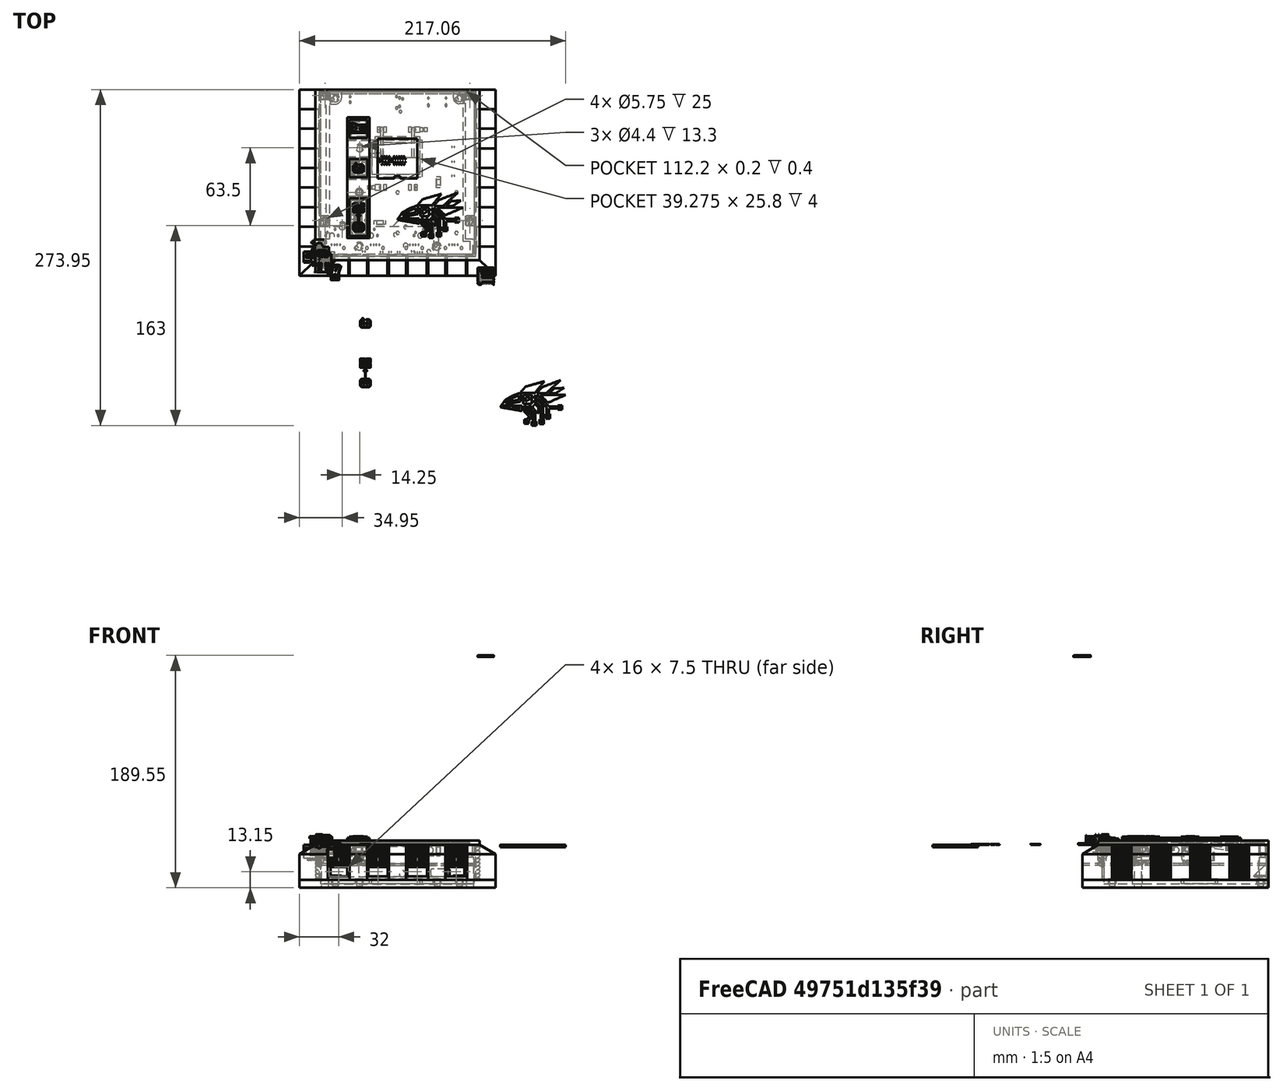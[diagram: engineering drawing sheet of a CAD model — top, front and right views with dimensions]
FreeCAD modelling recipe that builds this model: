
FCSTD DOCUMENT  (FreeCAD 1.0R39109 (Git))
Label: LegoCase_Konnexus_Mk1
License: All rights reserved
LicenseURL: http://en.wikipedia.org/wiki/All_rights_reserved
objects: Sketcher::SketchObject×154, PartDesign::Pad×122, Part::Feature×79, PartDesign::Body×69, App::Part×57, PartDesign::Pocket×45, PartDesign::SubShapeBinder×32, Part::Extrusion×20, Part::Cut×14, TechDraw::DrawViewDimension×11, PartDesign::FeatureBase×10, Mesh::Feature×9, Part::Scale×7, TechDraw::DrawSVGTemplate×6, PartDesign::Plane×6, TechDraw::DrawProjGroupItem×6, TechDraw::DrawPage×6, PartDesign::SubtractiveSphere×4, PartDesign::Groove×3, PartDesign::SubtractiveCylinder×3, +4 more types
note: 1118 computed .brp shape members not serialized (recipe doc carries the construction recipe); baked Part::Feature solids carry a one-line shape summary decoded from their .brp

FEATURE [Sketcher::SketchObject] Sketch
  ArcFitTolerance = 1e-06
  AttachmentSupport = -> [XY_Plane]
  FullyConstrained = true
  MakeInternals = false
  MapMode = 5
  sketch-geometry (4):
    g0: LineSegment StartX=0 StartY=0 StartZ=0 EndX=127.8 EndY=0 EndZ=0
    g1: LineSegment StartX=127.8 StartY=0 StartZ=0 EndX=127.8 EndY=135.8 EndZ=0
    g2: LineSegment StartX=127.8 StartY=135.8 StartZ=0 EndX=0 EndY=135.8 EndZ=0
    g3: LineSegment StartX=0 StartY=135.8 StartZ=0 EndX=0 EndY=0 EndZ=0
  constraints (11):
    c: Coincident(g0,g1)
    c: Coincident(g1,g2)
    c: Coincident(g2,g3)
    c: Coincident(g3,g0)
    c: Horizontal(g0)
    c: Horizontal(g2)
    c: Vertical(g1)
    c: Vertical(g3)
    c: Distance(g1,g3) = 127.8
    c: Distance(g0,g2) = 135.8
    c: Coincident(g0,g-1)
FEATURE [PartDesign::Pad] Pad
  Direction = (0,0,1)
  Length = 3.2
  Length2 = 10
  Profile = -> Sketch
  ReferenceAxis = -> Sketch [N_Axis]
  Refine = true
  Suppressed = false
  Type = 0
FEATURE [Sketcher::SketchObject] Sketch001
  ArcFitTolerance = 1e-06
  AttachmentSupport = -> [Pad]
  ExternalGeometry = -> [Pad]
  FullyConstrained = true
  MakeInternals = false
  MapMode = 5
  Placement = pos=(0,0,3.2) rot=(0,0,1;0rad)
  sketch-geometry (26):
    g0: LineSegment [constr] StartX=48 StartY=63.8 StartZ=0 EndX=79.8 EndY=63.8 EndZ=0
    g1: LineSegment [constr] StartX=79.8 StartY=63.8 StartZ=0 EndX=79.8 EndY=95.6 EndZ=0
    g2: LineSegment [constr] StartX=79.8 StartY=95.6 StartZ=0 EndX=48 EndY=95.6 EndZ=0
    g3: LineSegment [constr] StartX=48 StartY=95.6 StartZ=0 EndX=48 EndY=63.8 EndZ=0
    g4: LineSegment [constr] StartX=48 StartY=95.6 StartZ=0 EndX=79.8 EndY=63.8 EndZ=0
    g5: LineSegment [constr] StartX=48 StartY=63.8 StartZ=0 EndX=79.8 EndY=95.6 EndZ=0
    g6: GeomPoint [constr] X=63.9 Y=79.7 Z=0
    g7: LineSegment StartX=47.85 StartY=95.75 StartZ=0 EndX=47.85 EndY=63.65 EndZ=0
    g8: LineSegment StartX=47.85 StartY=63.65 StartZ=0 EndX=79.95 EndY=63.65 EndZ=0
    g9: LineSegment StartX=79.95 StartY=63.65 StartZ=0 EndX=79.95 EndY=95.75 EndZ=0
    g10: LineSegment StartX=79.95 StartY=95.75 StartZ=0 EndX=47.85 EndY=95.75 EndZ=0
    g11: LineSegment [constr] StartX=47.85 StartY=95.75 StartZ=0 EndX=79.95 EndY=63.65 EndZ=0
    g12: LineSegment [constr] StartX=47.85 StartY=63.65 StartZ=0 EndX=79.95 EndY=95.75 EndZ=0
    g13: LineSegment [constr] StartX=63.9 StartY=135.8 StartZ=0 EndX=63.9 EndY=0 EndZ=0
    g14: LineSegment StartX=24 StartY=111.8 StartZ=0 EndX=24 EndY=95.8 EndZ=0
    g15: LineSegment StartX=24 StartY=95.8 StartZ=0 EndX=40 EndY=95.8 EndZ=0
    g16: LineSegment StartX=40 StartY=95.8 StartZ=0 EndX=40 EndY=111.8 EndZ=0
    g17: LineSegment StartX=40 StartY=111.8 StartZ=0 EndX=24 EndY=111.8 EndZ=0
    g18: LineSegment StartX=24 StartY=79.8 StartZ=0 EndX=24 EndY=63.8 EndZ=0
    g19: LineSegment StartX=24 StartY=63.8 StartZ=0 EndX=40 EndY=63.8 EndZ=0
    g20: LineSegment StartX=40 StartY=63.8 StartZ=0 EndX=40 EndY=79.8 EndZ=0
    g21: LineSegment StartX=40 StartY=79.8 StartZ=0 EndX=24 EndY=79.8 EndZ=0
    g22: LineSegment StartX=24 StartY=47.8 StartZ=0 EndX=24 EndY=15.8 EndZ=0
    g23: LineSegment StartX=24 StartY=15.8 StartZ=0 EndX=40 EndY=15.8 EndZ=0
    g24: LineSegment StartX=40 StartY=15.8 StartZ=0 EndX=40 EndY=47.8 EndZ=0
    g25: LineSegment StartX=40 StartY=47.8 StartZ=0 EndX=24 EndY=47.8 EndZ=0
  constraints (72):
    c: Coincident(g0,g1)
    c: Coincident(g1,g2)
    c: Coincident(g2,g3)
    c: Coincident(g3,g0)
    c: Horizontal(g0)
    c: Horizontal(g2)
    c: Vertical(g1)
    c: Vertical(g3)
    c: Distance(g1,g3) = 31.8
    c: Distance(g0,g2) = 31.8
    c: Coincident(g4,g2)
    c: Coincident(g4,g0)
    c: Coincident(g5,g0)
    c: Coincident(g5,g1)
    c: PointOnObject(g6,g4)
    c: PointOnObject(g6,g5)
    c: Coincident(g7,g8)
    c: Coincident(g8,g9)
    c: Coincident(g9,g10)
    c: Coincident(g10,g7)
    c: Vertical(g7)
    c: Vertical(g9)
    c: Horizontal(g8)
    c: Horizontal(g10)
    c: Distance(g7,g9) = 32.1
    c: Distance(g8,g10) = 32.1
    c: Coincident(g11,g7)
    c: Coincident(g11,g8)
    c: Coincident(g12,g7)
    c: Coincident(g12,g9)
    c: PointOnObject(g6,g12)
    c: PointOnObject(g6,g11)
    c: Symmetric(g-3,g-3,g13)
    c: Symmetric(g-4,g-4,g13)
    c: PointOnObject(g6,g13)
    c: DistanceY(g-1,g0) = 63.8
    c: Coincident(g14,g15)
    c: Coincident(g15,g16)
    c: Coincident(g16,g17)
    c: Coincident(g17,g14)
    c: Vertical(g14)
    c: Vertical(g16)
    c: Horizontal(g15)
    c: Horizontal(g17)
    c: Distance(g14,g16) = 16
    c: Distance(g15,g17) = 16
    c: DistanceX(g-3,g14) = 24
    c: DistanceY(g14,g-3) = 24
    c: Coincident(g18,g19)
    c: Coincident(g19,g20)
    c: Coincident(g20,g21)
    c: Coincident(g21,g18)
    c: Vertical(g18)
    c: Vertical(g20)
    c: Horizontal(g19)
    c: Horizontal(g21)
    c: Distance(g18,g20) = 16
    c: Distance(g19,g21) = 16
    c: PointOnObject(g18,g14)
    c: DistanceY(g18,g14) = 16
    c: Coincident(g22,g23)
    c: Coincident(g23,g24)
    c: Coincident(g24,g25)
    c: Coincident(g25,g22)
    c: Vertical(g22)
    c: Vertical(g24)
    c: Horizontal(g23)
    c: Horizontal(g25)
    c: Distance(g22,g24) = 16
    c: Distance(g23,g25) = 32
    c: PointOnObject(g22,g18)
    c: DistanceY(g22,g18) = 16
FEATURE [PartDesign::Pocket] Pocket
  BaseFeature = -> Pad
  Direction = (0,0,-1)
  Length = 5
  Length2 = 5
  Profile = -> Sketch001
  ReferenceAxis = -> Sketch001 [N_Axis]
  Refine = true
  Suppressed = false
  Type = 0
FEATURE [PartDesign::SubShapeBinder] Binder
  BindCopyOnChange = 0
  BindMode = 0
  ClaimChildren = false
  Context = -> Part001 [Body001.Binder.]
  Fuse = false
  MakeFace = true
  OffsetFill = false
  OffsetIntersection = false
  OffsetJoinType = 0
  OffsetOpenResult = false
  PartialLoad = false
  Refine = true
  Relative = true
  Support = -> [Body]
  _Version = 2
FEATURE [Sketcher::SketchObject] Sketch002
  ArcFitTolerance = 1e-06
  AttachmentSupport = -> [Binder]
  ExternalGeometry = -> [Binder]
  FullyConstrained = true
  MakeInternals = false
  MapMode = 5
  Placement = pos=(0,0,-7.05e-14) rot=(1,0,0;3.14159rad)
  sketch-geometry (8):
    g0: LineSegment StartX=0 StartY=0 StartZ=0 EndX=0 EndY=-135.8 EndZ=0
    g1: LineSegment StartX=0 StartY=-135.8 StartZ=0 EndX=127.8 EndY=-135.8 EndZ=0
    g2: LineSegment StartX=127.8 StartY=-135.8 StartZ=0 EndX=127.8 EndY=0 EndZ=0
    g3: LineSegment StartX=127.8 StartY=0 StartZ=0 EndX=0 EndY=0 EndZ=0
    g4: LineSegment StartX=1.4 StartY=-1.4 StartZ=0 EndX=1.4 EndY=-134.4 EndZ=0
    g5: LineSegment StartX=1.4 StartY=-134.4 StartZ=0 EndX=126.4 EndY=-134.4 EndZ=0
    g6: LineSegment StartX=126.4 StartY=-134.4 StartZ=0 EndX=126.4 EndY=-1.4 EndZ=0
    g7: LineSegment StartX=126.4 StartY=-1.4 StartZ=0 EndX=1.4 EndY=-1.4 EndZ=0
  constraints (22):
    c: Coincident(g0,g1)
    c: Coincident(g1,g2)
    c: Coincident(g2,g3)
    c: Coincident(g3,g0)
    c: Vertical(g0)
    c: Vertical(g2)
    c: Horizontal(g1)
    c: Horizontal(g3)
    c: Coincident(g0,g-1)
    c: Coincident(g1,g-3)
    c: Coincident(g4,g5)
    c: Coincident(g5,g6)
    c: Coincident(g6,g7)
    c: Coincident(g7,g4)
    c: Vertical(g4)
    c: Vertical(g6)
    c: Horizontal(g5)
    c: Horizontal(g7)
    c: DistanceX(g0,g4) = 1.4
    c: DistanceY(g6,g2) = 1.4
    c: DistanceX(g5,g1) = 1.4
    c: DistanceY(g0,g4) = 1.4
FEATURE [PartDesign::Pad] Pad001
  Direction = (0,0,-1)
  Length = 32
  Length2 = 10
  Profile = -> Sketch002
  ReferenceAxis = -> Sketch002 [N_Axis]
  Refine = true
  Suppressed = false
  Type = 0
FEATURE [Sketcher::SketchObject] Sketch003
  ArcFitTolerance = 1e-06
  AttachmentSupport = -> [Pad001]
  ExternalGeometry = -> [Pad001]
  FullyConstrained = true
  MakeInternals = false
  MapMode = 5
  Placement = pos=(0,0,-32) rot=(1,0,0;3.14159rad)
  sketch-geometry (4):
    g0: LineSegment StartX=0 StartY=0 StartZ=0 EndX=0 EndY=-135.8 EndZ=0
    g1: LineSegment StartX=0 StartY=-135.8 StartZ=0 EndX=127.8 EndY=-135.8 EndZ=0
    g2: LineSegment StartX=127.8 StartY=-135.8 StartZ=0 EndX=127.8 EndY=0 EndZ=0
    g3: LineSegment StartX=127.8 StartY=0 StartZ=0 EndX=0 EndY=0 EndZ=0
  constraints (10):
    c: Coincident(g0,g1)
    c: Coincident(g1,g2)
    c: Coincident(g2,g3)
    c: Coincident(g3,g0)
    c: Vertical(g0)
    c: Vertical(g2)
    c: Horizontal(g1)
    c: Horizontal(g3)
    c: Coincident(g0,g-1)
    c: Coincident(g1,g-3)
FEATURE [PartDesign::Pad] Pad002
  BaseFeature = -> Pad001
  Direction = (0,0,-1)
  Length = 3.2
  Length2 = 10
  Profile = -> Sketch003
  ReferenceAxis = -> Sketch003 [N_Axis]
  Refine = true
  Suppressed = false
  Type = 0
FEATURE [Sketcher::SketchObject] Sketch004
  ArcFitTolerance = 1e-06
  AttachmentSupport = -> [Pad002]
  ExternalGeometry = -> [Pad002]
  FullyConstrained = true
  MakeInternals = false
  MapMode = 5
  Placement = pos=(0,0,-35.2) rot=(1,0,0;3.14159rad)
  sketch-geometry (14):
    g0: LineSegment [constr] StartX=0 StartY=0 StartZ=0 EndX=127.8 EndY=-135.8 EndZ=0
    g1: LineSegment [constr] StartX=127.8 StartY=0 StartZ=0 EndX=-4.4e-15 EndY=-135.8 EndZ=0
    g2: LineSegment StartX=0 StartY=0 StartZ=0 EndX=-4.4e-15 EndY=-135.8 EndZ=0
    g3: LineSegment StartX=127.8 StartY=-135.8 StartZ=0 EndX=127.8 EndY=0 EndZ=0
    g4: LineSegment StartX=-16 StartY=16 StartZ=0 EndX=-16 EndY=-135.8 EndZ=0
    g5: LineSegment StartX=143.8 StartY=-135.8 StartZ=0 EndX=143.8 EndY=16 EndZ=0
    g6: LineSegment [constr] StartX=-16 StartY=16 StartZ=0 EndX=143.8 EndY=-135.8 EndZ=0
    g7: LineSegment [constr] StartX=143.8 StartY=16 StartZ=0 EndX=-16 EndY=-135.8 EndZ=0
    g8: GeomPoint [constr] X=63.9 Y=-67.9 Z=0
    g9: GeomPoint X=63.9 Y=-59.9 Z=0
    g10: LineSegment StartX=-16 StartY=-135.8 StartZ=0 EndX=-3.6e-15 EndY=-135.8 EndZ=0
    g11: LineSegment StartX=127.8 StartY=-135.8 StartZ=0 EndX=143.8 EndY=-135.8 EndZ=0
    g12: LineSegment StartX=-16 StartY=16 StartZ=0 EndX=143.8 EndY=16 EndZ=0
    g13: LineSegment StartX=0 StartY=0 StartZ=0 EndX=127.8 EndY=0 EndZ=0
  constraints (32):
    c: Coincident(g0,g-1)
    c: Coincident(g0,g-3)
    c: Coincident(g1,g-3)
    c: Coincident(g1,g-4)
    c: Coincident(g2,g0)
    c: Vertical(g4)
    c: Vertical(g5)
    c: DistanceY(g4,g4) = 151.8
    c: Coincident(g7,g5)
    c: Coincident(g7,g4)
    c: PointOnObject(g8,g0)
    c: PointOnObject(g8,g1)
    c: PointOnObject(g9,g7)
    c: PointOnObject(g9,g6)
    c: Vertical(g9,g8)
    c: Coincident(g6,g4)
    c: DistanceX(g4,g5) = 159.8
    c: Coincident(g3,g1)
    c: Coincident(g6,g5)
    c: Coincident(g10,g4)
    c: Coincident(g10,g2)
    c: Coincident(g11,g3)
    c: Coincident(g11,g5)
    c: Horizontal(g10)
    c: Coincident(g1,g2)
    c: Horizontal(g11)
    c: Coincident(g12,g4)
    c: Coincident(g12,g5)
    c: Horizontal(g12)
    c: Coincident(g3,g0)
    c: Coincident(g13,g0)
    c: Coincident(g13,g1)
FEATURE [PartDesign::Pad] Pad003
  BaseFeature = -> Pad002
  Direction = (0,0,-1)
  Length = 6.4
  Length2 = 10
  Profile = -> Sketch004
  ReferenceAxis = -> Sketch004 [N_Axis]
  Refine = true
  Reversed = true
  Suppressed = false
  Type = 0
FEATURE [Sketcher::SketchObject] Sketch005
  ArcFitTolerance = 1e-06
  AttachmentSupport = -> [Pad003]
  ExternalGeometry = -> [Pad003]
  FullyConstrained = true
  MakeInternals = false
  MapMode = 5
  Placement = pos=(0,0,-28.8) rot=(0,0,1;0rad)
  sketch-geometry (32):
    g0: LineSegment StartX=127.8 StartY=24 StartZ=0 EndX=127.8 EndY=8 EndZ=0
    g1: LineSegment StartX=127.8 StartY=8 StartZ=0 EndX=143.8 EndY=8 EndZ=0
    g2: LineSegment StartX=143.8 StartY=8 StartZ=0 EndX=143.8 EndY=24 EndZ=0
    g3: LineSegment StartX=143.8 StartY=24 StartZ=0 EndX=127.8 EndY=24 EndZ=0
    g4: LineSegment StartX=127.8 StartY=56 StartZ=0 EndX=127.8 EndY=40 EndZ=0
    g5: LineSegment StartX=127.8 StartY=40 StartZ=0 EndX=143.8 EndY=40 EndZ=0
    g6: LineSegment StartX=143.8 StartY=40 StartZ=0 EndX=143.8 EndY=56 EndZ=0
    g7: LineSegment StartX=143.8 StartY=56 StartZ=0 EndX=127.8 EndY=56 EndZ=0
    g8: LineSegment StartX=127.8 StartY=88 StartZ=0 EndX=127.8 EndY=72 EndZ=0
    g9: LineSegment StartX=127.8 StartY=72 StartZ=0 EndX=143.8 EndY=72 EndZ=0
    g10: LineSegment StartX=143.8 StartY=72 StartZ=0 EndX=143.8 EndY=88 EndZ=0
    g11: LineSegment StartX=143.8 StartY=88 StartZ=0 EndX=127.8 EndY=88 EndZ=0
    g12: LineSegment StartX=127.8 StartY=120 StartZ=0 EndX=127.8 EndY=104 EndZ=0
    g13: LineSegment StartX=127.8 StartY=104 StartZ=0 EndX=143.8 EndY=104 EndZ=0
    g14: LineSegment StartX=143.8 StartY=104 StartZ=0 EndX=143.8 EndY=120 EndZ=0
    g15: LineSegment StartX=143.8 StartY=120 StartZ=0 EndX=127.8 EndY=120 EndZ=0
    g16: LineSegment StartX=-3.6e-15 StartY=120 StartZ=0 EndX=-16 EndY=120 EndZ=0
    g17: LineSegment StartX=-16 StartY=120 StartZ=0 EndX=-16 EndY=104 EndZ=0
    g18: LineSegment StartX=-16 StartY=104 StartZ=0 EndX=-3.6e-15 EndY=104 EndZ=0
    g19: LineSegment StartX=-3.6e-15 StartY=104 StartZ=0 EndX=-3.6e-15 EndY=120 EndZ=0
    g20: LineSegment StartX=-3.6e-15 StartY=88 StartZ=0 EndX=-16 EndY=88 EndZ=0
    g21: LineSegment StartX=-16 StartY=88 StartZ=0 EndX=-16 EndY=72 EndZ=0
    g22: LineSegment StartX=-16 StartY=72 StartZ=0 EndX=-3.6e-15 EndY=72 EndZ=0
    g23: LineSegment StartX=-3.6e-15 StartY=72 StartZ=0 EndX=-3.6e-15 EndY=88 EndZ=0
    g24: LineSegment StartX=-16 StartY=56 StartZ=0 EndX=-16 EndY=40 EndZ=0
    g25: LineSegment StartX=-16 StartY=40 StartZ=0 EndX=0 EndY=40 EndZ=0
    g26: LineSegment StartX=0 StartY=24 StartZ=0 EndX=-16 EndY=24 EndZ=0
    g27: LineSegment StartX=-16 StartY=24 StartZ=0 EndX=-16 EndY=8 EndZ=0
    g28: LineSegment StartX=-16 StartY=8 StartZ=0 EndX=0 EndY=8 EndZ=0
    g29: LineSegment StartX=0 StartY=8 StartZ=0 EndX=0 EndY=24 EndZ=0
    g30: LineSegment StartX=-16 StartY=56 StartZ=0 EndX=0 EndY=56 EndZ=0
    g31: LineSegment StartX=0 StartY=56 StartZ=0 EndX=0 EndY=40 EndZ=0
  constraints (96):
    c: Coincident(g0,g1)
    c: Coincident(g1,g2)
    c: Coincident(g2,g3)
    c: Coincident(g3,g0)
    c: Vertical(g0)
    c: Vertical(g2)
    c: Horizontal(g1)
    c: Horizontal(g3)
    c: PointOnObject(g0,g-5)
    c: PointOnObject(g1,g-4)
    c: DistanceY(g2,g2) = 16
    c: DistanceY(g-4,g1) = 24
    c: Coincident(g4,g5)
    c: Coincident(g5,g6)
    c: Coincident(g6,g7)
    c: Coincident(g7,g4)
    c: Vertical(g4)
    c: Vertical(g6)
    c: Horizontal(g5)
    c: Horizontal(g7)
    c: PointOnObject(g4,g-5)
    c: PointOnObject(g5,g-4)
    c: DistanceY(g6,g6) = 16
    c: DistanceY(g2,g5) = 16
    c: Coincident(g8,g9)
    c: Coincident(g9,g10)
    c: Coincident(g10,g11)
    c: Coincident(g11,g8)
    c: Vertical(g8)
    c: Vertical(g10)
    c: Horizontal(g9)
    c: Horizontal(g11)
    c: PointOnObject(g8,g-5)
    c: PointOnObject(g9,g-4)
    c: DistanceY(g10,g10) = 16
    c: DistanceY(g6,g9) = 16
    c: Coincident(g12,g13)
    c: Coincident(g13,g14)
    c: Coincident(g14,g15)
    c: Coincident(g15,g12)
    c: Vertical(g12)
    c: Vertical(g14)
    c: Horizontal(g13)
    c: Horizontal(g15)
    c: PointOnObject(g12,g-5)
    c: PointOnObject(g13,g-4)
    c: DistanceY(g14,g14) = 16
    c: DistanceY(g10,g13) = 16
    c: Coincident(g16,g17)
    c: Coincident(g17,g18)
    c: Coincident(g18,g19)
    c: Coincident(g19,g16)
    c: Horizontal(g16)
    c: Horizontal(g18)
    c: Vertical(g17)
    c: Vertical(g19)
    c: PointOnObject(g16,g-6)
    c: PointOnObject(g17,g-3)
    c: Coincident(g20,g21)
    c: Coincident(g21,g22)
    c: Coincident(g22,g23)
    c: Coincident(g23,g20)
    c: Horizontal(g20)
    c: Horizontal(g22)
    c: Vertical(g21)
    c: Vertical(g23)
    c: PointOnObject(g20,g-6)
    c: PointOnObject(g21,g-3)
    c: Coincident(g24,g25)
    c: Horizontal(g25)
    c: Vertical(g24)
    c: PointOnObject(g24,g-3)
    c: Coincident(g26,g27)
    c: Coincident(g27,g28)
    c: Coincident(g28,g29)
    c: Coincident(g29,g26)
    c: Horizontal(g26)
    c: Horizontal(g28)
    c: Vertical(g27)
    c: Vertical(g29)
    c: PointOnObject(g26,g-6)
    c: PointOnObject(g27,g-3)
    c: DistanceY(g27,g27) = 16
    c: DistanceY(g24,g24) = 16
    c: DistanceY(g21,g21) = 16
    c: DistanceY(g17,g17) = 16
    c: PointOnObject(g28,g1)
    c: PointOnObject(g25,g5)
    c: Coincident(g30,g24)
    c: PointOnObject(g30,g-6)
    c: Horizontal(g30)
    c: Coincident(g31,g30)
    c: Coincident(g31,g25)
    c: Vertical(g31)
    c: PointOnObject(g22,g9)
    c: PointOnObject(g18,g13)
FEATURE [PartDesign::Pad] Pad004
  BaseFeature = -> Pad003
  Direction = (0,0,1)
  Length = 19.2
  Length2 = 10
  Profile = -> Sketch005
  ReferenceAxis = -> Sketch005 [N_Axis]
  Refine = true
  Suppressed = false
  Type = 0
FEATURE [PartDesign::SubShapeBinder] Binder001
  BindCopyOnChange = 0
  BindMode = 0
  ClaimChildren = false
  Context = -> Part001 [Body002.Binder001.]
  Fuse = false
  MakeFace = true
  OffsetFill = false
  OffsetIntersection = false
  OffsetJoinType = 0
  OffsetOpenResult = false
  PartialLoad = false
  Refine = true
  Relative = true
  Support = -> [Body001]
  _Version = 2
FEATURE [Sketcher::SketchObject] Sketch006
  ArcFitTolerance = 1e-06
  AttachmentSupport = -> [Binder001]
  ExternalGeometry = -> [Binder001]
  FullyConstrained = true
  MakeInternals = false
  MapMode = 5
  Placement = pos=(0,0,-28.8) rot=(0,0,1;0rad)
  sketch-geometry (4):
    g0: LineSegment StartX=143.8 StartY=135.8 StartZ=0 EndX=127.8 EndY=135.8 EndZ=0
    g1: LineSegment StartX=127.8 StartY=135.8 StartZ=0 EndX=127.8 EndY=120 EndZ=0
    g2: LineSegment StartX=127.8 StartY=120 StartZ=0 EndX=143.8 EndY=120 EndZ=0
    g3: LineSegment StartX=143.8 StartY=120 StartZ=0 EndX=143.8 EndY=135.8 EndZ=0
  constraints (10):
    c: Coincident(g0,g1)
    c: Coincident(g1,g2)
    c: Coincident(g2,g3)
    c: Coincident(g3,g0)
    c: Horizontal(g0)
    c: Horizontal(g2)
    c: Vertical(g1)
    c: Vertical(g3)
    c: Coincident(g0,g-4)
    c: Coincident(g1,g-3)
FEATURE [PartDesign::Pad] Pad005
  Direction = (0,0,1)
  Length = 28.8
  Length2 = 10
  Profile = -> Sketch006
  ReferenceAxis = -> Sketch006 [N_Axis]
  Refine = true
  Suppressed = false
  Type = 0
FEATURE [Sketcher::SketchObject] Sketch007
  ArcFitTolerance = 1e-06
  AttachmentSupport = -> [Pad005]
  ExternalGeometry = -> [Pad005]
  FullyConstrained = true
  MakeInternals = false
  MapMode = 5
  Placement = pos=(0,120,0) rot=(1,0,0;1.5708rad)
  sketch-geometry (4):
    g0: LineSegment [constr] StartX=143.8 StartY=-9.6 StartZ=0 EndX=127.8 EndY=-9.6 EndZ=0
    g1: LineSegment StartX=127.8 StartY=-3.6e-15 StartZ=0 EndX=143.8 EndY=-9.6 EndZ=0
    g2: LineSegment StartX=127.8 StartY=-3.6e-15 StartZ=0 EndX=143.8 EndY=-3.6e-15 EndZ=0
    g3: LineSegment StartX=143.8 StartY=-3.6e-15 StartZ=0 EndX=143.8 EndY=-9.6 EndZ=0
  constraints (10):
    c: PointOnObject(g0,g-3)
    c: PointOnObject(g0,g-5)
    c: Horizontal(g0)
    c: Coincident(g1,g-5)
    c: Coincident(g1,g0)
    c: Coincident(g2,g1)
    c: Coincident(g2,g-4)
    c: Coincident(g3,g2)
    c: Coincident(g3,g0)
    c: DistanceY(g3,g3) = 9.6
FEATURE [PartDesign::Pocket] Pocket001
  BaseFeature = -> Pad005
  Direction = (0,1,-2e-16)
  Length = 16
  Length2 = 5
  Profile = -> Sketch007
  ReferenceAxis = -> Sketch007 [N_Axis]
  Refine = true
  Suppressed = false
  Type = 0
FEATURE [PartDesign::SubShapeBinder] Binder002
  BindCopyOnChange = 0
  BindMode = 0
  ClaimChildren = false
  Context = -> Part001 [Body003.Binder002.]
  Fuse = false
  MakeFace = true
  OffsetFill = false
  OffsetIntersection = false
  OffsetJoinType = 0
  OffsetOpenResult = false
  PartialLoad = false
  Refine = true
  Relative = true
  Support = -> [Body001]
  _Version = 2
FEATURE [Sketcher::SketchObject] Sketch008
  ArcFitTolerance = 1e-06
  AttachmentSupport = -> [Binder002]
  ExternalGeometry = -> [Binder002]
  FullyConstrained = true
  MakeInternals = false
  MapMode = 5
  Placement = pos=(0,0,-28.8) rot=(0,0,1;0rad)
  sketch-geometry (4):
    g0: LineSegment StartX=127.8 StartY=104 StartZ=0 EndX=127.8 EndY=88 EndZ=0
    g1: LineSegment StartX=127.8 StartY=88 StartZ=0 EndX=143.8 EndY=88 EndZ=0
    g2: LineSegment StartX=143.8 StartY=88 StartZ=0 EndX=143.8 EndY=104 EndZ=0
    g3: LineSegment StartX=143.8 StartY=104 StartZ=0 EndX=127.8 EndY=104 EndZ=0
  constraints (10):
    c: Coincident(g0,g1)
    c: Coincident(g1,g2)
    c: Coincident(g2,g3)
    c: Coincident(g3,g0)
    c: Vertical(g0)
    c: Vertical(g2)
    c: Horizontal(g1)
    c: Horizontal(g3)
    c: Coincident(g0,g-3)
    c: Coincident(g1,g-4)
FEATURE [PartDesign::Pad] Pad006
  Direction = (0,0,1)
  Length = 28.8
  Length2 = 10
  Profile = -> Sketch008
  ReferenceAxis = -> Sketch008 [N_Axis]
  Refine = true
  Suppressed = false
  Type = 0
FEATURE [Sketcher::SketchObject] Sketch009
  ArcFitTolerance = 1e-06
  AttachmentSupport = -> [Pad006]
  ExternalGeometry = -> [Pad006]
  FullyConstrained = true
  MakeInternals = false
  MapMode = 5
  Placement = pos=(0,88,0) rot=(1,0,0;1.5708rad)
  sketch-geometry (4):
    g0: LineSegment [constr] StartX=143.8 StartY=-9.6 StartZ=0 EndX=127.8 EndY=-9.6 EndZ=0
    g1: LineSegment StartX=143.8 StartY=-9.6 StartZ=0 EndX=127.8 EndY=-6.2e-15 EndZ=0
    g2: LineSegment StartX=127.8 StartY=-6.2e-15 StartZ=0 EndX=143.8 EndY=-3.6e-15 EndZ=0
    g3: LineSegment StartX=143.8 StartY=-3.6e-15 StartZ=0 EndX=143.8 EndY=-9.6 EndZ=0
  constraints (10):
    c: PointOnObject(g0,g-4)
    c: PointOnObject(g0,g-3)
    c: Horizontal(g0)
    c: Coincident(g0,g1)
    c: Coincident(g1,g-3)
    c: Coincident(g1,g2)
    c: Coincident(g2,g-4)
    c: Coincident(g2,g3)
    c: Coincident(g3,g1)
    c: DistanceY(g3,g3) = 9.6
FEATURE [PartDesign::Pocket] Pocket002
  BaseFeature = -> Pad006
  Direction = (0,1,-2e-16)
  Length = 16
  Length2 = 5
  Profile = -> Sketch009
  ReferenceAxis = -> Sketch009 [N_Axis]
  Refine = true
  Suppressed = false
  Type = 0
FEATURE [PartDesign::SubShapeBinder] Binder003
  BindCopyOnChange = 0
  BindMode = 0
  ClaimChildren = false
  Context = -> Part001 [Body004.Binder003.]
  Fuse = false
  MakeFace = true
  OffsetFill = false
  OffsetIntersection = false
  OffsetJoinType = 0
  OffsetOpenResult = false
  PartialLoad = false
  Refine = true
  Relative = true
  Support = -> [Body001]
  _Version = 2
FEATURE [Sketcher::SketchObject] Sketch010
  ArcFitTolerance = 1e-06
  AttachmentSupport = -> [Binder003]
  ExternalGeometry = -> [Binder003]
  FullyConstrained = true
  MakeInternals = false
  MapMode = 5
  Placement = pos=(0,0,-28.8) rot=(0,0,1;0rad)
  sketch-geometry (4):
    g0: LineSegment StartX=127.8 StartY=72 StartZ=0 EndX=127.8 EndY=56 EndZ=0
    g1: LineSegment StartX=127.8 StartY=56 StartZ=0 EndX=143.8 EndY=56 EndZ=0
    g2: LineSegment StartX=143.8 StartY=56 StartZ=0 EndX=143.8 EndY=72 EndZ=0
    g3: LineSegment StartX=143.8 StartY=72 StartZ=0 EndX=127.8 EndY=72 EndZ=0
  constraints (10):
    c: Coincident(g0,g1)
    c: Coincident(g1,g2)
    c: Coincident(g2,g3)
    c: Coincident(g3,g0)
    c: Vertical(g0)
    c: Vertical(g2)
    c: Horizontal(g1)
    c: Horizontal(g3)
    c: Coincident(g0,g-3)
    c: Coincident(g1,g-4)
FEATURE [PartDesign::Pad] Pad007
  Direction = (0,0,1)
  Length = 28.8
  Length2 = 10
  Profile = -> Sketch010
  ReferenceAxis = -> Sketch010 [N_Axis]
  Refine = true
  Suppressed = false
  Type = 0
FEATURE [Sketcher::SketchObject] Sketch011
  ArcFitTolerance = 1e-06
  AttachmentSupport = -> [Pad007]
  ExternalGeometry = -> [Pad007]
  FullyConstrained = true
  MakeInternals = false
  MapMode = 5
  Placement = pos=(0,56,0) rot=(1,0,0;1.5708rad)
  sketch-geometry (4):
    g0: LineSegment [constr] StartX=143.8 StartY=-9.6 StartZ=0 EndX=127.8 EndY=-9.6 EndZ=0
    g1: LineSegment StartX=143.8 StartY=-9.6 StartZ=0 EndX=127.8 EndY=-6e-16 EndZ=0
    g2: LineSegment StartX=143.8 StartY=-3.6e-15 StartZ=0 EndX=143.8 EndY=-9.6 EndZ=0
    g3: LineSegment StartX=127.8 StartY=-6e-16 StartZ=0 EndX=143.8 EndY=-3.6e-15 EndZ=0
  constraints (10):
    c: PointOnObject(g0,g-4)
    c: PointOnObject(g0,g-3)
    c: Horizontal(g0)
    c: Coincident(g1,g0)
    c: Coincident(g1,g-3)
    c: Coincident(g2,g-4)
    c: Coincident(g2,g0)
    c: Coincident(g3,g1)
    c: Coincident(g3,g2)
    c: DistanceY(g2,g2) = 9.6
FEATURE [PartDesign::Pocket] Pocket003
  BaseFeature = -> Pad007
  Direction = (0,1,-2e-16)
  Length = 16
  Length2 = 5
  Profile = -> Sketch011
  ReferenceAxis = -> Sketch011 [N_Axis]
  Refine = true
  Suppressed = false
  Type = 0
FEATURE [PartDesign::SubShapeBinder] Binder004
  BindCopyOnChange = 0
  BindMode = 0
  ClaimChildren = false
  Context = -> Part001 [Body005.Binder004.]
  Fuse = false
  MakeFace = true
  OffsetFill = false
  OffsetIntersection = false
  OffsetJoinType = 0
  OffsetOpenResult = false
  PartialLoad = false
  Refine = true
  Relative = true
  Support = -> [Body001]
  _Version = 2
FEATURE [Sketcher::SketchObject] Sketch012
  ArcFitTolerance = 1e-06
  AttachmentSupport = -> [Binder004]
  ExternalGeometry = -> [Binder004]
  FullyConstrained = true
  MakeInternals = false
  MapMode = 5
  Placement = pos=(0,0,-28.8) rot=(0,0,1;0rad)
  sketch-geometry (4):
    g0: LineSegment StartX=127.8 StartY=40 StartZ=0 EndX=127.8 EndY=24 EndZ=0
    g1: LineSegment StartX=127.8 StartY=24 StartZ=0 EndX=143.8 EndY=24 EndZ=0
    g2: LineSegment StartX=143.8 StartY=24 StartZ=0 EndX=143.8 EndY=40 EndZ=0
    g3: LineSegment StartX=143.8 StartY=40 StartZ=0 EndX=127.8 EndY=40 EndZ=0
  constraints (10):
    c: Coincident(g0,g1)
    c: Coincident(g1,g2)
    c: Coincident(g2,g3)
    c: Coincident(g3,g0)
    c: Vertical(g0)
    c: Vertical(g2)
    c: Horizontal(g1)
    c: Horizontal(g3)
    c: Coincident(g0,g-3)
    c: Coincident(g1,g-4)
FEATURE [PartDesign::Pad] Pad008
  Direction = (0,0,1)
  Length = 28.8
  Length2 = 10
  Profile = -> Sketch012
  ReferenceAxis = -> Sketch012 [N_Axis]
  Refine = true
  Suppressed = false
  Type = 0
FEATURE [Sketcher::SketchObject] Sketch013
  ArcFitTolerance = 1e-06
  AttachmentSupport = -> [Pad008]
  ExternalGeometry = -> [Pad008]
  FullyConstrained = true
  MakeInternals = false
  MapMode = 5
  Placement = pos=(0,24,0) rot=(1,0,0;1.5708rad)
  sketch-geometry (3):
    g0: LineSegment StartX=143.8 StartY=-9.6 StartZ=0 EndX=127.8 EndY=-4.5e-15 EndZ=0
    g1: LineSegment StartX=127.8 StartY=-4.5e-15 StartZ=0 EndX=143.8 EndY=-3.6e-15 EndZ=0
    g2: LineSegment StartX=143.8 StartY=-3.6e-15 StartZ=0 EndX=143.8 EndY=-9.6 EndZ=0
  constraints (7):
    c: PointOnObject(g0,g-4)
    c: Coincident(g0,g-3)
    c: Coincident(g1,g0)
    c: Coincident(g1,g-4)
    c: Coincident(g2,g1)
    c: DistanceY(g2,g2) = 9.6
    c: Coincident(g0,g2)
FEATURE [PartDesign::Pocket] Pocket004
  BaseFeature = -> Pad008
  Direction = (0,1,-2e-16)
  Length = 16
  Length2 = 5
  Profile = -> Sketch013
  ReferenceAxis = -> Sketch013 [N_Axis]
  Refine = true
  Suppressed = false
  Type = 0
FEATURE [PartDesign::SubShapeBinder] Binder005
  BindCopyOnChange = 0
  BindMode = 0
  ClaimChildren = false
  Context = -> Part001 [Body006.Binder005.]
  Fuse = false
  MakeFace = true
  OffsetFill = false
  OffsetIntersection = false
  OffsetJoinType = 0
  OffsetOpenResult = false
  PartialLoad = false
  Refine = true
  Relative = true
  Support = -> [Body001]
  _Version = 2
FEATURE [Sketcher::SketchObject] Sketch014
  ArcFitTolerance = 1e-06
  AttachmentSupport = -> [Binder005]
  ExternalGeometry = -> [Binder005]
  FullyConstrained = true
  MakeInternals = false
  MapMode = 5
  Placement = pos=(0,0,-28.8) rot=(0,0,1;0rad)
  sketch-geometry (6):
    g0: LineSegment StartX=127.8 StartY=0 StartZ=0 EndX=127.8 EndY=8 EndZ=0
    g1: LineSegment StartX=127.8 StartY=8 StartZ=0 EndX=143.8 EndY=8 EndZ=0
    g2: LineSegment StartX=143.8 StartY=8 StartZ=0 EndX=143.8 EndY=-16 EndZ=0
    g3: LineSegment StartX=143.8 StartY=-16 StartZ=0 EndX=119.8 EndY=-16 EndZ=0
    g4: LineSegment StartX=119.8 StartY=-16 StartZ=0 EndX=119.8 EndY=0 EndZ=0
    g5: LineSegment StartX=119.8 StartY=0 StartZ=0 EndX=127.8 EndY=0 EndZ=0
  constraints (14):
    c: Coincident(g-4,g0)
    c: Coincident(g0,g-4)
    c: Coincident(g0,g1)
    c: Coincident(g1,g-3)
    c: Coincident(g1,g2)
    c: Coincident(g2,g-3)
    c: Coincident(g2,g3)
    c: Horizontal(g3)
    c: Coincident(g3,g4)
    c: PointOnObject(g4,g-1)
    c: Vertical(g4)
    c: Coincident(g4,g5)
    c: Coincident(g5,g0)
    c: Equal(g5,g0)
FEATURE [PartDesign::Pad] Pad009
  Direction = (0,0,1)
  Length = 28.8
  Length2 = 10
  Profile = -> Sketch014
  ReferenceAxis = -> Sketch014 [N_Axis]
  Refine = true
  Suppressed = false
  Type = 0
FEATURE [Sketcher::SketchObject] Sketch015
  ArcFitTolerance = 1e-06
  AttachmentSupport = -> [Pad009]
  ExternalGeometry = -> [Pad009]
  FullyConstrained = true
  MakeInternals = false
  MapMode = 5
  Placement = pos=(119.8,0,0) rot=(0.57735,-0.57735,-0.57735;2.0944rad)
  sketch-geometry (4):
    g0: LineSegment [constr] StartX=16 StartY=-9.6 StartZ=0 EndX=0 EndY=-9.6 EndZ=0
    g1: LineSegment StartX=16 StartY=-9.6 StartZ=0 EndX=3e-16 EndY=-1.3e-15 EndZ=0
    g2: LineSegment StartX=3e-16 StartY=-1.3e-15 StartZ=0 EndX=16 EndY=-3.6e-15 EndZ=0
    g3: LineSegment StartX=16 StartY=-3.6e-15 StartZ=0 EndX=16 EndY=-9.6 EndZ=0
  constraints (10):
    c: PointOnObject(g0,g-3)
    c: PointOnObject(g0,g-4)
    c: Horizontal(g0)
    c: Coincident(g0,g1)
    c: Coincident(g1,g-1)
    c: Coincident(g1,g2)
    c: Coincident(g2,g-3)
    c: Coincident(g2,g3)
    c: Coincident(g3,g1)
    c: DistanceY(g3,g3) = 9.6
FEATURE [PartDesign::Pocket] Pocket005
  BaseFeature = -> Pad009
  Direction = (1,0,0)
  Length = 24
  Length2 = 5
  Profile = -> Sketch015
  ReferenceAxis = -> Sketch015 [N_Axis]
  Refine = true
  Suppressed = false
  Type = 0
FEATURE [Sketcher::SketchObject] Sketch016
  ArcFitTolerance = 1e-06
  AttachmentSupport = -> [Pocket005]
  ExternalGeometry = -> [Pocket005]
  FullyConstrained = true
  MakeInternals = false
  MapMode = 5
  Placement = pos=(0,8,0) rot=(0,0.707107,0.707107;3.14159rad)
  sketch-geometry (4):
    g0: LineSegment [constr] StartX=-143.8 StartY=-9.6 StartZ=0 EndX=-127.8 EndY=-9.6 EndZ=0
    g1: LineSegment StartX=-143.8 StartY=-9.6 StartZ=0 EndX=-127.8 EndY=-4.5e-15 EndZ=0
    g2: LineSegment StartX=-127.8 StartY=-4.5e-15 StartZ=0 EndX=-143.8 EndY=-3.6e-15 EndZ=0
    g3: LineSegment StartX=-143.8 StartY=-3.6e-15 StartZ=0 EndX=-143.8 EndY=-9.6 EndZ=0
  constraints (10):
    c: PointOnObject(g0,g-3)
    c: PointOnObject(g0,g-4)
    c: Horizontal(g0)
    c: Coincident(g1,g0)
    c: Coincident(g1,g-4)
    c: Coincident(g2,g1)
    c: Coincident(g2,g-3)
    c: Coincident(g3,g2)
    c: Coincident(g3,g0)
    c: DistanceY(g3,g3) = 9.6
FEATURE [PartDesign::Pocket] Pocket006
  BaseFeature = -> Pocket005
  Direction = (0,-1,2e-16)
  Length = 24
  Length2 = 5
  Profile = -> Sketch016
  ReferenceAxis = -> Sketch016 [N_Axis]
  Refine = true
  Suppressed = false
  Type = 0
FEATURE [PartDesign::SubShapeBinder] Binder006
  BindCopyOnChange = 0
  BindMode = 0
  ClaimChildren = false
  Context = -> Part001 [Body007.Binder006.]
  Fuse = false
  MakeFace = true
  OffsetFill = false
  OffsetIntersection = false
  OffsetJoinType = 0
  OffsetOpenResult = false
  PartialLoad = false
  Refine = true
  Relative = true
  Support = -> [Body001]
  _Version = 2
FEATURE [Sketcher::SketchObject] Sketch017
  ArcFitTolerance = 1e-06
  AttachmentSupport = -> [Binder006]
  ExternalGeometry = -> [Binder006]
  FullyConstrained = true
  MakeInternals = false
  MapMode = 5
  Placement = pos=(0,0,-28.8) rot=(0,0,1;0rad)
  sketch-geometry (4):
    g0: LineSegment StartX=0 StartY=135.8 StartZ=0 EndX=-16 EndY=135.8 EndZ=0
    g1: LineSegment StartX=-16 StartY=135.8 StartZ=0 EndX=-16 EndY=120 EndZ=0
    g2: LineSegment StartX=-16 StartY=120 StartZ=0 EndX=0 EndY=120 EndZ=0
    g3: LineSegment StartX=0 StartY=120 StartZ=0 EndX=0 EndY=135.8 EndZ=0
  constraints (10):
    c: Coincident(g0,g1)
    c: Coincident(g1,g2)
    c: Coincident(g2,g3)
    c: Coincident(g3,g0)
    c: Horizontal(g0)
    c: Horizontal(g2)
    c: Vertical(g1)
    c: Vertical(g3)
    c: Coincident(g0,g-3)
    c: Coincident(g1,g-4)
FEATURE [PartDesign::Pad] Pad010
  Direction = (0,0,1)
  Length = 28.8
  Length2 = 10
  Profile = -> Sketch017
  ReferenceAxis = -> Sketch017 [N_Axis]
  Refine = true
  Suppressed = false
  Type = 0
FEATURE [Sketcher::SketchObject] Sketch018
  ArcFitTolerance = 1e-06
  AttachmentSupport = -> [Pad010]
  ExternalGeometry = -> [Pad010]
  FullyConstrained = true
  MakeInternals = false
  MapMode = 5
  Placement = pos=(0,120,0) rot=(1,0,0;1.5708rad)
  sketch-geometry (3):
    g0: LineSegment StartX=0 StartY=0 StartZ=0 EndX=-16 EndY=-9.6 EndZ=0
    g1: LineSegment StartX=-16 StartY=-9.6 StartZ=0 EndX=-16 EndY=-3.6e-15 EndZ=0
    g2: LineSegment StartX=-16 StartY=-3.6e-15 StartZ=0 EndX=0 EndY=0 EndZ=0
  constraints (7):
    c: PointOnObject(g0,g-3)
    c: Coincident(g0,g-1)
    c: Coincident(g1,g-3)
    c: Coincident(g2,g1)
    c: Coincident(g2,g0)
    c: DistanceY(g1,g1) = 9.6
    c: Coincident(g0,g1)
FEATURE [PartDesign::Pocket] Pocket007
  BaseFeature = -> Pad010
  Direction = (0,1,-2e-16)
  Length = 16
  Length2 = 5
  Profile = -> Sketch018
  ReferenceAxis = -> Sketch018 [N_Axis]
  Refine = true
  Suppressed = false
  Type = 0
FEATURE [PartDesign::SubShapeBinder] Binder007
  BindCopyOnChange = 0
  BindMode = 0
  ClaimChildren = false
  Context = -> Part001 [Body008.Binder007.]
  Fuse = false
  MakeFace = true
  OffsetFill = false
  OffsetIntersection = false
  OffsetJoinType = 0
  OffsetOpenResult = false
  PartialLoad = false
  Refine = true
  Relative = true
  Support = -> [Body001]
  _Version = 2
FEATURE [Sketcher::SketchObject] Sketch019
  ArcFitTolerance = 1e-06
  AttachmentSupport = -> [Binder007]
  ExternalGeometry = -> [Binder007]
  FullyConstrained = true
  MakeInternals = false
  MapMode = 5
  Placement = pos=(0,0,-28.8) rot=(0,0,1;0rad)
  sketch-geometry (4):
    g0: LineSegment StartX=0 StartY=104 StartZ=0 EndX=-16 EndY=104 EndZ=0
    g1: LineSegment StartX=-16 StartY=104 StartZ=0 EndX=-16 EndY=88 EndZ=0
    g2: LineSegment StartX=-16 StartY=88 StartZ=0 EndX=0 EndY=88 EndZ=0
    g3: LineSegment StartX=0 StartY=88 StartZ=0 EndX=0 EndY=104 EndZ=0
  constraints (10):
    c: Coincident(g0,g1)
    c: Coincident(g1,g2)
    c: Coincident(g2,g3)
    c: Coincident(g3,g0)
    c: Horizontal(g0)
    c: Horizontal(g2)
    c: Vertical(g1)
    c: Vertical(g3)
    c: Coincident(g0,g-3)
    c: Coincident(g1,g-4)
FEATURE [PartDesign::Pad] Pad011
  Direction = (0,0,1)
  Length = 28.8
  Length2 = 10
  Profile = -> Sketch019
  ReferenceAxis = -> Sketch019 [N_Axis]
  Refine = true
  Suppressed = false
  Type = 0
FEATURE [Sketcher::SketchObject] Sketch020
  ArcFitTolerance = 1e-06
  AttachmentSupport = -> [Pad011]
  ExternalGeometry = -> [Pad011]
  FullyConstrained = true
  MakeInternals = false
  MapMode = 5
  Placement = pos=(0,88,0) rot=(1,0,0;1.5708rad)
  sketch-geometry (4):
    g0: LineSegment [constr] StartX=-16 StartY=-9.6 StartZ=0 EndX=0 EndY=-9.6 EndZ=0
    g1: LineSegment StartX=-16 StartY=-9.6 StartZ=0 EndX=-3e-16 EndY=7e-16 EndZ=0
    g2: LineSegment StartX=-3e-16 StartY=7e-16 StartZ=0 EndX=-16 EndY=-3.6e-15 EndZ=0
    g3: LineSegment StartX=-16 StartY=-3.6e-15 StartZ=0 EndX=-16 EndY=-9.6 EndZ=0
  constraints (10):
    c: PointOnObject(g0,g-3)
    c: PointOnObject(g0,g-4)
    c: Horizontal(g0)
    c: Coincident(g0,g1)
    c: Coincident(g1,g-1)
    c: Coincident(g1,g2)
    c: Coincident(g2,g-3)
    c: Coincident(g2,g3)
    c: Coincident(g3,g1)
    c: DistanceY(g3,g3) = 9.6
FEATURE [PartDesign::Pocket] Pocket008
  BaseFeature = -> Pad011
  Direction = (0,1,-2e-16)
  Length = 16
  Length2 = 5
  Profile = -> Sketch020
  ReferenceAxis = -> Sketch020 [N_Axis]
  Refine = true
  Suppressed = false
  Type = 0
FEATURE [PartDesign::SubShapeBinder] Binder008
  BindCopyOnChange = 0
  BindMode = 0
  ClaimChildren = false
  Context = -> Part001 [Body009.Binder008.]
  Fuse = false
  MakeFace = true
  OffsetFill = false
  OffsetIntersection = false
  OffsetJoinType = 0
  OffsetOpenResult = false
  PartialLoad = false
  Refine = true
  Relative = true
  Support = -> [Body001]
  _Version = 2
FEATURE [Sketcher::SketchObject] Sketch021
  ArcFitTolerance = 1e-06
  AttachmentSupport = -> [Binder008]
  ExternalGeometry = -> [Binder008]
  FullyConstrained = true
  MakeInternals = false
  MapMode = 5
  Placement = pos=(0,0,-28.8) rot=(0,0,1;0rad)
  sketch-geometry (4):
    g0: LineSegment StartX=0 StartY=72 StartZ=0 EndX=-16 EndY=72 EndZ=0
    g1: LineSegment StartX=-16 StartY=72 StartZ=0 EndX=-16 EndY=56 EndZ=0
    g2: LineSegment StartX=-16 StartY=56 StartZ=0 EndX=0 EndY=56 EndZ=0
    g3: LineSegment StartX=0 StartY=56 StartZ=0 EndX=0 EndY=72 EndZ=0
  constraints (10):
    c: Coincident(g0,g1)
    c: Coincident(g1,g2)
    c: Coincident(g2,g3)
    c: Coincident(g3,g0)
    c: Horizontal(g0)
    c: Horizontal(g2)
    c: Vertical(g1)
    c: Vertical(g3)
    c: Coincident(g0,g-3)
    c: Coincident(g1,g-4)
FEATURE [PartDesign::Pad] Pad012
  Direction = (0,0,1)
  Length = 28.8
  Length2 = 10
  Profile = -> Sketch021
  ReferenceAxis = -> Sketch021 [N_Axis]
  Refine = true
  Suppressed = false
  Type = 0
FEATURE [Sketcher::SketchObject] Sketch022
  ArcFitTolerance = 1e-06
  AttachmentSupport = -> [Pad012]
  ExternalGeometry = -> [Pad012]
  FullyConstrained = true
  MakeInternals = false
  MapMode = 5
  Placement = pos=(0,56,0) rot=(1,0,0;1.5708rad)
  sketch-geometry (4):
    g0: LineSegment [constr] StartX=-16 StartY=-9.6 StartZ=0 EndX=0 EndY=-9.6 EndZ=0
    g1: LineSegment StartX=-16 StartY=-9.6 StartZ=0 EndX=-3e-16 EndY=7e-16 EndZ=0
    g2: LineSegment StartX=-3e-16 StartY=7e-16 StartZ=0 EndX=-16 EndY=-3.6e-15 EndZ=0
    g3: LineSegment StartX=-16 StartY=-3.6e-15 StartZ=0 EndX=-16 EndY=-9.6 EndZ=0
  constraints (10):
    c: PointOnObject(g0,g-3)
    c: PointOnObject(g0,g-4)
    c: Horizontal(g0)
    c: Coincident(g0,g1)
    c: Coincident(g1,g-1)
    c: Coincident(g1,g2)
    c: Coincident(g2,g-3)
    c: Coincident(g2,g3)
    c: Coincident(g3,g1)
    c: DistanceY(g3,g3) = 9.6
FEATURE [PartDesign::Pocket] Pocket009
  BaseFeature = -> Pad012
  Direction = (0,1,-2e-16)
  Length = 16
  Length2 = 5
  Profile = -> Sketch022
  ReferenceAxis = -> Sketch022 [N_Axis]
  Refine = true
  Suppressed = false
  Type = 0
FEATURE [PartDesign::SubShapeBinder] Binder009
  BindCopyOnChange = 0
  BindMode = 0
  ClaimChildren = false
  Context = -> Part001 [Body010.Binder009.]
  Fuse = false
  MakeFace = true
  OffsetFill = false
  OffsetIntersection = false
  OffsetJoinType = 0
  OffsetOpenResult = false
  PartialLoad = false
  Refine = true
  Relative = true
  Support = -> [Body001]
  _Version = 2
FEATURE [Sketcher::SketchObject] Sketch023
  ArcFitTolerance = 1e-06
  AttachmentSupport = -> [Binder009]
  ExternalGeometry = -> [Binder009]
  FullyConstrained = true
  MakeInternals = false
  MapMode = 5
  Placement = pos=(0,0,-28.8) rot=(0,0,1;0rad)
  sketch-geometry (4):
    g0: LineSegment StartX=0 StartY=40 StartZ=0 EndX=-16 EndY=40 EndZ=0
    g1: LineSegment StartX=-16 StartY=40 StartZ=0 EndX=-16 EndY=24 EndZ=0
    g2: LineSegment StartX=-16 StartY=24 StartZ=0 EndX=0 EndY=24 EndZ=0
    g3: LineSegment StartX=0 StartY=24 StartZ=0 EndX=0 EndY=40 EndZ=0
  constraints (10):
    c: Coincident(g0,g1)
    c: Coincident(g1,g2)
    c: Coincident(g2,g3)
    c: Coincident(g3,g0)
    c: Horizontal(g0)
    c: Horizontal(g2)
    c: Vertical(g1)
    c: Vertical(g3)
    c: Coincident(g0,g-3)
    c: Coincident(g1,g-4)
FEATURE [PartDesign::Pad] Pad013
  Direction = (0,0,1)
  Length = 28.8
  Length2 = 10
  Profile = -> Sketch023
  ReferenceAxis = -> Sketch023 [N_Axis]
  Refine = true
  Suppressed = false
  Type = 0
FEATURE [Sketcher::SketchObject] Sketch024
  ArcFitTolerance = 1e-06
  AttachmentSupport = -> [Pad013]
  ExternalGeometry = -> [Pad013]
  FullyConstrained = true
  MakeInternals = false
  MapMode = 5
  Placement = pos=(0,24,0) rot=(1,0,0;1.5708rad)
  sketch-geometry (4):
    g0: LineSegment [constr] StartX=-16 StartY=-9.6 StartZ=0 EndX=0 EndY=-9.6 EndZ=0
    g1: LineSegment StartX=-16 StartY=-9.6 StartZ=0 EndX=-3e-16 EndY=7e-16 EndZ=0
    g2: LineSegment StartX=-3e-16 StartY=7e-16 StartZ=0 EndX=-16 EndY=-3.6e-15 EndZ=0
    g3: LineSegment StartX=-16 StartY=-3.6e-15 StartZ=0 EndX=-16 EndY=-9.6 EndZ=0
  constraints (10):
    c: PointOnObject(g0,g-3)
    c: PointOnObject(g0,g-4)
    c: Horizontal(g0)
    c: Coincident(g0,g1)
    c: Coincident(g1,g-1)
    c: Coincident(g1,g2)
    c: Coincident(g2,g-3)
    c: Coincident(g2,g3)
    c: Coincident(g3,g1)
    c: DistanceY(g3,g3) = 9.6
FEATURE [PartDesign::Pocket] Pocket010
  BaseFeature = -> Pad013
  Direction = (0,1,-2e-16)
  Length = 16
  Length2 = 5
  Profile = -> Sketch024
  ReferenceAxis = -> Sketch024 [N_Axis]
  Refine = true
  Suppressed = false
  Type = 0
FEATURE [PartDesign::SubShapeBinder] Binder010
  BindCopyOnChange = 0
  BindMode = 0
  ClaimChildren = false
  Context = -> Part001 [Body011.Binder010.]
  Fuse = false
  MakeFace = true
  OffsetFill = false
  OffsetIntersection = false
  OffsetJoinType = 0
  OffsetOpenResult = false
  PartialLoad = false
  Refine = true
  Relative = true
  Support = -> [Body001]
  _Version = 2
FEATURE [Sketcher::SketchObject] Sketch025
  ArcFitTolerance = 1e-06
  AttachmentSupport = -> [Binder010]
  ExternalGeometry = -> [Binder010]
  FullyConstrained = true
  MakeInternals = false
  MapMode = 5
  Placement = pos=(0,0,-28.8) rot=(0,0,1;0rad)
  sketch-geometry (6):
    g0: LineSegment StartX=0 StartY=0 StartZ=0 EndX=-2e-16 EndY=8 EndZ=0
    g1: LineSegment StartX=-2e-16 StartY=8 StartZ=0 EndX=-16 EndY=8 EndZ=0
    g2: LineSegment StartX=-16 StartY=8 StartZ=0 EndX=-16 EndY=-16 EndZ=0
    g3: LineSegment StartX=-16 StartY=-16 StartZ=0 EndX=8 EndY=-16 EndZ=0
    g4: LineSegment StartX=8 StartY=-16 StartZ=0 EndX=8 EndY=0 EndZ=0
    g5: LineSegment StartX=8 StartY=0 StartZ=0 EndX=0 EndY=0 EndZ=0
  constraints (14):
    c: Coincident(g-1,g0)
    c: Coincident(g0,g-4)
    c: Coincident(g0,g1)
    c: Coincident(g1,g-3)
    c: Coincident(g1,g2)
    c: Coincident(g2,g-3)
    c: Coincident(g2,g3)
    c: Horizontal(g3)
    c: Coincident(g3,g4)
    c: PointOnObject(g4,g-1)
    c: Vertical(g4)
    c: Coincident(g4,g5)
    c: Coincident(g5,g0)
    c: Equal(g5,g0)
FEATURE [PartDesign::Pad] Pad014
  Direction = (0,0,1)
  Length = 28.8
  Length2 = 10
  Profile = -> Sketch025
  ReferenceAxis = -> Sketch025 [N_Axis]
  Refine = true
  Suppressed = false
  Type = 0
FEATURE [Sketcher::SketchObject] Sketch026
  ArcFitTolerance = 1e-06
  AttachmentSupport = -> [Pad014]
  ExternalGeometry = -> [Pad014]
  FullyConstrained = true
  MakeInternals = false
  MapMode = 5
  Placement = pos=(8,0,0) rot=(0.57735,0.57735,0.57735;2.0944rad)
  sketch-geometry (3):
    g0: LineSegment StartX=-16 StartY=-9.6 StartZ=0 EndX=-3e-16 EndY=7e-16 EndZ=0
    g1: LineSegment StartX=-3e-16 StartY=7e-16 StartZ=0 EndX=-16 EndY=-3.6e-15 EndZ=0
    g2: LineSegment StartX=-16 StartY=-3.6e-15 StartZ=0 EndX=-16 EndY=-9.6 EndZ=0
  constraints (7):
    c: PointOnObject(g0,g-3)
    c: Coincident(g0,g-1)
    c: Coincident(g0,g1)
    c: Coincident(g1,g-3)
    c: Coincident(g1,g2)
    c: Coincident(g2,g0)
    c: DistanceY(g2,g2) = 9.6
FEATURE [PartDesign::Pocket] Pocket011
  BaseFeature = -> Pad014
  Direction = (-1,0,0)
  Length = 24
  Length2 = 5
  Profile = -> Sketch026
  ReferenceAxis = -> Sketch026 [N_Axis]
  Refine = true
  Suppressed = false
  Type = 0
FEATURE [Sketcher::SketchObject] Sketch027
  ArcFitTolerance = 1e-06
  AttachmentSupport = -> [Pocket011]
  ExternalGeometry = -> [Pocket011]
  FullyConstrained = true
  MakeInternals = false
  MapMode = 5
  Placement = pos=(1.4e-15,8,0) rot=(0,0.707107,0.707107;3.14159rad)
  sketch-geometry (4):
    g0: LineSegment [constr] StartX=16 StartY=-9.6 StartZ=0 EndX=1.8e-15 EndY=-9.6 EndZ=0
    g1: LineSegment StartX=16 StartY=-9.6 StartZ=0 EndX=3e-16 EndY=7e-16 EndZ=0
    g2: LineSegment StartX=3e-16 StartY=7e-16 StartZ=0 EndX=16 EndY=-3.6e-15 EndZ=0
    g3: LineSegment StartX=16 StartY=-3.6e-15 StartZ=0 EndX=16 EndY=-9.6 EndZ=0
  constraints (10):
    c: PointOnObject(g0,g-4)
    c: PointOnObject(g0,g-3)
    c: Horizontal(g0)
    c: Coincident(g0,g1)
    c: Coincident(g1,g-1)
    c: Coincident(g1,g2)
    c: Coincident(g2,g-4)
    c: Coincident(g2,g3)
    c: Coincident(g3,g1)
    c: DistanceY(g3,g3) = 9.6
FEATURE [PartDesign::Pocket] Pocket012
  BaseFeature = -> Pocket011
  Direction = (0,-1,2e-16)
  Length = 24
  Length2 = 5
  Profile = -> Sketch027
  ReferenceAxis = -> Sketch027 [N_Axis]
  Refine = true
  Suppressed = false
  Type = 0
FEATURE [PartDesign::SubShapeBinder] Binder011
  BindCopyOnChange = 0
  BindMode = 0
  ClaimChildren = false
  Context = -> Part001 [Body012.Binder011.]
  Fuse = false
  MakeFace = true
  OffsetFill = false
  OffsetIntersection = false
  OffsetJoinType = 0
  OffsetOpenResult = false
  PartialLoad = false
  Refine = true
  Relative = true
  Support = -> [Body001]
  _Version = 2
FEATURE [Sketcher::SketchObject] Sketch028
  ArcFitTolerance = 1e-06
  AttachmentSupport = -> [Binder011]
  ExternalGeometry = -> [Binder011]
  FullyConstrained = true
  MakeInternals = false
  MapMode = 5
  Placement = pos=(0,0,-28.8) rot=(0,0,1;0rad)
  expr: Constraints[11] = (24 + 16) * 1 mm
  sketch-geometry (4):
    g0: LineSegment StartX=24 StartY=0 StartZ=0 EndX=24 EndY=-16 EndZ=0
    g1: LineSegment StartX=24 StartY=-16 StartZ=0 EndX=40 EndY=-16 EndZ=0
    g2: LineSegment StartX=40 StartY=-16 StartZ=0 EndX=40 EndY=0 EndZ=0
    g3: LineSegment StartX=40 StartY=0 StartZ=0 EndX=24 EndY=0 EndZ=0
  constraints (12):
    c: Coincident(g0,g1)
    c: Coincident(g1,g2)
    c: Coincident(g2,g3)
    c: Coincident(g3,g0)
    c: Vertical(g0)
    c: Vertical(g2)
    c: Horizontal(g1)
    c: Horizontal(g3)
    c: PointOnObject(g0,g-4)
    c: PointOnObject(g1,g-3)
    c: DistanceX(g1,g1) = 16
    c: DistanceX(g-3,g0) = 40
FEATURE [PartDesign::Pad] Pad015
  Direction = (0,0,1)
  Length = 28.8
  Length2 = 10
  Profile = -> Sketch028
  ReferenceAxis = -> Sketch028 [N_Axis]
  Refine = true
  Suppressed = false
  Type = 0
FEATURE [Sketcher::SketchObject] Sketch029
  ArcFitTolerance = 1e-06
  AttachmentSupport = -> [Pad015]
  ExternalGeometry = -> [Pad015]
  FullyConstrained = true
  MakeInternals = false
  MapMode = 5
  Placement = pos=(40,0,0) rot=(0.57735,0.57735,0.57735;2.0944rad)
  sketch-geometry (3):
    g0: LineSegment StartX=-16 StartY=-3.6e-15 StartZ=0 EndX=-16 EndY=-9.6 EndZ=0
    g1: LineSegment StartX=-16 StartY=-9.6 StartZ=0 EndX=-3e-16 EndY=7e-16 EndZ=0
    g2: LineSegment StartX=-3e-16 StartY=7e-16 StartZ=0 EndX=-16 EndY=-3.6e-15 EndZ=0
  constraints (7):
    c: Coincident(g-3,g0)
    c: Vertical(g0)
    c: Coincident(g0,g1)
    c: Coincident(g1,g-1)
    c: Coincident(g1,g2)
    c: Coincident(g2,g0)
    c: DistanceY(g0,g0) = 9.6
FEATURE [PartDesign::Pocket] Pocket013
  BaseFeature = -> Pad015
  Direction = (-1,0,0)
  Length = 16
  Length2 = 5
  Profile = -> Sketch029
  ReferenceAxis = -> Sketch029 [N_Axis]
  Refine = true
  Suppressed = false
  Type = 0
FEATURE [PartDesign::SubShapeBinder] Binder012
  BindCopyOnChange = 0
  BindMode = 0
  ClaimChildren = false
  Context = -> Part001 [Body013.Binder012.]
  Fuse = false
  MakeFace = true
  OffsetFill = false
  OffsetIntersection = false
  OffsetJoinType = 0
  OffsetOpenResult = false
  PartialLoad = false
  Refine = true
  Relative = true
  Support = -> [Body001]
  _Version = 2
FEATURE [Sketcher::SketchObject] Sketch030
  ArcFitTolerance = 1e-06
  AttachmentSupport = -> [Binder012]
  ExternalGeometry = -> [Binder012]
  FullyConstrained = true
  MakeInternals = false
  MapMode = 5
  Placement = pos=(0,0,-28.8) rot=(0,0,1;0rad)
  expr: Constraints[11] = (24 + 16 + 16 + 16) * 1 mm
  sketch-geometry (4):
    g0: LineSegment StartX=56 StartY=-16 StartZ=0 EndX=72 EndY=-16 EndZ=0
    g1: LineSegment StartX=72 StartY=-16 StartZ=0 EndX=72 EndY=0 EndZ=0
    g2: LineSegment StartX=72 StartY=0 StartZ=0 EndX=56 EndY=0 EndZ=0
    g3: LineSegment StartX=56 StartY=0 StartZ=0 EndX=56 EndY=-16 EndZ=0
  constraints (12):
    c: Coincident(g0,g1)
    c: Coincident(g1,g2)
    c: Coincident(g2,g3)
    c: Coincident(g3,g0)
    c: Horizontal(g0)
    c: Horizontal(g2)
    c: Vertical(g1)
    c: Vertical(g3)
    c: PointOnObject(g0,g-4)
    c: PointOnObject(g1,g-3)
    c: DistanceX(g0,g0) = 16
    c: DistanceX(g-4,g0) = 72
FEATURE [PartDesign::Pad] Pad016
  Direction = (0,0,1)
  Length = 28.8
  Length2 = 10
  Profile = -> Sketch030
  ReferenceAxis = -> Sketch030 [N_Axis]
  Refine = true
  Suppressed = false
  Type = 0
FEATURE [Sketcher::SketchObject] Sketch031
  ArcFitTolerance = 1e-06
  AttachmentSupport = -> [Pad016]
  ExternalGeometry = -> [Pad016]
  FullyConstrained = true
  MakeInternals = false
  MapMode = 5
  Placement = pos=(72,0,0) rot=(0.57735,0.57735,0.57735;2.0944rad)
  sketch-geometry (3):
    g0: LineSegment StartX=-16 StartY=-3.6e-15 StartZ=0 EndX=-16 EndY=-9.6 EndZ=0
    g1: LineSegment StartX=-16 StartY=-9.6 StartZ=0 EndX=2e-16 EndY=0 EndZ=0
    g2: LineSegment StartX=2e-16 StartY=0 StartZ=0 EndX=-16 EndY=-3.6e-15 EndZ=0
  constraints (7):
    c: Coincident(g-3,g0)
    c: PointOnObject(g0,g-3)
    c: Coincident(g0,g1)
    c: Coincident(g1,g-1)
    c: Coincident(g1,g2)
    c: Coincident(g2,g0)
    c: DistanceY(g0,g0) = 9.6
FEATURE [PartDesign::Pocket] Pocket014
  BaseFeature = -> Pad016
  Direction = (-1,0,0)
  Length = 16
  Length2 = 5
  Profile = -> Sketch031
  ReferenceAxis = -> Sketch031 [N_Axis]
  Refine = true
  Suppressed = false
  Type = 0
FEATURE [PartDesign::SubShapeBinder] Binder013
  BindCopyOnChange = 0
  BindMode = 0
  ClaimChildren = false
  Context = -> Part001 [Body014.Binder013.]
  Fuse = false
  MakeFace = true
  OffsetFill = false
  OffsetIntersection = false
  OffsetJoinType = 0
  OffsetOpenResult = false
  PartialLoad = false
  Refine = true
  Relative = true
  Support = -> [Body001]
  _Version = 2
FEATURE [Sketcher::SketchObject] Sketch032
  ArcFitTolerance = 1e-06
  AttachmentSupport = -> [Binder013]
  ExternalGeometry = -> [Binder013]
  FullyConstrained = true
  MakeInternals = false
  MapMode = 5
  Placement = pos=(0,0,-28.8) rot=(0,0,1;0rad)
  expr: Constraints[11] = (24 + 16 + 16 + 16 + 16 + 16) * 1 mm
  sketch-geometry (4):
    g0: LineSegment StartX=88 StartY=-16 StartZ=0 EndX=104 EndY=-16 EndZ=0
    g1: LineSegment StartX=104 StartY=-16 StartZ=0 EndX=104 EndY=0 EndZ=0
    g2: LineSegment StartX=104 StartY=0 StartZ=0 EndX=88 EndY=0 EndZ=0
    g3: LineSegment StartX=88 StartY=0 StartZ=0 EndX=88 EndY=-16 EndZ=0
  constraints (12):
    c: Coincident(g0,g1)
    c: Coincident(g1,g2)
    c: Coincident(g2,g3)
    c: Coincident(g3,g0)
    c: Horizontal(g0)
    c: Horizontal(g2)
    c: Vertical(g1)
    c: Vertical(g3)
    c: PointOnObject(g0,g-3)
    c: PointOnObject(g1,g-4)
    c: DistanceX(g0,g0) = 16
    c: DistanceX(g-3,g0) = 104
FEATURE [PartDesign::Pad] Pad017
  Direction = (0,0,1)
  Length = 28.8
  Length2 = 10
  Profile = -> Sketch032
  ReferenceAxis = -> Sketch032 [N_Axis]
  Refine = true
  Suppressed = false
  Type = 0
FEATURE [Sketcher::SketchObject] Sketch033
  ArcFitTolerance = 1e-06
  AttachmentSupport = -> [Pad017]
  ExternalGeometry = -> [Pad017]
  FullyConstrained = true
  MakeInternals = false
  MapMode = 5
  Placement = pos=(104,0,0) rot=(0.57735,0.57735,0.57735;2.0944rad)
  sketch-geometry (3):
    g0: LineSegment StartX=-16 StartY=-3.6e-15 StartZ=0 EndX=-16 EndY=-9.6 EndZ=0
    g1: LineSegment StartX=-16 StartY=-9.6 StartZ=0 EndX=2e-16 EndY=0 EndZ=0
    g2: LineSegment StartX=2e-16 StartY=0 StartZ=0 EndX=-16 EndY=-3.6e-15 EndZ=0
  constraints (7):
    c: Coincident(g-3,g0)
    c: PointOnObject(g0,g-3)
    c: Coincident(g0,g1)
    c: Coincident(g1,g-1)
    c: Coincident(g1,g2)
    c: Coincident(g2,g0)
    c: DistanceY(g0,g0) = 9.6
FEATURE [PartDesign::Pocket] Pocket015
  BaseFeature = -> Pad017
  Direction = (-1,0,0)
  Length = 16
  Length2 = 5
  Profile = -> Sketch033
  ReferenceAxis = -> Sketch033 [N_Axis]
  Refine = true
  Suppressed = false
  Type = 0
FEATURE [Sketcher::SketchObject] Sketch034
  ArcFitTolerance = 1e-06
  AttachmentSupport = -> [Pad004]
  ExternalGeometry = -> [Pad004]
  FullyConstrained = true
  MakeInternals = false
  MapMode = 5
  Placement = pos=(0,0,-32) rot=(0,0,1;0rad)
  sketch-geometry (16):
    g0: LineSegment StartX=1.4 StartY=25 StartZ=0 EndX=8 EndY=25 EndZ=0
    g1: LineSegment StartX=8 StartY=25 StartZ=0 EndX=8 EndY=33 EndZ=0
    g2: LineSegment StartX=8 StartY=33 StartZ=0 EndX=1.4 EndY=33 EndZ=0
    g3: LineSegment StartX=1.4 StartY=33 StartZ=0 EndX=1.4 EndY=25 EndZ=0
    g4: LineSegment StartX=126.4 StartY=25 StartZ=0 EndX=126.4 EndY=33 EndZ=0
    g5: LineSegment StartX=126.4 StartY=33 StartZ=0 EndX=119.8 EndY=33 EndZ=0
    g6: LineSegment StartX=119.8 StartY=33 StartZ=0 EndX=119.8 EndY=25 EndZ=0
    g7: LineSegment StartX=119.8 StartY=25 StartZ=0 EndX=126.4 EndY=25 EndZ=0
    g8: LineSegment StartX=126.4 StartY=134.4 StartZ=0 EndX=119.8 EndY=134.4 EndZ=0
    g9: LineSegment StartX=119.8 StartY=134.4 StartZ=0 EndX=119.8 EndY=127.8 EndZ=0
    g10: LineSegment StartX=119.8 StartY=127.8 StartZ=0 EndX=126.4 EndY=127.8 EndZ=0
    g11: LineSegment StartX=126.4 StartY=127.8 StartZ=0 EndX=126.4 EndY=134.4 EndZ=0
    g12: LineSegment StartX=1.4 StartY=134.4 StartZ=0 EndX=1.4 EndY=127.8 EndZ=0
    g13: LineSegment StartX=1.4 StartY=127.8 StartZ=0 EndX=8 EndY=127.8 EndZ=0
    g14: LineSegment StartX=8 StartY=127.8 StartZ=0 EndX=8 EndY=134.4 EndZ=0
    g15: LineSegment StartX=8 StartY=134.4 StartZ=0 EndX=1.4 EndY=134.4 EndZ=0
  constraints (46):
    c: Coincident(g0,g1)
    c: Coincident(g1,g2)
    c: Coincident(g2,g3)
    c: Horizontal(g0)
    c: Horizontal(g2)
    c: Vertical(g1)
    c: Vertical(g3)
    c: Coincident(g4,g5)
    c: Coincident(g5,g6)
    c: Coincident(g6,g7)
    c: Vertical(g4)
    c: Vertical(g6)
    c: Horizontal(g5)
    c: Horizontal(g7)
    c: Coincident(g8,g9)
    c: Coincident(g9,g10)
    c: Coincident(g10,g11)
    c: Coincident(g11,g8)
    c: Horizontal(g8)
    c: Horizontal(g10)
    c: Vertical(g9)
    c: Vertical(g11)
    c: Coincident(g8,g-10)
    c: Coincident(g12,g13)
    c: Coincident(g13,g14)
    c: Coincident(g14,g15)
    c: Coincident(g15,g12)
    c: Vertical(g12)
    c: Vertical(g14)
    c: Horizontal(g13)
    c: Horizontal(g15)
    c: Coincident(g12,g-8)
    c: DistanceX(g-6,g13) = 8
    c: DistanceY(g13,g-6) = 8
    c: DistanceX(g9,g-6) = 8
    c: DistanceY(g9,g-6) = 8
    c: Coincident(g0,g3)
    c: DistanceX(g-1,g0) = 8
    c: PointOnObject(g0,g-8)
    c: DistanceY(g1,g1) = 8
    c: DistanceY(g-1,g0) = 25
    c: Coincident(g7,g4)
    c: PointOnObject(g4,g-10)
    c: DistanceX(g6,g-5) = 8
    c: DistanceY(g6,g6) = 8
    c: PointOnObject(g6,g0)
FEATURE [PartDesign::Pad] Pad018
  BaseFeature = -> Pad004
  Direction = (0,0,1)
  Length = 25
  Length2 = 10
  Profile = -> Sketch034
  ReferenceAxis = -> Sketch034 [N_Axis]
  Refine = true
  Suppressed = false
  Type = 0
FEATURE [Sketcher::SketchObject] Sketch035
  ArcFitTolerance = 1e-06
  AttachmentSupport = -> [Pad018]
  ExternalGeometry = -> [Pad018]
  FullyConstrained = true
  MakeInternals = false
  MapMode = 5
  Placement = pos=(0,0,0) rot=(1,0,0;1.5708rad)
  expr: Constraints[40] = 24 * 1 mm
  sketch-geometry (16):
    g0: LineSegment StartX=8 StartY=-25.8 StartZ=0 EndX=24 EndY=-25.8 EndZ=0
    g1: LineSegment StartX=24 StartY=-25.8 StartZ=0 EndX=24 EndY=-18.3 EndZ=0
    g2: LineSegment StartX=24 StartY=-18.3 StartZ=0 EndX=8 EndY=-18.3 EndZ=0
    g3: LineSegment StartX=8 StartY=-18.3 StartZ=0 EndX=8 EndY=-25.8 EndZ=0
    g4: LineSegment StartX=40 StartY=-18.3 StartZ=0 EndX=40 EndY=-25.8 EndZ=0
    g5: LineSegment StartX=40 StartY=-25.8 StartZ=0 EndX=56 EndY=-25.8 EndZ=0
    g6: LineSegment StartX=56 StartY=-25.8 StartZ=0 EndX=56 EndY=-18.3 EndZ=0
    g7: LineSegment StartX=56 StartY=-18.3 StartZ=0 EndX=40 EndY=-18.3 EndZ=0
    g8: LineSegment StartX=72 StartY=-18.3 StartZ=0 EndX=72 EndY=-25.8 EndZ=0
    g9: LineSegment StartX=72 StartY=-25.8 StartZ=0 EndX=88 EndY=-25.8 EndZ=0
    g10: LineSegment StartX=88 StartY=-25.8 StartZ=0 EndX=88 EndY=-18.3 EndZ=0
    g11: LineSegment StartX=88 StartY=-18.3 StartZ=0 EndX=72 EndY=-18.3 EndZ=0
    g12: LineSegment StartX=104 StartY=-18.3 StartZ=0 EndX=104 EndY=-25.8 EndZ=0
    g13: LineSegment StartX=104 StartY=-25.8 StartZ=0 EndX=120 EndY=-25.8 EndZ=0
    g14: LineSegment StartX=120 StartY=-25.8 StartZ=0 EndX=120 EndY=-18.3 EndZ=0
    g15: LineSegment StartX=120 StartY=-18.3 StartZ=0 EndX=104 EndY=-18.3 EndZ=0
  constraints (48):
    c: Coincident(g0,g1)
    c: Coincident(g1,g2)
    c: Coincident(g2,g3)
    c: Coincident(g3,g0)
    c: Horizontal(g0)
    c: Horizontal(g2)
    c: Vertical(g1)
    c: Vertical(g3)
    c: Distance(g1,g3) = 16
    c: Distance(g0,g2) = 7.5
    c: Coincident(g4,g5)
    c: Coincident(g5,g6)
    c: Coincident(g6,g7)
    c: Coincident(g7,g4)
    c: Vertical(g4)
    c: Vertical(g6)
    c: Horizontal(g5)
    c: Horizontal(g7)
    c: Distance(g4,g6) = 16
    c: Distance(g5,g7) = 7.5
    c: Coincident(g8,g9)
    c: Coincident(g9,g10)
    c: Coincident(g10,g11)
    c: Coincident(g11,g8)
    c: Vertical(g8)
    c: Vertical(g10)
    c: Horizontal(g9)
    c: Horizontal(g11)
    c: Distance(g8,g10) = 16
    c: Distance(g9,g11) = 7.5
    c: Coincident(g12,g13)
    c: Coincident(g13,g14)
    c: Coincident(g14,g15)
    c: Coincident(g15,g12)
    c: Vertical(g12)
    c: Vertical(g14)
    c: Horizontal(g13)
    c: Horizontal(g15)
    c: Distance(g12,g14) = 16
    c: Distance(g13,g15) = 7.5
    c: DistanceX(g-3,g0) = 24
    c: DistanceY(g-3,g0) = 3
    c: DistanceX(g0,g4) = 16
    c: PointOnObject(g4,g0)
    c: DistanceX(g5,g8) = 16
    c: PointOnObject(g8,g5)
    c: DistanceX(g9,g12) = 16
    c: PointOnObject(g12,g9)
FEATURE [PartDesign::Pocket] Pocket016
  BaseFeature = -> Pad018
  Direction = (0,1,-2e-16)
  Length = 1.4
  Length2 = 5
  Profile = -> Sketch035
  ReferenceAxis = -> Sketch035 [N_Axis]
  Refine = true
  Suppressed = false
  Type = 0
FEATURE [TechDraw::DrawSVGTemplate] Template
  Height = 210
  Orientation = 1
  Template = /Applications/FreeCAD.app/Contents/Resources/share/Mod/TechDraw/Templates/Default_Template_A4_Landscape.svg
  Width = 297
FEATURE [TechDraw::DrawSVGTemplate] Template001
  Height = 210
  Orientation = 1
  Template = /Applications/FreeCAD.app/Contents/Resources/share/Mod/TechDraw/Templates/Default_Template_A4_Landscape.svg
  Width = 297
FEATURE [PartDesign::SubShapeBinder] Binder014
  BindCopyOnChange = 0
  BindMode = 0
  ClaimChildren = false
  Context = -> Body015 [Binder014.]
  Fuse = false
  MakeFace = true
  OffsetFill = false
  OffsetIntersection = false
  OffsetJoinType = 0
  OffsetOpenResult = false
  PartialLoad = false
  Refine = true
  Relative = true
  Support = -> [Body001]
  _Version = 2
FEATURE [PartDesign::SubShapeBinder] Binder015
  BindCopyOnChange = 0
  BindMode = 0
  ClaimChildren = false
  Context = -> Body015 [Binder015.]
  Fuse = false
  MakeFace = true
  OffsetFill = false
  OffsetIntersection = false
  OffsetJoinType = 0
  OffsetOpenResult = false
  PartialLoad = false
  Refine = true
  Relative = true
  Support = -> [Body]
  _Version = 2
FEATURE [PartDesign::Plane] DatumPlane
  AttachmentOffset = pos=(0,0,15) rot=(0,0,1;0rad)
  AttachmentSupport = -> [Binder014]
  Length = 181.347
  MapMode = 5
  Placement = pos=(0,0,-17) rot=(0,0,1;0rad)
  ResizeMode = 0
  Width = 190.147
FEATURE [Sketcher::SketchObject] Sketch036
  ArcFitTolerance = 1e-06
  AttachmentSupport = -> [DatumPlane]
  ExternalGeometry = -> [Binder014,Binder015]
  FullyConstrained = true
  MakeInternals = false
  MapMode = 5
  Placement = pos=(0,0,-17) rot=(0,0,1;0rad)
  sketch-geometry (34):
    g0: LineSegment StartX=8.2 StartY=134.2 StartZ=0 EndX=8.2 EndY=14 EndZ=0
    g1: LineSegment StartX=8.2 StartY=14 StartZ=0 EndX=2.4 EndY=14 EndZ=0
    g2: LineSegment StartX=2.4 StartY=14 StartZ=0 EndX=2.4 EndY=1.6 EndZ=0
    g3: LineSegment StartX=2.4 StartY=1.6 StartZ=0 EndX=8.2 EndY=1.6 EndZ=0
    g4: LineSegment StartX=8.2 StartY=1.6 StartZ=0 EndX=8.2 EndY=-16 EndZ=0
    g5: LineSegment StartX=8.2 StartY=-16 StartZ=0 EndX=23.8 EndY=-16 EndZ=0
    g6: LineSegment StartX=23.8 StartY=-16 StartZ=0 EndX=23.8 EndY=1.6 EndZ=0
    g7: LineSegment StartX=23.8 StartY=1.6 StartZ=0 EndX=40.2 EndY=1.6 EndZ=0
    g8: LineSegment StartX=40.2 StartY=1.6 StartZ=0 EndX=40.2 EndY=-16 EndZ=0
    g9: LineSegment StartX=40.2 StartY=-16 StartZ=0 EndX=55.8 EndY=-16 EndZ=0
    g10: LineSegment StartX=55.8 StartY=-16 StartZ=0 EndX=55.8 EndY=1.6 EndZ=0
    g11: LineSegment StartX=55.8 StartY=1.6 StartZ=0 EndX=72.2 EndY=1.6 EndZ=0
    g12: LineSegment StartX=72.2 StartY=1.6 StartZ=0 EndX=72.2 EndY=-16 EndZ=0
    g13: LineSegment StartX=72.2 StartY=-16 StartZ=0 EndX=87.8 EndY=-16 EndZ=0
    g14: LineSegment StartX=87.8 StartY=-16 StartZ=0 EndX=87.8 EndY=1.6 EndZ=0
    g15: LineSegment StartX=87.8 StartY=1.6 StartZ=0 EndX=104.2 EndY=1.6 EndZ=0
    g16: LineSegment StartX=104.2 StartY=1.6 StartZ=0 EndX=104.2 EndY=-16 EndZ=0
    g17: LineSegment StartX=104.2 StartY=-16 StartZ=0 EndX=119.8 EndY=-16 EndZ=0
    g18: LineSegment StartX=119.8 StartY=-16 StartZ=0 EndX=119.8 EndY=1.6 EndZ=0
    g19: LineSegment StartX=119.8 StartY=1.6 StartZ=0 EndX=125.4 EndY=1.6 EndZ=0
    g20: LineSegment StartX=125.4 StartY=1.6 StartZ=0 EndX=125.4 EndY=14 EndZ=0
    g21: LineSegment StartX=125.4 StartY=14 StartZ=0 EndX=119.6 EndY=14 EndZ=0
    g22: LineSegment StartX=119.6 StartY=14 StartZ=0 EndX=119.6 EndY=134.2 EndZ=0
    g23: LineSegment StartX=119.6 StartY=134.2 StartZ=0 EndX=8.2 EndY=134.2 EndZ=0
    g24: LineSegment [constr] StartX=2.4 StartY=1.6 StartZ=0 EndX=1.4 EndY=1.6 EndZ=0
    g25: LineSegment [constr] StartX=47.85 StartY=95.75 StartZ=0 EndX=79.95 EndY=63.65 EndZ=0
    g26: LineSegment [constr] StartX=47.85 StartY=63.65 StartZ=0 EndX=79.95 EndY=95.75 EndZ=0
    g27: LineSegment StartX=48 StartY=95.6 StartZ=0 EndX=48 EndY=63.8 EndZ=0
    g28: LineSegment StartX=48 StartY=63.8 StartZ=0 EndX=79.8 EndY=63.8 EndZ=0
    g29: LineSegment StartX=79.8 StartY=63.8 StartZ=0 EndX=79.8 EndY=95.6 EndZ=0
    g30: LineSegment StartX=79.8 StartY=95.6 StartZ=0 EndX=48 EndY=95.6 EndZ=0
    g31: LineSegment [constr] StartX=48 StartY=95.6 StartZ=0 EndX=79.8 EndY=63.8 EndZ=0
    g32: LineSegment [constr] StartX=48 StartY=63.8 StartZ=0 EndX=79.8 EndY=95.6 EndZ=0
    g33: GeomPoint X=63.9 Y=79.7 Z=0
  constraints (97):
    c: Vertical(g0)
    c: Coincident(g0,g1)
    c: Horizontal(g1)
    c: Coincident(g1,g2)
    c: Vertical(g2)
    c: Coincident(g2,g3)
    c: Horizontal(g3)
    c: Coincident(g3,g4)
    c: Vertical(g4)
    c: Coincident(g4,g5)
    c: Horizontal(g5)
    c: Coincident(g5,g6)
    c: Vertical(g6)
    c: Coincident(g6,g7)
    c: Horizontal(g7)
    c: Coincident(g7,g8)
    c: Vertical(g8)
    c: Coincident(g8,g9)
    c: Horizontal(g9)
    c: Coincident(g9,g10)
    c: Vertical(g10)
    c: Coincident(g10,g11)
    c: Horizontal(g11)
    c: Coincident(g11,g12)
    c: Vertical(g12)
    c: Coincident(g12,g13)
    c: Horizontal(g13)
    c: Coincident(g13,g14)
    c: Vertical(g14)
    c: Coincident(g14,g15)
    c: Horizontal(g15)
    c: Coincident(g15,g16)
    c: Vertical(g16)
    c: Coincident(g16,g17)
    c: Horizontal(g17)
    c: Coincident(g17,g18)
    c: Vertical(g18)
    c: Coincident(g18,g19)
    c: Horizontal(g19)
    c: Coincident(g19,g20)
    c: Coincident(g20,g21)
    c: Horizontal(g21)
    c: Coincident(g21,g22)
    c: Vertical(g22)
    c: Coincident(g22,g23)
    c: Coincident(g23,g0)
    c: Horizontal(g23)
    c: Vertical(g20)
    c: Coincident(g24,g2)
    c: Horizontal(g24)
    c: DistanceX(g24,g24) = 1
    c: PointOnObject(g6,g3)
    c: PointOnObject(g10,g7)
    c: PointOnObject(g14,g11)
    c: PointOnObject(g18,g15)
    c: Coincident(g27,g28)
    c: Coincident(g28,g29)
    c: Coincident(g29,g30)
    c: Coincident(g30,g27)
    c: Vertical(g27)
    c: Vertical(g29)
    c: Horizontal(g28)
    c: Horizontal(g30)
    c: Distance(g27,g29) = 31.8
    c: Distance(g28,g30) = 31.8
    c: Coincident(g31,g27)
    c: Coincident(g31,g28)
    c: Coincident(g32,g27)
    c: Coincident(g32,g29)
    c: DistanceX(g-3,g0) = 0.2
    c: DistanceX(g22,g-16) = 0.2
    c: DistanceX(g-5,g3) = 0.2
    c: DistanceY(g-5,g3) = 0.2
    c: DistanceY(g2,g2) = 12.4
    c: DistanceY(g0,g-3) = 0.2
    c: PointOnObject(g24,g-17)
    c: PointOnObject(g4,g-13)
    c: DistanceX(g6,g-12) = 0.2
    c: DistanceX(g-6,g7) = 0.2
    c: PointOnObject(g8,g-13)
    c: DistanceX(g10,g-11) = 0.2
    c: DistanceX(g-7,g11) = 0.2
    c: PointOnObject(g12,g-13)
    c: DistanceX(g14,g-10) = 0.2
    c: DistanceX(g-8,g15) = 0.2
    c: PointOnObject(g16,g-13)
    c: DistanceX(g18,g-9) = 0.2
    c: Equal(g2,g20)
    c: DistanceX(g19,g-4) = 1
    c: Coincident(g26,g-14)
    c: Coincident(g26,g-15)
    c: Coincident(g25,g-15)
    c: Coincident(g25,g-14)
    c: PointOnObject(g33,g25)
    c: PointOnObject(g33,g26)
    c: PointOnObject(g33,g32)
    c: PointOnObject(g33,g31)
FEATURE [PartDesign::Pad] Pad019
  Direction = (0,0,1)
  Length = 1.6
  Length2 = 10
  Placement = pos=(0,0,-17) rot=(0,0,1;0rad)
  Profile = -> Sketch036
  ReferenceAxis = -> Sketch036 [N_Axis]
  Refine = true
  Suppressed = false
  Type = 0
FEATURE [PartDesign::Body] Body015  label="Dummy PCB"
  AllowCompound = false
  Group = -> [Binder014,Binder015,DatumPlane,Sketch036,Pad019]
  Origin = -> Origin015
  Tip = -> Pad019
FEATURE [TechDraw::DrawSVGTemplate] Template002
  Height = 210
  Orientation = 1
  Template = /Applications/FreeCAD.app/Contents/Resources/share/Mod/TechDraw/Templates/Default_Template_A4_Landscape.svg
  Width = 297
FEATURE [TechDraw::DrawProjGroupItem] View002
  CoarseView = false
  Direction = (0,0,1)
  Focus = 100
  HardHidden = false
  IsoCount = 0
  IsoHidden = false
  IsoVisible = false
  LockPosition = false
  Perspective = false
  Rotation = 0
  RotationVector = (1,0,0)
  ScaleType = 0
  ScrubCount = 1
  SeamHidden = false
  SeamVisible = true
  SmoothHidden = false
  SmoothVisible = true
  Source = -> [Body015]
  Type = 0
  X = 148.5
  XDirection = (1,0,0)
  Y = 105
FEATURE [TechDraw::DrawViewDimension] Dimension012
  AngleOverride = false
  Arbitrary = false
  ArbitraryTolerances = false
  BoxCorners = (2) [(-61.5,-75.1,0),(61.5,75.1,0)]
  EqualTolerance = true
  ExtensionAngle = 0
  FormatSpec = %.2f
  FormatSpecOverTolerance = %+.2f
  FormatSpecUnderTolerance = %+.2f
  Inverted = false
  LineAngle = 0
  LockPosition = false
  MeasureType = 1
  OverTolerance = 0
  References2D = -> [View002]
  Rotation = 0
  ScaleType = 0
  TheoreticalExact = false
  Type = 2
  UnderTolerance = 0
  X = -108.887
  Y = -30.5785
FEATURE [TechDraw::DrawViewDimension] Dimension013
  AngleOverride = false
  Arbitrary = false
  ArbitraryTolerances = false
  BoxCorners = (2) [(-61.5,-75.1,0),(61.5,75.1,0)]
  EqualTolerance = true
  ExtensionAngle = 0
  FormatSpec = %.2f
  FormatSpecOverTolerance = %+.2f
  FormatSpecUnderTolerance = %+.2f
  Inverted = false
  LineAngle = 0
  LockPosition = false
  MeasureType = 1
  OverTolerance = 0
  References2D = -> [View002]
  Rotation = 0
  ScaleType = 0
  TheoreticalExact = false
  Type = 0
  UnderTolerance = 0
  X = -97.7541
  Y = -25.2396
FEATURE [TechDraw::DrawViewDimension] Dimension014
  AngleOverride = false
  Arbitrary = false
  ArbitraryTolerances = false
  BoxCorners = (2) [(-61.5,-75.1,0),(61.5,75.1,0)]
  EqualTolerance = true
  ExtensionAngle = 0
  FormatSpec = %.2f
  FormatSpecOverTolerance = %+.2f
  FormatSpecUnderTolerance = %+.2f
  Inverted = false
  LineAngle = 0
  LockPosition = false
  MeasureType = 1
  OverTolerance = 0
  References2D = -> [View002]
  Rotation = 0
  ScaleType = 0
  TheoreticalExact = false
  Type = 1
  UnderTolerance = 0
  X = 14.8695
  Y = 90.4384
FEATURE [TechDraw::DrawViewDimension] Dimension015
  AngleOverride = false
  Arbitrary = false
  ArbitraryTolerances = false
  BoxCorners = (2) [(-61.5,-75.1,0),(61.5,75.1,0)]
  EqualTolerance = true
  ExtensionAngle = 0
  FormatSpec = %.2f
  FormatSpecOverTolerance = %+.2f
  FormatSpecUnderTolerance = %+.2f
  Inverted = false
  LineAngle = 0
  LockPosition = false
  MeasureType = 1
  OverTolerance = 0
  References2D = -> [View002]
  Rotation = 0
  ScaleType = 0
  TheoreticalExact = false
  Type = 0
  UnderTolerance = 0
  X = -52.0708
  Y = 90.4384
FEATURE [TechDraw::DrawViewDimension] Dimension016
  AngleOverride = false
  Arbitrary = false
  ArbitraryTolerances = false
  BoxCorners = (2) [(-61.5,-75.1,0),(61.5,75.1,0)]
  EqualTolerance = true
  ExtensionAngle = 0
  FormatSpec = %.2f
  FormatSpecOverTolerance = %+.2f
  FormatSpecUnderTolerance = %+.2f
  Inverted = false
  LineAngle = 0
  LockPosition = false
  MeasureType = 1
  OverTolerance = 0
  References2D = -> [View002]
  Rotation = 0
  ScaleType = 0
  TheoreticalExact = false
  Type = 0
  UnderTolerance = 0
  X = 66.0542
  Y = 90.4384
FEATURE [TechDraw::DrawPage] Page002  label="DummyPCB Main"
  KeepUpdated = true
  NextBalloonIndex = 1
  ProjectionType = 0
  Template = -> Template002
  Views = -> [View002,Dimension012,Dimension013,Dimension014,Dimension015,Dimension016]
FEATURE [Mesh::Feature] CartridgeMk1_BackSide  label="CartridgeMk1-BackSide"
FEATURE [Mesh::Feature] CartridgeMk1_CartridgeMk1_simple_1  label="CartridgeMk1-CartridgeMk1_simple 1"
FEATURE [Mesh::Feature] CartridgeMk1_FrontSide  label="CartridgeMk1-FrontSide"
FEATURE [Mesh::Feature] CartridgeMk1_Housing  label="CartridgeMk1-Housing"
FEATURE [Mesh::Feature] CartridgeMk1_TopPanel  label="CartridgeMk1-TopPanel"
FEATURE [App::Part] Part  label="Cartridge"
  Group = -> [CartridgeMk1_TopPanel,CartridgeMk1_Housing,CartridgeMk1_FrontSide,CartridgeMk1_CartridgeMk1_simple_1,CartridgeMk1_BackSide]
  Origin = -> Origin053
  Placement = pos=(50.1,80.5,-24) rot=(1,0,0;1.5708rad)
FEATURE [Part::Feature] Part__Feature  label="C_0201_0603Metric"
  shape: bbox 0.6 x 0.3 x 0.3 mm, 28 faces (baked)
FEATURE [App::Part] C_0201_0603Metric  label="C_0201_0603Metric062"
  Group = -> [Part__Feature]
  Origin = -> Origin239
  Placement = pos=(82.03,101.9,1.65) rot=(0,0,-1;1.5708rad)
FEATURE [Part::Feature] Part__Feature220  label="USB_A_Molex_67643_Horizontal"
  shape: bbox 16.16 x 15.26 x 11.54 mm, 559 faces, 10 solids (baked)
FEATURE [App::Part] USB_A_Molex_67643_Horizontal  label="USB_A_Molex_67643_Horizontal035"
  Group = -> [Part__Feature220]
  Origin = -> Origin240
  Placement = pos=(106.05,9.36,1.65) rot=(0,0,1;0rad)
FEATURE [Part::Feature] Part__Feature221  label="5033981892"
  shape: bbox 13.66 x 14.33 x 1.281 mm, 1438 faces (baked)
FEATURE [App::Part] _033981892  label="5033981892010"
  Group = -> [Part__Feature221]
  Origin = -> Origin241
  Placement = pos=(-94.1,17.1,156.05) rot=(1,0,0;3.14159rad)
FEATURE [Part::Feature] Part__Feature222  label="JST_B2B_PH_K"
  shape: bbox 5.9 x 4.55 x 9.4 mm, 93 faces (baked)
FEATURE [App::Part] JST_PH_B2B_PH_K_1x02_P2_00mm_Vertical  label="JST_PH_B2B-PH-K_1x02_P2.00mm_Vertical"
  Group = -> [Part__Feature222]
  Origin = -> Origin242
  Placement = pos=(108.3,77.05,1.65) rot=(0,0,1;0rad)
FEATURE [Part::Feature] Part__Feature223  label="C_0201_0603Metric063"
  shape: bbox 0.6 x 0.3 x 0.3 mm, 28 faces (baked)
FEATURE [App::Part] C_0201_0603Metric040
  Group = -> [Part__Feature223]
  Origin = -> Origin243
  Placement = pos=(81.65,117.345,1.65) rot=(0,0,-1;1.5708rad)
FEATURE [Part::Feature] Part__Feature224  label="SJ3-35083B-TR"
  shape: large baked B-rep (47 MB .brp); summary skipped
FEATURE [App::Part] SJ3_35083B_TR  label="SJ3-35083B-TR010"
  Group = -> [Part__Feature224]
  Origin = -> Origin244
  Placement = pos=(65.5745,126.666,1.75) rot=(0,0.707107,0.707107;3.14159rad)
FEATURE [Part::Feature] Part__Feature225  label="PJ-114AH-SMT-TR"
  shape: bbox 12.43 x 13.46 x 12.3 mm, 85 faces (baked)
FEATURE [App::Part] PJ_114AH_SMT_TR  label="PJ-114AH-SMT-TR010"
  Group = -> [Part__Feature225]
  Origin = -> Origin245
  Placement = pos=(25.3,135.15,7.15) rot=(0,0,1;3.14159rad)
FEATURE [Part::Feature] Part__Feature226  label="R_0201_0603Metric"
  shape: bbox 0.6 x 0.3 x 0.23 mm, 26 faces (baked)
FEATURE [App::Part] R_0201_0603Metric  label="R_0201_0603Metric080"
  Group = -> [Part__Feature226]
  Origin = -> Origin246
  Placement = pos=(81.33,106.945,1.65) rot=(0,0,1;3.14159rad)
FEATURE [Part::Feature] Part__Feature227  label="ASSEMBLY"
  shape: bbox 2.5 x 2 x 0.7 mm, 30 faces, 5 solids (baked)
FEATURE [App::Part] _30108208209  label="830108208209"
  Group = -> [Part__Feature227]
  Origin = -> Origin247
  Placement = pos=(25.125,27.863,1.65) rot=(0,0,1;3.14159rad)
FEATURE [Part::Feature] Part__Feature228  label="R_0201_0603Metric081"
  shape: bbox 0.6 x 0.3 x 0.23 mm, 26 faces (baked)
FEATURE [App::Part] R_0201_0603Metric052
  Group = -> [Part__Feature228]
  Origin = -> Origin248
  Placement = pos=(53.455,31,1.65) rot=(0,0,1;0rad)
FEATURE [Part::Feature] Part__Feature229  label="USB_A_Molex_67643_Horizontal036"
  shape: bbox 16.16 x 15.26 x 11.54 mm, 559 faces, 10 solids (baked)
FEATURE [App::Part] USB_A_Molex_67643_Horizontal022
  Group = -> [Part__Feature229]
  Origin = -> Origin249
  Placement = pos=(42.05,9.36,1.65) rot=(0,0,1;0rad)
FEATURE [Part::Feature] Part__Feature230  label="JST_B2B_PH_K016"
  shape: bbox 5.9 x 4.55 x 9.4 mm, 93 faces (baked)
FEATURE [App::Part] JST_PH_B2B_PH_K_1x02_P2_00mm_Vertical016  label="JST_PH_B2B-PH-K_1x02_P2.00mm_Vertical016"
  Group = -> [Part__Feature230]
  Origin = -> Origin250
  Placement = pos=(108.3,89.05,1.65) rot=(0,0,1;0rad)
FEATURE [Part::Feature] Part__Feature231  label="R_0201_0603Metric082"
  shape: bbox 0.6 x 0.3 x 0.23 mm, 26 faces (baked)
FEATURE [App::Part] R_0201_0603Metric053
  Group = -> [Part__Feature231]
  Origin = -> Origin251
  Placement = pos=(76.595,113.6,1.65) rot=(0,0,1;0rad)
FEATURE [Part::Feature] Part__Feature232  label="ASSEMBLY022"
  shape: bbox 2.1 x 2 x 1.1 mm, 102 faces, 7 solids (baked)
FEATURE [App::Part] NC7WZ16P6X
  Group = -> [Part__Feature232]
  Origin = -> Origin252
  Placement = pos=(78.1,101.55,1.65) rot=(0,0,1;1.5708rad)
FEATURE [Part::Feature] Part__Feature233  label="R_0201_0603Metric083"
  shape: bbox 0.6 x 0.3 x 0.23 mm, 26 faces (baked)
FEATURE [App::Part] R_0201_0603Metric054
  Group = -> [Part__Feature233]
  Origin = -> Origin253
  Placement = pos=(76.53,120.4,1.65) rot=(0,0,1;0rad)
FEATURE [Part::Feature] Part__Feature234  label="DF40C-100DS.prt"
  shape: bbox 3.38 x 1.45 x 22.6 mm, 2193 faces (baked)
FEATURE [App::Part] DF40C_100DS  label="DF40C-100DS"
  Group = -> [Part__Feature234]
  Origin = -> Origin254
  Placement = pos=(96.67,18.54,1.65) rot=(0.57735,0.57735,0.57735;2.0944rad)
FEATURE [Part::Feature] Part__Feature235  label="DF40C-100DS.prt010"
  shape: bbox 3.38 x 1.45 x 22.6 mm, 2193 faces (baked)
FEATURE [App::Part] DF40C_100DS010  label="DF40C-100DS010"
  Group = -> [Part__Feature235]
  Origin = -> Origin255
  Placement = pos=(96.67,52.46,1.65) rot=(0.57735,0.57735,0.57735;2.0944rad)
FEATURE [Part::Feature] Part__Feature236  label="LED_0201_0603Metric"
  shape: bbox 0.65 x 0.35 x 0.2 mm, 24 faces (baked)
FEATURE [App::Part] LED_0201_0603Metric  label="LED_0201_0603Metric008"
  Group = -> [Part__Feature236]
  Origin = -> Origin256
  Placement = pos=(53.455,35.5,1.65) rot=(0,0,1;0rad)
FEATURE [Part::Feature] Part__Feature237  label="C_0201_0603Metric064"
  shape: bbox 0.6 x 0.3 x 0.3 mm, 28 faces (baked)
FEATURE [App::Part] C_0201_0603Metric041
  Group = -> [Part__Feature237]
  Origin = -> Origin257
  Placement = pos=(81.295,110.1,1.65) rot=(0,0,1;3.14159rad)
FEATURE [Part::Feature] Part__Feature238  label="R_0201_0603Metric084"
  shape: bbox 0.6 x 0.3 x 0.23 mm, 26 faces (baked)
FEATURE [App::Part] R_0201_0603Metric055
  Group = -> [Part__Feature238]
  Origin = -> Origin258
  Placement = pos=(81.295,113.6,1.65) rot=(0,0,1;3.14159rad)
FEATURE [Part::Feature] Part__Feature239  label="R_0201_0603Metric085"
  shape: bbox 0.6 x 0.3 x 0.23 mm, 26 faces (baked)
FEATURE [App::Part] R_0201_0603Metric056
  Group = -> [Part__Feature239]
  Origin = -> Origin259
  Placement = pos=(81.35,120.4,1.65) rot=(0,0,1;3.14159rad)
FEATURE [Part::Feature] Part__Feature240  label="JST_B2B_PH_K017"
  shape: bbox 5.9 x 4.55 x 9.4 mm, 93 faces (baked)
FEATURE [App::Part] JST_PH_B2B_PH_K_1x02_P2_00mm_Vertical017  label="JST_PH_B2B-PH-K_1x02_P2.00mm_Vertical017"
  Group = -> [Part__Feature240]
  Origin = -> Origin260
  Placement = pos=(108.3,65.5,1.65) rot=(0,0,1;0rad)
FEATURE [Part::Feature] Part__Feature241  label="C_0201_0603Metric065"
  shape: bbox 0.6 x 0.3 x 0.3 mm, 28 faces (baked)
FEATURE [App::Part] C_0201_0603Metric042
  Group = -> [Part__Feature241]
  Origin = -> Origin261
  Placement = pos=(30.3,28.095,1.65) rot=(0,0,1;1.5708rad)
FEATURE [Part::Feature] Part__Feature242  label="USB_A_Molex_67643_Horizontal037"
  shape: bbox 16.16 x 15.26 x 11.54 mm, 559 faces, 10 solids (baked)
FEATURE [App::Part] USB_A_Molex_67643_Horizontal023
  Group = -> [Part__Feature242]
  Origin = -> Origin262
  Placement = pos=(74.05,9.36,1.65) rot=(0,0,1;0rad)
FEATURE [Part::Feature] Part__Feature243  label="PinHeader_1x03_P254mm_Vertical"
  shape: bbox 2.54 x 7.62 x 11.54 mm, 76 faces (baked)
FEATURE [App::Part] PinHeader_1x03_P2_54mm_Vertical  label="PinHeader_1x03_P2.54mm_Vertical"
  Group = -> [Part__Feature243]
  Origin = -> Origin263
  Placement = pos=(34.15,101.3,1.65) rot=(0,0,1;3.14159rad)
FEATURE [Part::Feature] Part__Feature244  label="C_0201_0603Metric066"
  shape: bbox 0.6 x 0.3 x 0.3 mm, 28 faces (baked)
FEATURE [App::Part] C_0201_0603Metric043
  Group = -> [Part__Feature244]
  Origin = -> Origin264
  Placement = pos=(76.405,110.1,1.65) rot=(0,0,1;0rad)
FEATURE [Part::Feature] Part__Feature245  label="C-1871058-1"
  shape: bbox 25 x 8.85 x 15.4 mm, 386 faces (baked)
FEATURE [App::Part] _871058_1  label="1871058-1"
  Group = -> [Part__Feature245]
  Origin = -> Origin265
  Placement = pos=(60.74,78,11.6) rot=(0,0,1;3.14159rad)
FEATURE [Part::Feature] Part__Feature246  label="HDMI_A_Molex_208658-1001_Horizontal"
  shape: bbox 12.15 x 15 x 8.39 mm, 435 faces (baked)
FEATURE [App::Part] HDMI_A_Molex_208658_1001_Horizontal  label="HDMI_A_Molex_208658-1001_Horizontal010"
  Group = -> [Part__Feature246]
  Origin = -> Origin266
  Placement = pos=(96.3,125.565,1.65) rot=(0,0,1;1.5708rad)
FEATURE [Part::Feature] Part__Feature247  label="IRF540NSTRLPBF"
  shape: bbox 9.65 x 4.187 x 15.88 mm, 74 faces (baked)
FEATURE [App::Part] IRLZ34NSTRLPBF
  Group = -> [Part__Feature247]
  Origin = -> Origin267
  Placement = pos=(15.59,94.65,1.78) rot=(1,0,0;1.5708rad)
FEATURE [Part::Feature] Part__Feature248  label="R_0201_0603Metric086"
  shape: bbox 0.6 x 0.3 x 0.23 mm, 26 faces (baked)
FEATURE [App::Part] R_0201_0603Metric057
  Group = -> [Part__Feature248]
  Origin = -> Origin268
  Placement = pos=(76.47,106.945,1.65) rot=(0,0,1;0rad)
FEATURE [Part::Feature] Part__Feature249  label="USB_A_Molex_67643_Horizontal038"
  shape: bbox 16.16 x 15.26 x 11.54 mm, 559 faces, 10 solids (baked)
FEATURE [App::Part] USB_A_Molex_67643_Horizontal024
  Group = -> [Part__Feature249]
  Origin = -> Origin269
  Placement = pos=(10.05,9.36,1.65) rot=(0,0,1;0rad)
FEATURE [Part::Feature] Part__Feature250  label="R_0201_0603Metric087"
  shape: bbox 0.6 x 0.3 x 0.23 mm, 26 faces (baked)
FEATURE [App::Part] R_0201_0603Metric058
  Group = -> [Part__Feature250]
  Origin = -> Origin270
  Placement = pos=(32.3,23.345,1.65) rot=(0,0,1;1.5708rad)
FEATURE [Part::Feature] Part__Feature251  label="C_0201_0603Metric067"
  shape: bbox 0.6 x 0.3 x 0.3 mm, 28 faces (baked)
FEATURE [App::Part] C_0201_0603Metric044
  Group = -> [Part__Feature251]
  Origin = -> Origin271
  Placement = pos=(76.25,117.345,1.65) rot=(0,0,-1;1.5708rad)
FEATURE [Part::Feature] Part__Feature252  label="C_0201_0603Metric068"
  shape: bbox 0.6 x 0.3 x 0.3 mm, 28 faces (baked)
FEATURE [App::Part] C_0201_0603Metric045
  Group = -> [Part__Feature252]
  Origin = -> Origin272
  Placement = pos=(20.8,28.07,1.65) rot=(0,0,1;1.5708rad)
FEATURE [Part::Feature] Part__Feature253  label="R_0201_0603Metric088"
  shape: bbox 0.6 x 0.3 x 0.23 mm, 26 faces (baked)
FEATURE [App::Part] R_0201_0603Metric059
  Group = -> [Part__Feature253]
  Origin = -> Origin273
  Placement = pos=(19.8,24,1.65) rot=(0,0,1;1.5708rad)
FEATURE [Part::Feature] Part__Feature254  label="ASSEMBLY023"
  shape: bbox 6.1 x 6.1 x 1 mm, 230 faces, 38 solids (baked)
FEATURE [App::Part] USB2514B_M2
  Group = -> [Part__Feature254]
  Origin = -> Origin274
  Placement = pos=(25.75,19.75,1.65) rot=(0,0,1;0rad)
FEATURE [Part::Feature] Part__Feature255  label="RetroConsoleMk2_PCB"
  shape: bbox 123 x 132.6 x 1.6 mm, 115 faces (baked)
FEATURE [App::Part] RetroConsoleMk2_1  label="RetroConsoleMk2"
  Group = -> [C_0201_0603Metric,USB_A_Molex_67643_Horizontal,_033981892,JST_PH_B2B_PH_K_1x02_P2_00mm_Vertical,C_0201_0603Metric040,SJ3_35083B_TR,PJ_114AH_SMT_TR,R_0201_0603Metric,_30108208209,R_0201_0603Metric052,USB_A_Molex_67643_Horizontal022,JST_PH_B2B_PH_K_1x02_P2_00mm_Vertical016,R_0201_0603Metric053,NC7WZ16P6X,R_0201_0603Metric054,DF40C_100DS,DF40C_100DS010,LED_0201_0603Metric,C_0201_0603Metric041,+18 more]
  Origin = -> Origin275
  Placement = pos=(2.4,1.6,-28) rot=(0,0,1;0rad)
FEATURE [Part::Feature] Part__Feature256  label="Component1"
  Placement = pos=(-3.98676e-05,0.793211,-1.03617) rot=(0,0,1;0rad)
  shape: bbox 15.64 x 14.07 x 16.33 mm, 110 faces, 7 solids (baked)
FEATURE [Part::Feature] Part__Feature257  label="Component2"
  Placement = pos=(-3.98676e-05,0.628211,-1.03617) rot=(0,0,1;0rad)
  shape: bbox 7.2 x 3.95 x 5.56 mm, 19 faces (baked)
FEATURE [App::Part] cherry_mx_v28  label="cherry mx v28"
  Group = -> [Part__Feature256,Part__Feature257]
  Origin = -> Origin276
  Placement = pos=(30.97,103.8,-6.72) rot=(-0.57735,0.57735,0.57735;4.18879rad)
  expr: .Placement.Base.z = -6.72 mm
FEATURE [Part::FeaturePython] Clone  label="cherry mx v029"  # Draft clone (typed FeaturePython)
  AttacherType = Attacher::AttachEngine3D
  Fuse = false
  Objects = -> [cherry_mx_v28]
  Placement = pos=(30.97,71.8,-8.12) rot=(-0.57735,0.57735,0.57735;4.18879rad)
  Scale = (1,1,1)
  expr: .Placement.Base.y = 103.8 mm - 32 mm
  expr: .Placement.Base.z = -6.72 mm - 1.4 mm
FEATURE [Part::FeaturePython] Clone001  label="cherry mx v030"  # Draft clone (typed FeaturePython)
  AttacherType = Attacher::AttachEngine3D
  Fuse = false
  Objects = -> [cherry_mx_v28]
  Placement = pos=(30.97,31.8,-8.12) rot=(-0.57735,0.57735,0.57735;4.18879rad)
  Scale = (1,1,1)
  expr: .Placement.Base.y = 103.8 mm - 16 mm - 16 mm - 16 mm - 16 mm - 8 mm
  expr: .Placement.Base.z = -6.72 mm - 1.4 mm
FEATURE [PartDesign::SubShapeBinder] Binder016
  BindCopyOnChange = 0
  BindMode = 0
  ClaimChildren = false
  Context = -> Body016 [Binder016.]
  Fuse = false
  MakeFace = true
  OffsetFill = false
  OffsetIntersection = false
  OffsetJoinType = 0
  OffsetOpenResult = false
  PartialLoad = false
  Refine = true
  Relative = true
  Support = -> [cherry_mx_v28]
  _Version = 2
FEATURE [PartDesign::SubShapeBinder] Binder017
  BindCopyOnChange = 0
  BindMode = 0
  ClaimChildren = false
  Context = -> Body016 [Binder017.]
  Fuse = false
  MakeFace = true
  OffsetFill = false
  OffsetIntersection = false
  OffsetJoinType = 0
  OffsetOpenResult = false
  PartialLoad = false
  Refine = true
  Relative = true
  Support = -> [Body]
  _Version = 2
FEATURE [Sketcher::SketchObject] Sketch037
  ArcFitTolerance = 1e-06
  AttachmentSupport = -> [Binder016]
  ExternalGeometry = -> [Binder016]
  FullyConstrained = true
  MakeInternals = false
  MapMode = 5
  Placement = pos=(0,0,-0.411789) rot=(0,0,1;0rad)
  sketch-geometry (20):
    g0: LineSegment StartX=29.7562 StartY=104.475 StartZ=0 EndX=31.4312 EndY=104.475 EndZ=0
    g1: LineSegment StartX=31.4312 StartY=104.475 StartZ=0 EndX=31.4312 EndY=106.05 EndZ=0
    g2: LineSegment StartX=31.4312 StartY=106.05 StartZ=0 EndX=32.5812 EndY=106.05 EndZ=0
    g3: LineSegment StartX=32.5812 StartY=106.05 StartZ=0 EndX=32.5812 EndY=104.475 EndZ=0
    g4: LineSegment StartX=32.5812 StartY=104.475 StartZ=0 EndX=34.2562 EndY=104.475 EndZ=0
    g5: LineSegment StartX=34.2562 StartY=104.475 StartZ=0 EndX=34.2562 EndY=103.125 EndZ=0
    g6: LineSegment StartX=34.2562 StartY=103.125 StartZ=0 EndX=32.5812 EndY=103.125 EndZ=0
    g7: LineSegment StartX=32.5812 StartY=103.125 StartZ=0 EndX=32.5812 EndY=101.55 EndZ=0
    g8: LineSegment StartX=32.5812 StartY=101.55 StartZ=0 EndX=31.4312 EndY=101.55 EndZ=0
    g9: LineSegment StartX=31.4312 StartY=101.55 StartZ=0 EndX=31.4312 EndY=103.125 EndZ=0
    g10: LineSegment StartX=31.4312 StartY=103.125 StartZ=0 EndX=29.7562 EndY=103.125 EndZ=0
    g11: LineSegment StartX=29.7562 StartY=103.125 StartZ=0 EndX=29.7562 EndY=104.475 EndZ=0
    g12: LineSegment StartX=29.1762 StartY=102.825 StartZ=0 EndX=29.1762 EndY=104.775 EndZ=0
    g13: LineSegment StartX=29.1762 StartY=104.775 StartZ=0 EndX=31.1312 EndY=106.73 EndZ=0
    g14: LineSegment StartX=31.1312 StartY=106.73 StartZ=0 EndX=32.8812 EndY=106.73 EndZ=0
    g15: LineSegment StartX=32.8812 StartY=106.73 StartZ=0 EndX=34.8362 EndY=104.775 EndZ=0
    g16: LineSegment StartX=34.8362 StartY=104.775 StartZ=0 EndX=34.8362 EndY=102.825 EndZ=0
    g17: LineSegment StartX=34.8362 StartY=102.825 StartZ=0 EndX=32.8812 EndY=100.87 EndZ=0
    g18: LineSegment StartX=32.8812 StartY=100.87 StartZ=0 EndX=31.1312 EndY=100.87 EndZ=0
    g19: LineSegment StartX=31.1312 StartY=100.87 StartZ=0 EndX=29.1762 EndY=102.825 EndZ=0
  constraints (60):
    c: Horizontal(g0)
    c: Coincident(g0,g1)
    c: Vertical(g1)
    c: Coincident(g1,g2)
    c: Horizontal(g2)
    c: Coincident(g2,g3)
    c: Vertical(g3)
    c: Coincident(g3,g4)
    c: Horizontal(g4)
    c: Coincident(g4,g5)
    c: Vertical(g5)
    c: Coincident(g5,g6)
    c: Horizontal(g6)
    c: Coincident(g6,g7)
    c: Vertical(g7)
    c: Coincident(g7,g8)
    c: Horizontal(g8)
    c: Coincident(g8,g9)
    c: Vertical(g9)
    c: Coincident(g9,g10)
    c: Horizontal(g10)
    c: Coincident(g10,g11)
    c: Coincident(g11,g0)
    c: Vertical(g11)
    c: DistanceX(g0,g-3) = 0
    c: DistanceY(g-3,g0) = 0
    c: DistanceX(g1,g-4) = 0
    c: DistanceY(g-4,g1) = 0
    c: DistanceX(g-4,g2) = 0
    c: Equal(g3,g1)
    c: Equal(g0,g4)
    c: Equal(g4,g6)
    c: DistanceY(g10,g-3) = 0
    c: Equal(g5,g11)
    c: Equal(g7,g3)
    c: Equal(g8,g2)
    c: Vertical(g12)
    c: Coincident(g12,g13)
    c: Coincident(g13,g14)
    c: Horizontal(g14)
    c: Coincident(g14,g15)
    c: Coincident(g15,g16)
    c: Vertical(g16)
    c: Coincident(g16,g17)
    c: Coincident(g17,g18)
    c: Horizontal(g18)
    c: Coincident(g18,g19)
    c: Coincident(g19,g12)
    c: Angle(g-7,g13) = 2.35619
    c: Angle(g14,g15) = 2.35619
    c: Angle(g16,g17) = 2.35619
    c: Angle(g18,g19) = 2.35619
    c: DistanceX(g12,g-7) = 0.05
    c: DistanceX(g-8,g15) = 0.05
    c: DistanceY(g4,g15) = 0.3
    c: DistanceY(g16,g5) = 0.3
    c: DistanceX(g2,g14) = 0.3
    c: DistanceX(g13,g1) = 0.3
    c: DistanceX(g7,g17) = 0.3
    c: DistanceX(g18,g8) = 0.3
FEATURE [PartDesign::Pad] Pad020
  Direction = (0,0,1)
  Length = 5.81
  Length2 = 10
  Profile = -> Sketch037
  ReferenceAxis = -> Sketch037 [N_Axis]
  Refine = true
  Suppressed = false
  Type = 0
  expr: Length = 7 mm - 0.19 mm - 1 mm
FEATURE [Sketcher::SketchObject] Sketch038
  ArcFitTolerance = 1e-06
  AttachmentSupport = -> [Pad020]
  ExternalGeometry = -> [Binder017]
  FullyConstrained = true
  MakeInternals = false
  MapMode = 5
  Placement = pos=(0,0,5.39821) rot=(0,0,1;0rad)
  sketch-geometry (4):
    g0: LineSegment StartX=24.5 StartY=111.3 StartZ=0 EndX=24.5 EndY=96.3 EndZ=0
    g1: LineSegment StartX=24.5 StartY=96.3 StartZ=0 EndX=39.5 EndY=96.3 EndZ=0
    g2: LineSegment StartX=39.5 StartY=96.3 StartZ=0 EndX=39.5 EndY=111.3 EndZ=0
    g3: LineSegment StartX=39.5 StartY=111.3 StartZ=0 EndX=24.5 EndY=111.3 EndZ=0
  constraints (12):
    c: Coincident(g0,g1)
    c: Coincident(g1,g2)
    c: Coincident(g2,g3)
    c: Coincident(g3,g0)
    c: Vertical(g0)
    c: Vertical(g2)
    c: Horizontal(g1)
    c: Horizontal(g3)
    c: DistanceY(g0,g-3) = 0.5
    c: DistanceX(g-3,g0) = 0.5
    c: DistanceY(g-3,g0) = 0.5
    c: DistanceX(g1,g-4) = 0.5
FEATURE [PartDesign::Pad] Pad021
  BaseFeature = -> Pad020
  Direction = (0,0,1)
  Length = 1
  Length2 = 10
  Profile = -> Sketch038
  ReferenceAxis = -> Sketch038 [N_Axis]
  Refine = true
  Suppressed = false
  Type = 0
FEATURE [Sketcher::SketchObject] Sketch039
  ArcFitTolerance = 1e-06
  AttachmentSupport = -> [Pad021]
  ExternalGeometry = -> [Pad021]
  FullyConstrained = true
  MakeInternals = false
  MapMode = 5
  Placement = pos=(0,0,5.39821) rot=(1,0,0;3.14159rad)
  sketch-geometry (8):
    g0: LineSegment StartX=24.5 StartY=-96.3 StartZ=0 EndX=24.5 EndY=-111.3 EndZ=0
    g1: LineSegment StartX=24.5 StartY=-111.3 StartZ=0 EndX=39.5 EndY=-111.3 EndZ=0
    g2: LineSegment StartX=39.5 StartY=-111.3 StartZ=0 EndX=39.5 EndY=-96.3 EndZ=0
    g3: LineSegment StartX=39.5 StartY=-96.3 StartZ=0 EndX=24.5 EndY=-96.3 EndZ=0
    g4: LineSegment StartX=25.9 StartY=-97.7 StartZ=0 EndX=25.9 EndY=-109.9 EndZ=0
    g5: LineSegment StartX=25.9 StartY=-109.9 StartZ=0 EndX=38.1 EndY=-109.9 EndZ=0
    g6: LineSegment StartX=38.1 StartY=-109.9 StartZ=0 EndX=38.1 EndY=-97.7 EndZ=0
    g7: LineSegment StartX=38.1 StartY=-97.7 StartZ=0 EndX=25.9 EndY=-97.7 EndZ=0
  constraints (22):
    c: Coincident(g0,g1)
    c: Coincident(g1,g2)
    c: Coincident(g2,g3)
    c: Coincident(g3,g0)
    c: Vertical(g0)
    c: Vertical(g2)
    c: Horizontal(g1)
    c: Horizontal(g3)
    c: Coincident(g0,g-3)
    c: Coincident(g1,g-4)
    c: Coincident(g4,g5)
    c: Coincident(g5,g6)
    c: Coincident(g6,g7)
    c: Coincident(g7,g4)
    c: Vertical(g4)
    c: Vertical(g6)
    c: Horizontal(g5)
    c: Horizontal(g7)
    c: DistanceY(g4,g0) = 1.4
    c: DistanceX(g0,g4) = 1.4
    c: DistanceX(g6,g2) = 1.4
    c: DistanceY(g1,g5) = 1.4
FEATURE [PartDesign::Pad] Pad022
  BaseFeature = -> Pad021
  Direction = (0,0,-1)
  Length = 4
  Length2 = 10
  Profile = -> Sketch039
  ReferenceAxis = -> Sketch039 [N_Axis]
  Refine = true
  Suppressed = false
  Type = 0
FEATURE [PartDesign::Body] Body016  label="Shutdown Button plain"
  AllowCompound = false
  Group = -> [Binder016,Binder017,Sketch037,Pad020,Sketch038,Pad021,Sketch039,Pad022]
  Origin = -> Origin277
  Tip = -> Pad022
FEATURE [PartDesign::FeatureBase] Clone002
  BaseFeature = -> Body016
  Suppressed = false
FEATURE [PartDesign::Body] Body017  label="Reset Button plain"
  AllowCompound = false
  Group = -> [Clone002]
  Origin = -> Origin278
  Placement = pos=(0,-32,0) rot=(0,0,1;0rad)
  Tip = -> Clone002
FEATURE [PartDesign::SubShapeBinder] Binder018
  BindCopyOnChange = 0
  BindMode = 0
  ClaimChildren = false
  Context = -> Body018 [Binder018.]
  Fuse = false
  MakeFace = true
  OffsetFill = false
  OffsetIntersection = false
  OffsetJoinType = 0
  OffsetOpenResult = false
  PartialLoad = false
  Refine = true
  Relative = true
  Support = -> [Clone001]
  _Version = 2
FEATURE [PartDesign::SubShapeBinder] Binder019
  BindCopyOnChange = 0
  BindMode = 0
  ClaimChildren = false
  Context = -> Body018 [Binder019.]
  Fuse = false
  MakeFace = true
  OffsetFill = false
  OffsetIntersection = false
  OffsetJoinType = 0
  OffsetOpenResult = false
  PartialLoad = false
  Refine = true
  Relative = true
  Support = -> [Body]
  _Version = 2
FEATURE [Sketcher::SketchObject] Sketch040
  ArcFitTolerance = 1e-06
  AttachmentSupport = -> [Binder018]
  ExternalGeometry = -> [Binder018]
  FullyConstrained = true
  MakeInternals = false
  MapMode = 5
  Placement = pos=(0,0,-1.81179) rot=(0,0,1;0rad)
  sketch-geometry (20):
    g0: LineSegment StartX=29.7562 StartY=31.125 StartZ=0 EndX=29.7562 EndY=32.475 EndZ=0
    g1: LineSegment StartX=29.7562 StartY=32.475 StartZ=0 EndX=31.4312 EndY=32.475 EndZ=0
    g2: LineSegment StartX=31.4312 StartY=32.475 StartZ=0 EndX=31.4312 EndY=34.05 EndZ=0
    g3: LineSegment StartX=31.4312 StartY=34.05 StartZ=0 EndX=32.5812 EndY=34.05 EndZ=0
    g4: LineSegment StartX=32.5812 StartY=34.05 StartZ=0 EndX=32.5812 EndY=32.475 EndZ=0
    g5: LineSegment StartX=32.5812 StartY=32.475 StartZ=0 EndX=34.2562 EndY=32.475 EndZ=0
    g6: LineSegment StartX=34.2562 StartY=32.475 StartZ=0 EndX=34.2562 EndY=31.125 EndZ=0
    g7: LineSegment StartX=34.2562 StartY=31.125 StartZ=0 EndX=32.5812 EndY=31.125 EndZ=0
    g8: LineSegment StartX=32.5812 StartY=31.125 StartZ=0 EndX=32.5812 EndY=29.55 EndZ=0
    g9: LineSegment StartX=32.5812 StartY=29.55 StartZ=0 EndX=31.4312 EndY=29.55 EndZ=0
    g10: LineSegment StartX=31.4312 StartY=29.55 StartZ=0 EndX=31.4312 EndY=31.125 EndZ=0
    g11: LineSegment StartX=31.4312 StartY=31.125 StartZ=0 EndX=29.7562 EndY=31.125 EndZ=0
    g12: LineSegment StartX=29.1762 StartY=30.825 StartZ=0 EndX=29.1762 EndY=32.775 EndZ=0
    g13: LineSegment StartX=29.1762 StartY=32.775 StartZ=0 EndX=31.1312 EndY=34.73 EndZ=0
    g14: LineSegment StartX=31.1312 StartY=34.73 StartZ=0 EndX=32.8812 EndY=34.73 EndZ=0
    g15: LineSegment StartX=32.8812 StartY=34.73 StartZ=0 EndX=34.8362 EndY=32.775 EndZ=0
    g16: LineSegment StartX=34.8362 StartY=32.775 StartZ=0 EndX=34.8362 EndY=30.825 EndZ=0
    g17: LineSegment StartX=34.8362 StartY=30.825 StartZ=0 EndX=32.8812 EndY=28.87 EndZ=0
    g18: LineSegment StartX=32.8812 StartY=28.87 StartZ=0 EndX=31.1312 EndY=28.87 EndZ=0
    g19: LineSegment StartX=31.1312 StartY=28.87 StartZ=0 EndX=29.1762 EndY=30.825 EndZ=0
  constraints (60):
    c: Vertical(g0)
    c: Coincident(g0,g1)
    c: Horizontal(g1)
    c: Coincident(g1,g2)
    c: Vertical(g2)
    c: Coincident(g2,g3)
    c: Horizontal(g3)
    c: Coincident(g3,g4)
    c: Vertical(g4)
    c: Coincident(g4,g5)
    c: Horizontal(g5)
    c: Coincident(g5,g6)
    c: Vertical(g6)
    c: Coincident(g6,g7)
    c: Horizontal(g7)
    c: Coincident(g7,g8)
    c: Vertical(g8)
    c: Coincident(g8,g9)
    c: Horizontal(g9)
    c: Coincident(g9,g10)
    c: Vertical(g10)
    c: Coincident(g10,g11)
    c: Coincident(g11,g0)
    c: Horizontal(g11)
    c: DistanceX(g0,g-3) = 0
    c: DistanceY(g-3,g0) = 0
    c: DistanceX(g2,g-4) = 0
    c: DistanceY(g-4,g2) = 0
    c: DistanceX(g-4,g3) = 0
    c: DistanceY(g0,g-3) = 0
    c: Equal(g4,g2)
    c: Equal(g5,g1)
    c: Equal(g6,g0)
    c: Equal(g7,g5)
    c: Equal(g8,g4)
    c: Equal(g9,g3)
    c: Vertical(g12)
    c: Coincident(g12,g13)
    c: Coincident(g13,g14)
    c: Horizontal(g14)
    c: Coincident(g14,g15)
    c: Coincident(g15,g16)
    c: Vertical(g16)
    c: Coincident(g16,g17)
    c: Coincident(g17,g18)
    c: Horizontal(g18)
    c: Coincident(g18,g19)
    c: Coincident(g19,g12)
    c: Angle(g12,g13) = 2.35619
    c: Angle(g14,g15) = 2.35619
    c: Angle(g16,g17) = 2.35619
    c: Angle(g18,g19) = 2.35619
    c: DistanceX(g-8,g15) = 0.05
    c: DistanceX(g12,g-7) = 0.05
    c: DistanceY(g5,g15) = 0.3
    c: DistanceY(g16,g6) = 0.3
    c: DistanceX(g3,g14) = 0.3
    c: DistanceX(g13,g2) = 0.3
    c: DistanceX(g8,g17) = 0.3
    c: DistanceX(g18,g9) = 0.3
FEATURE [PartDesign::Pad] Pad023
  Direction = (0,0,1)
  Length = 5.81
  Length2 = 10
  Profile = -> Sketch040
  ReferenceAxis = -> Sketch040 [N_Axis]
  Refine = true
  Suppressed = false
  Type = 0
FEATURE [Sketcher::SketchObject] Sketch041
  ArcFitTolerance = 1e-06
  AttachmentSupport = -> [Pad023]
  ExternalGeometry = -> [Binder019]
  FullyConstrained = true
  MakeInternals = false
  MapMode = 5
  Placement = pos=(0,0,3.99821) rot=(0,0,1;0rad)
  sketch-geometry (4):
    g0: LineSegment StartX=24.5 StartY=47.3 StartZ=0 EndX=24.5 EndY=16.3 EndZ=0
    g1: LineSegment StartX=24.5 StartY=16.3 StartZ=0 EndX=39.5 EndY=16.3 EndZ=0
    g2: LineSegment StartX=39.5 StartY=16.3 StartZ=0 EndX=39.5 EndY=47.3 EndZ=0
    g3: LineSegment StartX=39.5 StartY=47.3 StartZ=0 EndX=24.5 EndY=47.3 EndZ=0
  constraints (12):
    c: Coincident(g0,g1)
    c: Coincident(g1,g2)
    c: Coincident(g2,g3)
    c: Coincident(g3,g0)
    c: Vertical(g0)
    c: Vertical(g2)
    c: Horizontal(g1)
    c: Horizontal(g3)
    c: DistanceX(g-3,g0) = 0.5
    c: DistanceY(g0,g-3) = 0.5
    c: DistanceX(g2,g-4) = 0.5
    c: DistanceY(g-4,g1) = 0.5
FEATURE [PartDesign::Pad] Pad024
  BaseFeature = -> Pad023
  Direction = (0,0,1)
  Length = 1
  Length2 = 10
  Profile = -> Sketch041
  ReferenceAxis = -> Sketch041 [N_Axis]
  Refine = true
  Suppressed = false
  Type = 0
FEATURE [Sketcher::SketchObject] Sketch042
  ArcFitTolerance = 1e-06
  AttachmentSupport = -> [Pad024]
  ExternalGeometry = -> [Pad024]
  FullyConstrained = true
  MakeInternals = false
  MapMode = 5
  Placement = pos=(0,0,3.99821) rot=(1,0,0;3.14159rad)
  sketch-geometry (8):
    g0: LineSegment StartX=24.5 StartY=-16.3 StartZ=0 EndX=24.5 EndY=-47.3 EndZ=0
    g1: LineSegment StartX=24.5 StartY=-47.3 StartZ=0 EndX=39.5 EndY=-47.3 EndZ=0
    g2: LineSegment StartX=39.5 StartY=-47.3 StartZ=0 EndX=39.5 EndY=-16.3 EndZ=0
    g3: LineSegment StartX=39.5 StartY=-16.3 StartZ=0 EndX=24.5 EndY=-16.3 EndZ=0
    g4: LineSegment StartX=25.9 StartY=-17.7 StartZ=0 EndX=25.9 EndY=-45.9 EndZ=0
    g5: LineSegment StartX=25.9 StartY=-45.9 StartZ=0 EndX=38.1 EndY=-45.9 EndZ=0
    g6: LineSegment StartX=38.1 StartY=-45.9 StartZ=0 EndX=38.1 EndY=-17.7 EndZ=0
    g7: LineSegment StartX=38.1 StartY=-17.7 StartZ=0 EndX=25.9 EndY=-17.7 EndZ=0
  constraints (22):
    c: Coincident(g0,g1)
    c: Coincident(g1,g2)
    c: Coincident(g2,g3)
    c: Coincident(g3,g0)
    c: Vertical(g0)
    c: Vertical(g2)
    c: Horizontal(g1)
    c: Horizontal(g3)
    c: Coincident(g0,g-3)
    c: Coincident(g1,g-4)
    c: Coincident(g4,g5)
    c: Coincident(g5,g6)
    c: Coincident(g6,g7)
    c: Coincident(g7,g4)
    c: Vertical(g4)
    c: Vertical(g6)
    c: Horizontal(g5)
    c: Horizontal(g7)
    c: DistanceY(g4,g0) = 1.4
    c: DistanceX(g0,g4) = 1.4
    c: DistanceX(g6,g2) = 1.4
    c: DistanceY(g1,g5) = 1.4
FEATURE [PartDesign::Pad] Pad025
  BaseFeature = -> Pad024
  Direction = (0,0,-1)
  Length = 4
  Length2 = 10
  Profile = -> Sketch042
  ReferenceAxis = -> Sketch042 [N_Axis]
  Refine = true
  Suppressed = false
  Type = 0
FEATURE [PartDesign::Body] Body018  label="Quit Button plain"
  AllowCompound = false
  Group = -> [Binder018,Binder019,Sketch040,Pad023,Sketch041,Pad024,Sketch042,Pad025]
  Origin = -> Origin279
  Tip = -> Pad025
FEATURE [TechDraw::DrawSVGTemplate] Template003
  Height = 210
  Orientation = 1
  Template = /Applications/FreeCAD.app/Contents/Resources/share/Mod/TechDraw/Templates/Default_Template_A4_Landscape.svg
  Width = 297
FEATURE [TechDraw::DrawProjGroupItem] View003
  CoarseView = false
  Direction = (-1,-1e-16,0)
  Focus = 100
  HardHidden = false
  IsoCount = 0
  IsoHidden = false
  IsoVisible = false
  LockPosition = false
  Perspective = false
  Rotation = 0
  RotationVector = (1,0,0)
  ScaleType = 0
  ScrubCount = 1
  SeamHidden = false
  SeamVisible = true
  SmoothHidden = false
  SmoothVisible = true
  Source = -> [cherry_mx_v28,Clone,Clone001]
  Type = 0
  X = 73.8682
  XDirection = (1e-16,-1,0)
  Y = 188.821
FEATURE [TechDraw::DrawViewSection] SectionView001  label="Section001  - "
  BaseView = -> View003
  CoarseView = false
  CutSurfaceDisplay = 2
  Direction = (0,-1e-16,1)
  FileGeomPattern = /Applications/FreeCAD.app/Contents/Resources/share/Mod/TechDraw/PAT/FCPAT.pat
  FileHatchPattern = /Applications/FreeCAD.app/Contents/Resources/share/Mod/TechDraw/Patterns/simple.svg
  Focus = 100
  FuseBeforeCut = false
  HardHidden = false
  HatchOffset = (0,0,0)
  HatchRotation = 0
  HatchScale = 1
  IsoCount = 0
  IsoHidden = false
  IsoVisible = false
  LockPosition = false
  NameGeomPattern = Diamond
  Perspective = false
  Rotation = 0
  ScaleType = 0
  ScrubCount = 1
  SeamHidden = false
  SeamVisible = true
  SectionDirection = 4
  SectionLineStretch = 1
  SectionNormal = (0,-1e-16,1)
  SectionOrigin = (32.01,67.8,-12.63)
  SmoothHidden = false
  SmoothVisible = true
  Source = -> [cherry_mx_v28,Clone,Clone001]
  TrimAfterCut = false
  UsePreviousCut = false
  X = 67.1446
  XDirection = (1e-16,-1,-1e-16)
  Y = 144.445
FEATURE [TechDraw::DrawPage] Page003  label="DummyPCB KeyswitchCarrier"
  KeepUpdated = true
  NextBalloonIndex = 1
  ProjectionType = 0
  Template = -> Template003
  Views = -> [View003,SectionView001]
FEATURE [Part::Feature] Part__Feature262  label="JST_B2B_PH_K021"
  shape: bbox 5.9 x 4.55 x 9.4 mm, 93 faces (baked)
FEATURE [App::Part] JST_PH_B2B_PH_K_1x02_P2_00mm_Vertical021  label="JST_PH_B2B-PH-K_1x02_P2.00mm_Vertical021"
  Group = -> [Part__Feature262]
  Origin = -> Origin284
  Placement = pos=(75.4,3.9,-0.05) rot=(1,0,0;3.14159rad)
FEATURE [Part::Feature] Part__Feature263  label="JST_B2B_PH_K022"
  shape: bbox 5.9 x 4.55 x 9.4 mm, 93 faces (baked)
FEATURE [App::Part] JST_PH_B2B_PH_K_1x02_P2_00mm_Vertical022  label="JST_PH_B2B-PH-K_1x02_P2.00mm_Vertical022"
  Group = -> [Part__Feature263]
  Origin = -> Origin285
  Placement = pos=(3.4,3.9,-0.05) rot=(1,0,0;3.14159rad)
FEATURE [Part::Feature] Part__Feature264  label="JST_B2B_PH_K023"
  shape: bbox 5.9 x 4.55 x 9.4 mm, 93 faces (baked)
FEATURE [App::Part] JST_PH_B2B_PH_K_1x02_P2_00mm_Vertical023  label="JST_PH_B2B-PH-K_1x02_P2.00mm_Vertical023"
  Group = -> [Part__Feature264]
  Origin = -> Origin286
  Placement = pos=(35.4,3.9,-0.05) rot=(1,0,0;3.14159rad)
FEATURE [Part::Feature] Part__Feature265  label="KeyswitchCarrierMk1_PCB001"
  shape: bbox 93.3 x 24.4 x 1.6 mm, 30 faces (baked)
FEATURE [App::Part] KeyswitchCarrierMk1_002  label="KeyswitchCarrierMk1"
  Group = -> [JST_PH_B2B_PH_K_1x02_P2_00mm_Vertical021,JST_PH_B2B_PH_K_1x02_P2_00mm_Vertical022,JST_PH_B2B_PH_K_1x02_P2_00mm_Vertical023,Part__Feature265]
  Origin = -> Origin287
  Placement = pos=(15.2,114.3,-14.9) rot=(0,0,1;-1.5708rad)
  expr: .Placement.Base.z = -13.5 mm - 1.4 mm
FEATURE [Sketcher::SketchObject] Sketch043
  ArcFitTolerance = 1e-06
  AttachmentSupport = -> [Pocket]
  ExternalGeometry = -> [Pocket]
  FullyConstrained = true
  MakeInternals = false
  MapMode = 5
  Placement = pos=(0,0,0) rot=(1,0,0;3.14159rad)
  sketch-geometry (16):
    g0: LineSegment StartX=1.5 StartY=-25 StartZ=0 EndX=1.5 EndY=-33 EndZ=0
    g1: LineSegment StartX=1.5 StartY=-33 StartZ=0 EndX=8 EndY=-33 EndZ=0
    g2: LineSegment StartX=8 StartY=-33 StartZ=0 EndX=8 EndY=-25 EndZ=0
    g3: LineSegment StartX=8 StartY=-25 StartZ=0 EndX=1.5 EndY=-25 EndZ=0
    g4: LineSegment StartX=119.8 StartY=-25 StartZ=0 EndX=119.8 EndY=-33 EndZ=0
    g5: LineSegment StartX=119.8 StartY=-33 StartZ=0 EndX=126.3 EndY=-33 EndZ=0
    g6: LineSegment StartX=126.3 StartY=-33 StartZ=0 EndX=126.3 EndY=-25 EndZ=0
    g7: LineSegment StartX=126.3 StartY=-25 StartZ=0 EndX=119.8 EndY=-25 EndZ=0
    g8: LineSegment StartX=1.5 StartY=-134.3 StartZ=0 EndX=8 EndY=-134.3 EndZ=0
    g9: LineSegment StartX=8 StartY=-134.3 StartZ=0 EndX=8 EndY=-127.8 EndZ=0
    g10: LineSegment StartX=8 StartY=-127.8 StartZ=0 EndX=1.5 EndY=-127.8 EndZ=0
    g11: LineSegment StartX=1.5 StartY=-127.8 StartZ=0 EndX=1.5 EndY=-134.3 EndZ=0
    g12: LineSegment StartX=119.8 StartY=-127.8 StartZ=0 EndX=119.8 EndY=-134.3 EndZ=0
    g13: LineSegment StartX=119.8 StartY=-134.3 StartZ=0 EndX=126.3 EndY=-134.3 EndZ=0
    g14: LineSegment StartX=126.3 StartY=-134.3 StartZ=0 EndX=126.3 EndY=-127.8 EndZ=0
    g15: LineSegment StartX=126.3 StartY=-127.8 StartZ=0 EndX=119.8 EndY=-127.8 EndZ=0
  constraints (48):
    c: Coincident(g0,g1)
    c: Coincident(g1,g2)
    c: Coincident(g2,g3)
    c: Coincident(g3,g0)
    c: Vertical(g0)
    c: Vertical(g2)
    c: Horizontal(g1)
    c: Horizontal(g3)
    c: Distance(g0,g2) = 6.5
    c: Distance(g1,g3) = 8
    c: DistanceX(g-1,g0) = 1.5
    c: DistanceY(g0,g-1) = 25
    c: Coincident(g4,g5)
    c: Coincident(g5,g6)
    c: Coincident(g6,g7)
    c: Coincident(g7,g4)
    c: Vertical(g4)
    c: Vertical(g6)
    c: Horizontal(g5)
    c: Horizontal(g7)
    c: Distance(g4,g6) = 6.5
    c: Distance(g5,g7) = 8
    c: DistanceX(g6,g-3) = 1.5
    c: PointOnObject(g4,g3)
    c: Coincident(g8,g9)
    c: Coincident(g9,g10)
    c: Coincident(g10,g11)
    c: Coincident(g11,g8)
    c: Horizontal(g8)
    c: Horizontal(g10)
    c: Vertical(g9)
    c: Vertical(g11)
    c: Distance(g9,g11) = 6.5
    c: Distance(g8,g10) = 6.5
    c: PointOnObject(g10,g0)
    c: DistanceY(g-3,g8) = 1.5
    c: Coincident(g12,g13)
    c: Coincident(g13,g14)
    c: Coincident(g14,g15)
    c: Coincident(g15,g12)
    c: Vertical(g12)
    c: Vertical(g14)
    c: Horizontal(g13)
    c: Horizontal(g15)
    c: Distance(g12,g14) = 6.5
    c: Distance(g13,g15) = 6.5
    c: PointOnObject(g12,g10)
    c: PointOnObject(g14,g6)
FEATURE [PartDesign::Pad] Pad026
  BaseFeature = -> Pocket
  Direction = (0,0,-1)
  Length = 6.8
  Length2 = 10
  Profile = -> Sketch043
  ReferenceAxis = -> Sketch043 [N_Axis]
  Refine = true
  Suppressed = false
  Type = 0
FEATURE [PartDesign::SubShapeBinder] Binder020
  BindCopyOnChange = 0
  BindMode = 0
  ClaimChildren = false
  Context = -> Part001 [Body001.Binder020.]
  Fuse = false
  MakeFace = true
  OffsetFill = false
  OffsetIntersection = false
  OffsetJoinType = 0
  OffsetOpenResult = false
  PartialLoad = false
  Refine = true
  Relative = true
  Support = -> [RetroConsoleMk2_1[Part__Feature255.]]
  _Version = 2
FEATURE [Sketcher::SketchObject] Sketch044
  ArcFitTolerance = 1e-06
  AttachmentSupport = -> [Pocket016]
  ExternalGeometry = -> [Pocket016,Binder020]
  FullyConstrained = true
  MakeInternals = false
  MapMode = 5
  Placement = pos=(0,135.8,-3.4e-14) rot=(0,0.707107,0.707107;3.14159rad)
  sketch-geometry (4):
    g0: LineSegment StartX=-120.6 StartY=0 StartZ=0 EndX=-120.6 EndY=-26.4 EndZ=0
    g1: LineSegment StartX=-120.6 StartY=-26.4 StartZ=0 EndX=-7.2 EndY=-26.4 EndZ=0
    g2: LineSegment StartX=-7.2 StartY=-26.4 StartZ=0 EndX=-7.2 EndY=0 EndZ=0
    g3: LineSegment StartX=-7.2 StartY=0 StartZ=0 EndX=-120.6 EndY=0 EndZ=0
  constraints (12):
    c: Coincident(g0,g1)
    c: Coincident(g1,g2)
    c: Coincident(g2,g3)
    c: Coincident(g3,g0)
    c: Vertical(g0)
    c: Vertical(g2)
    c: Horizontal(g1)
    c: Horizontal(g3)
    c: PointOnObject(g0,g-3)
    c: PointOnObject(g1,g-6)
    c: DistanceX(g0,g-6) = 1
    c: DistanceX(g-6,g1) = 1
FEATURE [PartDesign::Pocket] Pocket017
  BaseFeature = -> Pocket016
  Direction = (0,-1,2e-16)
  Length = 1.4
  Length2 = 5
  Profile = -> Sketch044
  ReferenceAxis = -> Sketch044 [N_Axis]
  Refine = true
  Suppressed = false
  Type = 0
FEATURE [Sketcher::SketchObject] Sketch045
  ArcFitTolerance = 1e-06
  AttachmentSupport = -> [Pocket017]
  ExternalGeometry = -> [Binder020]
  FullyConstrained = true
  MakeInternals = false
  MapMode = 5
  Placement = pos=(0,0,-32) rot=(0,0,1;0rad)
  sketch-geometry (20):
    g0: Circle CenterX=13.2 CenterY=129.1 CenterZ=0 NormalX=0 NormalY=0 NormalZ=1 AngleXU=0 Radius=2.2
    g1: Circle CenterX=114.45 CenterY=129.35 CenterZ=0 NormalX=0 NormalY=0 NormalZ=1 AngleXU=0 Radius=2.2
    g2: Circle CenterX=32.7 CenterY=8.18114 CenterZ=0 NormalX=0 NormalY=0 NormalZ=1 AngleXU=0 Radius=2.2
    g3: Circle CenterX=96.2 CenterY=8.18114 CenterZ=0 NormalX=0 NormalY=0 NormalZ=1 AngleXU=0 Radius=2.2
    g4: Circle CenterX=13.2 CenterY=129.1 CenterZ=0 NormalX=0 NormalY=0 NormalZ=1 AngleXU=0 Radius=3.25
    g5: Circle CenterX=114.45 CenterY=129.35 CenterZ=0 NormalX=0 NormalY=0 NormalZ=1 AngleXU=0 Radius=3.25
    g6: Circle CenterX=32.7 CenterY=8.18114 CenterZ=0 NormalX=0 NormalY=0 NormalZ=1 AngleXU=0 Radius=3.25
    g7: Circle CenterX=96.2 CenterY=8.18114 CenterZ=0 NormalX=0 NormalY=0 NormalZ=1 AngleXU=0 Radius=3.25
    g8: LineSegment StartX=43.025 StartY=92.55 StartZ=0 EndX=43.025 EndY=66.75 EndZ=0
    g9: LineSegment StartX=43.025 StartY=66.75 StartZ=0 EndX=82.3 EndY=66.75 EndZ=0
    g10: LineSegment StartX=82.3 StartY=66.75 StartZ=0 EndX=82.3 EndY=92.55 EndZ=0
    g11: LineSegment StartX=82.3 StartY=92.55 StartZ=0 EndX=43.025 EndY=92.55 EndZ=0
    g12: LineSegment StartX=41.025 StartY=94.55 StartZ=0 EndX=41.025 EndY=64.75 EndZ=0
    g13: LineSegment StartX=41.025 StartY=64.75 StartZ=0 EndX=84.3 EndY=64.75 EndZ=0
    g14: LineSegment StartX=84.3 StartY=64.75 StartZ=0 EndX=84.3 EndY=94.55 EndZ=0
    g15: LineSegment StartX=84.3 StartY=94.55 StartZ=0 EndX=41.025 EndY=94.55 EndZ=0
    g16: LineSegment [constr] StartX=53.025 StartY=79.65 StartZ=0 EndX=43.025 EndY=79.65 EndZ=0
    g17: LineSegment [constr] StartX=53.65 StartY=66.75 StartZ=0 EndX=53.65 EndY=76.75 EndZ=0
    g18: LineSegment [constr] StartX=72.3 StartY=80.9 StartZ=0 EndX=82.3 EndY=80.9 EndZ=0
    g19: LineSegment [constr] StartX=71.65 StartY=92.55 StartZ=0 EndX=71.65 EndY=82.55 EndZ=0
  constraints (56):
    c: Diameter(g0) = 4.4
    c: Diameter(g1) = 4.4
    c: Diameter(g2) = 4.4
    c: Diameter(g3) = 4.4
    c: Coincident(g0,g-3)
    c: Coincident(g1,g-4)
    c: Coincident(g2,g-5)
    c: Coincident(g3,g-6)
    c: Diameter(g4) = 6.5
    c: Diameter(g5) = 6.5
    c: Diameter(g6) = 6.5
    c: Diameter(g7) = 6.5
    c: Coincident(g4,g0)
    c: Coincident(g5,g1)
    c: Coincident(g6,g2)
    c: Coincident(g7,g3)
    c: Coincident(g8,g9)
    c: Coincident(g9,g10)
    c: Coincident(g10,g11)
    c: Coincident(g11,g8)
    c: Vertical(g8)
    c: Vertical(g10)
    c: Horizontal(g9)
    c: Horizontal(g11)
    c: Coincident(g12,g13)
    c: Coincident(g13,g14)
    c: Coincident(g14,g15)
    c: Coincident(g15,g12)
    c: Vertical(g12)
    c: Vertical(g14)
    c: Horizontal(g13)
    c: Horizontal(g15)
    c: DistanceY(g12,g8) = 2
    c: DistanceX(g12,g8) = 2
    c: DistanceY(g10,g14) = 2
    c: DistanceX(g9,g13) = 2
    c: PointOnObject(g16,g-7)
    c: PointOnObject(g16,g8)
    c: Horizontal(g16)
    c: PointOnObject(g-7,g16)
    c: PointOnObject(g17,g9)
    c: PointOnObject(g17,g-8)
    c: Vertical(g17)
    c: PointOnObject(g-8,g17)
    c: PointOnObject(g18,g-10)
    c: Horizontal(g18)
    c: PointOnObject(g18,g10)
    c: PointOnObject(g-10,g18)
    c: PointOnObject(g19,g11)
    c: PointOnObject(g19,g-9)
    c: Vertical(g19)
    c: PointOnObject(g-9,g19)
    c: DistanceX(g16,g16) = 10
    c: DistanceY(g17,g17) = 10
    c: DistanceX(g18,g18) = 10
    c: DistanceY(g19,g19) = 10
FEATURE [PartDesign::Pocket] Pocket018
  BaseFeature = -> Pocket017
  Direction = (0,0,-1)
  Length = 2
  Length2 = 5
  Profile = -> Sketch045 [Edge2,Edge1,Edge3,Edge4]
  ReferenceAxis = -> Sketch045 [N_Axis]
  Refine = true
  Suppressed = false
  Type = 0
FEATURE [PartDesign::Pad] Pad027
  BaseFeature = -> Pocket018
  Direction = (0,0,1)
  Length = 4
  Length2 = 10
  Profile = -> Sketch045
  ReferenceAxis = -> Sketch045 [N_Axis]
  Refine = true
  Suppressed = false
  Type = 0
FEATURE [Sketcher::SketchObject] Sketch046
  ArcFitTolerance = 1e-06
  AttachmentSupport = -> [Pad027]
  ExternalGeometry = -> [Pad027]
  FullyConstrained = true
  MakeInternals = false
  MapMode = 5
  Placement = pos=(0,0,-35.2) rot=(1,0,0;3.14159rad)
  sketch-geometry (16):
    g0: LineSegment [constr] StartX=1.4 StartY=-25 StartZ=0 EndX=8 EndY=-33 EndZ=0
    g1: LineSegment [constr] StartX=1.4 StartY=-33 StartZ=0 EndX=8 EndY=-25 EndZ=0
    g2: Circle CenterX=4.7 CenterY=-29 CenterZ=0 NormalX=0 NormalY=0 NormalZ=1 AngleXU=0 Radius=1.75
    g3: Circle CenterX=4.7 CenterY=-29 CenterZ=0 NormalX=0 NormalY=0 NormalZ=1 AngleXU=0 Radius=2.875
    g4: LineSegment [constr] StartX=119.8 StartY=-25 StartZ=0 EndX=126.4 EndY=-33 EndZ=0
    g5: LineSegment [constr] StartX=119.8 StartY=-33 StartZ=0 EndX=126.4 EndY=-25 EndZ=0
    g6: Circle CenterX=123.1 CenterY=-29 CenterZ=0 NormalX=0 NormalY=0 NormalZ=1 AngleXU=0 Radius=1.75
    g7: Circle CenterX=123.1 CenterY=-29 CenterZ=0 NormalX=0 NormalY=0 NormalZ=1 AngleXU=0 Radius=2.875
    g8: LineSegment [constr] StartX=1.4 StartY=-127.8 StartZ=0 EndX=8 EndY=-134.4 EndZ=0
    g9: LineSegment [constr] StartX=8 StartY=-127.8 StartZ=0 EndX=4.7 EndY=-131.1 EndZ=0
    g10: Circle CenterX=4.7 CenterY=-131.1 CenterZ=0 NormalX=0 NormalY=0 NormalZ=1 AngleXU=0 Radius=1.75
    g11: Circle CenterX=4.7 CenterY=-131.1 CenterZ=0 NormalX=0 NormalY=0 NormalZ=1 AngleXU=0 Radius=2.875
    g12: LineSegment [constr] StartX=126.4 StartY=-127.8 StartZ=0 EndX=119.8 EndY=-134.4 EndZ=0
    g13: LineSegment [constr] StartX=119.8 StartY=-127.8 StartZ=0 EndX=123.1 EndY=-131.1 EndZ=0
    g14: Circle CenterX=123.1 CenterY=-131.1 CenterZ=0 NormalX=0 NormalY=0 NormalZ=1 AngleXU=0 Radius=1.75
    g15: Circle CenterX=123.1 CenterY=-131.1 CenterZ=0 NormalX=0 NormalY=0 NormalZ=1 AngleXU=0 Radius=2.875
  constraints (36):
    c: Coincident(g0,g-4)
    c: Coincident(g0,g-3)
    c: Coincident(g1,g-4)
    c: Coincident(g1,g-3)
    c: Diameter(g2) = 3.5
    c: PointOnObject(g2,g0)
    c: PointOnObject(g2,g1)
    c: Diameter(g3) = 5.75
    c: PointOnObject(g3,g0)
    c: PointOnObject(g3,g1)
    c: Coincident(g4,g-5)
    c: Coincident(g4,g-6)
    c: Coincident(g5,g-5)
    c: Coincident(g5,g-6)
    c: Diameter(g6) = 3.5
    c: Diameter(g7) = 5.75
    c: PointOnObject(g6,g5)
    c: PointOnObject(g6,g4)
    c: PointOnObject(g7,g4)
    c: PointOnObject(g7,g5)
    c: Coincident(g8,g-9)
    c: Coincident(g8,g-10)
    c: Coincident(g9,g-10)
    c: Symmetric(g8,g8,g9)
    c: Diameter(g10) = 3.5
    c: Diameter(g11) = 5.75
    c: Coincident(g10,g9)
    c: Coincident(g11,g9)
    c: Coincident(g12,g-7)
    c: Coincident(g12,g-8)
    c: Coincident(g13,g-8)
    c: Symmetric(g12,g12,g13)
    c: Diameter(g14) = 3.5
    c: Diameter(g15) = 5.75
    c: Coincident(g14,g13)
    c: Coincident(g15,g13)
FEATURE [PartDesign::Pocket] Pocket019
  BaseFeature = -> Pad027
  Direction = (0,0,1)
  Length = 35
  Length2 = 5
  Profile = -> Sketch046 [Edge7,Edge5,Edge1,Edge3]
  ReferenceAxis = -> Sketch046 [N_Axis]
  Refine = true
  Suppressed = false
  Type = 0
FEATURE [PartDesign::Pocket] Pocket020
  BaseFeature = -> Pocket019
  Direction = (0,0,1)
  Length = 25
  Length2 = 5
  Profile = -> Sketch046
  ReferenceAxis = -> Sketch046 [N_Axis]
  Refine = true
  Suppressed = false
  Type = 0
FEATURE [TechDraw::DrawSVGTemplate] Template004
  Height = 210
  Orientation = 1
  Template = /Applications/FreeCAD.app/Contents/Resources/share/Mod/TechDraw/Templates/Default_Template_A4_Landscape.svg
  Width = 297
FEATURE [PartDesign::SubShapeBinder] Binder021
  BindCopyOnChange = 0
  BindMode = 0
  ClaimChildren = false
  Context = -> Body019 [Binder021.]
  Fuse = false
  MakeFace = true
  OffsetFill = false
  OffsetIntersection = false
  OffsetJoinType = 0
  OffsetOpenResult = false
  PartialLoad = false
  Refine = true
  Relative = true
  Support = -> [RetroConsoleMk2_1[SJ3_35083B_TR.,PJ_114AH_SMT_TR.,HDMI_A_Molex_208658_1001_Horizontal.],Part001[Body001.]]
  _Version = 2
FEATURE [Sketcher::SketchObject] Sketch047
  ArcFitTolerance = 1e-06
  AttachmentSupport = -> [Binder021]
  ExternalGeometry = -> [Binder021]
  FullyConstrained = true
  MakeInternals = false
  MapMode = 5
  Placement = pos=(0,135.8,-3.4e-14) rot=(0,0.707107,0.707107;3.14159rad)
  sketch-geometry (28):
    g0: LineSegment StartX=-120.5 StartY=-0.1 StartZ=0 EndX=-120.5 EndY=-26.3 EndZ=0
    g1: LineSegment StartX=-7.3 StartY=-26.3 StartZ=0 EndX=-7.3 EndY=-0.1 EndZ=0
    g2: LineSegment StartX=-7.3 StartY=-0.1 StartZ=0 EndX=-120.5 EndY=-0.1 EndZ=0
    g3: LineSegment StartX=-120.5 StartY=-26.3 StartZ=0 EndX=-68.4819 EndY=-26.3 EndZ=0
    g4: ArcOfCircle CenterX=-67.9745 CenterY=-23.75 CenterZ=0 NormalX=0 NormalY=0 NormalZ=1 AngleXU=0 Radius=2.6 StartAngle=4.90882 EndAngle=10.7991
    g5: LineSegment StartX=-67.4671 StartY=-26.3 StartZ=0 EndX=-32.3 EndY=-26.3 EndZ=0
    g6: LineSegment StartX=-32.3 StartY=-15.9343 StartZ=0 EndX=-32.3 EndY=-26.3 EndZ=0
    g7: ArcOfCircle CenterX=-31.6157 CenterY=-15.9343 CenterZ=0 NormalX=0 NormalY=0 NormalZ=1 AngleXU=0 Radius=0.684266 StartAngle=1.5708 EndAngle=3.14159
    g8: LineSegment StartX=-31.6157 StartY=-15.25 StartZ=0 EndX=-23.7843 EndY=-15.25 EndZ=0
    g9: ArcOfCircle CenterX=-23.7843 CenterY=-15.9343 CenterZ=0 NormalX=0 NormalY=0 NormalZ=1 AngleXU=0 Radius=0.684266 StartAngle=8.18479e-08 EndAngle=1.5708
    g10: LineSegment StartX=-23.1 StartY=-15.9343 StartZ=0 EndX=-23.1 EndY=-26.3 EndZ=0
    g11: LineSegment StartX=-7.3 StartY=-26.3 StartZ=0 EndX=-23.1 EndY=-26.3 EndZ=0
    g12: LineSegment StartX=-105.2 StartY=-19.86 StartZ=0 EndX=-92.2 EndY=-19.86 EndZ=0
    g13: LineSegment StartX=-90.9 StartY=-21.16 StartZ=0 EndX=-90.9 EndY=-24.7766 EndZ=0
    g14: LineSegment StartX=-106.5 StartY=-21.16 StartZ=0 EndX=-106.5 EndY=-24.7766 EndZ=0
    g15: ArcOfCircle CenterX=-105.2 CenterY=-21.16 CenterZ=0 NormalX=0 NormalY=0 NormalZ=1 AngleXU=0 Radius=1.3 StartAngle=1.5708 EndAngle=3.14159
    g16: ArcOfCircle CenterX=-92.2 CenterY=-21.16 CenterZ=0 NormalX=0 NormalY=0 NormalZ=1 AngleXU=0 Radius=1.3 StartAngle=-9e-16 EndAngle=1.5708
    g17: LineSegment StartX=-90.9 StartY=-24.7766 StartZ=0 EndX=-91.9387 EndY=-25.1209 EndZ=0
    g18: LineSegment [constr] StartX=-91.9387 StartY=-25.1209 StartZ=0 EndX=-92.0331 EndY=-24.8361 EndZ=0
    g19: LineSegment StartX=-91.9387 StartY=-25.1209 StartZ=0 EndX=-92.869 EndY=-25.774 EndZ=0
    g20: LineSegment [constr] StartX=-92.869 StartY=-25.774 StartZ=0 EndX=-93.0414 EndY=-25.5285 EndZ=0
    g21: ArcOfCircle CenterX=-93.616 CenterY=-24.71 CenterZ=0 NormalX=0 NormalY=0 NormalZ=1 AngleXU=0 Radius=1.3 StartAngle=4.71239 EndAngle=5.32448
    g22: LineSegment StartX=-93.616 StartY=-26.01 StartZ=0 EndX=-103.784 EndY=-26.01 EndZ=0
    g23: LineSegment StartX=-106.5 StartY=-24.7766 StartZ=0 EndX=-105.461 EndY=-25.1209 EndZ=0
    g24: LineSegment [constr] StartX=-105.461 StartY=-25.1209 StartZ=0 EndX=-105.367 EndY=-24.8361 EndZ=0
    g25: LineSegment StartX=-105.461 StartY=-25.1209 StartZ=0 EndX=-104.531 EndY=-25.774 EndZ=0
    g26: LineSegment [constr] StartX=-104.531 StartY=-25.774 StartZ=0 EndX=-104.359 EndY=-25.5284 EndZ=0
    g27: ArcOfCircle CenterX=-103.784 CenterY=-24.71 CenterZ=0 NormalX=0 NormalY=0 NormalZ=1 AngleXU=0 Radius=1.3 StartAngle=4.1003 EndAngle=4.71239
  constraints (86):
    c: Coincident(g1,g2)
    c: Coincident(g2,g0)
    c: Vertical(g0)
    c: Vertical(g1)
    c: Horizontal(g2)
    c: DistanceX(g-3,g0) = 0.1
    c: DistanceX(g1,g-4) = 0.1
    c: DistanceY(g0,g-3) = 0.1
    c: DistanceY(g-3,g0) = 0.1
    c: DistanceY(g-4,g1) = 0.1
    c: Horizontal(g3)
    c: Coincident(g3,g0)
    c: Radius(g-20) = 2.5
    c: Radius(g4) = 2.6
    c: Coincident(g4,g-23)
    c: Coincident(g3,g4)
    c: PointOnObject(g4,g3)
    c: Coincident(g5,g4)
    c: Horizontal(g5)
    c: Vertical(g6)
    c: DistanceX(g6,g-29) = 0.1
    c: Coincident(g5,g6)
    c: Radius(g-27) = 0.584266
    c: Coincident(g7,g-27)
    c: Coincident(g7,g6)
    c: Horizontal(g8)
    c: DistanceY(g-27,g8) = 0.1
    c: Coincident(g8,g7)
    c: Vertical(g7,g-27)
    c: Coincident(g9,g-28)
    c: Coincident(g8,g9)
    c: Vertical(g8,g-28)
    c: Vertical(g10)
    c: DistanceX(g-28,g10) = 0.1
    c: Coincident(g10,g9)
    c: Coincident(g11,g1)
    c: Horizontal(g11)
    c: Coincident(g10,g11)
    c: Horizontal(g12)
    c: Vertical(g13)
    c: Vertical(g14)
    c: Horizontal(g14,g-17)
    c: DistanceX(g14,g-17) = 0.3
    c: DistanceY(g-17,g12) = 0.3
    c: Coincident(g15,g-17)
    c: Coincident(g15,g14)
    c: Coincident(g15,g12)
    c: DistanceX(g-16,g13) = 0.3
    c: Horizontal(g13,g-16)
    c: Coincident(g16,g-16)
    c: Coincident(g16,g13)
    c: Coincident(g12,g16)
    c: Parallel(g17,g-15)
    c: Coincident(g18,g17)
    c: PointOnObject(g18,g-15)
    c: Perpendicular(g17,g18)
    c: Distance(g18,g18) = 0.3
    c: Coincident(g17,g13)
    c: Parallel(g19,g-14)
    c: Coincident(g20,g19)
    c: PointOnObject(g20,g-14)
    c: Perpendicular(g19,g20)
    c: Distance(g20,g20) = 0.3
    c: Coincident(g19,g17)
    c: Coincident(g21,g-13)
    c: Coincident(g21,g19)
    c: Horizontal(g22)
    c: DistanceY(g22,g-13) = 0.3
    c: Coincident(g22,g21)
    c: Vertical(g21,g-13)
    c: Parallel(g23,g-10)
    c: Coincident(g24,g23)
    c: PointOnObject(g24,g-10)
    c: Perpendicular(g23,g24)
    c: Distance(g24,g24) = 0.3
    c: Coincident(g23,g14)
    c: Parallel(g25,g-11)
    c: Coincident(g26,g25)
    c: PointOnObject(g26,g-11)
    c: Perpendicular(g25,g26)
    c: Distance(g26,g26) = 0.3
    c: Coincident(g25,g23)
    c: Coincident(g27,g-12)
    c: Coincident(g27,g25)
    c: Coincident(g27,g22)
    c: Vertical(g22,g-12)
FEATURE [PartDesign::Pad] Pad028
  Direction = (0,1,-2e-16)
  Length = 1.4
  Length2 = 10
  Profile = -> Sketch047
  ReferenceAxis = -> Sketch047 [N_Axis]
  Refine = true
  Reversed = true
  Suppressed = false
  Type = 0
FEATURE [PartDesign::SubShapeBinder] Binder022
  BindCopyOnChange = 0
  BindMode = 0
  ClaimChildren = false
  Context = -> Body019 [Binder022.]
  Fuse = false
  MakeFace = true
  OffsetFill = false
  OffsetIntersection = false
  OffsetJoinType = 0
  OffsetOpenResult = false
  PartialLoad = false
  Refine = true
  Relative = true
  Support = -> [RetroConsoleMk2_1[Part__Feature255.]]
  _Version = 2
FEATURE [Sketcher::SketchObject] Sketch048
  ArcFitTolerance = 1e-06
  AttachmentOffset = pos=(0,0,0.1) rot=(0,0,1;0rad)
  AttachmentSupport = -> [Binder022]
  ExternalGeometry = -> [Binder022,Pad028]
  FullyConstrained = true
  MakeInternals = false
  MapMode = 5
  Placement = pos=(0,0,-26.3) rot=(0,0,1;0rad)
  sketch-geometry (12):
    g0: Circle CenterX=13.2 CenterY=129.1 CenterZ=0 NormalX=0 NormalY=0 NormalZ=1 AngleXU=0 Radius=1.75
    g1: Circle CenterX=114.45 CenterY=129.35 CenterZ=0 NormalX=0 NormalY=0 NormalZ=1 AngleXU=0 Radius=1.75
    g2: LineSegment StartX=18.2 StartY=134.4 StartZ=0 EndX=8.19999 EndY=134.4 EndZ=0
    g3: LineSegment StartX=8.19999 StartY=134.4 StartZ=0 EndX=8.19999 EndY=124.1 EndZ=0
    g4: LineSegment StartX=8.19999 StartY=124.1 StartZ=0 EndX=13.2 EndY=124.1 EndZ=0
    g5: ArcOfCircle CenterX=13.2 CenterY=129.1 CenterZ=0 NormalX=0 NormalY=0 NormalZ=1 AngleXU=0 Radius=5 StartAngle=4.71239 EndAngle=6.28319
    g6: LineSegment StartX=18.2 StartY=134.4 StartZ=0 EndX=18.2 EndY=129.1 EndZ=0
    g7: LineSegment StartX=109.45 StartY=134.4 StartZ=0 EndX=119.6 EndY=134.4 EndZ=0
    g8: LineSegment StartX=119.6 StartY=134.4 StartZ=0 EndX=119.6 EndY=124.35 EndZ=0
    g9: LineSegment StartX=119.6 StartY=124.35 StartZ=0 EndX=114.45 EndY=124.35 EndZ=0
    g10: ArcOfCircle CenterX=114.45 CenterY=129.35 CenterZ=0 NormalX=0 NormalY=0 NormalZ=1 AngleXU=0 Radius=5 StartAngle=3.14159 EndAngle=4.71239
    g11: LineSegment StartX=109.45 StartY=134.4 StartZ=0 EndX=109.45 EndY=129.35 EndZ=0
  constraints (34):
    c: Diameter(g0) = 3.5
    c: Coincident(g0,g-4)
    c: Diameter(g1) = 3.5
    c: Coincident(g1,g-3)
    c: PointOnObject(g2,g-5)
    c: PointOnObject(g2,g-5)
    c: Coincident(g3,g2)
    c: Vertical(g3)
    c: PointOnObject(g3,g-6)
    c: Coincident(g4,g3)
    c: Horizontal(g4)
    c: Vertical(g4,g0)
    c: DistanceY(g4,g0) = 5
    c: Coincident(g5,g0)
    c: Coincident(g5,g4)
    c: Coincident(g6,g2)
    c: Vertical(g6)
    c: Horizontal(g6,g0)
    c: Coincident(g5,g6)
    c: PointOnObject(g7,g-5)
    c: PointOnObject(g7,g-5)
    c: Coincident(g8,g7)
    c: Vertical(g8)
    c: PointOnObject(g8,g-7)
    c: Coincident(g9,g8)
    c: Horizontal(g9)
    c: Vertical(g9,g1)
    c: Coincident(g10,g1)
    c: Coincident(g10,g9)
    c: Coincident(g11,g7)
    c: Vertical(g11)
    c: Horizontal(g11,g1)
    c: Coincident(g11,g10)
    c: DistanceY(g9,g1) = 5
FEATURE [PartDesign::Pad] Pad029
  BaseFeature = -> Pad028
  Direction = (0,0,1)
  Length = 1
  Length2 = 10
  Profile = -> Sketch048
  ReferenceAxis = -> Sketch048 [N_Axis]
  Refine = true
  Suppressed = false
  Type = 0
FEATURE [Sketcher::SketchObject] Sketch049
  ArcFitTolerance = 1e-06
  AttachmentSupport = -> [Pad029]
  ExternalGeometry = -> [Pad029]
  FullyConstrained = true
  MakeInternals = false
  MapMode = 5
  Placement = pos=(8.19999,0,0) rot=(0.57735,-0.57735,-0.57735;2.0944rad)
  sketch-geometry (3):
    g0: LineSegment StartX=-134.4 StartY=-25.3 StartZ=0 EndX=-124.1 EndY=-25.3 EndZ=0
    g1: LineSegment StartX=-124.1 StartY=-25.3 StartZ=0 EndX=-134.4 EndY=-15 EndZ=0
    g2: LineSegment StartX=-134.4 StartY=-15 StartZ=0 EndX=-134.4 EndY=-25.3 EndZ=0
  constraints (7):
    c: Coincident(g-3,g0)
    c: Coincident(g0,g-3)
    c: Coincident(g0,g1)
    c: PointOnObject(g1,g-4)
    c: Coincident(g1,g2)
    c: Coincident(g2,g0)
    c: Angle(g1,g0) = 0.785398
FEATURE [PartDesign::Pad] Pad030
  BaseFeature = -> Pad029
  Direction = (-1,0,0)
  Length = 1
  Length2 = 10
  Profile = -> Sketch049
  ReferenceAxis = -> Sketch049 [N_Axis]
  Refine = true
  Reversed = true
  Suppressed = false
  Type = 0
FEATURE [Sketcher::SketchObject] Sketch050
  ArcFitTolerance = 1e-06
  AttachmentSupport = -> [Pad030]
  ExternalGeometry = -> [Pad030]
  FullyConstrained = true
  MakeInternals = false
  MapMode = 5
  Placement = pos=(119.6,0,0) rot=(0.57735,0.57735,0.57735;2.0944rad)
  sketch-geometry (3):
    g0: LineSegment StartX=124.35 StartY=-25.3 StartZ=0 EndX=134.4 EndY=-25.3 EndZ=0
    g1: LineSegment StartX=134.4 StartY=-25.3 StartZ=0 EndX=134.4 EndY=-15.25 EndZ=0
    g2: LineSegment StartX=134.4 StartY=-15.25 StartZ=0 EndX=124.35 EndY=-25.3 EndZ=0
  constraints (7):
    c: Coincident(g-3,g0)
    c: Coincident(g0,g-3)
    c: Coincident(g0,g1)
    c: PointOnObject(g1,g-4)
    c: Coincident(g1,g2)
    c: Coincident(g2,g0)
    c: Angle(g0,g2) = 0.785398
FEATURE [PartDesign::Pad] Pad031
  BaseFeature = -> Pad030
  Direction = (1,0,0)
  Length = 1
  Length2 = 10
  Profile = -> Sketch050
  ReferenceAxis = -> Sketch050 [N_Axis]
  Refine = true
  Reversed = true
  Suppressed = false
  Type = 0
FEATURE [PartDesign::Body] Body019  label="Backpanel"
  AllowCompound = false
  Group = -> [Binder021,Sketch047,Pad028,Binder022,Sketch048,Pad029,Sketch049,Pad030,Sketch050,Pad031]
  Origin = -> Origin289
  Tip = -> Pad031
FEATURE [Sketcher::SketchObject] Sketch051
  ArcFitTolerance = 1e-06
  AttachmentSupport = -> [Pad026]
  ExternalGeometry = -> [Pad026]
  FullyConstrained = true
  MakeInternals = false
  MapMode = 5
  Placement = pos=(0,0,-6.8) rot=(1,0,0;3.14159rad)
  sketch-geometry (12):
    g0: LineSegment [constr] StartX=1.5 StartY=-25 StartZ=0 EndX=8 EndY=-33 EndZ=0
    g1: LineSegment [constr] StartX=1.5 StartY=-33 StartZ=0 EndX=8 EndY=-25 EndZ=0
    g2: Circle CenterX=4.75 CenterY=-29 CenterZ=0 NormalX=0 NormalY=0 NormalZ=1 AngleXU=0 Radius=2.2
    g3: LineSegment [constr] StartX=1.5 StartY=-127.8 StartZ=0 EndX=8 EndY=-134.3 EndZ=0
    g4: LineSegment [constr] StartX=8 StartY=-127.8 StartZ=0 EndX=4.75 EndY=-131.05 EndZ=0
    g5: Circle CenterX=4.75 CenterY=-131.05 CenterZ=0 NormalX=0 NormalY=0 NormalZ=1 AngleXU=0 Radius=2.2
    g6: LineSegment [constr] StartX=119.8 StartY=-134.3 StartZ=0 EndX=126.3 EndY=-127.8 EndZ=0
    g7: LineSegment [constr] StartX=119.8 StartY=-127.8 StartZ=0 EndX=123.05 EndY=-131.05 EndZ=0
    g8: Circle CenterX=123.05 CenterY=-131.05 CenterZ=0 NormalX=0 NormalY=0 NormalZ=1 AngleXU=0 Radius=2.2
    g9: LineSegment [constr] StartX=119.8 StartY=-25 StartZ=0 EndX=126.3 EndY=-33 EndZ=0
    g10: LineSegment [constr] StartX=119.8 StartY=-33 StartZ=0 EndX=126.3 EndY=-25 EndZ=0
    g11: Circle CenterX=123.05 CenterY=-29 CenterZ=0 NormalX=0 NormalY=0 NormalZ=1 AngleXU=0 Radius=2.2
  constraints (26):
    c: Coincident(g0,g-3)
    c: Coincident(g0,g-4)
    c: Coincident(g1,g-3)
    c: Coincident(g1,g-4)
    c: Diameter(g2) = 4.4
    c: PointOnObject(g2,g1)
    c: PointOnObject(g2,g0)
    c: Coincident(g3,g-5)
    c: Coincident(g3,g-6)
    c: Coincident(g4,g-6)
    c: Symmetric(g3,g3,g4)
    c: Diameter(g5) = 4.4
    c: Coincident(g5,g4)
    c: Coincident(g6,g-8)
    c: Coincident(g6,g-7)
    c: Coincident(g7,g-8)
    c: Symmetric(g6,g6,g7)
    c: Diameter(g8) = 4.4
    c: Coincident(g8,g7)
    c: Coincident(g9,g-9)
    c: Coincident(g9,g-10)
    c: Coincident(g10,g-9)
    c: Coincident(g10,g-10)
    c: Diameter(g11) = 4.4
    c: PointOnObject(g11,g10)
    c: PointOnObject(g11,g9)
FEATURE [PartDesign::Pocket] Pocket021
  BaseFeature = -> Pad026
  Direction = (0,0,1)
  Length = 7
  Length2 = 5
  Profile = -> Sketch051
  ReferenceAxis = -> Sketch051 [N_Axis]
  Refine = true
  Suppressed = false
  Type = 0
FEATURE [Sketcher::SketchObject] Sketch052
  ArcFitTolerance = 1e-06
  AttachmentSupport = -> [Pocket021]
  ExternalGeometry = -> [Pocket021]
  FullyConstrained = true
  MakeInternals = false
  MapMode = 5
  Placement = pos=(0,0,0) rot=(1,0,0;3.14159rad)
  sketch-geometry (32):
    g0: LineSegment StartX=47.85 StartY=-53.65 StartZ=0 EndX=47.85 EndY=-58.65 EndZ=0
    g1: LineSegment StartX=47.85 StartY=-58.65 StartZ=0 EndX=49.85 EndY=-58.65 EndZ=0
    g2: LineSegment StartX=49.85 StartY=-58.65 StartZ=0 EndX=49.85 EndY=-53.65 EndZ=0
    g3: LineSegment StartX=49.85 StartY=-53.65 StartZ=0 EndX=47.85 EndY=-53.65 EndZ=0
    g4: LineSegment StartX=52.69 StartY=-53.65 StartZ=0 EndX=52.69 EndY=-58.65 EndZ=0
    g5: LineSegment StartX=52.69 StartY=-58.65 StartZ=0 EndX=54.69 EndY=-58.65 EndZ=0
    g6: LineSegment StartX=54.69 StartY=-58.65 StartZ=0 EndX=54.69 EndY=-53.65 EndZ=0
    g7: LineSegment StartX=54.69 StartY=-53.65 StartZ=0 EndX=52.69 EndY=-53.65 EndZ=0
    g8: LineSegment StartX=73.11 StartY=-53.65 StartZ=0 EndX=73.11 EndY=-58.65 EndZ=0
    g9: LineSegment StartX=73.11 StartY=-58.65 StartZ=0 EndX=75.11 EndY=-58.65 EndZ=0
    g10: LineSegment StartX=75.11 StartY=-58.65 StartZ=0 EndX=75.11 EndY=-53.65 EndZ=0
    g11: LineSegment StartX=75.11 StartY=-53.65 StartZ=0 EndX=73.11 EndY=-53.65 EndZ=0
    g12: LineSegment StartX=77.95 StartY=-53.65 StartZ=0 EndX=77.95 EndY=-58.65 EndZ=0
    g13: LineSegment StartX=77.95 StartY=-58.65 StartZ=0 EndX=79.95 EndY=-58.65 EndZ=0
    g14: LineSegment StartX=79.95 StartY=-58.65 StartZ=0 EndX=79.95 EndY=-53.65 EndZ=0
    g15: LineSegment StartX=79.95 StartY=-53.65 StartZ=0 EndX=77.95 EndY=-53.65 EndZ=0
    g16: LineSegment StartX=47.85 StartY=-100.75 StartZ=0 EndX=47.85 EndY=-105.75 EndZ=0
    g17: LineSegment StartX=47.85 StartY=-105.75 StartZ=0 EndX=49.85 EndY=-105.75 EndZ=0
    g18: LineSegment StartX=49.85 StartY=-105.75 StartZ=0 EndX=49.85 EndY=-100.75 EndZ=0
    g19: LineSegment StartX=49.85 StartY=-100.75 StartZ=0 EndX=47.85 EndY=-100.75 EndZ=0
    g20: LineSegment StartX=52.69 StartY=-100.75 StartZ=0 EndX=52.69 EndY=-105.75 EndZ=0
    g21: LineSegment StartX=52.69 StartY=-105.75 StartZ=0 EndX=54.69 EndY=-105.75 EndZ=0
    g22: LineSegment StartX=54.69 StartY=-105.75 StartZ=0 EndX=54.69 EndY=-100.75 EndZ=0
    g23: LineSegment StartX=54.69 StartY=-100.75 StartZ=0 EndX=52.69 EndY=-100.75 EndZ=0
    g24: LineSegment StartX=73.11 StartY=-100.75 StartZ=0 EndX=73.11 EndY=-105.75 EndZ=0
    g25: LineSegment StartX=73.11 StartY=-105.75 StartZ=0 EndX=75.11 EndY=-105.75 EndZ=0
    g26: LineSegment StartX=75.11 StartY=-105.75 StartZ=0 EndX=75.11 EndY=-100.75 EndZ=0
    g27: LineSegment StartX=75.11 StartY=-100.75 StartZ=0 EndX=73.11 EndY=-100.75 EndZ=0
    g28: LineSegment StartX=77.95 StartY=-100.75 StartZ=0 EndX=77.95 EndY=-105.75 EndZ=0
    g29: LineSegment StartX=77.95 StartY=-105.75 StartZ=0 EndX=79.95 EndY=-105.75 EndZ=0
    g30: LineSegment StartX=79.95 StartY=-105.75 StartZ=0 EndX=79.95 EndY=-100.75 EndZ=0
    g31: LineSegment StartX=79.95 StartY=-100.75 StartZ=0 EndX=77.95 EndY=-100.75 EndZ=0
  constraints (96):
    c: Coincident(g0,g1)
    c: Coincident(g1,g2)
    c: Coincident(g2,g3)
    c: Coincident(g3,g0)
    c: Vertical(g0)
    c: Vertical(g2)
    c: Horizontal(g1)
    c: Horizontal(g3)
    c: Distance(g0,g2) = 2
    c: Distance(g1,g3) = 5
    c: Coincident(g4,g5)
    c: Coincident(g5,g6)
    c: Coincident(g6,g7)
    c: Coincident(g7,g4)
    c: Vertical(g4)
    c: Vertical(g6)
    c: Horizontal(g5)
    c: Horizontal(g7)
    c: Distance(g4,g6) = 2
    c: Distance(g5,g7) = 5
    c: Coincident(g8,g9)
    c: Coincident(g9,g10)
    c: Coincident(g10,g11)
    c: Coincident(g11,g8)
    c: Vertical(g8)
    c: Vertical(g10)
    c: Horizontal(g9)
    c: Horizontal(g11)
    c: Distance(g8,g10) = 2
    c: Distance(g9,g11) = 5
    c: Coincident(g12,g13)
    c: Coincident(g13,g14)
    c: Coincident(g14,g15)
    c: Coincident(g15,g12)
    c: Vertical(g12)
    c: Vertical(g14)
    c: Horizontal(g13)
    c: Horizontal(g15)
    c: Distance(g12,g14) = 2
    c: Distance(g13,g15) = 5
    c: Coincident(g16,g17)
    c: Coincident(g17,g18)
    c: Coincident(g18,g19)
    c: Coincident(g19,g16)
    c: Vertical(g16)
    c: Vertical(g18)
    c: Horizontal(g17)
    c: Horizontal(g19)
    c: Distance(g16,g18) = 2
    c: Distance(g17,g19) = 5
    c: Coincident(g20,g21)
    c: Coincident(g21,g22)
    c: Coincident(g22,g23)
    c: Coincident(g23,g20)
    c: Vertical(g20)
    c: Vertical(g22)
    c: Horizontal(g21)
    c: Horizontal(g23)
    c: Distance(g20,g22) = 2
    c: Distance(g21,g23) = 5
    c: Coincident(g24,g25)
    c: Coincident(g25,g26)
    c: Coincident(g26,g27)
    c: Coincident(g27,g24)
    c: Vertical(g24)
    c: Vertical(g26)
    c: Horizontal(g25)
    c: Horizontal(g27)
    c: Distance(g24,g26) = 2
    c: Distance(g25,g27) = 5
    c: Coincident(g28,g29)
    c: Coincident(g29,g30)
    c: Coincident(g30,g31)
    c: Coincident(g31,g28)
    c: Vertical(g28)
    c: Vertical(g30)
    c: Horizontal(g29)
    c: Horizontal(g31)
    c: Distance(g28,g30) = 2
    c: Distance(g29,g31) = 5
    c: PointOnObject(g-3,g14)
    c: DistanceY(g-3,g14) = 10
    c: PointOnObject(g10,g15)
    c: DistanceX(g10,g12) = 2.84
    c: PointOnObject(g-3,g0)
    c: DistanceY(g-3,g0) = 10
    c: PointOnObject(g2,g7)
    c: DistanceX(g2,g4) = 2.84
    c: PointOnObject(g-4,g16)
    c: DistanceY(g16,g-4) = 10
    c: PointOnObject(g20,g17)
    c: DistanceX(g17,g20) = 2.84
    c: PointOnObject(g-4,g30)
    c: DistanceY(g29,g-4) = 10
    c: PointOnObject(g25,g29)
    c: DistanceX(g25,g28) = 2.84
FEATURE [PartDesign::Pad] Pad032
  BaseFeature = -> Pocket021
  Direction = (0,0,-1)
  Length = 5
  Length2 = 10
  Profile = -> Sketch052
  ReferenceAxis = -> Sketch052 [N_Axis]
  Refine = true
  Suppressed = false
  Type = 0
FEATURE [PartDesign::Pad] Pad033
  BaseFeature = -> Pad032
  Direction = (-1,0,0)
  Length = 2
  Length2 = 10
  Profile = -> Pad032 [Face22]
  Refine = true
  Suppressed = false
  Type = 0
FEATURE [PartDesign::Pad] Pad034
  BaseFeature = -> Pad033
  Direction = (1,0,0)
  Length = 2
  Length2 = 10
  Profile = -> Pad033 [Face62]
  Refine = true
  Suppressed = false
  Type = 0
FEATURE [Sketcher::SketchObject] Sketch053
  ArcFitTolerance = 1e-06
  AttachmentSupport = -> [Pad034]
  ExternalGeometry = -> [Pad034]
  FullyConstrained = true
  MakeInternals = false
  MapMode = 5
  Placement = pos=(45.85,0,0) rot=(0.57735,-0.57735,-0.57735;2.0944rad)
  sketch-geometry (3):
    g0: LineSegment [constr] StartX=-58.65 StartY=-5 StartZ=0 EndX=-53.65 EndY=-3e-16 EndZ=0
    g1: LineSegment [constr] StartX=-53.65 StartY=-5 StartZ=0 EndX=-56.15 EndY=-2.5 EndZ=0
    g2: Circle CenterX=-56.15 CenterY=-2.5 CenterZ=0 NormalX=0 NormalY=0 NormalZ=1 AngleXU=0 Radius=1.65
  constraints (6):
    c: Coincident(g0,g-3)
    c: Coincident(g0,g-4)
    c: Coincident(g1,g-3)
    c: Symmetric(g0,g0,g1)
    c: Diameter(g2) = 3.3
    c: Coincident(g2,g1)
FEATURE [PartDesign::Pad] Pad035
  BaseFeature = -> Pad034
  Direction = (-1,0,0)
  Length = 6
  Length2 = 10
  Profile = -> Sketch053
  ReferenceAxis = -> Sketch053 [N_Axis]
  Refine = true
  Suppressed = false
  Type = 0
FEATURE [Sketcher::SketchObject] Sketch054
  ArcFitTolerance = 1e-06
  AttachmentSupport = -> [Pad035]
  ExternalGeometry = -> [Pad035]
  FullyConstrained = true
  MakeInternals = false
  MapMode = 5
  Placement = pos=(81.95,0,0) rot=(0.57735,0.57735,0.57735;2.0944rad)
  sketch-geometry (3):
    g0: LineSegment [constr] StartX=100.75 StartY=-5 StartZ=0 EndX=105.75 EndY=-1e-16 EndZ=0
    g1: LineSegment [constr] StartX=105.75 StartY=-5 StartZ=0 EndX=103.25 EndY=-2.5 EndZ=0
    g2: Circle CenterX=103.25 CenterY=-2.5 CenterZ=0 NormalX=0 NormalY=0 NormalZ=1 AngleXU=0 Radius=1.65
  constraints (6):
    c: Coincident(g0,g-3)
    c: Coincident(g0,g-4)
    c: Coincident(g1,g-3)
    c: Symmetric(g0,g0,g1)
    c: Diameter(g2) = 3.3
    c: Coincident(g2,g1)
FEATURE [PartDesign::Pad] Pad036
  BaseFeature = -> Pad035
  Direction = (1,0,0)
  Length = 6
  Length2 = 10
  Profile = -> Sketch054
  ReferenceAxis = -> Sketch054 [N_Axis]
  Refine = true
  Suppressed = false
  Type = 0
FEATURE [PartDesign::Plane] DatumPlane001
  AttachmentOffset = pos=(0,0,0) rot=(1,0,0;1.5708rad)
  AttachmentSupport = -> [Pad036]
  Length = 192.15
  MapMode = 45
  Placement = pos=(84.95,103.25,-2.5) rot=(0.707107,0.707107,0;3.14159rad)
  ResizeMode = 0
  Width = 184.15
FEATURE [Sketcher::SketchObject] Sketch055
  ArcFitTolerance = 1e-06
  AttachmentSupport = -> [DatumPlane001]
  FullyConstrained = false
  MakeInternals = false
  MapMode = 5
  Placement = pos=(84.95,103.25,-2.5) rot=(0.707107,0.707107,0;3.14159rad)
  sketch-geometry (1):
    g0: Circle CenterX=1.67982 CenterY=0 CenterZ=0 NormalX=0 NormalY=0 NormalZ=1 AngleXU=0 Radius=0.5
  constraints (2):
    c: Diameter(g0) = 1
    c: PointOnObject(g0,g-1)
FEATURE [PartDesign::Groove] Groove
  Angle = 360
  Angle2 = 60
  Axis = (1,-2e-16,0)
  Base = (84.95,103.25,-2.5)
  BaseFeature = -> Pad036
  Profile = -> Sketch055
  ReferenceAxis = -> Sketch055 [V_Axis]
  Refine = true
  Suppressed = false
  Type = 0
FEATURE [PartDesign::Plane] DatumPlane002
  AttachmentOffset = pos=(0,0,0) rot=(1,0,0;1.5708rad)
  AttachmentSupport = -> [Groove]
  Length = 192.15
  MapMode = 45
  Placement = pos=(42.85,56.15,-2.5) rot=(0.707107,0.707107,0;3.14159rad)
  ResizeMode = 0
  Width = 184.15
FEATURE [Sketcher::SketchObject] Sketch056
  ArcFitTolerance = 1e-06
  AttachmentSupport = -> [DatumPlane002]
  FullyConstrained = false
  MakeInternals = false
  MapMode = 5
  Placement = pos=(42.85,56.15,-2.5) rot=(0.707107,0.707107,0;3.14159rad)
  sketch-geometry (1):
    g0: Circle CenterX=1.63266 CenterY=0 CenterZ=0 NormalX=0 NormalY=0 NormalZ=1 AngleXU=0 Radius=0.5
  constraints (2):
    c: Diameter(g0) = 1
    c: PointOnObject(g0,g-1)
FEATURE [PartDesign::Groove] Groove001
  Angle = 360
  Angle2 = 60
  Axis = (1,-2e-16,0)
  Base = (42.85,56.15,-2.5)
  BaseFeature = -> Groove
  Profile = -> Sketch056
  ReferenceAxis = -> Sketch056 [V_Axis]
  Refine = true
  Suppressed = false
  Type = 0
FEATURE [PartDesign::SubtractiveSphere] Sphere
  Angle1 = -90
  Angle2 = 90
  Angle3 = 360
  AttacherType = Attacher::AttachEngine3D
  AttachmentSupport = -> [Groove001]
  BaseFeature = -> Groove001
  MapMode = 45
  Placement = pos=(49.85,103.25,-2.5) rot=(0.57735,0.57735,0.57735;2.0944rad)
  Radius = 1
  Refine = true
  Suppressed = false
FEATURE [PartDesign::SubtractiveSphere] Sphere001
  Angle1 = -90
  Angle2 = 90
  Angle3 = 360
  AttacherType = Attacher::AttachEngine3D
  AttachmentSupport = -> [Sphere]
  BaseFeature = -> Sphere
  MapMode = 45
  Placement = pos=(77.95,103.25,-2.5) rot=(0.57735,0.57735,0.57735;2.0944rad)
  Radius = 1
  Refine = true
  Suppressed = false
FEATURE [PartDesign::SubtractiveSphere] Sphere002
  Angle1 = -90
  Angle2 = 90
  Angle3 = 360
  AttacherType = Attacher::AttachEngine3D
  AttachmentSupport = -> [Sphere001]
  BaseFeature = -> Sphere001
  MapMode = 45
  Placement = pos=(77.95,56.15,-2.5) rot=(0.57735,0.57735,0.57735;2.0944rad)
  Radius = 1
  Refine = true
  Suppressed = false
FEATURE [PartDesign::SubtractiveSphere] Sphere003
  Angle1 = -90
  Angle2 = 90
  Angle3 = 360
  AttacherType = Attacher::AttachEngine3D
  AttachmentSupport = -> [Sphere002]
  BaseFeature = -> Sphere002
  MapMode = 45
  Placement = pos=(49.85,56.15,-2.5) rot=(0.57735,0.57735,0.57735;2.0944rad)
  Radius = 1
  Refine = true
  Suppressed = false
FEATURE [PartDesign::SubShapeBinder] Binder023
  BindCopyOnChange = 0
  BindMode = 0
  ClaimChildren = false
  Context = -> Body [Binder023.]
  Fuse = false
  MakeFace = true
  OffsetFill = false
  OffsetIntersection = false
  OffsetJoinType = 0
  OffsetOpenResult = false
  PartialLoad = false
  Refine = true
  Relative = true
  Support = -> [KeyswitchCarrierMk1_002]
  _Version = 2
FEATURE [Sketcher::SketchObject] Sketch057
  ArcFitTolerance = 1e-06
  AttachmentSupport = -> [Sphere003]
  ExternalGeometry = -> [Binder023]
  FullyConstrained = true
  MakeInternals = false
  MapMode = 5
  Placement = pos=(49.85,56.15,-2.84e-14) rot=(0.707107,0.707107,0;3.14159rad)
  sketch-geometry (6):
    g0: Circle CenterX=-31.3 CenterY=-30.9 CenterZ=0 NormalX=0 NormalY=0 NormalZ=1 AngleXU=0 Radius=2.2
    g1: Circle CenterX=-31.3 CenterY=-30.9 CenterZ=0 NormalX=0 NormalY=0 NormalZ=1 AngleXU=0 Radius=3.2
    g2: Circle CenterX=-4.05 CenterY=-17.15 CenterZ=0 NormalX=0 NormalY=0 NormalZ=1 AngleXU=0 Radius=2.2
    g3: Circle CenterX=-4.05 CenterY=-17.15 CenterZ=0 NormalX=0 NormalY=0 NormalZ=1 AngleXU=0 Radius=3.2
    g4: Circle CenterX=32.2 CenterY=-16.65 CenterZ=0 NormalX=0 NormalY=0 NormalZ=1 AngleXU=0 Radius=2.2
    g5: Circle CenterX=32.2 CenterY=-16.65 CenterZ=0 NormalX=0 NormalY=0 NormalZ=1 AngleXU=0 Radius=3.2
  constraints (12):
    c: Diameter(g0) = 4.4
    c: Coincident(g0,g-3)
    c: Diameter(g1) = 6.4
    c: Coincident(g1,g0)
    c: Diameter(g2) = 4.4
    c: Diameter(g3) = 6.4
    c: Diameter(g4) = 4.4
    c: Diameter(g5) = 6.4
    c: Coincident(g2,g3)
    c: Coincident(g2,g-4)
    c: Coincident(g4,g5)
    c: Coincident(g4,g-5)
FEATURE [PartDesign::Pad] Pad037
  BaseFeature = -> Sphere003
  Direction = (0,0,-1)
  Length = 11.9
  Length2 = 10
  Placement = pos=(49.85,56.15,-2.5) rot=(0.57735,0.57735,0.57735;2.0944rad)
  Profile = -> Sketch057
  ReferenceAxis = -> Sketch057 [N_Axis]
  Refine = true
  Suppressed = false
  Type = 0
FEATURE [PartDesign::SubShapeBinder] Binder024
  BindCopyOnChange = 0
  BindMode = 0
  ClaimChildren = false
  Context = -> Body020 [Binder024.]
  Fuse = false
  MakeFace = true
  OffsetFill = false
  OffsetIntersection = false
  OffsetJoinType = 0
  OffsetOpenResult = false
  PartialLoad = false
  Refine = true
  Relative = true
  Support = -> [Body]
  _Version = 2
FEATURE [PartDesign::Plane] DatumPlane003
  AttachmentOffset = pos=(0,0,0.6) rot=(0,0,1;0rad)
  AttachmentSupport = -> [Binder024]
  Length = 133.541
  MapMode = 5
  Placement = pos=(0,0,-0.6) rot=(1,0,0;3.14159rad)
  ResizeMode = 0
  Width = 125.691
FEATURE [Sketcher::SketchObject] Sketch058
  ArcFitTolerance = 1e-06
  AttachmentSupport = -> [DatumPlane003]
  ExternalGeometry = -> [Binder024]
  FullyConstrained = true
  MakeInternals = false
  MapMode = 5
  Placement = pos=(0,0,-0.6) rot=(1,0,0;3.14159rad)
  sketch-geometry (20):
    g0: LineSegment [constr] StartX=47.85 StartY=-63.65 StartZ=0 EndX=79.95 EndY=-95.75 EndZ=0
    g1: LineSegment [constr] StartX=47.85 StartY=-95.75 StartZ=0 EndX=63.9 EndY=-79.7 EndZ=0
    g2: LineSegment StartX=45.85 StartY=-61.65 StartZ=0 EndX=45.85 EndY=-79.1 EndZ=0
    g3: LineSegment StartX=45.85 StartY=-79.1 StartZ=0 EndX=81.95 EndY=-79.1 EndZ=0
    g4: LineSegment StartX=81.95 StartY=-79.1 StartZ=0 EndX=81.95 EndY=-61.65 EndZ=0
    g5: LineSegment StartX=81.95 StartY=-61.65 StartZ=0 EndX=77.55 EndY=-61.65 EndZ=0
    g6: LineSegment StartX=77.55 StartY=-61.65 StartZ=0 EndX=77.55 EndY=-58.65 EndZ=0
    g7: LineSegment StartX=77.55 StartY=-58.65 StartZ=0 EndX=77.75 EndY=-58.65 EndZ=0
    g8: LineSegment StartX=77.75 StartY=-58.65 StartZ=0 EndX=77.75 EndY=-56.15 EndZ=0
    g9: LineSegment StartX=77.75 StartY=-56.15 StartZ=0 EndX=75.55 EndY=-56.15 EndZ=0
    g10: LineSegment StartX=75.55 StartY=-56.15 StartZ=0 EndX=75.55 EndY=-61.65 EndZ=0
    g11: LineSegment StartX=75.55 StartY=-61.65 StartZ=0 EndX=52.25 EndY=-61.65 EndZ=0
    g12: LineSegment StartX=52.25 StartY=-61.65 StartZ=0 EndX=52.25 EndY=-56.15 EndZ=0
    g13: LineSegment StartX=52.25 StartY=-56.15 StartZ=0 EndX=50.05 EndY=-56.15 EndZ=0
    g14: LineSegment StartX=50.05 StartY=-56.15 StartZ=0 EndX=50.05 EndY=-58.65 EndZ=0
    g15: LineSegment StartX=50.05 StartY=-58.65 StartZ=0 EndX=50.25 EndY=-58.65 EndZ=0
    g16: LineSegment StartX=50.25 StartY=-58.65 StartZ=0 EndX=50.25 EndY=-61.65 EndZ=0
    g17: LineSegment StartX=50.25 StartY=-61.65 StartZ=0 EndX=45.85 EndY=-61.65 EndZ=0
    g18: GeomPoint X=77.95 Y=-56.15 Z=0
    g19: GeomPoint X=49.85 Y=-56.15 Z=0
  constraints (54):
    c: Coincident(g0,g-3)
    c: Coincident(g0,g-4)
    c: Coincident(g1,g-4)
    c: Symmetric(g0,g0,g1)
    c: Vertical(g2)
    c: Coincident(g2,g3)
    c: Horizontal(g3)
    c: Coincident(g3,g4)
    c: Vertical(g4)
    c: Coincident(g4,g5)
    c: Horizontal(g5)
    c: Coincident(g5,g6)
    c: Vertical(g6)
    c: Coincident(g6,g7)
    c: Horizontal(g7)
    c: Coincident(g7,g8)
    c: Vertical(g8)
    c: Coincident(g8,g9)
    c: Horizontal(g9)
    c: Coincident(g9,g10)
    c: Vertical(g10)
    c: Coincident(g10,g11)
    c: Horizontal(g11)
    c: Coincident(g11,g12)
    c: Vertical(g12)
    c: Coincident(g12,g13)
    c: Horizontal(g13)
    c: Coincident(g13,g14)
    c: Vertical(g14)
    c: Coincident(g14,g15)
    c: Horizontal(g15)
    c: Coincident(g15,g16)
    c: Vertical(g16)
    c: Coincident(g16,g17)
    c: Horizontal(g17)
    c: Coincident(g17,g2)
    c: DistanceX(g2,g0) = 2
    c: DistanceY(g0,g2) = 2
    c: DistanceX(g-3,g4) = 2
    c: DistanceY(g-3,g4) = 2
    c: DistanceY(g1,g3) = 0.6
    c: PointOnObject(g11,g17)
    c: Symmetric(g-8,g-8,g18)
    c: PointOnObject(g18,g9)
    c: PointOnObject(g-8,g7)
    c: Distance(g-8,g7) = 0.2
    c: DistanceX(g7,g7) = 0.2
    c: DistanceX(g10,g5) = 2
    c: Symmetric(g-5,g-5,g19)
    c: PointOnObject(g19,g13)
    c: PointOnObject(g-5,g15)
    c: Distance(g14,g-5) = 0.2
    c: DistanceX(g15,g15) = 0.2
    c: DistanceX(g16,g11) = 2
FEATURE [PartDesign::Pad] Pad038
  Direction = (0,0,-1)
  Length = 1
  Length2 = 10
  Placement = pos=(0,0,-0.6) rot=(1,0,0;3.14159rad)
  Profile = -> Sketch058
  ReferenceAxis = -> Sketch058 [N_Axis]
  Refine = true
  Suppressed = false
  Type = 0
FEATURE [Sketcher::SketchObject] Sketch059
  ArcFitTolerance = 1e-06
  AttachmentSupport = -> [Pad038]
  ExternalGeometry = -> [Binder024,Pad038]
  FullyConstrained = true
  MakeInternals = false
  MapMode = 5
  Placement = pos=(50.05,0,-0.6) rot=(0.57735,0.57735,-0.57735;4.18879rad)
  sketch-geometry (3):
    g0: ArcOfCircle CenterX=56.15 CenterY=1.9 CenterZ=0 NormalX=0 NormalY=0 NormalZ=1 AngleXU=0 Radius=1.9 StartAngle=5.78972 EndAngle=10.9956
    g1: LineSegment StartX=57.8233 StartY=1 StartZ=0 EndX=56.15 EndY=1 EndZ=0
    g2: LineSegment StartX=56.15 StartY=1 StartZ=0 EndX=56.15 EndY=-2.55e-14 EndZ=0
  constraints (7):
    c: Coincident(g0,g-3)
    c: Coincident(g0,g-4)
    c: PointOnObject(g0,g-5)
    c: Coincident(g1,g0)
    c: Coincident(g1,g-5)
    c: Coincident(g2,g1)
    c: Coincident(g2,g0)
FEATURE [PartDesign::Pad] Pad039
  BaseFeature = -> Pad038
  Direction = (-1,0,0)
  Length = 2.2
  Length2 = 10
  Placement = pos=(0,0,-0.6) rot=(1,0,0;3.14159rad)
  Profile = -> Sketch059
  ReferenceAxis = -> Sketch059 [N_Axis]
  Refine = true
  Reversed = true
  Suppressed = false
  Type = 0
FEATURE [Sketcher::SketchObject] Sketch060
  ArcFitTolerance = 1e-06
  AttachmentSupport = -> [Pad039]
  ExternalGeometry = -> [Pad039]
  FullyConstrained = true
  MakeInternals = false
  MapMode = 5
  Placement = pos=(50.05,0,-0.6) rot=(0.57735,0.57735,-0.57735;4.18879rad)
  sketch-geometry (4):
    g0: ArcOfCircle CenterX=56.15 CenterY=1.9 CenterZ=0 NormalX=0 NormalY=0 NormalZ=1 AngleXU=0 Radius=1.9 StartAngle=4.71239 EndAngle=5.78972
    g1: LineSegment StartX=57.8233 StartY=1 StartZ=0 EndX=58.65 EndY=1 EndZ=0
    g2: LineSegment StartX=58.65 StartY=1 StartZ=0 EndX=58.65 EndY=-1.481e-13 EndZ=0
    g3: LineSegment StartX=58.65 StartY=-1.481e-13 StartZ=0 EndX=56.15 EndY=-1.481e-13 EndZ=0
  constraints (9):
    c: Coincident(g0,g-3)
    c: Coincident(g0,g-3)
    c: Coincident(g1,g0)
    c: Coincident(g1,g-4)
    c: Coincident(g2,g1)
    c: Coincident(g2,g-4)
    c: Coincident(g3,g2)
    c: Coincident(g3,g0)
    c: Horizontal(g3)
FEATURE [PartDesign::Pocket] Pocket022
  BaseFeature = -> Pad039
  Direction = (1,0,0)
  Length = 0.2
  Length2 = 5
  Placement = pos=(0,0,-0.6) rot=(1,0,0;3.14159rad)
  Profile = -> Sketch060
  ReferenceAxis = -> Sketch060 [N_Axis]
  Refine = true
  Suppressed = false
  Type = 0
FEATURE [Sketcher::SketchObject] Sketch061
  ArcFitTolerance = 1e-06
  AttachmentSupport = -> [Pocket022]
  ExternalGeometry = -> [Binder024,Pocket022]
  FullyConstrained = true
  MakeInternals = false
  MapMode = 5
  Placement = pos=(77.75,0,-0.6) rot=(0.57735,-0.57735,0.57735;4.18879rad)
  sketch-geometry (3):
    g0: ArcOfCircle CenterX=-56.15 CenterY=1.9 CenterZ=0 NormalX=0 NormalY=0 NormalZ=1 AngleXU=0 Radius=1.9 StartAngle=4.71239 EndAngle=9.91825
    g1: LineSegment StartX=-57.8233 StartY=1 StartZ=0 EndX=-56.15 EndY=1 EndZ=0
    g2: LineSegment StartX=-56.15 StartY=1 StartZ=0 EndX=-56.15 EndY=-6.44e-14 EndZ=0
  constraints (7):
    c: Coincident(g0,g-3)
    c: Coincident(g0,g-5)
    c: PointOnObject(g0,g-4)
    c: Coincident(g1,g0)
    c: Coincident(g1,g-5)
    c: Coincident(g2,g1)
    c: Coincident(g2,g0)
FEATURE [PartDesign::Pad] Pad040
  BaseFeature = -> Pocket022
  Direction = (1,0,0)
  Length = 2.2
  Length2 = 10
  Placement = pos=(0,0,-0.6) rot=(1,0,0;3.14159rad)
  Profile = -> Sketch061
  ReferenceAxis = -> Sketch061 [N_Axis]
  Refine = true
  Reversed = true
  Suppressed = false
  Type = 0
FEATURE [Sketcher::SketchObject] Sketch062
  ArcFitTolerance = 1e-06
  AttachmentSupport = -> [Pad040]
  ExternalGeometry = -> [Pad040]
  FullyConstrained = true
  MakeInternals = false
  MapMode = 5
  Placement = pos=(77.75,0,-0.6) rot=(0.57735,-0.57735,0.57735;4.18879rad)
  sketch-geometry (4):
    g0: ArcOfCircle CenterX=-56.15 CenterY=1.9 CenterZ=0 NormalX=0 NormalY=0 NormalZ=1 AngleXU=0 Radius=1.9 StartAngle=3.63506 EndAngle=4.71239
    g1: LineSegment StartX=-57.8233 StartY=1 StartZ=0 EndX=-58.65 EndY=1 EndZ=0
    g2: LineSegment StartX=-58.65 StartY=1 StartZ=0 EndX=-58.65 EndY=8.56e-14 EndZ=0
    g3: LineSegment StartX=-58.65 StartY=8.56e-14 StartZ=0 EndX=-56.15 EndY=7.77e-14 EndZ=0
  constraints (8):
    c: Coincident(g0,g-3)
    c: Coincident(g0,g-3)
    c: Coincident(g1,g0)
    c: Coincident(g1,g-4)
    c: Coincident(g2,g1)
    c: Coincident(g2,g-4)
    c: Coincident(g3,g2)
    c: Tangent(g3,g0) = -1.5708
FEATURE [PartDesign::Pocket] Pocket023
  BaseFeature = -> Pad040
  Direction = (-1,0,0)
  Length = 0.2
  Length2 = 5
  Placement = pos=(0,0,-0.6) rot=(1,0,0;3.14159rad)
  Profile = -> Sketch062
  ReferenceAxis = -> Sketch062 [N_Axis]
  Refine = true
  Suppressed = false
  Type = 0
FEATURE [PartDesign::AdditiveSphere] Sphere004
  Angle1 = -90
  Angle2 = 90
  Angle3 = 360
  AttacherType = Attacher::AttachEngine3D
  AttachmentSupport = -> [Pocket023]
  BaseFeature = -> Pocket023
  MapMode = 45
  Placement = pos=(50.05,56.15,-2.5) rot=(0.57735,0.57735,0.57735;2.0944rad)
  Radius = 1
  Refine = true
  Suppressed = false
FEATURE [PartDesign::AdditiveSphere] Sphere005
  Angle1 = -90
  Angle2 = 90
  Angle3 = 360
  AttacherType = Attacher::AttachEngine3D
  AttachmentSupport = -> [Sphere004]
  BaseFeature = -> Sphere004
  MapMode = 5
  Placement = pos=(77.75,56.15,-2.5) rot=(0.57735,0.57735,0.57735;2.0944rad)
  Radius = 1
  Refine = true
  Suppressed = false
FEATURE [Sketcher::SketchObject] Sketch063
  ArcFitTolerance = 1e-06
  AttachmentSupport = -> [Sphere005]
  ExternalGeometry = -> [Sphere005]
  FullyConstrained = true
  MakeInternals = false
  MapMode = 5
  Placement = pos=(77.75,56.15,-1.6) rot=(0.707107,0.707107,0;3.14159rad)
  sketch-geometry (4):
    g0: LineSegment StartX=22.95 StartY=4.2 StartZ=0 EndX=18.95 EndY=4.2 EndZ=0
    g1: LineSegment StartX=18.95 StartY=4.2 StartZ=0 EndX=18.95 EndY=0.2 EndZ=0
    g2: LineSegment StartX=18.95 StartY=0.2 StartZ=0 EndX=22.95 EndY=0.2 EndZ=0
    g3: LineSegment StartX=22.95 StartY=0.2 StartZ=0 EndX=22.95 EndY=4.2 EndZ=0
  constraints (11):
    c: Coincident(g0,g1)
    c: Coincident(g1,g2)
    c: Coincident(g2,g3)
    c: Coincident(g3,g0)
    c: Horizontal(g0)
    c: Horizontal(g2)
    c: Vertical(g1)
    c: Vertical(g3)
    c: Distance(g1,g3) = 4
    c: Coincident(g0,g-3)
    c: DistanceY(g1,g1) = 4
FEATURE [PartDesign::Pad] Pad041
  BaseFeature = -> Sphere005
  Direction = (0,1.1e-15,-1)
  Length = 5
  Length2 = 10
  Placement = pos=(77.75,56.15,-2.5) rot=(0.57735,0.57735,0.57735;2.0944rad)
  Profile = -> Sketch063
  ReferenceAxis = -> Sketch063 [N_Axis]
  Refine = true
  Suppressed = false
  Type = 0
FEATURE [Sketcher::SketchObject] Sketch064
  ArcFitTolerance = 1e-06
  AttachmentSupport = -> [Pad041]
  ExternalGeometry = -> [Pad041]
  FullyConstrained = true
  MakeInternals = false
  MapMode = 5
  Placement = pos=(81.95,56.15,-2.5) rot=(0.57735,0.57735,0.57735;2.0944rad)
  sketch-geometry (3):
    g0: LineSegment [constr] StartX=18.95 StartY=0.900004 StartZ=0 EndX=22.95 EndY=-4.1 EndZ=0
    g1: LineSegment [constr] StartX=18.95 StartY=-4.1 StartZ=0 EndX=20.95 EndY=-1.6 EndZ=0
    g2: Circle CenterX=20.95 CenterY=-1.6 CenterZ=0 NormalX=0 NormalY=0 NormalZ=1 AngleXU=0 Radius=1.65
  constraints (6):
    c: Coincident(g0,g-3)
    c: Coincident(g0,g-4)
    c: Coincident(g1,g-4)
    c: Symmetric(g0,g0,g1)
    c: Diameter(g2) = 3.3
    c: Coincident(g2,g1)
FEATURE [PartDesign::Pad] Pad042
  BaseFeature = -> Pad041
  Direction = (1,1.4e-15,-2e-16)
  Length = 5
  Length2 = 10
  Placement = pos=(77.75,56.15,-2.5) rot=(0.57735,0.57735,0.57735;2.0944rad)
  Profile = -> Sketch064
  ReferenceAxis = -> Sketch064 [N_Axis]
  Refine = true
  Suppressed = false
  Type = 0
FEATURE [PartDesign::Plane] DatumPlane004
  AttachmentOffset = pos=(0,0,0) rot=(1,0,0;1.5708rad)
  AttachmentSupport = -> [Pad042]
  Length = 125.691
  MapMode = 45
  Placement = pos=(84.45,77.1,-4.1) rot=(0.707107,0.707107,0;3.14159rad)
  ResizeMode = 0
  Width = 133.541
FEATURE [Sketcher::SketchObject] Sketch065
  ArcFitTolerance = 1e-06
  AttachmentSupport = -> [DatumPlane004]
  FullyConstrained = false
  MakeInternals = false
  MapMode = 5
  Placement = pos=(84.45,77.1,-4.1) rot=(0.707107,0.707107,0;3.14159rad)
  sketch-geometry (1):
    g0: Circle CenterX=1.68054 CenterY=0.5 CenterZ=0 NormalX=0 NormalY=0 NormalZ=1 AngleXU=0 Radius=0.5
  constraints (2):
    c: Diameter(g0) = 1
    c: Tangent(g-1,g0)
FEATURE [PartDesign::Groove] Groove002
  Angle = 360
  Angle2 = 60
  Axis = (1,-2e-16,0)
  Base = (84.45,77.1,-4.1)
  BaseFeature = -> Pad042
  Placement = pos=(77.75,56.15,-2.5) rot=(0.57735,0.57735,0.57735;2.0944rad)
  Profile = -> Sketch065
  ReferenceAxis = -> Sketch065 [V_Axis]
  Refine = true
  Suppressed = false
  Type = 0
FEATURE [Sketcher::SketchObject] Sketch066
  ArcFitTolerance = 1e-06
  AttachmentSupport = -> [Pad037]
  FullyConstrained = false
  MakeInternals = false
  MapMode = 5
  Placement = pos=(49.85,56.15,-2.8e-14) rot=(0.707107,0.707107,0;3.14159rad)
  sketch-geometry (12):
    g0: LineSegment StartX=-30.1845 StartY=4.16634 StartZ=0 EndX=-30.1845 EndY=-4.83366 EndZ=0
    g1: LineSegment StartX=-30.1845 StartY=-4.83366 StartZ=0 EndX=-27.1845 EndY=-4.83366 EndZ=0
    g2: LineSegment StartX=-27.1845 StartY=-4.83366 StartZ=0 EndX=-27.1845 EndY=4.16634 EndZ=0
    g3: LineSegment StartX=-27.1845 StartY=4.16634 StartZ=0 EndX=-30.1845 EndY=4.16634 EndZ=0
    g4: LineSegment StartX=-30.1845 StartY=45.3612 StartZ=0 EndX=-30.1845 EndY=36.3612 EndZ=0
    g5: LineSegment StartX=-30.1845 StartY=36.3612 StartZ=0 EndX=-27.1845 EndY=36.3612 EndZ=0
    g6: LineSegment StartX=-27.1845 StartY=36.3612 StartZ=0 EndX=-27.1845 EndY=45.3612 EndZ=0
    g7: LineSegment StartX=-27.1845 StartY=45.3612 StartZ=0 EndX=-30.1845 EndY=45.3612 EndZ=0
    g8: LineSegment StartX=-0.240095 StartY=48.8712 StartZ=0 EndX=-0.240095 EndY=45.8712 EndZ=0
    g9: LineSegment StartX=-0.240095 StartY=45.8712 StartZ=0 EndX=8.75991 EndY=45.8712 EndZ=0
    g10: LineSegment StartX=8.75991 StartY=45.8712 StartZ=0 EndX=8.75991 EndY=48.8712 EndZ=0
    g11: LineSegment StartX=8.75991 StartY=48.8712 StartZ=0 EndX=-0.240095 EndY=48.8712 EndZ=0
  constraints (31):
    c: Coincident(g0,g1)
    c: Coincident(g1,g2)
    c: Coincident(g2,g3)
    c: Coincident(g3,g0)
    c: Vertical(g0)
    c: Vertical(g2)
    c: Horizontal(g1)
    c: Horizontal(g3)
    c: Distance(g0,g2) = 3
    c: Distance(g1,g3) = 9
    c: Coincident(g4,g5)
    c: Coincident(g5,g6)
    c: Coincident(g6,g7)
    c: Coincident(g7,g4)
    c: Vertical(g4)
    c: Vertical(g6)
    c: Horizontal(g5)
    c: Horizontal(g7)
    c: Distance(g4,g6) = 3
    c: Distance(g5,g7) = 9
    c: PointOnObject(g4,g0)
    c: Coincident(g8,g9)
    c: Coincident(g9,g10)
    c: Coincident(g10,g11)
    c: Coincident(g11,g8)
    c: Vertical(g8)
    c: Vertical(g10)
    c: Horizontal(g9)
    c: Horizontal(g11)
    c: Distance(g8,g10) = 9
    c: Distance(g9,g11) = 3
FEATURE [PartDesign::Pad] Pad043
  BaseFeature = -> Pad037
  Direction = (0,0,-1)
  Length = 9
  Length2 = 10
  Placement = pos=(49.85,56.15,-2.5) rot=(0.57735,0.57735,0.57735;2.0944rad)
  Profile = -> Sketch066
  ReferenceAxis = -> Sketch066 [N_Axis]
  Refine = true
  Suppressed = false
  Type = 0
FEATURE [PartDesign::SubtractiveCylinder] Cylinder
  Angle = 360
  AttacherType = Attacher::AttachEngine3D
  AttachmentOffset = pos=(0,0,-5) rot=(0,0,1;0rad)
  AttachmentSupport = -> [Pad043]
  BaseFeature = -> Pad043
  FirstAngle = 0
  Height = 10
  MapMode = 45
  Placement = pos=(92.2212,60.4099,-4.5) rot=(0.57735,0.57735,0.57735;2.0944rad)
  Radius = 2.5
  Refine = true
  SecondAngle = 0
  Suppressed = false
FEATURE [PartDesign::SubtractiveCylinder] Cylinder001
  Angle = 360
  AttacherType = Attacher::AttachEngine3D
  AttachmentOffset = pos=(0,0,-5) rot=(0,0,1;0rad)
  AttachmentSupport = -> [Cylinder]
  BaseFeature = -> Cylinder
  FirstAngle = 0
  Height = 10
  MapMode = 45
  Placement = pos=(90.7112,22.4655,-4.5) rot=(0,0.707107,0.707107;3.14159rad)
  Radius = 2.5
  Refine = true
  SecondAngle = 0
  Suppressed = false
FEATURE [PartDesign::SubtractiveCylinder] Cylinder002
  Angle = 360
  AttacherType = Attacher::AttachEngine3D
  AttachmentOffset = pos=(0,0,-4) rot=(0,0,1;0rad)
  AttachmentSupport = -> [Cylinder001]
  BaseFeature = -> Cylinder001
  FirstAngle = 0
  Height = 10
  MapMode = 45
  Placement = pos=(49.5163,23.4655,-4.5) rot=(0,0.707107,0.707107;3.14159rad)
  Radius = 2.5
  Refine = true
  SecondAngle = 0
  Suppressed = false
FEATURE [PartDesign::SubShapeBinder] Binder025
  BindCopyOnChange = 0
  BindMode = 0
  ClaimChildren = false
  Context = -> Body022 [Binder025.]
  Fuse = false
  MakeFace = true
  OffsetFill = false
  OffsetIntersection = false
  OffsetJoinType = 0
  OffsetOpenResult = false
  PartialLoad = false
  Refine = true
  Relative = true
  Support = -> [cherry_mx_v28,Clone,Clone001]
  _Version = 2
FEATURE [PartDesign::Plane] DatumPlane005
  AttachmentOffset = pos=(0,0,4) rot=(0,0,1;0rad)
  AttachmentSupport = -> [Binder025]
  Length = 85.2052
  MapMode = 5
  Placement = pos=(0,0,3.58821) rot=(0,0,1;0rad)
  ResizeMode = 0
  Width = 157.407
FEATURE [Sketcher::SketchObject] Sketch067
  ArcFitTolerance = 1e-06
  AttachmentSupport = -> [DatumPlane005]
  ExternalGeometry = -> [Binder025]
  FullyConstrained = false
  MakeInternals = false
  MapMode = 5
  Placement = pos=(0,0,3.58821) rot=(0,0,1;0rad)
  sketch-geometry (57):
    g0: LineSegment StartX=29.6562 StartY=103.025 StartZ=0 EndX=29.6562 EndY=104.575 EndZ=0
    g1: LineSegment StartX=29.6562 StartY=104.575 StartZ=0 EndX=31.3312 EndY=104.575 EndZ=0
    g2: LineSegment StartX=31.3312 StartY=104.575 StartZ=0 EndX=31.3312 EndY=106.15 EndZ=0
    g3: LineSegment StartX=31.3312 StartY=106.15 StartZ=0 EndX=32.6812 EndY=106.15 EndZ=0
    g4: LineSegment StartX=32.6812 StartY=106.15 StartZ=0 EndX=32.6812 EndY=104.575 EndZ=0
    g5: LineSegment StartX=32.6812 StartY=104.575 StartZ=0 EndX=34.3562 EndY=104.575 EndZ=0
    g6: LineSegment StartX=34.3562 StartY=104.575 StartZ=0 EndX=34.3562 EndY=103.025 EndZ=0
    g7: LineSegment StartX=34.3562 StartY=103.025 StartZ=0 EndX=32.6812 EndY=103.025 EndZ=0
    g8: LineSegment StartX=32.6812 StartY=103.025 StartZ=0 EndX=32.6812 EndY=101.45 EndZ=0
    g9: LineSegment StartX=32.6812 StartY=101.45 StartZ=0 EndX=31.3312 EndY=101.45 EndZ=0
    g10: LineSegment StartX=31.3312 StartY=101.45 StartZ=0 EndX=31.3312 EndY=103.025 EndZ=0
    g11: LineSegment StartX=31.3312 StartY=103.025 StartZ=0 EndX=29.6562 EndY=103.025 EndZ=0
    g12: LineSegment StartX=29.6562 StartY=71.025 StartZ=0 EndX=29.6562 EndY=72.575 EndZ=0
    g13: LineSegment StartX=29.6562 StartY=72.575 StartZ=0 EndX=31.3312 EndY=72.575 EndZ=0
    g14: LineSegment StartX=31.3312 StartY=72.575 StartZ=0 EndX=31.3312 EndY=74.15 EndZ=0
    g15: LineSegment StartX=31.3312 StartY=74.15 StartZ=0 EndX=32.6812 EndY=74.15 EndZ=0
    g16: LineSegment StartX=32.6812 StartY=74.15 StartZ=0 EndX=32.6812 EndY=72.575 EndZ=0
    g17: LineSegment StartX=32.6812 StartY=72.575 StartZ=0 EndX=34.3562 EndY=72.575 EndZ=0
    g18: LineSegment StartX=34.3562 StartY=72.575 StartZ=0 EndX=34.3562 EndY=71.025 EndZ=0
    g19: LineSegment StartX=34.3562 StartY=71.025 StartZ=0 EndX=32.6812 EndY=71.025 EndZ=0
    g20: LineSegment StartX=32.6812 StartY=71.025 StartZ=0 EndX=32.6812 EndY=69.45 EndZ=0
    g21: LineSegment StartX=32.6812 StartY=69.45 StartZ=0 EndX=31.3312 EndY=69.45 EndZ=0
    g22: LineSegment StartX=31.3312 StartY=69.45 StartZ=0 EndX=31.3312 EndY=71.025 EndZ=0
    g23: LineSegment StartX=31.3312 StartY=71.025 StartZ=0 EndX=29.6562 EndY=71.025 EndZ=0
    g24: LineSegment StartX=29.6562 StartY=31.025 StartZ=0 EndX=29.6562 EndY=32.575 EndZ=0
    g25: LineSegment StartX=29.6562 StartY=32.575 StartZ=0 EndX=31.3312 EndY=32.575 EndZ=0
    g26: LineSegment StartX=31.3312 StartY=32.575 StartZ=0 EndX=31.3312 EndY=34.15 EndZ=0
    g27: LineSegment StartX=31.3312 StartY=34.15 StartZ=0 EndX=32.6812 EndY=34.15 EndZ=0
    g28: LineSegment StartX=32.6812 StartY=34.15 StartZ=0 EndX=32.6812 EndY=32.575 EndZ=0
    g29: LineSegment StartX=32.6812 StartY=32.575 StartZ=0 EndX=34.3562 EndY=32.575 EndZ=0
    g30: LineSegment StartX=34.3562 StartY=32.575 StartZ=0 EndX=34.3562 EndY=31.025 EndZ=0
    g31: LineSegment StartX=34.3562 StartY=31.025 StartZ=0 EndX=32.6812 EndY=31.025 EndZ=0
    g32: LineSegment StartX=32.6812 StartY=31.025 StartZ=0 EndX=32.6812 EndY=29.45 EndZ=0
    g33: LineSegment StartX=32.6812 StartY=29.45 StartZ=0 EndX=31.3312 EndY=29.45 EndZ=0
    g34: LineSegment StartX=31.3312 StartY=29.45 StartZ=0 EndX=31.3312 EndY=31.025 EndZ=0
    g35: LineSegment StartX=31.3312 StartY=31.025 StartZ=0 EndX=29.6562 EndY=31.025 EndZ=0
    g36: LineSegment [constr] StartX=24.0062 StartY=95.8471 StartZ=0 EndX=40.0572 EndY=95.8471 EndZ=0
    g37: LineSegment [constr] StartX=23.9551 StartY=111.753 StartZ=0 EndX=40.0572 EndY=95.8471 EndZ=0
    g38: LineSegment [constr] StartX=40.0062 StartY=111.8 StartZ=0 EndX=32.0062 EndY=103.8 EndZ=0
    g39: LineSegment [constr] StartX=31.3312 StartY=104.575 StartZ=0 EndX=32.6812 EndY=103.025 EndZ=0
    g40: LineSegment [constr] StartX=32.6812 StartY=104.575 StartZ=0 EndX=32.0062 EndY=103.8 EndZ=0
    g41: LineSegment StartX=29.0762 StartY=106.73 StartZ=0 EndX=29.0762 EndY=100.87 EndZ=0
    g42: LineSegment StartX=29.0762 StartY=100.87 StartZ=0 EndX=34.9362 EndY=100.87 EndZ=0
    g43: LineSegment StartX=34.9362 StartY=100.87 StartZ=0 EndX=34.9362 EndY=106.73 EndZ=0
    g44: LineSegment StartX=34.9362 StartY=106.73 StartZ=0 EndX=29.0762 EndY=106.73 EndZ=0
    g45: LineSegment StartX=29.0762 StartY=74.73 StartZ=0 EndX=29.0762 EndY=68.87 EndZ=0
    g46: LineSegment StartX=29.0762 StartY=68.87 StartZ=0 EndX=34.9362 EndY=68.87 EndZ=0
    g47: LineSegment StartX=34.9362 StartY=68.87 StartZ=0 EndX=34.9362 EndY=74.73 EndZ=0
    g48: LineSegment StartX=34.9362 StartY=74.73 StartZ=0 EndX=29.0762 EndY=74.73 EndZ=0
    g49: LineSegment StartX=29.0762 StartY=34.73 StartZ=0 EndX=29.0762 EndY=28.87 EndZ=0
    g50: LineSegment StartX=29.0762 StartY=28.87 StartZ=0 EndX=34.9362 EndY=28.87 EndZ=0
    g51: LineSegment StartX=34.9362 StartY=28.87 StartZ=0 EndX=34.9362 EndY=34.73 EndZ=0
    g52: LineSegment StartX=34.9362 StartY=34.73 StartZ=0 EndX=29.0762 EndY=34.73 EndZ=0
    g53: LineSegment StartX=23.0257 StartY=113.288 StartZ=0 EndX=23.0257 EndY=23.6454 EndZ=0
    g54: LineSegment StartX=23.0257 StartY=23.6454 StartZ=0 EndX=41.0858 EndY=23.6454 EndZ=0
    g55: LineSegment StartX=41.0858 StartY=23.6454 StartZ=0 EndX=41.0858 EndY=113.288 EndZ=0
    g56: LineSegment StartX=41.0858 StartY=113.288 StartZ=0 EndX=23.0257 EndY=113.288 EndZ=0
  constraints (160):
    c: Vertical(g0)
    c: Coincident(g0,g1)
    c: Horizontal(g1)
    c: Coincident(g1,g2)
    c: Vertical(g2)
    c: Coincident(g2,g3)
    c: Horizontal(g3)
    c: Coincident(g3,g4)
    c: Vertical(g4)
    c: Coincident(g4,g5)
    c: Horizontal(g5)
    c: Coincident(g5,g6)
    c: Vertical(g6)
    c: Coincident(g6,g7)
    c: Horizontal(g7)
    c: Coincident(g7,g8)
    c: Vertical(g8)
    c: Coincident(g8,g9)
    c: Horizontal(g9)
    c: Coincident(g9,g10)
    c: Vertical(g10)
    c: Coincident(g10,g11)
    c: Coincident(g11,g0)
    c: Horizontal(g11)
    c: DistanceX(g0,g-3) = 0.1
    c: DistanceY(g0,g-3) = 0.1
    c: DistanceY(g-3,g0) = 0.1
    c: DistanceX(g2,g-4) = 0.1
    c: DistanceY(g-4,g2) = 0.1
    c: DistanceX(g-4,g3) = 0.1
    c: DistanceY(g-5,g5) = 0.1
    c: DistanceX(g-5,g5) = 0.1
    c: DistanceY(g6,g-5) = 0.1
    c: DistanceX(g-6,g8) = 0.1
    c: DistanceY(g8,g-6) = 0.1
    c: DistanceX(g9,g-6) = 0.1
    c: Vertical(g12)
    c: Coincident(g12,g13)
    c: Horizontal(g13)
    c: Coincident(g13,g14)
    c: Vertical(g14)
    c: Coincident(g14,g15)
    c: Horizontal(g15)
    c: Coincident(g15,g16)
    c: Vertical(g16)
    c: Coincident(g16,g17)
    c: Horizontal(g17)
    c: Coincident(g17,g18)
    c: Vertical(g18)
    c: Coincident(g18,g19)
    c: Horizontal(g19)
    c: Coincident(g19,g20)
    c: Vertical(g20)
    c: Coincident(g20,g21)
    c: Horizontal(g21)
    c: Coincident(g21,g22)
    c: Vertical(g22)
    c: Coincident(g22,g23)
    c: Coincident(g23,g12)
    c: Horizontal(g23)
    c: DistanceY(g-8,g12) = 0.1
    c: DistanceX(g12,g-8) = 0.1
    c: DistanceX(g14,g-7) = 0.1
    c: DistanceY(g-7,g14) = 0.1
    c: DistanceX(g-7,g15) = 0.1
    c: DistanceY(g-10,g17) = 0.1
    c: DistanceX(g-10,g17) = 0.1
    c: DistanceY(g18,g-10) = 0.1
    c: DistanceX(g-9,g20) = 0.1
    c: DistanceY(g20,g-9) = 0.1
    c: DistanceX(g21,g-9) = 0.1
    c: DistanceY(g12,g-8) = 0.1
    c: Vertical(g24)
    c: Coincident(g24,g25)
    c: Horizontal(g25)
    c: Coincident(g25,g26)
    c: Vertical(g26)
    c: Coincident(g26,g27)
    c: Horizontal(g27)
    c: Coincident(g27,g28)
    c: Vertical(g28)
    c: Coincident(g28,g29)
    c: Horizontal(g29)
    c: Coincident(g29,g30)
    c: Vertical(g30)
    c: Coincident(g30,g31)
    c: Horizontal(g31)
    c: Coincident(g31,g32)
    c: Vertical(g32)
    c: Coincident(g32,g33)
    c: Horizontal(g33)
    c: Coincident(g33,g34)
    c: Vertical(g34)
    c: Coincident(g34,g35)
    c: Coincident(g35,g24)
    c: Horizontal(g35)
    c: DistanceY(g-12,g24) = 0.1
    c: DistanceX(g24,g-12) = 0.1
    c: DistanceX(g26,g-11) = 0.1
    c: DistanceY(g-11,g26) = 0.1
    c: DistanceX(g-11,g27) = 0.1
    c: DistanceY(g-13,g29) = 0.1
    c: DistanceX(g-13,g29) = 0.1
    c: DistanceY(g30,g-13) = 0.1
    c: DistanceY(g32,g-14) = 0.1
    c: DistanceX(g-14,g32) = 0.1
    c: DistanceX(g33,g-14) = 0.1
    c: DistanceY(g24,g-12) = 0.1
    c: Horizontal(g36)
    c: Coincident(g37,g36)
    c: Symmetric(g37,g37,g38)
    c: Coincident(g39,g1)
    c: Coincident(g39,g7)
    c: Coincident(g40,g4)
    c: Symmetric(g39,g39,g40)
    c: Coincident(g38,g40)
    c: Coincident(g41,g42)
    c: Coincident(g42,g43)
    c: Coincident(g43,g44)
    c: Coincident(g44,g41)
    c: Vertical(g41)
    c: Vertical(g43)
    c: Horizontal(g42)
    c: Horizontal(g44)
    c: DistanceX(g41,g0) = 0.58
    c: DistanceY(g41,g9) = 0.58
    c: DistanceX(g6,g42) = 0.58
    c: DistanceY(g3,g43) = 0.58
    c: Coincident(g45,g46)
    c: Coincident(g46,g47)
    c: Coincident(g47,g48)
    c: Coincident(g48,g45)
    c: Vertical(g45)
    c: Vertical(g47)
    c: Horizontal(g46)
    c: Horizontal(g48)
    c: DistanceY(g45,g21) = 0.58
    c: DistanceX(g18,g46) = 0.58
    c: DistanceY(g15,g47) = 0.58
    c: DistanceX(g45,g12) = 0.58
    c: Coincident(g49,g50)
    c: Coincident(g50,g51)
    c: Coincident(g51,g52)
    c: Coincident(g52,g49)
    c: Vertical(g49)
    c: Vertical(g51)
    c: Horizontal(g50)
    c: Horizontal(g52)
    c: DistanceX(g29,g51) = 0.58
    c: DistanceY(g50,g32) = 0.58
    c: DistanceX(g49,g24) = 0.58
    c: DistanceY(g26,g49) = 0.58
    c: Coincident(g53,g54)
    c: Coincident(g54,g55)
    c: Coincident(g55,g56)
    c: Coincident(g56,g53)
    c: Vertical(g53)
    c: Vertical(g55)
    c: Horizontal(g54)
    c: Horizontal(g56)
FEATURE [PartDesign::Pad] Pad044
  Direction = (0,0,1)
  Length = 2
  Length2 = 10
  Placement = pos=(1e-16,0,3.58821) rot=(0,0,1;0rad)
  Profile = -> Sketch067 [Edge49,Edge52,Edge51,Edge50]
  ReferenceAxis = -> Sketch067 [N_Axis]
  Refine = true
  Suppressed = false
  Type = 0
FEATURE [PartDesign::Pad] Pad045
  BaseFeature = -> Pad044
  Direction = (0,0,1)
  Length = 4
  Length2 = 10
  Placement = pos=(1e-16,0,3.58821) rot=(0,0,1;0rad)
  Profile = -> Sketch067 [Edge46,Edge45,Edge48,Edge47,Edge31,Edge32,Edge33,Edge34,Edge35,Edge36,Edge25,Edge26,Edge27,Edge28,Edge29,Edge30,Edge42,Edge43,Edge44,Edge41,Edge13,Edge24,Edge23,Edge22,Edge21,Edge20,Edge18,Edge19,Edge17,Edge16,Edge15,Edge14,Edge38,Edge39,Edge40,Edge37,Edge1,Edge12,Edge11,Edge10,+8 more]
  ReferenceAxis = -> Sketch067 [N_Axis]
  Refine = true
  Reversed = true
  Suppressed = false
  Type = 0
FEATURE [PartDesign::Body] Body022  label="KeySwitchSolderingHolder"
  AllowCompound = false
  Group = -> [Binder025,Sketch067,DatumPlane005,Pad044,Pad045]
  Origin = -> Origin292
  Tip = -> Pad045
FEATURE [Sketcher::SketchObject] Sketch068
  ArcFitTolerance = 1e-06
  AttachmentSupport = -> [Cylinder002]
  ExternalGeometry = -> [Cylinder002]
  FullyConstrained = true
  MakeInternals = false
  MapMode = 5
  Placement = pos=(49.5163,23.4655,3.855e-13) rot=(0,1,0;3.14159rad)
  sketch-geometry (4):
    g0: LineSegment StartX=-70.2837 StartY=110.834 StartZ=0 EndX=-70.2837 EndY=108.834 EndZ=0
    g1: LineSegment StartX=-70.2837 StartY=108.834 StartZ=0 EndX=41.5163 EndY=108.834 EndZ=0
    g2: LineSegment StartX=41.5163 StartY=108.834 StartZ=0 EndX=41.5163 EndY=110.834 EndZ=0
    g3: LineSegment StartX=41.5163 StartY=110.834 StartZ=0 EndX=-70.2837 EndY=110.834 EndZ=0
  constraints (10):
    c: Coincident(g0,g1)
    c: Coincident(g1,g2)
    c: Coincident(g2,g3)
    c: Coincident(g3,g0)
    c: Vertical(g0)
    c: Vertical(g2)
    c: Horizontal(g1)
    c: Distance(g1,g3) = 2
    c: Coincident(g0,g-3)
    c: Coincident(g2,g-4)
FEATURE [PartDesign::Pad] Pad046
  BaseFeature = -> Cylinder002
  Direction = (0,0,-1)
  Length = 1
  Length2 = 10
  Placement = pos=(49.5163,23.4655,-4.5) rot=(0,0.707107,0.707107;3.14159rad)
  Profile = -> Sketch068
  ReferenceAxis = -> Sketch068 [N_Axis]
  Refine = true
  Suppressed = false
  Type = 0
FEATURE [PartDesign::Body] Body  label="cover"
  AllowCompound = false
  Group = -> [Sketch,Pad,Sketch001,Pocket,Sketch043,Pad026,Sketch051,Pocket021,Sketch052,Pad032,Pad033,Pad034,Sketch053,Pad035,Sketch054,Pad036,DatumPlane001,Sketch055,Groove,DatumPlane002,Sketch056,Groove001,Sphere,Sphere001,Sphere002,Sphere003,Binder023,Sketch057,Pad037,Sketch066,Pad043,Cylinder,Cylinder001,Cylinder002,Sketch068,Pad046]
  Origin = -> Origin
  Tip = -> Pad046
FEATURE [Sketcher::SketchObject] Sketch069
  ArcFitTolerance = 1e-06
  AttachmentSupport = -> [XY_Plane293]
  FullyConstrained = false
  MakeInternals = false
  MapMode = 5
  sketch-geometry (24):
    g0: BSplineCurve PolesCount=3 KnotsCount=2 Degree=2 IsPeriodic=0
    g1: BSplineCurve PolesCount=2 KnotsCount=2 Degree=1 IsPeriodic=0
    g2: BSplineCurve PolesCount=2 KnotsCount=2 Degree=1 IsPeriodic=0
    g3: BSplineCurve PolesCount=3 KnotsCount=2 Degree=2 IsPeriodic=0
    g4: BSplineCurve PolesCount=2 KnotsCount=2 Degree=1 IsPeriodic=0
    g5: BSplineCurve PolesCount=3 KnotsCount=2 Degree=2 IsPeriodic=0
    g6: BSplineCurve PolesCount=2 KnotsCount=2 Degree=1 IsPeriodic=0
    g7: BSplineCurve PolesCount=3 KnotsCount=2 Degree=2 IsPeriodic=0
    g8: BSplineCurve PolesCount=2 KnotsCount=2 Degree=1 IsPeriodic=0
    g9: BSplineCurve PolesCount=2 KnotsCount=2 Degree=1 IsPeriodic=0
    g10: BSplineCurve PolesCount=3 KnotsCount=2 Degree=2 IsPeriodic=0
    g11: BSplineCurve PolesCount=2 KnotsCount=2 Degree=1 IsPeriodic=0
    g12: BSplineCurve PolesCount=3 KnotsCount=2 Degree=2 IsPeriodic=0
    g13: BSplineCurve PolesCount=2 KnotsCount=2 Degree=1 IsPeriodic=0
    g14: BSplineCurve PolesCount=2 KnotsCount=2 Degree=1 IsPeriodic=0
    g15: BSplineCurve PolesCount=2 KnotsCount=2 Degree=1 IsPeriodic=0
    g16: BSplineCurve PolesCount=2 KnotsCount=2 Degree=1 IsPeriodic=0
    g17: BSplineCurve PolesCount=3 KnotsCount=2 Degree=2 IsPeriodic=0
    g18: BSplineCurve PolesCount=2 KnotsCount=2 Degree=1 IsPeriodic=0
    g19: BSplineCurve PolesCount=2 KnotsCount=2 Degree=1 IsPeriodic=0
    g20: BSplineCurve PolesCount=2 KnotsCount=2 Degree=1 IsPeriodic=0
    g21: BSplineCurve PolesCount=2 KnotsCount=2 Degree=1 IsPeriodic=0
    g22: BSplineCurve PolesCount=3 KnotsCount=2 Degree=2 IsPeriodic=0
    g23: BSplineCurve PolesCount=2 KnotsCount=2 Degree=1 IsPeriodic=0
  constraints (24):
    c: Coincident(g0,g1)
    c: Coincident(g1,g2)
    c: Coincident(g2,g3)
    c: Coincident(g3,g4)
    c: Coincident(g4,g5)
    c: Coincident(g5,g6)
    c: Coincident(g6,g7)
    c: Coincident(g7,g8)
    c: Coincident(g8,g9)
    c: Coincident(g9,g10)
    c: Coincident(g10,g11)
    c: Coincident(g11,g12)
    c: Coincident(g12,g13)
    c: Coincident(g13,g0)
    c: Coincident(g14,g15)
    c: Coincident(g15,g16)
    c: Coincident(g16,g17)
    c: Coincident(g17,g18)
    c: Coincident(g18,g19)
    c: Coincident(g19,g20)
    c: Coincident(g20,g21)
    c: Coincident(g21,g22)
    c: Coincident(g22,g23)
    c: Coincident(g23,g14)
FEATURE [PartDesign::Pad] Pad047
  Direction = (0,0,1)
  Length = 1
  Length2 = 10
  Profile = -> Sketch069
  ReferenceAxis = -> Sketch069 [N_Axis]
  Refine = true
  Suppressed = false
  Type = 0
FEATURE [PartDesign::Body] Body023  label="Body"
  AllowCompound = false
  Group = -> [Sketch069,Pad047]
  Origin = -> Origin293
  Tip = -> Pad047
FEATURE [Sketcher::SketchObject] Sketch070
  ArcFitTolerance = 1e-06
  AttachmentSupport = -> [XY_Plane294]
  FullyConstrained = false
  MakeInternals = false
  MapMode = 5
  sketch-geometry (6):
    g0: BSplineCurve PolesCount=3 KnotsCount=2 Degree=2 IsPeriodic=0
    g1: BSplineCurve PolesCount=2 KnotsCount=2 Degree=1 IsPeriodic=0
    g2: BSplineCurve PolesCount=3 KnotsCount=2 Degree=2 IsPeriodic=0
    g3: BSplineCurve PolesCount=3 KnotsCount=2 Degree=2 IsPeriodic=0
    g4: BSplineCurve PolesCount=2 KnotsCount=2 Degree=1 IsPeriodic=0
    g5: BSplineCurve PolesCount=3 KnotsCount=2 Degree=2 IsPeriodic=0
  constraints (6):
    c: Coincident(g0,g1)
    c: Coincident(g1,g2)
    c: Coincident(g2,g3)
    c: Coincident(g3,g4)
    c: Coincident(g4,g5)
    c: Coincident(g5,g0)
FEATURE [Sketcher::SketchObject] Sketch071
  ArcFitTolerance = 1e-06
  AttachmentSupport = -> [XY_Plane295]
  FullyConstrained = false
  MakeInternals = false
  MapMode = 5
  sketch-geometry (6):
    g0: BSplineCurve PolesCount=3 KnotsCount=2 Degree=2 IsPeriodic=0
    g1: BSplineCurve PolesCount=3 KnotsCount=2 Degree=2 IsPeriodic=0
    g2: BSplineCurve PolesCount=2 KnotsCount=2 Degree=1 IsPeriodic=0
    g3: BSplineCurve PolesCount=3 KnotsCount=2 Degree=2 IsPeriodic=0
    g4: BSplineCurve PolesCount=3 KnotsCount=2 Degree=2 IsPeriodic=0
    g5: BSplineCurve PolesCount=2 KnotsCount=2 Degree=1 IsPeriodic=0
  constraints (6):
    c: Coincident(g0,g1)
    c: Coincident(g1,g2)
    c: Coincident(g2,g3)
    c: Coincident(g3,g4)
    c: Coincident(g4,g5)
    c: Coincident(g5,g0)
FEATURE [Sketcher::SketchObject] Sketch072
  ArcFitTolerance = 1e-06
  AttachmentSupport = -> [XY_Plane296]
  FullyConstrained = false
  MakeInternals = false
  MapMode = 5
  sketch-geometry (7):
    g0: BSplineCurve PolesCount=3 KnotsCount=2 Degree=2 IsPeriodic=0
    g1: BSplineCurve PolesCount=2 KnotsCount=2 Degree=1 IsPeriodic=0
    g2: BSplineCurve PolesCount=3 KnotsCount=2 Degree=2 IsPeriodic=0
    g3: BSplineCurve PolesCount=3 KnotsCount=2 Degree=2 IsPeriodic=0
    g4: BSplineCurve PolesCount=2 KnotsCount=2 Degree=1 IsPeriodic=0
    g5: BSplineCurve PolesCount=3 KnotsCount=2 Degree=2 IsPeriodic=0
    g6: BSplineCurve PolesCount=3 KnotsCount=2 Degree=2 IsPeriodic=0
  constraints (7):
    c: Coincident(g0,g1)
    c: Coincident(g1,g2)
    c: Coincident(g2,g3)
    c: Coincident(g3,g4)
    c: Coincident(g4,g5)
    c: Coincident(g5,g6)
    c: Coincident(g6,g0)
FEATURE [PartDesign::Pad] Pad048
  Direction = (0,0,1)
  Length = 1
  Length2 = 10
  Profile = -> Sketch070
  ReferenceAxis = -> Sketch070 [N_Axis]
  Refine = true
  Suppressed = false
  Type = 0
FEATURE [PartDesign::Body] Body024
  AllowCompound = false
  Group = -> [Sketch070,Pad048]
  Origin = -> Origin294
  Tip = -> Pad048
FEATURE [PartDesign::Pad] Pad049
  Direction = (0,0,1)
  Length = 1
  Length2 = 10
  Profile = -> Sketch071
  ReferenceAxis = -> Sketch071 [N_Axis]
  Refine = true
  Suppressed = false
  Type = 0
FEATURE [PartDesign::Body] Body025
  AllowCompound = false
  Group = -> [Sketch071,Pad049]
  Origin = -> Origin295
  Tip = -> Pad049
FEATURE [Part::MultiFuse] Fusion
  Shapes = -> [Body025,Body023]
FEATURE [PartDesign::Pad] Pad050
  Direction = (0,0,1)
  Length = 1
  Length2 = 10
  Profile = -> Sketch072
  ReferenceAxis = -> Sketch072 [N_Axis]
  Refine = true
  Suppressed = false
  Type = 0
FEATURE [PartDesign::Body] Body026
  AllowCompound = false
  Group = -> [Sketch072,Pad050]
  Origin = -> Origin296
  Tip = -> Pad050
FEATURE [Part::MultiFuse] Fusion001
  Shapes = -> [Fusion,Body024]
FEATURE [Part::Scale] Scale
  Base = -> Fusion001
  Uniform = false
  UniformScale = 1
  XScale = 0.01
  YScale = 0.01
  ZScale = 1
FEATURE [Part::Scale] Scale001
  Base = -> Scale
  Uniform = false
  UniformScale = 1
  XScale = 0.9
  YScale = 0.9
  ZScale = 1
FEATURE [Part::Scale] Scale002
  Base = -> Body026
  Uniform = false
  UniformScale = 1
  XScale = 0.01
  YScale = 0.01
  ZScale = 1
FEATURE [Part::Scale] Scale003
  Base = -> Scale002
  Uniform = false
  UniformScale = 1
  XScale = 0.9
  YScale = 0.9
  ZScale = 1
FEATURE [Sketcher::SketchObject] Sketch075
  ArcFitTolerance = 1e-06
  AttachmentSupport = -> [XY_Plane300]
  FullyConstrained = false
  MakeInternals = false
  MapMode = 5
  sketch-geometry (8):
    g0: BSplineCurve PolesCount=4 KnotsCount=2 Degree=3 IsPeriodic=0
    g1: BSplineCurve PolesCount=4 KnotsCount=2 Degree=3 IsPeriodic=0
    g2: BSplineCurve PolesCount=4 KnotsCount=2 Degree=3 IsPeriodic=0
    g3: BSplineCurve PolesCount=4 KnotsCount=2 Degree=3 IsPeriodic=0
    g4: BSplineCurve PolesCount=4 KnotsCount=2 Degree=3 IsPeriodic=0
    g5: BSplineCurve PolesCount=4 KnotsCount=2 Degree=3 IsPeriodic=0
    g6: BSplineCurve PolesCount=4 KnotsCount=2 Degree=3 IsPeriodic=0
    g7: BSplineCurve PolesCount=4 KnotsCount=2 Degree=3 IsPeriodic=0
  constraints (8):
    c: Coincident(g0,g1)
    c: Coincident(g1,g2)
    c: Coincident(g2,g3)
    c: Coincident(g3,g0)
    c: Coincident(g4,g5)
    c: Coincident(g5,g6)
    c: Coincident(g6,g7)
    c: Coincident(g7,g4)
FEATURE [PartDesign::Pad] Pad053
  Direction = (0,0,1)
  Length = 1
  Length2 = 10
  Profile = -> Sketch075
  ReferenceAxis = -> Sketch075 [N_Axis]
  Refine = true
  Suppressed = false
  Type = 0
FEATURE [PartDesign::Body] Body029
  AllowCompound = false
  Group = -> [Sketch075,Pad053]
  Origin = -> Origin300
  Tip = -> Pad053
FEATURE [PartDesign::FeatureBase] BaseFeature
  BaseFeature = -> Scale001
  Suppressed = false
FEATURE [Sketcher::SketchObject] Sketch074
  ArcFitTolerance = 1e-06
  AttachmentSupport = -> [BaseFeature]
  ExternalGeometry = -> [BaseFeature]
  FullyConstrained = true
  MakeInternals = false
  MapMode = 5
  Placement = pos=(0,0,1) rot=(0,0,1;0rad)
  sketch-geometry (4):
    g0: LineSegment StartX=9.68768 StartY=-13.3082 StartZ=0 EndX=9.68768 EndY=-7.31951 EndZ=0
    g1: LineSegment StartX=9.68768 StartY=-7.31951 StartZ=0 EndX=10.2746 EndY=-7.83779 EndZ=0
    g2: LineSegment StartX=10.2746 StartY=-7.83779 StartZ=0 EndX=10.2746 EndY=-11.4999 EndZ=0
    g3: LineSegment StartX=10.2746 StartY=-11.4999 StartZ=0 EndX=9.68768 EndY=-13.3082 EndZ=0
  constraints (8):
    c: Coincident(g0,g-3)
    c: Coincident(g0,g-3)
    c: Coincident(g0,g1)
    c: Coincident(g1,g-4)
    c: Coincident(g1,g2)
    c: Coincident(g2,g-5)
    c: Coincident(g2,g3)
    c: Coincident(g3,g0)
FEATURE [PartDesign::Pad] Pad052
  BaseFeature = -> BaseFeature
  Direction = (0,0,1)
  Length = 1
  Length2 = 10
  Profile = -> Sketch074
  ReferenceAxis = -> Sketch074 [N_Axis]
  Refine = true
  Reversed = true
  Suppressed = false
  Type = 0
FEATURE [PartDesign::Body] Body028
  AllowCompound = false
  BaseFeature = -> Scale001
  Group = -> [BaseFeature,Sketch074,Pad052]
  Origin = -> Origin298
  Tip = -> Pad052
FEATURE [Part::Scale] Scale006
  Base = -> Body029
  Uniform = false
  UniformScale = 1
  XScale = 0.01
  YScale = 0.01
  ZScale = 1
FEATURE [Part::Scale] Scale007
  Base = -> Scale006
  Uniform = false
  UniformScale = 1
  XScale = 0.9
  YScale = 0.9
  ZScale = 1
FEATURE [App::Part] Part002
  Group = -> [Body026,Scale002,Scale003,Body028,Scale006,Body029,Scale007]
  Origin = -> Origin299
  Placement = pos=(18.46,116.87,5.39821) rot=(0,0,1;0rad)
FEATURE [Part::Scale] Scale010
  Base = -> Part002
  Placement = pos=(18.49,91,8.59732) rot=(0,0,1;1.5708rad)
  Uniform = false
  UniformScale = 1
  XScale = 1
  YScale = 1
  ZScale = 0.5
FEATURE [Part::Cut] Cut  label="Shutdown Button"
  Base = -> Body016
  Tool = -> Scale010
FEATURE [Part::Feature] Scale011  label="Shutdown Button print"
  Placement = pos=(18.49,91,8.59732) rot=(0,0,1;1.5708rad)
  shape: bbox 12.56 x 9.063 x 0.5 mm, 60 faces, 3 solids (baked)
FEATURE [Sketcher::SketchObject] Sketch076
  ArcFitTolerance = 1e-06
  FullyConstrained = false
  MakeInternals = false
  sketch-geometry (22):
    g0: BSplineCurve PolesCount=2 KnotsCount=2 Degree=1 IsPeriodic=0
    g1: BSplineCurve PolesCount=4 KnotsCount=2 Degree=3 IsPeriodic=0
    g2: BSplineCurve PolesCount=4 KnotsCount=2 Degree=3 IsPeriodic=0
    g3: BSplineCurve PolesCount=4 KnotsCount=2 Degree=3 IsPeriodic=0
    g4: BSplineCurve PolesCount=2 KnotsCount=2 Degree=1 IsPeriodic=0
    g5: BSplineCurve PolesCount=4 KnotsCount=2 Degree=3 IsPeriodic=0
    g6: BSplineCurve PolesCount=2 KnotsCount=2 Degree=1 IsPeriodic=0
    g7: BSplineCurve PolesCount=4 KnotsCount=2 Degree=3 IsPeriodic=0
    g8: BSplineCurve PolesCount=2 KnotsCount=2 Degree=1 IsPeriodic=0
    g9: BSplineCurve PolesCount=4 KnotsCount=2 Degree=3 IsPeriodic=0
    g10: BSplineCurve PolesCount=4 KnotsCount=2 Degree=3 IsPeriodic=0
    g11: BSplineCurve PolesCount=2 KnotsCount=2 Degree=1 IsPeriodic=0
    g12: BSplineCurve PolesCount=4 KnotsCount=2 Degree=3 IsPeriodic=0
    g13: BSplineCurve PolesCount=4 KnotsCount=2 Degree=3 IsPeriodic=0
    g14: BSplineCurve PolesCount=4 KnotsCount=2 Degree=3 IsPeriodic=0
    g15: BSplineCurve PolesCount=4 KnotsCount=2 Degree=3 IsPeriodic=0
    g16: BSplineCurve PolesCount=4 KnotsCount=2 Degree=3 IsPeriodic=0
    g17: BSplineCurve PolesCount=2 KnotsCount=2 Degree=1 IsPeriodic=0
    g18: BSplineCurve PolesCount=4 KnotsCount=2 Degree=3 IsPeriodic=0
    g19: BSplineCurve PolesCount=4 KnotsCount=2 Degree=3 IsPeriodic=0
    g20: BSplineCurve PolesCount=4 KnotsCount=2 Degree=3 IsPeriodic=0
    g21: BSplineCurve PolesCount=4 KnotsCount=2 Degree=3 IsPeriodic=0
  constraints (22):
    c: Coincident(g0,g1)
    c: Coincident(g1,g2)
    c: Coincident(g2,g3)
    c: Coincident(g3,g4)
    c: Coincident(g4,g5)
    c: Coincident(g5,g6)
    c: Coincident(g6,g7)
    c: Coincident(g7,g8)
    c: Coincident(g8,g9)
    c: Coincident(g9,g10)
    c: Coincident(g10,g11)
    c: Coincident(g11,g12)
    c: Coincident(g12,g13)
    c: Coincident(g13,g14)
    c: Coincident(g14,g15)
    c: Coincident(g15,g16)
    c: Coincident(g16,g17)
    c: Coincident(g17,g18)
    c: Coincident(g18,g19)
    c: Coincident(g19,g20)
    c: Coincident(g20,g21)
    c: Coincident(g21,g0)
FEATURE [Sketcher::SketchObject] Sketch077
  ArcFitTolerance = 1e-06
  FullyConstrained = false
  MakeInternals = false
  sketch-geometry (16):
    g0: BSplineCurve PolesCount=2 KnotsCount=2 Degree=1 IsPeriodic=0
    g1: BSplineCurve PolesCount=4 KnotsCount=2 Degree=3 IsPeriodic=0
    g2: BSplineCurve PolesCount=4 KnotsCount=2 Degree=3 IsPeriodic=0
    g3: BSplineCurve PolesCount=2 KnotsCount=2 Degree=1 IsPeriodic=0
    g4: BSplineCurve PolesCount=2 KnotsCount=2 Degree=1 IsPeriodic=0
    g5: BSplineCurve PolesCount=4 KnotsCount=2 Degree=3 IsPeriodic=0
    g6: BSplineCurve PolesCount=4 KnotsCount=2 Degree=3 IsPeriodic=0
    g7: BSplineCurve PolesCount=2 KnotsCount=2 Degree=1 IsPeriodic=0
    g8: BSplineCurve PolesCount=2 KnotsCount=2 Degree=1 IsPeriodic=0
    g9: BSplineCurve PolesCount=4 KnotsCount=2 Degree=3 IsPeriodic=0
    g10: BSplineCurve PolesCount=4 KnotsCount=2 Degree=3 IsPeriodic=0
    g11: BSplineCurve PolesCount=2 KnotsCount=2 Degree=1 IsPeriodic=0
    g12: BSplineCurve PolesCount=2 KnotsCount=2 Degree=1 IsPeriodic=0
    g13: BSplineCurve PolesCount=4 KnotsCount=2 Degree=3 IsPeriodic=0
    g14: BSplineCurve PolesCount=4 KnotsCount=2 Degree=3 IsPeriodic=0
    g15: BSplineCurve PolesCount=2 KnotsCount=2 Degree=1 IsPeriodic=0
  constraints (16):
    c: Coincident(g0,g1)
    c: Coincident(g1,g2)
    c: Coincident(g2,g3)
    c: Coincident(g3,g4)
    c: Coincident(g4,g5)
    c: Coincident(g5,g6)
    c: Coincident(g6,g7)
    c: Coincident(g7,g8)
    c: Coincident(g8,g9)
    c: Coincident(g9,g10)
    c: Coincident(g10,g11)
    c: Coincident(g11,g12)
    c: Coincident(g12,g13)
    c: Coincident(g13,g14)
    c: Coincident(g14,g15)
    c: Coincident(g15,g0)
FEATURE [Sketcher::SketchObject] Sketch078
  ArcFitTolerance = 1e-06
  FullyConstrained = false
  MakeInternals = false
  Placement = pos=(0,0,0) rot=(0,0,1;3.14159rad)
  sketch-geometry (4):
    g0: BSplineCurve PolesCount=4 KnotsCount=2 Degree=3 IsPeriodic=0
    g1: BSplineCurve PolesCount=4 KnotsCount=2 Degree=3 IsPeriodic=0
    g2: BSplineCurve PolesCount=4 KnotsCount=2 Degree=3 IsPeriodic=0
    g3: BSplineCurve PolesCount=4 KnotsCount=2 Degree=3 IsPeriodic=0
  constraints (4):
    c: Coincident(g0,g1)
    c: Coincident(g1,g2)
    c: Coincident(g2,g3)
    c: Coincident(g3,g0)
FEATURE [Sketcher::SketchObject] Sketch079
  ArcFitTolerance = 1e-06
  FullyConstrained = false
  MakeInternals = false
  Placement = pos=(0,0,0) rot=(0,0,1;3.14159rad)
  sketch-geometry (4):
    g0: BSplineCurve PolesCount=4 KnotsCount=2 Degree=3 IsPeriodic=0
    g1: BSplineCurve PolesCount=4 KnotsCount=2 Degree=3 IsPeriodic=0
    g2: BSplineCurve PolesCount=4 KnotsCount=2 Degree=3 IsPeriodic=0
    g3: BSplineCurve PolesCount=4 KnotsCount=2 Degree=3 IsPeriodic=0
  constraints (4):
    c: Coincident(g0,g1)
    c: Coincident(g1,g2)
    c: Coincident(g2,g3)
    c: Coincident(g3,g0)
FEATURE [Sketcher::SketchObject] Sketch080
  ArcFitTolerance = 1e-06
  FullyConstrained = false
  MakeInternals = false
  Placement = pos=(0,0,0) rot=(0,0,1;3.14159rad)
  sketch-geometry (4):
    g0: BSplineCurve PolesCount=4 KnotsCount=2 Degree=3 IsPeriodic=0
    g1: BSplineCurve PolesCount=4 KnotsCount=2 Degree=3 IsPeriodic=0
    g2: BSplineCurve PolesCount=4 KnotsCount=2 Degree=3 IsPeriodic=0
    g3: BSplineCurve PolesCount=4 KnotsCount=2 Degree=3 IsPeriodic=0
  constraints (4):
    c: Coincident(g0,g1)
    c: Coincident(g1,g2)
    c: Coincident(g2,g3)
    c: Coincident(g3,g0)
FEATURE [Sketcher::SketchObject] Sketch081
  ArcFitTolerance = 1e-06
  FullyConstrained = false
  MakeInternals = false
  Placement = pos=(0,0,0) rot=(0,0,1;3.14159rad)
  sketch-geometry (4):
    g0: BSplineCurve PolesCount=4 KnotsCount=2 Degree=3 IsPeriodic=0
    g1: BSplineCurve PolesCount=4 KnotsCount=2 Degree=3 IsPeriodic=0
    g2: BSplineCurve PolesCount=4 KnotsCount=2 Degree=3 IsPeriodic=0
    g3: BSplineCurve PolesCount=4 KnotsCount=2 Degree=3 IsPeriodic=0
  constraints (4):
    c: Coincident(g0,g1)
    c: Coincident(g1,g2)
    c: Coincident(g2,g3)
    c: Coincident(g3,g0)
FEATURE [Sketcher::SketchObject] Sketch082
  ArcFitTolerance = 1e-06
  FullyConstrained = false
  MakeInternals = false
  sketch-geometry (13):
    g0: BSplineCurve PolesCount=2 KnotsCount=2 Degree=1 IsPeriodic=0
    g1: BSplineCurve PolesCount=4 KnotsCount=2 Degree=3 IsPeriodic=0
    g2: BSplineCurve PolesCount=4 KnotsCount=2 Degree=3 IsPeriodic=0
    g3: BSplineCurve PolesCount=2 KnotsCount=2 Degree=1 IsPeriodic=0
    g4: BSplineCurve PolesCount=2 KnotsCount=2 Degree=1 IsPeriodic=0
    g5: BSplineCurve PolesCount=4 KnotsCount=2 Degree=3 IsPeriodic=0
    g6: BSplineCurve PolesCount=4 KnotsCount=2 Degree=3 IsPeriodic=0
    g7: BSplineCurve PolesCount=2 KnotsCount=2 Degree=1 IsPeriodic=0
    g8: BSplineCurve PolesCount=4 KnotsCount=2 Degree=3 IsPeriodic=0
    g9: BSplineCurve PolesCount=2 KnotsCount=2 Degree=1 IsPeriodic=0
    g10: BSplineCurve PolesCount=4 KnotsCount=2 Degree=3 IsPeriodic=0
    g11: BSplineCurve PolesCount=4 KnotsCount=2 Degree=3 IsPeriodic=0
    g12: BSplineCurve PolesCount=2 KnotsCount=2 Degree=1 IsPeriodic=0
  constraints (13):
    c: Coincident(g0,g1)
    c: Coincident(g1,g2)
    c: Coincident(g2,g3)
    c: Coincident(g3,g4)
    c: Coincident(g4,g5)
    c: Coincident(g5,g6)
    c: Coincident(g6,g7)
    c: Coincident(g7,g8)
    c: Coincident(g8,g9)
    c: Coincident(g9,g10)
    c: Coincident(g10,g11)
    c: Coincident(g11,g12)
    c: Coincident(g12,g0)
FEATURE [Sketcher::SketchObject] Sketch083
  ArcFitTolerance = 1e-06
  FullyConstrained = false
  MakeInternals = false
  sketch-geometry (12):
    g0: BSplineCurve PolesCount=4 KnotsCount=2 Degree=3 IsPeriodic=0
    g1: BSplineCurve PolesCount=2 KnotsCount=2 Degree=1 IsPeriodic=0
    g2: BSplineCurve PolesCount=4 KnotsCount=2 Degree=3 IsPeriodic=0
    g3: BSplineCurve PolesCount=2 KnotsCount=2 Degree=1 IsPeriodic=0
    g4: BSplineCurve PolesCount=4 KnotsCount=2 Degree=3 IsPeriodic=0
    g5: BSplineCurve PolesCount=2 KnotsCount=2 Degree=1 IsPeriodic=0
    g6: BSplineCurve PolesCount=4 KnotsCount=2 Degree=3 IsPeriodic=0
    g7: BSplineCurve PolesCount=2 KnotsCount=2 Degree=1 IsPeriodic=0
    g8: BSplineCurve PolesCount=2 KnotsCount=2 Degree=1 IsPeriodic=0
    g9: BSplineCurve PolesCount=4 KnotsCount=2 Degree=3 IsPeriodic=0
    g10: BSplineCurve PolesCount=4 KnotsCount=2 Degree=3 IsPeriodic=0
    g11: BSplineCurve PolesCount=2 KnotsCount=2 Degree=1 IsPeriodic=0
  constraints (12):
    c: Coincident(g0,g1)
    c: Coincident(g1,g2)
    c: Coincident(g2,g3)
    c: Coincident(g3,g4)
    c: Coincident(g4,g5)
    c: Coincident(g5,g6)
    c: Coincident(g6,g7)
    c: Coincident(g7,g0)
    c: Coincident(g8,g9)
    c: Coincident(g9,g10)
    c: Coincident(g10,g11)
    c: Coincident(g11,g8)
FEATURE [Sketcher::SketchObject] Sketch084
  ArcFitTolerance = 1e-06
  FullyConstrained = false
  MakeInternals = false
  sketch-geometry (12):
    g0: BSplineCurve PolesCount=4 KnotsCount=2 Degree=3 IsPeriodic=0
    g1: BSplineCurve PolesCount=2 KnotsCount=2 Degree=1 IsPeriodic=0
    g2: BSplineCurve PolesCount=4 KnotsCount=2 Degree=3 IsPeriodic=0
    g3: BSplineCurve PolesCount=2 KnotsCount=2 Degree=1 IsPeriodic=0
    g4: BSplineCurve PolesCount=4 KnotsCount=2 Degree=3 IsPeriodic=0
    g5: BSplineCurve PolesCount=2 KnotsCount=2 Degree=1 IsPeriodic=0
    g6: BSplineCurve PolesCount=4 KnotsCount=2 Degree=3 IsPeriodic=0
    g7: BSplineCurve PolesCount=2 KnotsCount=2 Degree=1 IsPeriodic=0
    g8: BSplineCurve PolesCount=2 KnotsCount=2 Degree=1 IsPeriodic=0
    g9: BSplineCurve PolesCount=4 KnotsCount=2 Degree=3 IsPeriodic=0
    g10: BSplineCurve PolesCount=4 KnotsCount=2 Degree=3 IsPeriodic=0
    g11: BSplineCurve PolesCount=2 KnotsCount=2 Degree=1 IsPeriodic=0
  constraints (12):
    c: Coincident(g0,g1)
    c: Coincident(g1,g2)
    c: Coincident(g2,g3)
    c: Coincident(g3,g4)
    c: Coincident(g4,g5)
    c: Coincident(g5,g6)
    c: Coincident(g6,g7)
    c: Coincident(g7,g0)
    c: Coincident(g8,g9)
    c: Coincident(g9,g10)
    c: Coincident(g10,g11)
    c: Coincident(g11,g8)
FEATURE [Sketcher::SketchObject] Sketch085
  ArcFitTolerance = 1e-06
  FullyConstrained = false
  MakeInternals = false
  sketch-geometry (12):
    g0: BSplineCurve PolesCount=4 KnotsCount=2 Degree=3 IsPeriodic=0
    g1: BSplineCurve PolesCount=2 KnotsCount=2 Degree=1 IsPeriodic=0
    g2: BSplineCurve PolesCount=4 KnotsCount=2 Degree=3 IsPeriodic=0
    g3: BSplineCurve PolesCount=2 KnotsCount=2 Degree=1 IsPeriodic=0
    g4: BSplineCurve PolesCount=4 KnotsCount=2 Degree=3 IsPeriodic=0
    g5: BSplineCurve PolesCount=2 KnotsCount=2 Degree=1 IsPeriodic=0
    g6: BSplineCurve PolesCount=4 KnotsCount=2 Degree=3 IsPeriodic=0
    g7: BSplineCurve PolesCount=2 KnotsCount=2 Degree=1 IsPeriodic=0
    g8: BSplineCurve PolesCount=2 KnotsCount=2 Degree=1 IsPeriodic=0
    g9: BSplineCurve PolesCount=4 KnotsCount=2 Degree=3 IsPeriodic=0
    g10: BSplineCurve PolesCount=4 KnotsCount=2 Degree=3 IsPeriodic=0
    g11: BSplineCurve PolesCount=2 KnotsCount=2 Degree=1 IsPeriodic=0
  constraints (12):
    c: Coincident(g0,g1)
    c: Coincident(g1,g2)
    c: Coincident(g2,g3)
    c: Coincident(g3,g4)
    c: Coincident(g4,g5)
    c: Coincident(g5,g6)
    c: Coincident(g6,g7)
    c: Coincident(g7,g0)
    c: Coincident(g8,g9)
    c: Coincident(g9,g10)
    c: Coincident(g10,g11)
    c: Coincident(g11,g8)
FEATURE [Sketcher::SketchObject] Sketch086
  ArcFitTolerance = 1e-06
  FullyConstrained = false
  MakeInternals = false
  sketch-geometry (12):
    g0: BSplineCurve PolesCount=4 KnotsCount=2 Degree=3 IsPeriodic=0
    g1: BSplineCurve PolesCount=2 KnotsCount=2 Degree=1 IsPeriodic=0
    g2: BSplineCurve PolesCount=4 KnotsCount=2 Degree=3 IsPeriodic=0
    g3: BSplineCurve PolesCount=2 KnotsCount=2 Degree=1 IsPeriodic=0
    g4: BSplineCurve PolesCount=4 KnotsCount=2 Degree=3 IsPeriodic=0
    g5: BSplineCurve PolesCount=2 KnotsCount=2 Degree=1 IsPeriodic=0
    g6: BSplineCurve PolesCount=4 KnotsCount=2 Degree=3 IsPeriodic=0
    g7: BSplineCurve PolesCount=2 KnotsCount=2 Degree=1 IsPeriodic=0
    g8: BSplineCurve PolesCount=2 KnotsCount=2 Degree=1 IsPeriodic=0
    g9: BSplineCurve PolesCount=4 KnotsCount=2 Degree=3 IsPeriodic=0
    g10: BSplineCurve PolesCount=4 KnotsCount=2 Degree=3 IsPeriodic=0
    g11: BSplineCurve PolesCount=2 KnotsCount=2 Degree=1 IsPeriodic=0
  constraints (12):
    c: Coincident(g0,g1)
    c: Coincident(g1,g2)
    c: Coincident(g2,g3)
    c: Coincident(g3,g4)
    c: Coincident(g4,g5)
    c: Coincident(g5,g6)
    c: Coincident(g6,g7)
    c: Coincident(g7,g0)
    c: Coincident(g8,g9)
    c: Coincident(g9,g10)
    c: Coincident(g10,g11)
    c: Coincident(g11,g8)
FEATURE [Sketcher::SketchObject] Sketch087
  ArcFitTolerance = 1e-06
  AttachmentSupport = -> [XY_Plane303]
  FullyConstrained = false
  MakeInternals = false
  MapMode = 5
  sketch-geometry (29):
    g0: BSplineCurve PolesCount=2 KnotsCount=2 Degree=1 IsPeriodic=0
    g1: BSplineCurve PolesCount=4 KnotsCount=2 Degree=3 IsPeriodic=0
    g2: BSplineCurve PolesCount=4 KnotsCount=2 Degree=3 IsPeriodic=0
    g3: BSplineCurve PolesCount=4 KnotsCount=2 Degree=3 IsPeriodic=0
    g4: BSplineCurve PolesCount=4 KnotsCount=2 Degree=3 IsPeriodic=0
    g5: BSplineCurve PolesCount=4 KnotsCount=2 Degree=3 IsPeriodic=0
    g6: BSplineCurve PolesCount=2 KnotsCount=2 Degree=1 IsPeriodic=0
    g7: BSplineCurve PolesCount=4 KnotsCount=2 Degree=3 IsPeriodic=0
    g8: BSplineCurve PolesCount=2 KnotsCount=2 Degree=1 IsPeriodic=0
    g9: BSplineCurve PolesCount=4 KnotsCount=2 Degree=3 IsPeriodic=0
    g10: BSplineCurve PolesCount=4 KnotsCount=2 Degree=3 IsPeriodic=0
    g11: BSplineCurve PolesCount=2 KnotsCount=2 Degree=1 IsPeriodic=0
    g12: BSplineCurve PolesCount=4 KnotsCount=2 Degree=3 IsPeriodic=0
    g13: BSplineCurve PolesCount=4 KnotsCount=2 Degree=3 IsPeriodic=0
    g14: BSplineCurve PolesCount=4 KnotsCount=2 Degree=3 IsPeriodic=0
    g15: BSplineCurve PolesCount=2 KnotsCount=2 Degree=1 IsPeriodic=0
    g16: BSplineCurve PolesCount=4 KnotsCount=2 Degree=3 IsPeriodic=0
    g17: BSplineCurve PolesCount=2 KnotsCount=2 Degree=1 IsPeriodic=0
    g18: BSplineCurve PolesCount=4 KnotsCount=2 Degree=3 IsPeriodic=0
    g19: BSplineCurve PolesCount=2 KnotsCount=2 Degree=1 IsPeriodic=0
    g20: BSplineCurve PolesCount=2 KnotsCount=2 Degree=1 IsPeriodic=0
    g21: BSplineCurve PolesCount=4 KnotsCount=2 Degree=3 IsPeriodic=0
    g22: BSplineCurve PolesCount=4 KnotsCount=2 Degree=3 IsPeriodic=0
    g23: BSplineCurve PolesCount=2 KnotsCount=2 Degree=1 IsPeriodic=0
    g24: BSplineCurve PolesCount=4 KnotsCount=2 Degree=3 IsPeriodic=0
    g25: BSplineCurve PolesCount=2 KnotsCount=2 Degree=1 IsPeriodic=0
    g26: BSplineCurve PolesCount=4 KnotsCount=2 Degree=3 IsPeriodic=0
    g27: BSplineCurve PolesCount=4 KnotsCount=2 Degree=3 IsPeriodic=0
    g28: BSplineCurve PolesCount=2 KnotsCount=2 Degree=1 IsPeriodic=0
  constraints (29):
    c: Coincident(g0,g1)
    c: Coincident(g1,g2)
    c: Coincident(g2,g3)
    c: Coincident(g3,g4)
    c: Coincident(g4,g5)
    c: Coincident(g5,g6)
    c: Coincident(g6,g7)
    c: Coincident(g7,g8)
    c: Coincident(g8,g9)
    c: Coincident(g9,g10)
    c: Coincident(g10,g11)
    c: Coincident(g11,g12)
    c: Coincident(g12,g13)
    c: Coincident(g13,g14)
    c: Coincident(g14,g15)
    c: Coincident(g15,g16)
    c: Coincident(g16,g17)
    c: Coincident(g17,g18)
    c: Coincident(g18,g19)
    c: Coincident(g19,g20)
    c: Coincident(g20,g21)
    c: Coincident(g21,g22)
    c: Coincident(g22,g23)
    c: Coincident(g23,g24)
    c: Coincident(g24,g25)
    c: Coincident(g25,g26)
    c: Coincident(g26,g27)
    c: Coincident(g27,g28)
    c: Coincident(g28,g0)
FEATURE [Sketcher::SketchObject] Sketch088
  ArcFitTolerance = 1e-06
  AttachmentSupport = -> [XY_Plane304]
  FullyConstrained = false
  MakeInternals = false
  MapMode = 5
  sketch-geometry (16):
    g0: BSplineCurve PolesCount=2 KnotsCount=2 Degree=1 IsPeriodic=0
    g1: BSplineCurve PolesCount=4 KnotsCount=2 Degree=3 IsPeriodic=0
    g2: BSplineCurve PolesCount=4 KnotsCount=2 Degree=3 IsPeriodic=0
    g3: BSplineCurve PolesCount=2 KnotsCount=2 Degree=1 IsPeriodic=0
    g4: BSplineCurve PolesCount=2 KnotsCount=2 Degree=1 IsPeriodic=0
    g5: BSplineCurve PolesCount=4 KnotsCount=2 Degree=3 IsPeriodic=0
    g6: BSplineCurve PolesCount=4 KnotsCount=2 Degree=3 IsPeriodic=0
    g7: BSplineCurve PolesCount=2 KnotsCount=2 Degree=1 IsPeriodic=0
    g8: BSplineCurve PolesCount=2 KnotsCount=2 Degree=1 IsPeriodic=0
    g9: BSplineCurve PolesCount=4 KnotsCount=2 Degree=3 IsPeriodic=0
    g10: BSplineCurve PolesCount=4 KnotsCount=2 Degree=3 IsPeriodic=0
    g11: BSplineCurve PolesCount=2 KnotsCount=2 Degree=1 IsPeriodic=0
    g12: BSplineCurve PolesCount=2 KnotsCount=2 Degree=1 IsPeriodic=0
    g13: BSplineCurve PolesCount=4 KnotsCount=2 Degree=3 IsPeriodic=0
    g14: BSplineCurve PolesCount=4 KnotsCount=2 Degree=3 IsPeriodic=0
    g15: BSplineCurve PolesCount=2 KnotsCount=2 Degree=1 IsPeriodic=0
  constraints (16):
    c: Coincident(g0,g1)
    c: Coincident(g1,g2)
    c: Coincident(g2,g3)
    c: Coincident(g3,g4)
    c: Coincident(g4,g5)
    c: Coincident(g5,g6)
    c: Coincident(g6,g7)
    c: Coincident(g7,g8)
    c: Coincident(g8,g9)
    c: Coincident(g9,g10)
    c: Coincident(g10,g11)
    c: Coincident(g11,g12)
    c: Coincident(g12,g13)
    c: Coincident(g13,g14)
    c: Coincident(g14,g15)
    c: Coincident(g15,g0)
FEATURE [Sketcher::SketchObject] Sketch089
  ArcFitTolerance = 1e-06
  FullyConstrained = false
  MakeInternals = false
  Placement = pos=(0,0,0) rot=(0,0,1;3.14159rad)
  sketch-geometry (4):
    g0: BSplineCurve PolesCount=4 KnotsCount=2 Degree=3 IsPeriodic=0
    g1: BSplineCurve PolesCount=4 KnotsCount=2 Degree=3 IsPeriodic=0
    g2: BSplineCurve PolesCount=4 KnotsCount=2 Degree=3 IsPeriodic=0
    g3: BSplineCurve PolesCount=4 KnotsCount=2 Degree=3 IsPeriodic=0
  constraints (4):
    c: Coincident(g0,g1)
    c: Coincident(g1,g2)
    c: Coincident(g2,g3)
    c: Coincident(g3,g0)
FEATURE [Sketcher::SketchObject] Sketch090
  ArcFitTolerance = 1e-06
  FullyConstrained = false
  MakeInternals = false
  Placement = pos=(0,0,0) rot=(0,0,1;3.14159rad)
  sketch-geometry (4):
    g0: BSplineCurve PolesCount=4 KnotsCount=2 Degree=3 IsPeriodic=0
    g1: BSplineCurve PolesCount=4 KnotsCount=2 Degree=3 IsPeriodic=0
    g2: BSplineCurve PolesCount=4 KnotsCount=2 Degree=3 IsPeriodic=0
    g3: BSplineCurve PolesCount=4 KnotsCount=2 Degree=3 IsPeriodic=0
  constraints (4):
    c: Coincident(g0,g1)
    c: Coincident(g1,g2)
    c: Coincident(g2,g3)
    c: Coincident(g3,g0)
FEATURE [Sketcher::SketchObject] Sketch091
  ArcFitTolerance = 1e-06
  FullyConstrained = false
  MakeInternals = false
  Placement = pos=(0,0,0) rot=(0,0,1;3.14159rad)
  sketch-geometry (4):
    g0: BSplineCurve PolesCount=4 KnotsCount=2 Degree=3 IsPeriodic=0
    g1: BSplineCurve PolesCount=4 KnotsCount=2 Degree=3 IsPeriodic=0
    g2: BSplineCurve PolesCount=4 KnotsCount=2 Degree=3 IsPeriodic=0
    g3: BSplineCurve PolesCount=4 KnotsCount=2 Degree=3 IsPeriodic=0
  constraints (4):
    c: Coincident(g0,g1)
    c: Coincident(g1,g2)
    c: Coincident(g2,g3)
    c: Coincident(g3,g0)
FEATURE [Sketcher::SketchObject] Sketch092
  ArcFitTolerance = 1e-06
  FullyConstrained = false
  MakeInternals = false
  Placement = pos=(0,0,0) rot=(0,0,1;3.14159rad)
  sketch-geometry (4):
    g0: BSplineCurve PolesCount=4 KnotsCount=2 Degree=3 IsPeriodic=0
    g1: BSplineCurve PolesCount=4 KnotsCount=2 Degree=3 IsPeriodic=0
    g2: BSplineCurve PolesCount=4 KnotsCount=2 Degree=3 IsPeriodic=0
    g3: BSplineCurve PolesCount=4 KnotsCount=2 Degree=3 IsPeriodic=0
  constraints (4):
    c: Coincident(g0,g1)
    c: Coincident(g1,g2)
    c: Coincident(g2,g3)
    c: Coincident(g3,g0)
FEATURE [PartDesign::Pad] Pad054
  Direction = (0,0,1)
  Length = 0.5
  Length2 = 10
  Profile = -> Sketch087
  ReferenceAxis = -> Sketch087 [N_Axis]
  Refine = true
  Suppressed = false
  Type = 0
FEATURE [PartDesign::Body] Body030
  AllowCompound = false
  Group = -> [Sketch087,Pad054]
  Origin = -> Origin303
  Tip = -> Pad054
FEATURE [PartDesign::Pad] Pad055
  Direction = (0,0,1)
  Length = 0.5
  Length2 = 10
  Profile = -> Sketch088
  ReferenceAxis = -> Sketch088 [N_Axis]
  Refine = true
  Suppressed = false
  Type = 0
FEATURE [PartDesign::Body] Body031
  AllowCompound = false
  Group = -> [Sketch088,Pad055]
  Origin = -> Origin304
  Tip = -> Pad055
FEATURE [PartDesign::Pad] Pad056
  Direction = (0,0,1)
  Length = 0.5
  Length2 = 10
  Placement = pos=(0,0,0) rot=(0,0,1;3.14159rad)
  Profile = -> Sketch089
  ReferenceAxis = -> Sketch089 [N_Axis]
  Refine = true
  Suppressed = false
  Type = 0
FEATURE [PartDesign::Body] Body032
  AllowCompound = false
  Group = -> [Sketch089,Pad056]
  Origin = -> Origin305
  Tip = -> Pad056
FEATURE [PartDesign::Pad] Pad057
  Direction = (0,0,1)
  Length = 0.5
  Length2 = 10
  Placement = pos=(0,0,0) rot=(0,0,1;3.14159rad)
  Profile = -> Sketch090
  ReferenceAxis = -> Sketch090 [N_Axis]
  Refine = true
  Suppressed = false
  Type = 0
FEATURE [PartDesign::Body] Body033
  AllowCompound = false
  Group = -> [Sketch090,Pad057]
  Origin = -> Origin306
  Tip = -> Pad057
FEATURE [PartDesign::Pad] Pad058
  Direction = (0,0,1)
  Length = 0.5
  Length2 = 10
  Placement = pos=(0,0,0) rot=(0,0,1;3.14159rad)
  Profile = -> Sketch091
  ReferenceAxis = -> Sketch091 [N_Axis]
  Refine = true
  Suppressed = false
  Type = 0
FEATURE [PartDesign::Body] Body034
  AllowCompound = false
  Group = -> [Sketch091,Pad058]
  Origin = -> Origin307
  Tip = -> Pad058
FEATURE [PartDesign::Pad] Pad059
  Direction = (0,0,1)
  Length = 0.5
  Length2 = 10
  Placement = pos=(0,0,0) rot=(0,0,1;3.14159rad)
  Profile = -> Sketch092
  ReferenceAxis = -> Sketch092 [N_Axis]
  Refine = true
  Suppressed = false
  Type = 0
FEATURE [PartDesign::Body] Body035
  AllowCompound = false
  Group = -> [Sketch092,Pad059]
  Origin = -> Origin308
  Tip = -> Pad059
FEATURE [App::Part] Part004
  Group = -> [Body030,Body031,Body032,Body033,Body034,Body035]
  Origin = -> Origin302
  Placement = pos=(-5.69031,126.5,5.9) rot=(0,0,1;0rad)
FEATURE [Part::Cut] Cut001  label="Reset Button"
  Base = -> Body017
  Tool = -> Part004
FEATURE [Part::Feature] Part005  label="Reset Button print"
  Placement = pos=(-5.69031,126.5,5.9) rot=(0,0,1;0rad)
  shape: bbox 8.662 x 7.861 x 0.5 mm, 73 faces, 6 solids (baked)
FEATURE [PartDesign::Pad] Pad060
  Direction = (0,0,1)
  Length = 0.5
  Length2 = 10
  Profile = -> Sketch076
  ReferenceAxis = -> Sketch076 [N_Axis]
  Refine = true
  Suppressed = false
  Type = 0
FEATURE [PartDesign::Body] Body036
  AllowCompound = false
  Group = -> [Sketch076,Pad060]
  Origin = -> Origin309
  Tip = -> Pad060
FEATURE [PartDesign::Pad] Pad061
  Direction = (0,0,1)
  Length = 0.5
  Length2 = 10
  Profile = -> Sketch077
  ReferenceAxis = -> Sketch077 [N_Axis]
  Refine = true
  Suppressed = false
  Type = 0
FEATURE [PartDesign::Body] Body037
  AllowCompound = false
  Group = -> [Sketch077,Pad061]
  Origin = -> Origin310
  Tip = -> Pad061
FEATURE [PartDesign::Pad] Pad062
  Direction = (0,0,1)
  Length = 0.5
  Length2 = 10
  Placement = pos=(0,0,0) rot=(0,0,1;3.14159rad)
  Profile = -> Sketch078
  ReferenceAxis = -> Sketch078 [N_Axis]
  Refine = true
  Suppressed = false
  Type = 0
FEATURE [PartDesign::Body] Body038
  AllowCompound = false
  Group = -> [Sketch078,Pad062]
  Origin = -> Origin311
  Tip = -> Pad062
FEATURE [PartDesign::Pad] Pad063
  Direction = (0,0,1)
  Length = 0.5
  Length2 = 10
  Placement = pos=(0,0,0) rot=(0,0,1;3.14159rad)
  Profile = -> Sketch079
  ReferenceAxis = -> Sketch079 [N_Axis]
  Refine = true
  Suppressed = false
  Type = 0
FEATURE [PartDesign::Body] Body039
  AllowCompound = false
  Group = -> [Sketch079,Pad063]
  Origin = -> Origin312
  Tip = -> Pad063
FEATURE [PartDesign::Pad] Pad064
  Direction = (0,0,1)
  Length = 0.5
  Length2 = 10
  Placement = pos=(0,0,0) rot=(0,0,1;3.14159rad)
  Profile = -> Sketch080
  ReferenceAxis = -> Sketch080 [N_Axis]
  Refine = true
  Suppressed = false
  Type = 0
FEATURE [PartDesign::Body] Body040
  AllowCompound = false
  Group = -> [Sketch080,Pad064]
  Origin = -> Origin313
  Tip = -> Pad064
FEATURE [PartDesign::Pad] Pad065
  Direction = (0,0,1)
  Length = 0.5
  Length2 = 10
  Placement = pos=(0,0,0) rot=(0,0,1;3.14159rad)
  Profile = -> Sketch081
  ReferenceAxis = -> Sketch081 [N_Axis]
  Refine = true
  Suppressed = false
  Type = 0
FEATURE [PartDesign::Body] Body041
  AllowCompound = false
  Group = -> [Sketch081,Pad065]
  Origin = -> Origin314
  Tip = -> Pad065
FEATURE [PartDesign::Pad] Pad066
  Direction = (0,0,1)
  Length = 0.5
  Length2 = 10
  Profile = -> Sketch082
  ReferenceAxis = -> Sketch082 [N_Axis]
  Refine = true
  Suppressed = false
  Type = 0
FEATURE [PartDesign::Body] Body042
  AllowCompound = false
  Group = -> [Sketch082,Pad066]
  Origin = -> Origin315
  Tip = -> Pad066
FEATURE [PartDesign::Pad] Pad067
  Direction = (0,0,1)
  Length = 0.5
  Length2 = 10
  Profile = -> Sketch083
  ReferenceAxis = -> Sketch083 [N_Axis]
  Refine = true
  Suppressed = false
  Type = 0
FEATURE [PartDesign::Body] Body043
  AllowCompound = false
  Group = -> [Sketch083,Pad067]
  Origin = -> Origin316
  Tip = -> Pad067
FEATURE [PartDesign::Pad] Pad068
  Direction = (0,0,1)
  Length = 0.5
  Length2 = 10
  Profile = -> Sketch084
  ReferenceAxis = -> Sketch084 [N_Axis]
  Refine = true
  Suppressed = false
  Type = 0
FEATURE [PartDesign::Body] Body044
  AllowCompound = false
  Group = -> [Sketch084,Pad068]
  Origin = -> Origin317
  Tip = -> Pad068
FEATURE [PartDesign::Pad] Pad069
  Direction = (0,0,1)
  Length = 0.5
  Length2 = 10
  Profile = -> Sketch085
  ReferenceAxis = -> Sketch085 [N_Axis]
  Refine = true
  Suppressed = false
  Type = 0
FEATURE [PartDesign::Body] Body045
  AllowCompound = false
  Group = -> [Sketch085,Pad069]
  Origin = -> Origin318
  Tip = -> Pad069
FEATURE [PartDesign::Pad] Pad070
  Direction = (0,0,1)
  Length = 0.5
  Length2 = 10
  Profile = -> Sketch086
  ReferenceAxis = -> Sketch086 [N_Axis]
  Refine = true
  Suppressed = false
  Type = 0
FEATURE [PartDesign::Body] Body046
  AllowCompound = false
  Group = -> [Sketch086,Pad070]
  Origin = -> Origin319
  Tip = -> Pad070
FEATURE [App::Part] Part003
  Group = -> [Body036,Body037,Body038,Body039,Body040,Body041,Body042,Body043,Body044,Body045,Body046]
  Origin = -> Origin301
  Placement = pos=(-5.54,126.777,5.89821) rot=(0,0,1;0rad)
FEATURE [Part::Cut] Cut002  label="Quit Button"
  Base = -> Body018
  Tool = -> Part003
FEATURE [Part::Feature] Part006  label="Quit Button print"
  Placement = pos=(-5.54,126.78,5.89821) rot=(0,0,1;0rad)
  shape: bbox 8.682 x 23.13 x 0.5 mm, 137 faces, 11 solids (baked)
FEATURE [Part::Feature] Body047  label="Reset Button plain fat"
  Placement = pos=(0,-32,0) rot=(0,0,1;0rad)
  shape: bbox 15 x 15 x 6.81 mm, 33 faces (baked)
FEATURE [Part::Feature] Body048  label="Quit Button plain fat"
  shape: bbox 15 x 31 x 6.81 mm, 33 faces (baked)
FEATURE [Sketcher::SketchObject] Sketch093
  ArcFitTolerance = 1e-06
  FullyConstrained = false
  MakeInternals = false
  Placement = pos=(0,0,6.39821) rot=(0,0,1;0rad)
  sketch-geometry (29):
    g0: BSplineCurve PolesCount=2 KnotsCount=2 Degree=1 IsPeriodic=0
    g1: BSplineCurve PolesCount=4 KnotsCount=2 Degree=3 IsPeriodic=0
    g2: BSplineCurve PolesCount=4 KnotsCount=2 Degree=3 IsPeriodic=0
    g3: BSplineCurve PolesCount=4 KnotsCount=2 Degree=3 IsPeriodic=0
    g4: BSplineCurve PolesCount=4 KnotsCount=2 Degree=3 IsPeriodic=0
    g5: BSplineCurve PolesCount=4 KnotsCount=2 Degree=3 IsPeriodic=0
    g6: BSplineCurve PolesCount=2 KnotsCount=2 Degree=1 IsPeriodic=0
    g7: BSplineCurve PolesCount=4 KnotsCount=2 Degree=3 IsPeriodic=0
    g8: BSplineCurve PolesCount=2 KnotsCount=2 Degree=1 IsPeriodic=0
    g9: BSplineCurve PolesCount=4 KnotsCount=2 Degree=3 IsPeriodic=0
    g10: BSplineCurve PolesCount=4 KnotsCount=2 Degree=3 IsPeriodic=0
    g11: BSplineCurve PolesCount=2 KnotsCount=2 Degree=1 IsPeriodic=0
    g12: BSplineCurve PolesCount=4 KnotsCount=2 Degree=3 IsPeriodic=0
    g13: BSplineCurve PolesCount=4 KnotsCount=2 Degree=3 IsPeriodic=0
    g14: BSplineCurve PolesCount=4 KnotsCount=2 Degree=3 IsPeriodic=0
    g15: BSplineCurve PolesCount=2 KnotsCount=2 Degree=1 IsPeriodic=0
    g16: BSplineCurve PolesCount=4 KnotsCount=2 Degree=3 IsPeriodic=0
    g17: BSplineCurve PolesCount=2 KnotsCount=2 Degree=1 IsPeriodic=0
    g18: BSplineCurve PolesCount=4 KnotsCount=2 Degree=3 IsPeriodic=0
    g19: BSplineCurve PolesCount=2 KnotsCount=2 Degree=1 IsPeriodic=0
    g20: BSplineCurve PolesCount=2 KnotsCount=2 Degree=1 IsPeriodic=0
    g21: BSplineCurve PolesCount=4 KnotsCount=2 Degree=3 IsPeriodic=0
    g22: BSplineCurve PolesCount=4 KnotsCount=2 Degree=3 IsPeriodic=0
    g23: BSplineCurve PolesCount=2 KnotsCount=2 Degree=1 IsPeriodic=0
    g24: BSplineCurve PolesCount=4 KnotsCount=2 Degree=3 IsPeriodic=0
    g25: BSplineCurve PolesCount=2 KnotsCount=2 Degree=1 IsPeriodic=0
    g26: BSplineCurve PolesCount=4 KnotsCount=2 Degree=3 IsPeriodic=0
    g27: BSplineCurve PolesCount=4 KnotsCount=2 Degree=3 IsPeriodic=0
    g28: BSplineCurve PolesCount=2 KnotsCount=2 Degree=1 IsPeriodic=0
  constraints (29):
    c: Coincident(g0,g1)
    c: Coincident(g1,g2)
    c: Coincident(g2,g3)
    c: Coincident(g3,g4)
    c: Coincident(g4,g5)
    c: Coincident(g5,g6)
    c: Coincident(g6,g7)
    c: Coincident(g7,g8)
    c: Coincident(g8,g9)
    c: Coincident(g9,g10)
    c: Coincident(g10,g11)
    c: Coincident(g11,g12)
    c: Coincident(g12,g13)
    c: Coincident(g13,g14)
    c: Coincident(g14,g15)
    c: Coincident(g15,g16)
    c: Coincident(g16,g17)
    c: Coincident(g17,g18)
    c: Coincident(g18,g19)
    c: Coincident(g19,g20)
    c: Coincident(g20,g21)
    c: Coincident(g21,g22)
    c: Coincident(g22,g23)
    c: Coincident(g23,g24)
    c: Coincident(g24,g25)
    c: Coincident(g25,g26)
    c: Coincident(g26,g27)
    c: Coincident(g27,g28)
    c: Coincident(g28,g0)
FEATURE [Sketcher::SketchObject] Sketch094
  ArcFitTolerance = 1e-06
  FullyConstrained = false
  MakeInternals = false
  Placement = pos=(0,0,6.39821) rot=(0,0,1;0rad)
  sketch-geometry (16):
    g0: BSplineCurve PolesCount=2 KnotsCount=2 Degree=1 IsPeriodic=0
    g1: BSplineCurve PolesCount=4 KnotsCount=2 Degree=3 IsPeriodic=0
    g2: BSplineCurve PolesCount=4 KnotsCount=2 Degree=3 IsPeriodic=0
    g3: BSplineCurve PolesCount=2 KnotsCount=2 Degree=1 IsPeriodic=0
    g4: BSplineCurve PolesCount=2 KnotsCount=2 Degree=1 IsPeriodic=0
    g5: BSplineCurve PolesCount=4 KnotsCount=2 Degree=3 IsPeriodic=0
    g6: BSplineCurve PolesCount=4 KnotsCount=2 Degree=3 IsPeriodic=0
    g7: BSplineCurve PolesCount=2 KnotsCount=2 Degree=1 IsPeriodic=0
    g8: BSplineCurve PolesCount=2 KnotsCount=2 Degree=1 IsPeriodic=0
    g9: BSplineCurve PolesCount=4 KnotsCount=2 Degree=3 IsPeriodic=0
    g10: BSplineCurve PolesCount=4 KnotsCount=2 Degree=3 IsPeriodic=0
    g11: BSplineCurve PolesCount=2 KnotsCount=2 Degree=1 IsPeriodic=0
    g12: BSplineCurve PolesCount=2 KnotsCount=2 Degree=1 IsPeriodic=0
    g13: BSplineCurve PolesCount=4 KnotsCount=2 Degree=3 IsPeriodic=0
    g14: BSplineCurve PolesCount=4 KnotsCount=2 Degree=3 IsPeriodic=0
    g15: BSplineCurve PolesCount=2 KnotsCount=2 Degree=1 IsPeriodic=0
  constraints (16):
    c: Coincident(g0,g1)
    c: Coincident(g1,g2)
    c: Coincident(g2,g3)
    c: Coincident(g3,g4)
    c: Coincident(g4,g5)
    c: Coincident(g5,g6)
    c: Coincident(g6,g7)
    c: Coincident(g7,g8)
    c: Coincident(g8,g9)
    c: Coincident(g9,g10)
    c: Coincident(g10,g11)
    c: Coincident(g11,g12)
    c: Coincident(g12,g13)
    c: Coincident(g13,g14)
    c: Coincident(g14,g15)
    c: Coincident(g15,g0)
FEATURE [Sketcher::SketchObject] Sketch095
  ArcFitTolerance = 1e-06
  FullyConstrained = false
  MakeInternals = false
  Placement = pos=(0,0,6.39821) rot=(0,0,1;0rad)
  sketch-geometry (4):
    g0: BSplineCurve PolesCount=4 KnotsCount=2 Degree=3 IsPeriodic=0
    g1: BSplineCurve PolesCount=4 KnotsCount=2 Degree=3 IsPeriodic=0
    g2: BSplineCurve PolesCount=4 KnotsCount=2 Degree=3 IsPeriodic=0
    g3: BSplineCurve PolesCount=4 KnotsCount=2 Degree=3 IsPeriodic=0
  constraints (4):
    c: Coincident(g0,g1)
    c: Coincident(g1,g2)
    c: Coincident(g2,g3)
    c: Coincident(g3,g0)
FEATURE [Sketcher::SketchObject] Sketch096
  ArcFitTolerance = 1e-06
  FullyConstrained = false
  MakeInternals = false
  Placement = pos=(0,0,6.39821) rot=(0,0,1;0rad)
  sketch-geometry (4):
    g0: BSplineCurve PolesCount=4 KnotsCount=2 Degree=3 IsPeriodic=0
    g1: BSplineCurve PolesCount=4 KnotsCount=2 Degree=3 IsPeriodic=0
    g2: BSplineCurve PolesCount=4 KnotsCount=2 Degree=3 IsPeriodic=0
    g3: BSplineCurve PolesCount=4 KnotsCount=2 Degree=3 IsPeriodic=0
  constraints (4):
    c: Coincident(g0,g1)
    c: Coincident(g1,g2)
    c: Coincident(g2,g3)
    c: Coincident(g3,g0)
FEATURE [PartDesign::Pad] Pad071
  Direction = (0,0,1)
  Length = 0.5
  Length2 = 10
  Placement = pos=(0,0,6.39821) rot=(0,0,1;0rad)
  Profile = -> Sketch093
  ReferenceAxis = -> Sketch093 [N_Axis]
  Refine = true
  Suppressed = false
  Type = 0
FEATURE [PartDesign::Body] Body049
  AllowCompound = false
  Group = -> [Sketch093,Pad071]
  Origin = -> Origin321
  Tip = -> Pad071
FEATURE [PartDesign::Pad] Pad072
  Direction = (0,0,1)
  Length = 0.5
  Length2 = 10
  Placement = pos=(0,0,6.39821) rot=(0,0,1;0rad)
  Profile = -> Sketch094
  ReferenceAxis = -> Sketch094 [N_Axis]
  Refine = true
  Suppressed = false
  Type = 0
FEATURE [PartDesign::Body] Body050
  AllowCompound = false
  Group = -> [Sketch094,Pad072]
  Origin = -> Origin322
  Tip = -> Pad072
FEATURE [PartDesign::Pad] Pad073
  Direction = (0,0,1)
  Length = 0.5
  Length2 = 10
  Placement = pos=(0,0,6.39821) rot=(0,0,1;0rad)
  Profile = -> Sketch095
  ReferenceAxis = -> Sketch095 [N_Axis]
  Refine = true
  Suppressed = false
  Type = 0
FEATURE [PartDesign::Body] Body051
  AllowCompound = false
  Group = -> [Sketch095,Pad073]
  Origin = -> Origin323
  Tip = -> Pad073
FEATURE [PartDesign::Pad] Pad074
  Direction = (0,0,1)
  Length = 0.5
  Length2 = 10
  Placement = pos=(0,0,6.39821) rot=(0,0,1;0rad)
  Profile = -> Sketch096
  ReferenceAxis = -> Sketch096 [N_Axis]
  Refine = true
  Suppressed = false
  Type = 0
FEATURE [PartDesign::Body] Body052
  AllowCompound = false
  Group = -> [Sketch096,Pad074]
  Origin = -> Origin324
  Tip = -> Pad074
FEATURE [App::Part] Part007
  Group = -> [Body049,Body050,Body051,Body052]
  Origin = -> Origin320
  Placement = pos=(0,0,-0.5) rot=(0,0,1;0rad)
FEATURE [Sketcher::SketchObject] Sketch097
  ArcFitTolerance = 1e-06
  FullyConstrained = false
  MakeInternals = false
  Placement = pos=(0,0,6.39821) rot=(0,0,1;0rad)
  sketch-geometry (4):
    g0: BSplineCurve PolesCount=4 KnotsCount=2 Degree=3 IsPeriodic=0
    g1: BSplineCurve PolesCount=4 KnotsCount=2 Degree=3 IsPeriodic=0
    g2: BSplineCurve PolesCount=4 KnotsCount=2 Degree=3 IsPeriodic=0
    g3: BSplineCurve PolesCount=4 KnotsCount=2 Degree=3 IsPeriodic=0
  constraints (4):
    c: Coincident(g0,g1)
    c: Coincident(g1,g2)
    c: Coincident(g2,g3)
    c: Coincident(g3,g0)
FEATURE [Sketcher::SketchObject] Sketch098
  ArcFitTolerance = 1e-06
  FullyConstrained = false
  MakeInternals = false
  Placement = pos=(0,0,6.39821) rot=(0,0,1;0rad)
  sketch-geometry (4):
    g0: BSplineCurve PolesCount=4 KnotsCount=2 Degree=3 IsPeriodic=0
    g1: BSplineCurve PolesCount=4 KnotsCount=2 Degree=3 IsPeriodic=0
    g2: BSplineCurve PolesCount=4 KnotsCount=2 Degree=3 IsPeriodic=0
    g3: BSplineCurve PolesCount=4 KnotsCount=2 Degree=3 IsPeriodic=0
  constraints (4):
    c: Coincident(g0,g1)
    c: Coincident(g1,g2)
    c: Coincident(g2,g3)
    c: Coincident(g3,g0)
FEATURE [Sketcher::SketchObject] Sketch099
  ArcFitTolerance = 1e-06
  FullyConstrained = false
  MakeInternals = false
  Placement = pos=(0,0,6.39821) rot=(0,0,1;0rad)
  sketch-geometry (16):
    g0: BSplineCurve PolesCount=2 KnotsCount=2 Degree=1 IsPeriodic=0
    g1: BSplineCurve PolesCount=4 KnotsCount=2 Degree=3 IsPeriodic=0
    g2: BSplineCurve PolesCount=4 KnotsCount=2 Degree=3 IsPeriodic=0
    g3: BSplineCurve PolesCount=2 KnotsCount=2 Degree=1 IsPeriodic=0
    g4: BSplineCurve PolesCount=2 KnotsCount=2 Degree=1 IsPeriodic=0
    g5: BSplineCurve PolesCount=4 KnotsCount=2 Degree=3 IsPeriodic=0
    g6: BSplineCurve PolesCount=4 KnotsCount=2 Degree=3 IsPeriodic=0
    g7: BSplineCurve PolesCount=2 KnotsCount=2 Degree=1 IsPeriodic=0
    g8: BSplineCurve PolesCount=2 KnotsCount=2 Degree=1 IsPeriodic=0
    g9: BSplineCurve PolesCount=4 KnotsCount=2 Degree=3 IsPeriodic=0
    g10: BSplineCurve PolesCount=4 KnotsCount=2 Degree=3 IsPeriodic=0
    g11: BSplineCurve PolesCount=2 KnotsCount=2 Degree=1 IsPeriodic=0
    g12: BSplineCurve PolesCount=2 KnotsCount=2 Degree=1 IsPeriodic=0
    g13: BSplineCurve PolesCount=4 KnotsCount=2 Degree=3 IsPeriodic=0
    g14: BSplineCurve PolesCount=4 KnotsCount=2 Degree=3 IsPeriodic=0
    g15: BSplineCurve PolesCount=2 KnotsCount=2 Degree=1 IsPeriodic=0
  constraints (16):
    c: Coincident(g0,g1)
    c: Coincident(g1,g2)
    c: Coincident(g2,g3)
    c: Coincident(g3,g4)
    c: Coincident(g4,g5)
    c: Coincident(g5,g6)
    c: Coincident(g6,g7)
    c: Coincident(g7,g8)
    c: Coincident(g8,g9)
    c: Coincident(g9,g10)
    c: Coincident(g10,g11)
    c: Coincident(g11,g12)
    c: Coincident(g12,g13)
    c: Coincident(g13,g14)
    c: Coincident(g14,g15)
    c: Coincident(g15,g0)
FEATURE [Sketcher::SketchObject] Sketch100
  ArcFitTolerance = 1e-06
  FullyConstrained = false
  MakeInternals = false
  Placement = pos=(0,0,6.39821) rot=(0,0,1;0rad)
  sketch-geometry (22):
    g0: BSplineCurve PolesCount=2 KnotsCount=2 Degree=1 IsPeriodic=0
    g1: BSplineCurve PolesCount=4 KnotsCount=2 Degree=3 IsPeriodic=0
    g2: BSplineCurve PolesCount=4 KnotsCount=2 Degree=3 IsPeriodic=0
    g3: BSplineCurve PolesCount=4 KnotsCount=2 Degree=3 IsPeriodic=0
    g4: BSplineCurve PolesCount=2 KnotsCount=2 Degree=1 IsPeriodic=0
    g5: BSplineCurve PolesCount=4 KnotsCount=2 Degree=3 IsPeriodic=0
    g6: BSplineCurve PolesCount=2 KnotsCount=2 Degree=1 IsPeriodic=0
    g7: BSplineCurve PolesCount=4 KnotsCount=2 Degree=3 IsPeriodic=0
    g8: BSplineCurve PolesCount=2 KnotsCount=2 Degree=1 IsPeriodic=0
    g9: BSplineCurve PolesCount=4 KnotsCount=2 Degree=3 IsPeriodic=0
    g10: BSplineCurve PolesCount=4 KnotsCount=2 Degree=3 IsPeriodic=0
    g11: BSplineCurve PolesCount=2 KnotsCount=2 Degree=1 IsPeriodic=0
    g12: BSplineCurve PolesCount=4 KnotsCount=2 Degree=3 IsPeriodic=0
    g13: BSplineCurve PolesCount=4 KnotsCount=2 Degree=3 IsPeriodic=0
    g14: BSplineCurve PolesCount=4 KnotsCount=2 Degree=3 IsPeriodic=0
    g15: BSplineCurve PolesCount=4 KnotsCount=2 Degree=3 IsPeriodic=0
    g16: BSplineCurve PolesCount=4 KnotsCount=2 Degree=3 IsPeriodic=0
    g17: BSplineCurve PolesCount=2 KnotsCount=2 Degree=1 IsPeriodic=0
    g18: BSplineCurve PolesCount=4 KnotsCount=2 Degree=3 IsPeriodic=0
    g19: BSplineCurve PolesCount=4 KnotsCount=2 Degree=3 IsPeriodic=0
    g20: BSplineCurve PolesCount=4 KnotsCount=2 Degree=3 IsPeriodic=0
    g21: BSplineCurve PolesCount=4 KnotsCount=2 Degree=3 IsPeriodic=0
  constraints (22):
    c: Coincident(g0,g1)
    c: Coincident(g1,g2)
    c: Coincident(g2,g3)
    c: Coincident(g3,g4)
    c: Coincident(g4,g5)
    c: Coincident(g5,g6)
    c: Coincident(g6,g7)
    c: Coincident(g7,g8)
    c: Coincident(g8,g9)
    c: Coincident(g9,g10)
    c: Coincident(g10,g11)
    c: Coincident(g11,g12)
    c: Coincident(g12,g13)
    c: Coincident(g13,g14)
    c: Coincident(g14,g15)
    c: Coincident(g15,g16)
    c: Coincident(g16,g17)
    c: Coincident(g17,g18)
    c: Coincident(g18,g19)
    c: Coincident(g19,g20)
    c: Coincident(g20,g21)
    c: Coincident(g21,g0)
FEATURE [Sketcher::SketchObject] Sketch101
  ArcFitTolerance = 1e-06
  FullyConstrained = false
  MakeInternals = false
  Placement = pos=(0,0,6.39821) rot=(0,0,1;0rad)
  sketch-geometry (13):
    g0: BSplineCurve PolesCount=2 KnotsCount=2 Degree=1 IsPeriodic=0
    g1: BSplineCurve PolesCount=4 KnotsCount=2 Degree=3 IsPeriodic=0
    g2: BSplineCurve PolesCount=4 KnotsCount=2 Degree=3 IsPeriodic=0
    g3: BSplineCurve PolesCount=2 KnotsCount=2 Degree=1 IsPeriodic=0
    g4: BSplineCurve PolesCount=2 KnotsCount=2 Degree=1 IsPeriodic=0
    g5: BSplineCurve PolesCount=4 KnotsCount=2 Degree=3 IsPeriodic=0
    g6: BSplineCurve PolesCount=4 KnotsCount=2 Degree=3 IsPeriodic=0
    g7: BSplineCurve PolesCount=2 KnotsCount=2 Degree=1 IsPeriodic=0
    g8: BSplineCurve PolesCount=4 KnotsCount=2 Degree=3 IsPeriodic=0
    g9: BSplineCurve PolesCount=2 KnotsCount=2 Degree=1 IsPeriodic=0
    g10: BSplineCurve PolesCount=4 KnotsCount=2 Degree=3 IsPeriodic=0
    g11: BSplineCurve PolesCount=4 KnotsCount=2 Degree=3 IsPeriodic=0
    g12: BSplineCurve PolesCount=2 KnotsCount=2 Degree=1 IsPeriodic=0
  constraints (13):
    c: Coincident(g0,g1)
    c: Coincident(g1,g2)
    c: Coincident(g2,g3)
    c: Coincident(g3,g4)
    c: Coincident(g4,g5)
    c: Coincident(g5,g6)
    c: Coincident(g6,g7)
    c: Coincident(g7,g8)
    c: Coincident(g8,g9)
    c: Coincident(g9,g10)
    c: Coincident(g10,g11)
    c: Coincident(g11,g12)
    c: Coincident(g12,g0)
FEATURE [Sketcher::SketchObject] Sketch102
  ArcFitTolerance = 1e-06
  FullyConstrained = false
  MakeInternals = false
  Placement = pos=(0,0,6.39821) rot=(0,0,1;0rad)
  sketch-geometry (12):
    g0: BSplineCurve PolesCount=2 KnotsCount=2 Degree=1 IsPeriodic=0
    g1: BSplineCurve PolesCount=4 KnotsCount=2 Degree=3 IsPeriodic=0
    g2: BSplineCurve PolesCount=4 KnotsCount=2 Degree=3 IsPeriodic=0
    g3: BSplineCurve PolesCount=2 KnotsCount=2 Degree=1 IsPeriodic=0
    g4: BSplineCurve PolesCount=4 KnotsCount=2 Degree=3 IsPeriodic=0
    g5: BSplineCurve PolesCount=2 KnotsCount=2 Degree=1 IsPeriodic=0
    g6: BSplineCurve PolesCount=4 KnotsCount=2 Degree=3 IsPeriodic=0
    g7: BSplineCurve PolesCount=2 KnotsCount=2 Degree=1 IsPeriodic=0
    g8: BSplineCurve PolesCount=4 KnotsCount=2 Degree=3 IsPeriodic=0
    g9: BSplineCurve PolesCount=2 KnotsCount=2 Degree=1 IsPeriodic=0
    g10: BSplineCurve PolesCount=4 KnotsCount=2 Degree=3 IsPeriodic=0
    g11: BSplineCurve PolesCount=2 KnotsCount=2 Degree=1 IsPeriodic=0
  constraints (12):
    c: Coincident(g0,g1)
    c: Coincident(g1,g2)
    c: Coincident(g2,g3)
    c: Coincident(g3,g0)
    c: Coincident(g4,g5)
    c: Coincident(g5,g6)
    c: Coincident(g6,g7)
    c: Coincident(g7,g8)
    c: Coincident(g8,g9)
    c: Coincident(g9,g10)
    c: Coincident(g10,g11)
    c: Coincident(g11,g4)
FEATURE [Sketcher::SketchObject] Sketch103
  ArcFitTolerance = 1e-06
  FullyConstrained = false
  MakeInternals = false
  Placement = pos=(0,0,6.39821) rot=(0,0,1;0rad)
  sketch-geometry (12):
    g0: BSplineCurve PolesCount=2 KnotsCount=2 Degree=1 IsPeriodic=0
    g1: BSplineCurve PolesCount=4 KnotsCount=2 Degree=3 IsPeriodic=0
    g2: BSplineCurve PolesCount=4 KnotsCount=2 Degree=3 IsPeriodic=0
    g3: BSplineCurve PolesCount=2 KnotsCount=2 Degree=1 IsPeriodic=0
    g4: BSplineCurve PolesCount=4 KnotsCount=2 Degree=3 IsPeriodic=0
    g5: BSplineCurve PolesCount=2 KnotsCount=2 Degree=1 IsPeriodic=0
    g6: BSplineCurve PolesCount=4 KnotsCount=2 Degree=3 IsPeriodic=0
    g7: BSplineCurve PolesCount=2 KnotsCount=2 Degree=1 IsPeriodic=0
    g8: BSplineCurve PolesCount=4 KnotsCount=2 Degree=3 IsPeriodic=0
    g9: BSplineCurve PolesCount=2 KnotsCount=2 Degree=1 IsPeriodic=0
    g10: BSplineCurve PolesCount=4 KnotsCount=2 Degree=3 IsPeriodic=0
    g11: BSplineCurve PolesCount=2 KnotsCount=2 Degree=1 IsPeriodic=0
  constraints (12):
    c: Coincident(g0,g1)
    c: Coincident(g1,g2)
    c: Coincident(g2,g3)
    c: Coincident(g3,g0)
    c: Coincident(g4,g5)
    c: Coincident(g5,g6)
    c: Coincident(g6,g7)
    c: Coincident(g7,g8)
    c: Coincident(g8,g9)
    c: Coincident(g9,g10)
    c: Coincident(g10,g11)
    c: Coincident(g11,g4)
FEATURE [Sketcher::SketchObject] Sketch104
  ArcFitTolerance = 1e-06
  FullyConstrained = false
  MakeInternals = false
  Placement = pos=(0,0,6.39821) rot=(0,0,1;0rad)
  sketch-geometry (12):
    g0: BSplineCurve PolesCount=4 KnotsCount=2 Degree=3 IsPeriodic=0
    g1: BSplineCurve PolesCount=2 KnotsCount=2 Degree=1 IsPeriodic=0
    g2: BSplineCurve PolesCount=4 KnotsCount=2 Degree=3 IsPeriodic=0
    g3: BSplineCurve PolesCount=2 KnotsCount=2 Degree=1 IsPeriodic=0
    g4: BSplineCurve PolesCount=4 KnotsCount=2 Degree=3 IsPeriodic=0
    g5: BSplineCurve PolesCount=2 KnotsCount=2 Degree=1 IsPeriodic=0
    g6: BSplineCurve PolesCount=4 KnotsCount=2 Degree=3 IsPeriodic=0
    g7: BSplineCurve PolesCount=2 KnotsCount=2 Degree=1 IsPeriodic=0
    g8: BSplineCurve PolesCount=2 KnotsCount=2 Degree=1 IsPeriodic=0
    g9: BSplineCurve PolesCount=4 KnotsCount=2 Degree=3 IsPeriodic=0
    g10: BSplineCurve PolesCount=4 KnotsCount=2 Degree=3 IsPeriodic=0
    g11: BSplineCurve PolesCount=2 KnotsCount=2 Degree=1 IsPeriodic=0
  constraints (12):
    c: Coincident(g0,g1)
    c: Coincident(g1,g2)
    c: Coincident(g2,g3)
    c: Coincident(g3,g4)
    c: Coincident(g4,g5)
    c: Coincident(g5,g6)
    c: Coincident(g6,g7)
    c: Coincident(g7,g0)
    c: Coincident(g8,g9)
    c: Coincident(g9,g10)
    c: Coincident(g10,g11)
    c: Coincident(g11,g8)
FEATURE [Sketcher::SketchObject] Sketch105
  ArcFitTolerance = 1e-06
  FullyConstrained = false
  MakeInternals = false
  Placement = pos=(0,0,6.39821) rot=(0,0,1;0rad)
  sketch-geometry (12):
    g0: BSplineCurve PolesCount=4 KnotsCount=2 Degree=3 IsPeriodic=0
    g1: BSplineCurve PolesCount=2 KnotsCount=2 Degree=1 IsPeriodic=0
    g2: BSplineCurve PolesCount=4 KnotsCount=2 Degree=3 IsPeriodic=0
    g3: BSplineCurve PolesCount=2 KnotsCount=2 Degree=1 IsPeriodic=0
    g4: BSplineCurve PolesCount=4 KnotsCount=2 Degree=3 IsPeriodic=0
    g5: BSplineCurve PolesCount=2 KnotsCount=2 Degree=1 IsPeriodic=0
    g6: BSplineCurve PolesCount=4 KnotsCount=2 Degree=3 IsPeriodic=0
    g7: BSplineCurve PolesCount=2 KnotsCount=2 Degree=1 IsPeriodic=0
    g8: BSplineCurve PolesCount=2 KnotsCount=2 Degree=1 IsPeriodic=0
    g9: BSplineCurve PolesCount=4 KnotsCount=2 Degree=3 IsPeriodic=0
    g10: BSplineCurve PolesCount=4 KnotsCount=2 Degree=3 IsPeriodic=0
    g11: BSplineCurve PolesCount=2 KnotsCount=2 Degree=1 IsPeriodic=0
  constraints (12):
    c: Coincident(g0,g1)
    c: Coincident(g1,g2)
    c: Coincident(g2,g3)
    c: Coincident(g3,g4)
    c: Coincident(g4,g5)
    c: Coincident(g5,g6)
    c: Coincident(g6,g7)
    c: Coincident(g7,g0)
    c: Coincident(g8,g9)
    c: Coincident(g9,g10)
    c: Coincident(g10,g11)
    c: Coincident(g11,g8)
FEATURE [PartDesign::Pad] Pad075
  Direction = (0,0,1)
  Length = 0.5
  Length2 = 10
  Placement = pos=(0,0,6.39821) rot=(0,0,1;0rad)
  Profile = -> Sketch097
  ReferenceAxis = -> Sketch097 [N_Axis]
  Refine = true
  Suppressed = false
  Type = 0
FEATURE [PartDesign::Body] Body053
  AllowCompound = false
  Group = -> [Sketch097,Pad075]
  Origin = -> Origin326
  Tip = -> Pad075
FEATURE [PartDesign::Pad] Pad076
  Direction = (0,0,1)
  Length = 0.5
  Length2 = 10
  Placement = pos=(0,0,6.39821) rot=(0,0,1;0rad)
  Profile = -> Sketch098
  ReferenceAxis = -> Sketch098 [N_Axis]
  Refine = true
  Suppressed = false
  Type = 0
FEATURE [PartDesign::Body] Body054
  AllowCompound = false
  Group = -> [Sketch098,Pad076]
  Origin = -> Origin327
  Tip = -> Pad076
FEATURE [PartDesign::Pad] Pad077
  Direction = (0,0,1)
  Length = 0.5
  Length2 = 10
  Placement = pos=(0,0,6.39821) rot=(0,0,1;0rad)
  Profile = -> Sketch099
  ReferenceAxis = -> Sketch099 [N_Axis]
  Refine = true
  Suppressed = false
  Type = 0
FEATURE [PartDesign::Body] Body055
  AllowCompound = false
  Group = -> [Sketch099,Pad077]
  Origin = -> Origin328
  Tip = -> Pad077
FEATURE [PartDesign::Pad] Pad078
  Direction = (0,0,1)
  Length = 0.5
  Length2 = 10
  Placement = pos=(0,0,6.39821) rot=(0,0,1;0rad)
  Profile = -> Sketch100
  ReferenceAxis = -> Sketch100 [N_Axis]
  Refine = true
  Suppressed = false
  Type = 0
FEATURE [PartDesign::Body] Body056
  AllowCompound = false
  Group = -> [Sketch100,Pad078]
  Origin = -> Origin329
  Tip = -> Pad078
FEATURE [PartDesign::Pad] Pad079
  Direction = (0,0,1)
  Length = 0.5
  Length2 = 10
  Placement = pos=(0,0,6.39821) rot=(0,0,1;0rad)
  Profile = -> Sketch101
  ReferenceAxis = -> Sketch101 [N_Axis]
  Refine = true
  Suppressed = false
  Type = 0
FEATURE [PartDesign::Body] Body057
  AllowCompound = false
  Group = -> [Sketch101,Pad079]
  Origin = -> Origin330
  Tip = -> Pad079
FEATURE [PartDesign::Pad] Pad080
  Direction = (0,0,1)
  Length = 0.5
  Length2 = 10
  Placement = pos=(0,0,6.39821) rot=(0,0,1;0rad)
  Profile = -> Sketch102
  ReferenceAxis = -> Sketch102 [N_Axis]
  Refine = true
  Suppressed = false
  Type = 0
FEATURE [PartDesign::Body] Body058
  AllowCompound = false
  Group = -> [Sketch102,Pad080]
  Origin = -> Origin331
  Tip = -> Pad080
FEATURE [PartDesign::Pad] Pad081
  Direction = (0,0,1)
  Length = 0.5
  Length2 = 10
  Placement = pos=(0,0,6.39821) rot=(0,0,1;0rad)
  Profile = -> Sketch103
  ReferenceAxis = -> Sketch103 [N_Axis]
  Refine = true
  Suppressed = false
  Type = 0
FEATURE [PartDesign::Body] Body059
  AllowCompound = false
  Group = -> [Sketch103,Pad081]
  Origin = -> Origin332
  Tip = -> Pad081
FEATURE [PartDesign::Pad] Pad082
  Direction = (0,0,1)
  Length = 0.5
  Length2 = 10
  Placement = pos=(0,0,6.39821) rot=(0,0,1;0rad)
  Profile = -> Sketch104
  ReferenceAxis = -> Sketch104 [N_Axis]
  Refine = true
  Suppressed = false
  Type = 0
FEATURE [PartDesign::Body] Body060
  AllowCompound = false
  Group = -> [Sketch104,Pad082]
  Origin = -> Origin333
  Tip = -> Pad082
FEATURE [PartDesign::Pad] Pad083
  Direction = (0,0,1)
  Length = 0.5
  Length2 = 10
  Placement = pos=(0,0,6.39821) rot=(0,0,1;0rad)
  Profile = -> Sketch105
  ReferenceAxis = -> Sketch105 [N_Axis]
  Refine = true
  Suppressed = false
  Type = 0
FEATURE [PartDesign::Body] Body061
  AllowCompound = false
  Group = -> [Sketch105,Pad083]
  Origin = -> Origin334
  Tip = -> Pad083
FEATURE [App::Part] Part008
  Group = -> [Body053,Body054,Body055,Body056,Body057,Body058,Body059,Body060,Body061]
  Origin = -> Origin325
  Placement = pos=(0,0,-0.5) rot=(0,0,1;0rad)
FEATURE [Part::Cut] Cut003  label="Reset Button fat"
  Base = -> Body047
  Tool = -> Part007
FEATURE [Part::Feature] Part009  label="Reset Button fat print"
  Placement = pos=(0,0,-0.5) rot=(0,0,1;0rad)
  shape: bbox 8.093 x 7.013 x 0.5 mm, 61 faces, 4 solids (baked)
FEATURE [Part::Cut] Cut004  label="Quit Button fat"
  Base = -> Body048
  Tool = -> Part008
FEATURE [Part::Feature] Part010  label="Quit Button fat print"
  Placement = pos=(0,0,-0.5) rot=(0,0,1;0rad)
  shape: bbox 8.112 x 21.61 x 0.5 mm, 125 faces, 9 solids (baked)
FEATURE [Part::Feature] path1
  shape: bbox 7.133 x 7.132 x 2e-07 mm, 0 faces, 0 solids (baked)
FEATURE [Part::Feature] path320
  shape: bbox 3.566 x 3.566 x 2e-07 mm, 0 faces, 0 solids (baked)
FEATURE [Part::Feature] path321
  shape: bbox 17.37 x 4.252 x 2e-07 mm, 0 faces, 0 solids (baked)
FEATURE [Part::Feature] path322
  shape: bbox 6.416 x 0.9813 x 2e-07 mm, 0 faces, 0 solids (baked)
FEATURE [Part::Feature] path323
  shape: bbox 5.362 x 14.66 x 2e-07 mm, 0 faces, 0 solids (baked)
FEATURE [Part::Feature] path324
  shape: bbox 1.783 x 1.783 x 2e-07 mm, 0 faces, 0 solids (baked)
FEATURE [Part::Feature] path325
  shape: bbox 8.024 x 19.17 x 2e-07 mm, 0 faces, 0 solids (baked)
FEATURE [Part::Feature] path326
  shape: bbox 1.783 x 1.783 x 2e-07 mm, 0 faces, 0 solids (baked)
FEATURE [Part::Feature] path327
  shape: bbox 6.241 x 16.05 x 2e-07 mm, 0 faces, 0 solids (baked)
FEATURE [Part::Feature] path328
  shape: bbox 1.783 x 1.783 x 2e-07 mm, 0 faces, 0 solids (baked)
FEATURE [Part::Feature] path329
  shape: bbox 22.78 x 18.28 x 2e-07 mm, 0 faces, 0 solids (baked)
FEATURE [Part::Feature] path330
  shape: bbox 1.783 x 1.783 x 2e-07 mm, 0 faces, 0 solids (baked)
FEATURE [Part::Feature] path331
  shape: bbox 1.783 x 1.783 x 2e-07 mm, 0 faces, 0 solids (baked)
FEATURE [Part::Feature] path332
  shape: bbox 19.14 x 10.32 x 2e-07 mm, 0 faces, 0 solids (baked)
FEATURE [Part::Feature] path333
  shape: bbox 19.33 x 10.73 x 2e-07 mm, 0 faces, 0 solids (baked)
FEATURE [Part::Feature] path334
  shape: bbox 20.74 x 6.339 x 2e-07 mm, 0 faces, 0 solids (baked)
FEATURE [Part::Feature] path335
  shape: bbox 4.461 x 7.132 x 2e-07 mm, 0 faces, 0 solids (baked)
FEATURE [Part::Feature] path336
  shape: bbox 12.31 x 4.368 x 2e-07 mm, 0 faces, 0 solids (baked)
FEATURE [Part::Feature] path337
  shape: bbox 16.87 x 11.38 x 2e-07 mm, 0 faces, 0 solids (baked)
FEATURE [Part::Feature] path338
  shape: bbox 10.85 x 6.072 x 2e-07 mm, 0 faces, 0 solids (baked)
FEATURE [Part::Extrusion] Extrude
  Base = -> path1
  Dir = (0,0,1)
  DirMode = 2
  FaceMakerClass = Part::FaceMakerBullseye
  FaceMakerMode = 3
  LengthFwd = 2
  LengthRev = 0
  Reversed = true
  Solid = true
  Symmetric = false
FEATURE [Part::Extrusion] Extrude001
  Base = -> path320
  Dir = (0,0,-1)
  DirMode = 2
  FaceMakerClass = Part::FaceMakerBullseye
  FaceMakerMode = 3
  LengthFwd = 2
  LengthRev = 0
  Solid = true
  Symmetric = false
FEATURE [Part::Cut] Cut005
  Base = -> Extrude
  Tool = -> Extrude001
FEATURE [Part::Extrusion] Extrude002
  Base = -> path321
  Dir = (0,0,1)
  DirMode = 2
  FaceMakerClass = Part::FaceMakerBullseye
  FaceMakerMode = 3
  LengthFwd = 2
  LengthRev = 0
  Reversed = true
  Solid = true
  Symmetric = false
FEATURE [Part::Extrusion] Extrude003
  Base = -> path322
  Dir = (0,0,-1)
  DirMode = 2
  FaceMakerClass = Part::FaceMakerBullseye
  FaceMakerMode = 3
  LengthFwd = 2
  LengthRev = 0
  Solid = true
  Symmetric = false
FEATURE [Part::Cut] Cut006
  Base = -> Extrude002
  Tool = -> Extrude003
FEATURE [Part::Extrusion] Extrude004
  Base = -> path323
  Dir = (0,0,1)
  DirMode = 2
  FaceMakerClass = Part::FaceMakerBullseye
  FaceMakerMode = 3
  LengthFwd = 2
  LengthRev = 0
  Reversed = true
  Solid = true
  Symmetric = false
FEATURE [Part::Extrusion] Extrude005
  Base = -> path324
  Dir = (0,0,-1)
  DirMode = 2
  FaceMakerClass = Part::FaceMakerBullseye
  FaceMakerMode = 3
  LengthFwd = 2
  LengthRev = 0
  Solid = true
  Symmetric = false
FEATURE [Part::Cut] Cut007
  Base = -> Extrude004
  Tool = -> Extrude005
FEATURE [Part::Extrusion] Extrude006
  Base = -> path325
  Dir = (0,0,1)
  DirMode = 2
  FaceMakerClass = Part::FaceMakerBullseye
  FaceMakerMode = 3
  LengthFwd = 2
  LengthRev = 0
  Reversed = true
  Solid = true
  Symmetric = false
FEATURE [Part::Extrusion] Extrude007
  Base = -> path326
  Dir = (0,0,-1)
  DirMode = 2
  FaceMakerClass = Part::FaceMakerBullseye
  FaceMakerMode = 3
  LengthFwd = 2
  LengthRev = 0
  Solid = true
  Symmetric = false
FEATURE [Part::Cut] Cut008
  Base = -> Extrude006
  Tool = -> Extrude007
FEATURE [Part::Extrusion] Extrude008
  Base = -> path327
  Dir = (0,0,1)
  DirMode = 2
  FaceMakerClass = Part::FaceMakerBullseye
  FaceMakerMode = 3
  LengthFwd = 2
  LengthRev = 0
  Reversed = true
  Solid = true
  Symmetric = false
FEATURE [Part::Extrusion] Extrude009
  Base = -> path328
  Dir = (0,0,-1)
  DirMode = 2
  FaceMakerClass = Part::FaceMakerBullseye
  FaceMakerMode = 3
  LengthFwd = 2
  LengthRev = 0
  Solid = true
  Symmetric = false
FEATURE [Part::Cut] Cut009
  Base = -> Extrude008
  Tool = -> Extrude009
FEATURE [Part::Extrusion] Extrude010
  Base = -> path329
  Dir = (0,0,1)
  DirMode = 2
  FaceMakerClass = Part::FaceMakerBullseye
  FaceMakerMode = 3
  LengthFwd = 2
  LengthRev = 0
  Reversed = true
  Solid = true
  Symmetric = false
FEATURE [Part::Extrusion] Extrude011
  Base = -> path330
  Dir = (0,0,-1)
  DirMode = 2
  FaceMakerClass = Part::FaceMakerBullseye
  FaceMakerMode = 3
  LengthFwd = 2
  LengthRev = 0
  Solid = true
  Symmetric = false
FEATURE [Part::Extrusion] Extrude012
  Base = -> path331
  Dir = (0,0,-1)
  DirMode = 2
  FaceMakerClass = Part::FaceMakerBullseye
  FaceMakerMode = 3
  LengthFwd = 2
  LengthRev = 0
  Solid = true
  Symmetric = false
FEATURE [Part::Cut] Cut010
  Base = -> Extrude010
  Tool = -> Extrude011
FEATURE [Part::Cut] Cut011
  Base = -> Cut010
  Tool = -> Extrude012
FEATURE [Part::Extrusion] Extrude013
  Base = -> path332
  Dir = (0,0,1)
  DirMode = 2
  FaceMakerClass = Part::FaceMakerBullseye
  FaceMakerMode = 3
  LengthFwd = 2
  LengthRev = 0
  Reversed = true
  Solid = true
  Symmetric = false
FEATURE [Part::Extrusion] Extrude014
  Base = -> path333
  Dir = (0,0,1)
  DirMode = 2
  FaceMakerClass = Part::FaceMakerBullseye
  FaceMakerMode = 3
  LengthFwd = 2
  LengthRev = 0
  Reversed = true
  Solid = true
  Symmetric = false
FEATURE [Part::Extrusion] Extrude015
  Base = -> path334
  Dir = (0,0,1)
  DirMode = 2
  FaceMakerClass = Part::FaceMakerBullseye
  FaceMakerMode = 3
  LengthFwd = 2
  LengthRev = 0
  Reversed = true
  Solid = true
  Symmetric = false
FEATURE [Part::Extrusion] Extrude016
  Base = -> path335
  Dir = (0,0,1)
  DirMode = 2
  FaceMakerClass = Part::FaceMakerBullseye
  FaceMakerMode = 3
  LengthFwd = 2
  LengthRev = 0
  Reversed = true
  Solid = true
  Symmetric = false
FEATURE [Part::Extrusion] Extrude017
  Base = -> path336
  Dir = (0,0,1)
  DirMode = 2
  FaceMakerClass = Part::FaceMakerBullseye
  FaceMakerMode = 3
  LengthFwd = 2
  LengthRev = 0
  Reversed = true
  Solid = true
  Symmetric = false
FEATURE [Part::Extrusion] Extrude018
  Base = -> path337
  Dir = (0,0,1)
  DirMode = 2
  FaceMakerClass = Part::FaceMakerBullseye
  FaceMakerMode = 3
  LengthFwd = 2
  LengthRev = 0
  Reversed = true
  Solid = true
  Symmetric = false
FEATURE [Part::Extrusion] Extrude019
  Base = -> path338
  Dir = (0,0,-1)
  DirMode = 2
  FaceMakerClass = Part::FaceMakerBullseye
  FaceMakerMode = 3
  LengthFwd = 2
  LengthRev = 0
  Solid = true
  Symmetric = false
FEATURE [Part::Cut] Cut012
  Base = -> Extrude018
  Tool = -> Extrude019
FEATURE [App::Part] Part011  label="Logo"
  Group = -> [path332,path333,path334,path335,path336,Extrude001,Extrude,path1,path320,Cut005,Extrude003,Extrude002,path321,path322,Cut006,Extrude005,path324,path323,Extrude004,Cut007,Extrude006,path325,Extrude007,path326,Cut008,Extrude009,Extrude008,path327,path328,Cut009,Extrude011,Extrude012,Cut010,Extrude010,path330,path331,path329,Cut011,Extrude013,Extrude014,Extrude015,Extrude016,Extrude017,Extrude018,+4 more]
  Origin = -> Origin335
  Placement = pos=(-83.95,152.84,3.2) rot=(0,0,1;0rad)
FEATURE [Part::Cut] Cut013  label="cover embossed unedited"
  Base = -> Body
  Tool = -> Part011
FEATURE [TechDraw::DrawSVGTemplate] Template005
  Height = 210
  Orientation = 1
  Template = /Applications/FreeCAD.app/Contents/Resources/share/Mod/TechDraw/Templates/Default_Template_A4_Landscape.svg
  Width = 297
FEATURE [TechDraw::DrawProjGroupItem] View005
  CoarseView = false
  Direction = (0,0,1)
  Focus = 100
  HardHidden = false
  IsoCount = 0
  IsoHidden = false
  IsoVisible = false
  LockPosition = false
  Perspective = false
  Rotation = 0
  RotationVector = (1,0,0)
  ScaleType = 0
  ScrubCount = 1
  SeamHidden = false
  SeamVisible = true
  SmoothHidden = false
  SmoothVisible = true
  Source = -> [Cut013]
  Type = 0
  X = 148.5
  XDirection = (1,0,0)
  Y = 105
FEATURE [TechDraw::DrawPage] Page005  label="LogoPlacement"
  KeepUpdated = true
  NextBalloonIndex = 1
  ProjectionType = 0
  Template = -> Template005
  Views = -> [View005]
FEATURE [PartDesign::FeatureBase] BaseFeature001
  BaseFeature = -> Cut013
  Suppressed = false
FEATURE [Sketcher::SketchObject] Sketch106
  ArcFitTolerance = 1e-06
  AttachmentSupport = -> [BaseFeature001]
  ExternalGeometry = -> [BaseFeature001]
  FullyConstrained = true
  MakeInternals = false
  MapMode = 5
  Placement = pos=(-3e-16,-1.4e-15,3.2) rot=(0,0,1;0rad)
  sketch-geometry (20):
    g0: LineSegment StartX=47.75 StartY=95.85 StartZ=0 EndX=47.75 EndY=63.55 EndZ=0
    g1: LineSegment StartX=47.75 StartY=63.55 StartZ=0 EndX=80.05 EndY=63.55 EndZ=0
    g2: LineSegment StartX=80.05 StartY=63.55 StartZ=0 EndX=80.05 EndY=95.85 EndZ=0
    g3: LineSegment StartX=80.05 StartY=95.85 StartZ=0 EndX=47.75 EndY=95.85 EndZ=0
    g4: LineSegment StartX=23 StartY=112.8 StartZ=0 EndX=23 EndY=94.8 EndZ=0
    g5: LineSegment StartX=23 StartY=94.8 StartZ=0 EndX=41 EndY=94.8 EndZ=0
    g6: LineSegment StartX=41 StartY=94.8 StartZ=0 EndX=41 EndY=112.8 EndZ=0
    g7: LineSegment StartX=41 StartY=112.8 StartZ=0 EndX=23 EndY=112.8 EndZ=0
    g8: LineSegment [constr] StartX=23 StartY=112.8 StartZ=0 EndX=41 EndY=94.8 EndZ=0
    g9: LineSegment [constr] StartX=23 StartY=94.8 StartZ=0 EndX=41 EndY=112.8 EndZ=0
    g10: LineSegment StartX=23 StartY=80.8 StartZ=0 EndX=23 EndY=62.8 EndZ=0
    g11: LineSegment StartX=23 StartY=62.8 StartZ=0 EndX=41 EndY=62.8 EndZ=0
    g12: LineSegment StartX=41 StartY=62.8 StartZ=0 EndX=41 EndY=80.8 EndZ=0
    g13: LineSegment StartX=41 StartY=80.8 StartZ=0 EndX=23 EndY=80.8 EndZ=0
    g14: LineSegment [constr] StartX=23 StartY=80.8 StartZ=0 EndX=41 EndY=62.8 EndZ=0
    g15: LineSegment [constr] StartX=23 StartY=62.8 StartZ=0 EndX=41 EndY=80.8 EndZ=0
    g16: LineSegment StartX=23 StartY=48.8 StartZ=0 EndX=23 EndY=14.8 EndZ=0
    g17: LineSegment StartX=23 StartY=14.8 StartZ=0 EndX=41 EndY=14.8 EndZ=0
    g18: LineSegment StartX=41 StartY=14.8 StartZ=0 EndX=41 EndY=48.8 EndZ=0
    g19: LineSegment StartX=41 StartY=48.8 StartZ=0 EndX=23 EndY=48.8 EndZ=0
  constraints (56):
    c: Coincident(g0,g1)
    c: Coincident(g1,g2)
    c: Coincident(g2,g3)
    c: Coincident(g3,g0)
    c: Vertical(g0)
    c: Vertical(g2)
    c: Horizontal(g1)
    c: Horizontal(g3)
    c: DistanceX(g-4,g1) = 0.1
    c: DistanceY(g0,g-4) = 0.1
    c: DistanceX(g0,g-3) = 0.1
    c: DistanceY(g-3,g2) = 0.1
    c: Coincident(g4,g5)
    c: Coincident(g5,g6)
    c: Coincident(g6,g7)
    c: Coincident(g7,g4)
    c: Vertical(g4)
    c: Vertical(g6)
    c: Horizontal(g5)
    c: Horizontal(g7)
    c: Coincident(g8,g4)
    c: Coincident(g8,g5)
    c: Coincident(g9,g4)
    c: Coincident(g9,g6)
    c: PointOnObject(g-10,g8)
    c: PointOnObject(g-9,g8)
    c: PointOnObject(g-9,g9)
    c: DistanceX(g4,g-10) = 1
    c: Coincident(g10,g11)
    c: Coincident(g11,g12)
    c: Coincident(g12,g13)
    c: Coincident(g13,g10)
    c: Vertical(g10)
    c: Vertical(g12)
    c: Horizontal(g11)
    c: Horizontal(g13)
    c: Coincident(g14,g10)
    c: Coincident(g14,g11)
    c: Coincident(g15,g10)
    c: Coincident(g15,g12)
    c: PointOnObject(g-8,g14)
    c: PointOnObject(g-7,g14)
    c: PointOnObject(g-7,g15)
    c: DistanceX(g10,g-8) = 1
    c: Coincident(g16,g17)
    c: Coincident(g17,g18)
    c: Coincident(g18,g19)
    c: Coincident(g19,g16)
    c: Vertical(g16)
    c: Vertical(g18)
    c: Horizontal(g17)
    c: Horizontal(g19)
    c: DistanceX(g16,g-6) = 1
    c: DistanceY(g-6,g18) = 1
    c: DistanceX(g-5,g17) = 1
    c: DistanceY(g16,g-5) = 1
FEATURE [PartDesign::Pocket] Pocket024
  BaseFeature = -> BaseFeature001
  Direction = (0,0,-1)
  Length = 4
  Length2 = 5
  Profile = -> Sketch106
  ReferenceAxis = -> Sketch106 [N_Axis]
  Refine = true
  Suppressed = false
  Type = 0
FEATURE [Sketcher::SketchObject] Sketch107
  ArcFitTolerance = 1e-06
  AttachmentSupport = -> [Groove002]
  ExternalGeometry = -> [Groove002]
  FullyConstrained = true
  MakeInternals = false
  MapMode = 5
  Placement = pos=(52.25,56.15,-2.5) rot=(0.57735,0.57735,0.57735;2.0944rad)
  sketch-geometry (3):
    g0: LineSegment StartX=22.95 StartY=0.900005 StartZ=0 EndX=0.231255 EndY=-1.88587 EndZ=0
    g1: LineSegment StartX=22.95 StartY=0.900005 StartZ=0 EndX=1.67332 EndY=0.9 EndZ=0
    g2: LineSegment StartX=1.67332 StartY=0.9 StartZ=0 EndX=0.231255 EndY=-1.88587 EndZ=0
  constraints (6):
    c: Tangent(g0,g-3) = 1.5708
    c: Coincident(g0,g-5)
    c: Coincident(g1,g0)
    c: Coincident(g1,g-4)
    c: Coincident(g2,g1)
    c: Coincident(g2,g0)
FEATURE [PartDesign::Pad] Pad084
  BaseFeature = -> Groove002
  Direction = (1,2e-15,0)
  Length = 2
  Length2 = 10
  Placement = pos=(77.75,56.15,-2.5) rot=(0.57735,0.57735,0.57735;2.0944rad)
  Profile = -> Sketch107
  ReferenceAxis = -> Sketch107 [N_Axis]
  Refine = true
  Reversed = true
  Suppressed = false
  Type = 0
FEATURE [Sketcher::SketchObject] Sketch108
  ArcFitTolerance = 1e-06
  AttachmentSupport = -> [Pad084]
  ExternalGeometry = -> [Pad084]
  FullyConstrained = true
  MakeInternals = false
  MapMode = 5
  Placement = pos=(75.55,56.15,-2.5) rot=(0.57735,0.57735,-0.57735;4.18879rad)
  sketch-geometry (3):
    g0: LineSegment StartX=1.67332 StartY=-0.9 StartZ=0 EndX=22.95 EndY=-0.900005 EndZ=0
    g1: LineSegment StartX=22.95 StartY=-0.900005 StartZ=0 EndX=0.231255 EndY=1.88587 EndZ=0
    g2: LineSegment StartX=1.67332 StartY=-0.9 StartZ=0 EndX=0.231255 EndY=1.88587 EndZ=0
  constraints (6):
    c: Coincident(g0,g-4)
    c: Coincident(g0,g-5)
    c: Coincident(g1,g-5)
    c: Tangent(g1,g-3) = -1.5708
    c: Coincident(g2,g0)
    c: Coincident(g2,g1)
FEATURE [PartDesign::Pad] Pad085
  BaseFeature = -> Pad084
  Direction = (-1,-2.1e-15,1.2e-15)
  Length = 2
  Length2 = 10
  Placement = pos=(77.75,56.15,-2.5) rot=(0.57735,0.57735,0.57735;2.0944rad)
  Profile = -> Sketch108
  ReferenceAxis = -> Sketch108 [N_Axis]
  Refine = true
  Reversed = true
  Suppressed = false
  Type = 0
FEATURE [PartDesign::Body] Body020  label="SlotCover"
  AllowCompound = false
  Group = -> [Binder024,DatumPlane003,Sketch058,Pad038,Sketch059,Pad039,Sketch060,Pocket022,Sketch061,Pad040,Sketch062,Pocket023,Sphere004,Sphere005,Sketch063,Pad041,Sketch064,Pad042,DatumPlane004,Sketch065,Groove002,Sketch107,Pad084,Sketch108,Pad085]
  Origin = -> Origin290
  Tip = -> Pad085
FEATURE [PartDesign::FeatureBase] Clone003
  BaseFeature = -> Body020
  Placement = pos=(91.8,159.4,-1.94e-14) rot=(0,0,-1;3.14159rad)
  Suppressed = false
  expr: .Placement.Base.y = 158.8 mm + 0.6 mm
FEATURE [PartDesign::Body] Body021  label="SlotCover Clone"
  AllowCompound = false
  Group = -> [Clone003]
  Origin = -> Origin291
  Placement = pos=(36,0,0) rot=(0,0,1;0rad)
  Tip = -> Clone003
FEATURE [PartDesign::SubShapeBinder] Binder026
  BindCopyOnChange = 0
  BindMode = 0
  ClaimChildren = false
  Context = -> Part001 [Body001.Binder026.]
  Fuse = false
  MakeFace = true
  OffsetFill = false
  OffsetIntersection = false
  OffsetJoinType = 0
  OffsetOpenResult = false
  PartialLoad = false
  Refine = true
  Relative = true
  Support = -> [RetroConsoleMk2_1]
  _Version = 2
FEATURE [Sketcher::SketchObject] Sketch109
  ArcFitTolerance = 1e-06
  AttachmentSupport = -> [Pocket020]
  ExternalGeometry = -> [Binder026,Pocket020]
  FullyConstrained = true
  MakeInternals = false
  MapMode = 5
  Placement = pos=(0,0,-7) rot=(0,0,1;0rad)
  sketch-geometry (16):
    g0: LineSegment StartX=7.79999 StartY=33 StartZ=0 EndX=7.79999 EndY=25 EndZ=0
    g1: LineSegment StartX=7.79999 StartY=25 StartZ=0 EndX=8 EndY=25 EndZ=0
    g2: LineSegment StartX=8 StartY=25 StartZ=0 EndX=8 EndY=33 EndZ=0
    g3: LineSegment StartX=8 StartY=33 StartZ=0 EndX=7.79999 EndY=33 EndZ=0
    g4: LineSegment StartX=8 StartY=127.8 StartZ=0 EndX=8 EndY=134.4 EndZ=0
    g5: LineSegment StartX=8 StartY=134.4 StartZ=0 EndX=7.79999 EndY=134.4 EndZ=0
    g6: LineSegment StartX=7.79999 StartY=134.4 StartZ=0 EndX=7.79999 EndY=127.8 EndZ=0
    g7: LineSegment StartX=7.79999 StartY=127.8 StartZ=0 EndX=8 EndY=127.8 EndZ=0
    g8: LineSegment StartX=119.8 StartY=127.8 StartZ=0 EndX=120 EndY=127.8 EndZ=0
    g9: LineSegment StartX=120 StartY=127.8 StartZ=0 EndX=120 EndY=134.4 EndZ=0
    g10: LineSegment StartX=120 StartY=134.4 StartZ=0 EndX=119.8 EndY=134.4 EndZ=0
    g11: LineSegment StartX=119.8 StartY=134.4 StartZ=0 EndX=119.8 EndY=127.8 EndZ=0
    g12: LineSegment StartX=119.8 StartY=25 StartZ=0 EndX=120 EndY=25 EndZ=0
    g13: LineSegment StartX=120 StartY=25 StartZ=0 EndX=120 EndY=33 EndZ=0
    g14: LineSegment StartX=120 StartY=33 StartZ=0 EndX=119.8 EndY=33 EndZ=0
    g15: LineSegment StartX=119.8 StartY=33 StartZ=0 EndX=119.8 EndY=25 EndZ=0
  constraints (44):
    c: Coincident(g0,g1)
    c: Coincident(g1,g2)
    c: Coincident(g2,g3)
    c: Coincident(g3,g0)
    c: Vertical(g0)
    c: Vertical(g2)
    c: Horizontal(g1)
    c: Horizontal(g3)
    c: PointOnObject(g0,g-4)
    c: Coincident(g1,g-5)
    c: Distance(g0,g-3) = 0.4
    c: Coincident(g4,g5)
    c: Coincident(g5,g6)
    c: Coincident(g6,g7)
    c: Coincident(g7,g4)
    c: Vertical(g4)
    c: Vertical(g6)
    c: Horizontal(g5)
    c: Horizontal(g7)
    c: Coincident(g4,g-6)
    c: PointOnObject(g5,g-7)
    c: DistanceX(g5,g-3) = 0.4
    c: Coincident(g8,g9)
    c: Coincident(g9,g10)
    c: Coincident(g10,g11)
    c: Coincident(g11,g8)
    c: Horizontal(g8)
    c: Horizontal(g10)
    c: Vertical(g9)
    c: Vertical(g11)
    c: Coincident(g8,g-9)
    c: PointOnObject(g9,g-10)
    c: DistanceX(g-8,g9) = 0.4
    c: Coincident(g12,g13)
    c: Coincident(g13,g14)
    c: Coincident(g14,g15)
    c: Coincident(g15,g12)
    c: Horizontal(g12)
    c: Horizontal(g14)
    c: Vertical(g13)
    c: Vertical(g15)
    c: Coincident(g12,g-12)
    c: PointOnObject(g13,g-11)
    c: Distance(g12,g-8) = 0.4
FEATURE [PartDesign::Pocket] Pocket025
  BaseFeature = -> Pocket020
  Direction = (0,0,-1)
  Length = 25
  Length2 = 5
  Profile = -> Sketch109
  ReferenceAxis = -> Sketch109 [N_Axis]
  Refine = true
  Suppressed = false
  Type = 0
FEATURE [Sketcher::SketchObject] Sketch110
  ArcFitTolerance = 1e-06
  AttachmentSupport = -> [Pocket025]
  ExternalGeometry = -> [Pocket025,Binder026]
  FullyConstrained = true
  MakeInternals = false
  MapMode = 5
  Placement = pos=(0,-5.8e-15,-26.4) rot=(0,0,1;0rad)
  sketch-geometry (4):
    g0: LineSegment StartX=7.79999 StartY=134.4 StartZ=0 EndX=120 EndY=134.4 EndZ=0
    g1: LineSegment StartX=120 StartY=134.4 StartZ=0 EndX=120 EndY=134.6 EndZ=0
    g2: LineSegment StartX=120 StartY=134.6 StartZ=0 EndX=7.79999 EndY=134.6 EndZ=0
    g3: LineSegment StartX=7.79999 StartY=134.6 StartZ=0 EndX=7.79999 EndY=134.4 EndZ=0
  constraints (10):
    c: Coincident(g0,g1)
    c: Coincident(g1,g2)
    c: Coincident(g2,g3)
    c: Coincident(g3,g0)
    c: Horizontal(g2)
    c: Vertical(g1)
    c: Vertical(g3)
    c: Coincident(g0,g-3)
    c: Coincident(g0,g-3)
    c: DistanceY(g-4,g1) = 0.4
FEATURE [PartDesign::Pocket] Pocket026
  BaseFeature = -> Pocket025
  Direction = (0,0,-1)
  Length = 6
  Length2 = 5
  Profile = -> Sketch110
  ReferenceAxis = -> Sketch110 [N_Axis]
  Refine = true
  Suppressed = false
  Type = 0
FEATURE [PartDesign::Body] Body001  label="Base"
  AllowCompound = false
  Group = -> [Binder,Sketch002,Pad001,Sketch003,Pad002,Sketch004,Pad003,Sketch005,Pad004,Sketch034,Pad018,Sketch035,Pocket016,Binder020,Sketch044,Pocket017,Sketch045,Pocket018,Pad027,Sketch046,Pocket019,Pocket020,Binder026,Sketch109,Pocket025,Sketch110,Pocket026]
  Origin = -> Origin001
  Tip = -> Pocket026
FEATURE [Sketcher::SketchObject] Sketch111
  ArcFitTolerance = 1e-06
  AttachmentSupport = -> [Pocket006]
  ExternalGeometry = -> [Pocket006]
  FullyConstrained = true
  MakeInternals = false
  MapMode = 5
  Placement = pos=(0,0,-28.8) rot=(1,0,0;3.14159rad)
  sketch-geometry (4):
    g0: LineSegment StartX=119.8 StartY=16 StartZ=0 EndX=119.8 EndY=0 EndZ=0
    g1: LineSegment StartX=119.8 StartY=0 StartZ=0 EndX=120.8 EndY=0 EndZ=0
    g2: LineSegment StartX=120.8 StartY=0 StartZ=0 EndX=120.8 EndY=16 EndZ=0
    g3: LineSegment StartX=120.8 StartY=16 StartZ=0 EndX=119.8 EndY=16 EndZ=0
  constraints (11):
    c: Coincident(g0,g1)
    c: Coincident(g1,g2)
    c: Coincident(g2,g3)
    c: Coincident(g3,g0)
    c: Vertical(g0)
    c: Vertical(g2)
    c: Horizontal(g1)
    c: Horizontal(g3)
    c: Distance(g0,g2) = 1
    c: Coincident(g0,g-3)
    c: PointOnObject(g1,g-1)
FEATURE [PartDesign::Pocket] Pocket027
  BaseFeature = -> Pocket006
  Direction = (0,0,1)
  Length = 30
  Length2 = 5
  Profile = -> Sketch111
  ReferenceAxis = -> Sketch111 [N_Axis]
  Refine = true
  Suppressed = false
  Type = 0
FEATURE [Sketcher::SketchObject] Sketch112
  ArcFitTolerance = 1e-06
  AttachmentSupport = -> [Pocket012]
  ExternalGeometry = -> [Pocket012]
  FullyConstrained = true
  MakeInternals = false
  MapMode = 5
  Placement = pos=(0,0,-28.8) rot=(1,0,0;3.14159rad)
  sketch-geometry (4):
    g0: LineSegment StartX=8 StartY=16 StartZ=0 EndX=7 EndY=16 EndZ=0
    g1: LineSegment StartX=7 StartY=16 StartZ=0 EndX=7 EndY=0 EndZ=0
    g2: LineSegment StartX=7 StartY=0 StartZ=0 EndX=8 EndY=0 EndZ=0
    g3: LineSegment StartX=8 StartY=0 StartZ=0 EndX=8 EndY=16 EndZ=0
  constraints (11):
    c: Coincident(g0,g1)
    c: Coincident(g1,g2)
    c: Coincident(g2,g3)
    c: Coincident(g3,g0)
    c: Horizontal(g0)
    c: Horizontal(g2)
    c: Vertical(g1)
    c: Vertical(g3)
    c: Distance(g1,g3) = 1
    c: Coincident(g0,g-3)
    c: PointOnObject(g1,g-1)
FEATURE [PartDesign::Pocket] Pocket028
  BaseFeature = -> Pocket012
  Direction = (0,0,1)
  Length = 30
  Length2 = 5
  Profile = -> Sketch112
  ReferenceAxis = -> Sketch112 [N_Axis]
  Refine = true
  Suppressed = false
  Type = 0
FEATURE [Sketcher::SketchObject] Sketch113
  ArcFitTolerance = 1e-06
  AttachmentSupport = -> [Pocket013]
  ExternalGeometry = -> [Pocket013]
  FullyConstrained = true
  MakeInternals = false
  MapMode = 5
  Placement = pos=(0,0,-28.8) rot=(1,0,0;3.14159rad)
  sketch-geometry (8):
    g0: LineSegment StartX=24 StartY=16 StartZ=0 EndX=24 EndY=0 EndZ=0
    g1: LineSegment StartX=24 StartY=0 StartZ=0 EndX=25 EndY=0 EndZ=0
    g2: LineSegment StartX=25 StartY=0 StartZ=0 EndX=25 EndY=16 EndZ=0
    g3: LineSegment StartX=25 StartY=16 StartZ=0 EndX=24 EndY=16 EndZ=0
    g4: LineSegment StartX=40 StartY=16 StartZ=0 EndX=39 EndY=16 EndZ=0
    g5: LineSegment StartX=39 StartY=16 StartZ=0 EndX=39 EndY=0 EndZ=0
    g6: LineSegment StartX=39 StartY=0 StartZ=0 EndX=40 EndY=0 EndZ=0
    g7: LineSegment StartX=40 StartY=0 StartZ=0 EndX=40 EndY=16 EndZ=0
  constraints (22):
    c: Coincident(g0,g1)
    c: Coincident(g1,g2)
    c: Coincident(g2,g3)
    c: Coincident(g3,g0)
    c: Vertical(g0)
    c: Vertical(g2)
    c: Horizontal(g1)
    c: Horizontal(g3)
    c: Distance(g0,g2) = 1
    c: Coincident(g0,g-3)
    c: PointOnObject(g1,g-1)
    c: Coincident(g4,g5)
    c: Coincident(g5,g6)
    c: Coincident(g6,g7)
    c: Coincident(g7,g4)
    c: Horizontal(g4)
    c: Horizontal(g6)
    c: Vertical(g5)
    c: Vertical(g7)
    c: Distance(g5,g7) = 1
    c: Coincident(g4,g-4)
    c: PointOnObject(g5,g-1)
FEATURE [PartDesign::Pocket] Pocket029
  BaseFeature = -> Pocket013
  Direction = (0,0,1)
  Length = 30
  Length2 = 5
  Profile = -> Sketch113
  ReferenceAxis = -> Sketch113 [N_Axis]
  Refine = true
  Suppressed = false
  Type = 0
FEATURE [Sketcher::SketchObject] Sketch114
  ArcFitTolerance = 1e-06
  AttachmentSupport = -> [Pocket014]
  ExternalGeometry = -> [Pocket014]
  FullyConstrained = true
  MakeInternals = false
  MapMode = 5
  Placement = pos=(0,0,-28.8) rot=(1,0,0;3.14159rad)
  sketch-geometry (8):
    g0: LineSegment StartX=56 StartY=16 StartZ=0 EndX=56 EndY=0 EndZ=0
    g1: LineSegment StartX=56 StartY=0 StartZ=0 EndX=57 EndY=0 EndZ=0
    g2: LineSegment StartX=57 StartY=0 StartZ=0 EndX=57 EndY=16 EndZ=0
    g3: LineSegment StartX=57 StartY=16 StartZ=0 EndX=56 EndY=16 EndZ=0
    g4: LineSegment StartX=72 StartY=16 StartZ=0 EndX=71 EndY=16 EndZ=0
    g5: LineSegment StartX=71 StartY=16 StartZ=0 EndX=71 EndY=0 EndZ=0
    g6: LineSegment StartX=71 StartY=0 StartZ=0 EndX=72 EndY=0 EndZ=0
    g7: LineSegment StartX=72 StartY=0 StartZ=0 EndX=72 EndY=16 EndZ=0
  constraints (22):
    c: Coincident(g0,g1)
    c: Coincident(g1,g2)
    c: Coincident(g2,g3)
    c: Coincident(g3,g0)
    c: Vertical(g0)
    c: Vertical(g2)
    c: Horizontal(g1)
    c: Horizontal(g3)
    c: Distance(g0,g2) = 1
    c: Coincident(g0,g-3)
    c: PointOnObject(g1,g-1)
    c: Coincident(g4,g5)
    c: Coincident(g5,g6)
    c: Coincident(g6,g7)
    c: Coincident(g7,g4)
    c: Horizontal(g4)
    c: Horizontal(g6)
    c: Vertical(g5)
    c: Vertical(g7)
    c: Distance(g5,g7) = 1
    c: Coincident(g4,g-4)
    c: PointOnObject(g5,g-1)
FEATURE [PartDesign::Pocket] Pocket030
  BaseFeature = -> Pocket014
  Direction = (0,0,1)
  Length = 30
  Length2 = 5
  Profile = -> Sketch114
  ReferenceAxis = -> Sketch114 [N_Axis]
  Refine = true
  Suppressed = false
  Type = 0
FEATURE [Sketcher::SketchObject] Sketch115
  ArcFitTolerance = 1e-06
  AttachmentSupport = -> [Pocket015]
  ExternalGeometry = -> [Pocket015]
  FullyConstrained = true
  MakeInternals = false
  MapMode = 5
  Placement = pos=(0,0,-28.8) rot=(1,0,0;3.14159rad)
  sketch-geometry (8):
    g0: LineSegment StartX=104 StartY=16 StartZ=0 EndX=103 EndY=16 EndZ=0
    g1: LineSegment StartX=103 StartY=16 StartZ=0 EndX=103 EndY=0 EndZ=0
    g2: LineSegment StartX=103 StartY=0 StartZ=0 EndX=104 EndY=0 EndZ=0
    g3: LineSegment StartX=104 StartY=0 StartZ=0 EndX=104 EndY=16 EndZ=0
    g4: LineSegment StartX=88 StartY=16 StartZ=0 EndX=88 EndY=0 EndZ=0
    g5: LineSegment StartX=88 StartY=0 StartZ=0 EndX=89 EndY=0 EndZ=0
    g6: LineSegment StartX=89 StartY=0 StartZ=0 EndX=89 EndY=16 EndZ=0
    g7: LineSegment StartX=89 StartY=16 StartZ=0 EndX=88 EndY=16 EndZ=0
  constraints (22):
    c: Coincident(g0,g1)
    c: Coincident(g1,g2)
    c: Coincident(g2,g3)
    c: Coincident(g3,g0)
    c: Horizontal(g0)
    c: Horizontal(g2)
    c: Vertical(g1)
    c: Vertical(g3)
    c: Distance(g1,g3) = 1
    c: Coincident(g0,g-4)
    c: PointOnObject(g1,g-1)
    c: Coincident(g4,g5)
    c: Coincident(g5,g6)
    c: Coincident(g6,g7)
    c: Coincident(g7,g4)
    c: Vertical(g4)
    c: Vertical(g6)
    c: Horizontal(g5)
    c: Horizontal(g7)
    c: Distance(g4,g6) = 1
    c: Coincident(g4,g-3)
    c: PointOnObject(g5,g-1)
FEATURE [PartDesign::Pocket] Pocket031
  BaseFeature = -> Pocket015
  Direction = (0,0,1)
  Length = 30
  Length2 = 5
  Profile = -> Sketch115
  ReferenceAxis = -> Sketch115 [N_Axis]
  Refine = true
  Suppressed = false
  Type = 0
FEATURE [PartDesign::FeatureBase] BaseFeature002
  BaseFeature = -> Cut004
  Suppressed = false
FEATURE [PartDesign::Pad] Pad086
  BaseFeature = -> BaseFeature002
  Direction = (0,0,-1)
  Length = 1.4
  Length2 = 10
  Profile = -> BaseFeature002 [Face140]
  Refine = true
  Suppressed = false
  Type = 0
FEATURE [PartDesign::Pad] Pad087
  BaseFeature = -> Pad086
  Direction = (0,0,-1)
  Length = 1.4
  Length2 = 10
  Profile = -> Pad086 [Face97]
  Refine = true
  Suppressed = false
  Type = 0
FEATURE [Sketcher::SketchObject] Sketch116
  ArcFitTolerance = 1e-06
  AttachmentSupport = -> [Pad087]
  ExternalGeometry = -> [Pad087]
  FullyConstrained = true
  MakeInternals = false
  MapMode = 5
  Placement = pos=(0,0,-0.00178905) rot=(1,0,0;3.14159rad)
  sketch-geometry (8):
    g0: LineSegment StartX=25.9 StartY=-17.7 StartZ=0 EndX=25.9 EndY=-45.9 EndZ=0
    g1: LineSegment StartX=25.9 StartY=-45.9 StartZ=0 EndX=38.1 EndY=-45.9 EndZ=0
    g2: LineSegment StartX=38.1 StartY=-45.9 StartZ=0 EndX=38.1 EndY=-17.7 EndZ=0
    g3: LineSegment StartX=38.1 StartY=-17.7 StartZ=0 EndX=25.9 EndY=-17.7 EndZ=0
    g4: LineSegment StartX=25.4 StartY=-17.2 StartZ=0 EndX=25.4 EndY=-46.4 EndZ=0
    g5: LineSegment StartX=25.4 StartY=-46.4 StartZ=0 EndX=38.6 EndY=-46.4 EndZ=0
    g6: LineSegment StartX=38.6 StartY=-46.4 StartZ=0 EndX=38.6 EndY=-17.2 EndZ=0
    g7: LineSegment StartX=38.6 StartY=-17.2 StartZ=0 EndX=25.4 EndY=-17.2 EndZ=0
  constraints (22):
    c: Coincident(g0,g1)
    c: Coincident(g1,g2)
    c: Coincident(g2,g3)
    c: Coincident(g3,g0)
    c: Vertical(g0)
    c: Vertical(g2)
    c: Horizontal(g1)
    c: Horizontal(g3)
    c: Coincident(g0,g-3)
    c: Coincident(g1,g-4)
    c: Coincident(g4,g5)
    c: Coincident(g5,g6)
    c: Coincident(g6,g7)
    c: Coincident(g7,g4)
    c: Vertical(g4)
    c: Vertical(g6)
    c: Horizontal(g5)
    c: Horizontal(g7)
    c: DistanceX(g4,g0) = 0.5
    c: DistanceY(g2,g6) = 0.5
    c: DistanceX(g1,g5) = 0.5
    c: DistanceY(g4,g0) = 0.5
FEATURE [PartDesign::Pocket] Pocket032
  BaseFeature = -> Pad087
  Direction = (0,0,1)
  Length = 5.4
  Length2 = 5
  Profile = -> Sketch116
  ReferenceAxis = -> Sketch116 [N_Axis]
  Refine = true
  Suppressed = false
  Type = 0
FEATURE [PartDesign::SubShapeBinder] Binder027
  BindCopyOnChange = 0
  BindMode = 0
  ClaimChildren = false
  Context = -> Body064 [Binder027.]
  Fuse = false
  MakeFace = true
  OffsetFill = false
  OffsetIntersection = false
  OffsetJoinType = 0
  OffsetOpenResult = false
  PartialLoad = false
  Refine = true
  Relative = true
  Support = -> [Body063]
  _Version = 2
FEATURE [Sketcher::SketchObject] Sketch117
  ArcFitTolerance = 1e-06
  AttachmentSupport = -> [Binder027]
  ExternalGeometry = -> [Binder027]
  FullyConstrained = true
  MakeInternals = false
  MapMode = 5
  Placement = pos=(0,0,-0.00178905) rot=(1,0,0;3.14159rad)
  sketch-geometry (8):
    g0: LineSegment StartX=26.1 StartY=-17.9 StartZ=0 EndX=26.1 EndY=-45.7 EndZ=0
    g1: LineSegment StartX=26.1 StartY=-45.7 StartZ=0 EndX=37.9 EndY=-45.7 EndZ=0
    g2: LineSegment StartX=37.9 StartY=-45.7 StartZ=0 EndX=37.9 EndY=-17.9 EndZ=0
    g3: LineSegment StartX=37.9 StartY=-17.9 StartZ=0 EndX=26.1 EndY=-17.9 EndZ=0
    g4: LineSegment StartX=22.5 StartY=-14.3 StartZ=0 EndX=22.5 EndY=-48.8 EndZ=0
    g5: LineSegment StartX=22.5 StartY=-48.8 StartZ=0 EndX=41.5 EndY=-48.8 EndZ=0
    g6: LineSegment StartX=41.5 StartY=-48.8 StartZ=0 EndX=41.5 EndY=-14.3 EndZ=0
    g7: LineSegment StartX=41.5 StartY=-14.3 StartZ=0 EndX=22.5 EndY=-14.3 EndZ=0
  constraints (24):
    c: Coincident(g0,g1)
    c: Coincident(g1,g2)
    c: Coincident(g2,g3)
    c: Coincident(g3,g0)
    c: Vertical(g0)
    c: Vertical(g2)
    c: Horizontal(g1)
    c: Horizontal(g3)
    c: DistanceY(g0,g-3) = 0.7
    c: DistanceX(g2,g-3) = 0.7
    c: DistanceY(g-4,g1) = 0.7
    c: DistanceX(g-4,g0) = 0.7
    c: Coincident(g4,g5)
    c: Coincident(g5,g6)
    c: Coincident(g6,g7)
    c: Coincident(g7,g4)
    c: Vertical(g4)
    c: Vertical(g6)
    c: Horizontal(g5)
    c: Horizontal(g7)
    c: DistanceY(g-5,g4) = 2
    c: DistanceX(g-5,g6) = 2
    c: DistanceY(g5,g-6) = 1.5
    c: DistanceX(g4,g-6) = 2
FEATURE [PartDesign::Pad] Pad088
  Direction = (0,0,-1)
  Length = 0.2
  Length2 = 10
  Profile = -> Sketch117
  ReferenceAxis = -> Sketch117 [N_Axis]
  Refine = true
  Suppressed = false
  Type = 0
FEATURE [Sketcher::SketchObject] Sketch118
  ArcFitTolerance = 1e-06
  AttachmentSupport = -> [Pad088]
  ExternalGeometry = -> [Pad088]
  FullyConstrained = true
  MakeInternals = false
  MapMode = 5
  Placement = pos=(0,0,-0.00178905) rot=(0,0,1;0rad)
  sketch-geometry (8):
    g0: LineSegment StartX=26.1 StartY=45.7 StartZ=0 EndX=26.1 EndY=17.9 EndZ=0
    g1: LineSegment StartX=26.1 StartY=17.9 StartZ=0 EndX=37.9 EndY=17.9 EndZ=0
    g2: LineSegment StartX=37.9 StartY=17.9 StartZ=0 EndX=37.9 EndY=45.7 EndZ=0
    g3: LineSegment StartX=37.9 StartY=45.7 StartZ=0 EndX=26.1 EndY=45.7 EndZ=0
    g4: LineSegment StartX=25.6 StartY=46.2 StartZ=0 EndX=25.6 EndY=17.4 EndZ=0
    g5: LineSegment StartX=25.6 StartY=17.4 StartZ=0 EndX=38.4 EndY=17.4 EndZ=0
    g6: LineSegment StartX=38.4 StartY=17.4 StartZ=0 EndX=38.4 EndY=46.2 EndZ=0
    g7: LineSegment StartX=38.4 StartY=46.2 StartZ=0 EndX=25.6 EndY=46.2 EndZ=0
  constraints (22):
    c: Coincident(g0,g1)
    c: Coincident(g1,g2)
    c: Coincident(g2,g3)
    c: Coincident(g3,g0)
    c: Vertical(g0)
    c: Vertical(g2)
    c: Horizontal(g1)
    c: Horizontal(g3)
    c: Coincident(g0,g-3)
    c: Coincident(g1,g-4)
    c: Coincident(g4,g5)
    c: Coincident(g5,g6)
    c: Coincident(g6,g7)
    c: Coincident(g7,g4)
    c: Vertical(g4)
    c: Vertical(g6)
    c: Horizontal(g5)
    c: Horizontal(g7)
    c: DistanceX(g4,g0) = 0.5
    c: DistanceY(g2,g6) = 0.5
    c: DistanceX(g1,g5) = 0.5
    c: DistanceY(g4,g0) = 0.5
FEATURE [PartDesign::Pad] Pad089
  BaseFeature = -> Pad088
  Direction = (0,0,1)
  Length = 5
  Length2 = 10
  Profile = -> Sketch118
  ReferenceAxis = -> Sketch118 [N_Axis]
  Refine = true
  Suppressed = false
  Type = 0
FEATURE [PartDesign::Body] Body064  label="Quit Button fat Border"
  AllowCompound = false
  Group = -> [Binder027,Sketch117,Pad088,Sketch118,Pad089]
  Origin = -> Origin338
  Tip = -> Pad089
FEATURE [PartDesign::FeatureBase] BaseFeature003
  BaseFeature = -> Cut003
  Suppressed = false
FEATURE [PartDesign::Pad] Pad090
  BaseFeature = -> BaseFeature003
  Direction = (0,0,-1)
  Length = 1.4
  Length2 = 10
  Profile = -> BaseFeature003 [Face77]
  Refine = true
  Suppressed = false
  Type = 0
FEATURE [PartDesign::Pad] Pad091
  BaseFeature = -> Pad090
  Direction = (0,0,-1)
  Length = 1.4
  Length2 = 10
  Profile = -> Pad090 [Face59]
  Refine = true
  Suppressed = false
  Type = 0
FEATURE [Sketcher::SketchObject] Sketch119
  ArcFitTolerance = 1e-06
  AttachmentSupport = -> [Pad091]
  ExternalGeometry = -> [Pad091]
  FullyConstrained = true
  MakeInternals = false
  MapMode = 5
  Placement = pos=(0,0,-0.00178905) rot=(1,0,0;3.14159rad)
  sketch-geometry (8):
    g0: LineSegment StartX=25.9 StartY=-65.7 StartZ=0 EndX=25.9 EndY=-77.9 EndZ=0
    g1: LineSegment StartX=25.9 StartY=-77.9 StartZ=0 EndX=38.1 EndY=-77.9 EndZ=0
    g2: LineSegment StartX=38.1 StartY=-77.9 StartZ=0 EndX=38.1 EndY=-65.7 EndZ=0
    g3: LineSegment StartX=38.1 StartY=-65.7 StartZ=0 EndX=25.9 EndY=-65.7 EndZ=0
    g4: LineSegment StartX=25.4 StartY=-65.2 StartZ=0 EndX=25.4 EndY=-78.4 EndZ=0
    g5: LineSegment StartX=25.4 StartY=-78.4 StartZ=0 EndX=38.6 EndY=-78.4 EndZ=0
    g6: LineSegment StartX=38.6 StartY=-78.4 StartZ=0 EndX=38.6 EndY=-65.2 EndZ=0
    g7: LineSegment StartX=38.6 StartY=-65.2 StartZ=0 EndX=25.4 EndY=-65.2 EndZ=0
  constraints (22):
    c: Coincident(g0,g1)
    c: Coincident(g1,g2)
    c: Coincident(g2,g3)
    c: Coincident(g3,g0)
    c: Vertical(g0)
    c: Vertical(g2)
    c: Horizontal(g1)
    c: Horizontal(g3)
    c: Coincident(g0,g-3)
    c: Coincident(g1,g-4)
    c: Coincident(g4,g5)
    c: Coincident(g5,g6)
    c: Coincident(g6,g7)
    c: Coincident(g7,g4)
    c: Vertical(g4)
    c: Vertical(g6)
    c: Horizontal(g5)
    c: Horizontal(g7)
    c: DistanceY(g0,g4) = 0.5
    c: DistanceX(g2,g6) = 0.5
    c: DistanceY(g5,g1) = 0.5
    c: DistanceX(g4,g0) = 0.5
FEATURE [PartDesign::Pocket] Pocket033
  BaseFeature = -> Pad091
  Direction = (0,0,1)
  Length = 5.4
  Length2 = 5
  Profile = -> Sketch119
  ReferenceAxis = -> Sketch119 [N_Axis]
  Refine = true
  Suppressed = false
  Type = 0
FEATURE [PartDesign::Body] Body065  label="Reset Button fat revised"
  AllowCompound = false
  BaseFeature = -> Cut003
  Group = -> [BaseFeature003,Pad090,Pad091,Sketch119,Pocket033]
  Origin = -> Origin339
  Tip = -> Pocket033
FEATURE [PartDesign::SubShapeBinder] Binder028
  BindCopyOnChange = 0
  BindMode = 0
  ClaimChildren = false
  Context = -> Body066 [Binder028.]
  Fuse = false
  MakeFace = true
  OffsetFill = false
  OffsetIntersection = false
  OffsetJoinType = 0
  OffsetOpenResult = false
  PartialLoad = false
  Refine = true
  Relative = true
  Support = -> [Body065]
  _Version = 2
FEATURE [Sketcher::SketchObject] Sketch120
  ArcFitTolerance = 1e-06
  AttachmentSupport = -> [Binder028]
  ExternalGeometry = -> [Binder028]
  FullyConstrained = true
  MakeInternals = false
  MapMode = 5
  Placement = pos=(0,0,-0.00178905) rot=(1,0,0;3.14159rad)
  sketch-geometry (8):
    g0: LineSegment StartX=26 StartY=-65.8 StartZ=0 EndX=26 EndY=-77.8 EndZ=0
    g1: LineSegment StartX=26 StartY=-77.8 StartZ=0 EndX=38 EndY=-77.8 EndZ=0
    g2: LineSegment StartX=38 StartY=-77.8 StartZ=0 EndX=38 EndY=-65.8 EndZ=0
    g3: LineSegment StartX=38 StartY=-65.8 StartZ=0 EndX=26 EndY=-65.8 EndZ=0
    g4: LineSegment StartX=22.5 StartY=-62.3 StartZ=0 EndX=22.5 EndY=-81.3 EndZ=0
    g5: LineSegment StartX=22.5 StartY=-81.3 StartZ=0 EndX=41.5 EndY=-81.3 EndZ=0
    g6: LineSegment StartX=41.5 StartY=-81.3 StartZ=0 EndX=41.5 EndY=-62.3 EndZ=0
    g7: LineSegment StartX=41.5 StartY=-62.3 StartZ=0 EndX=22.5 EndY=-62.3 EndZ=0
  constraints (24):
    c: Coincident(g0,g1)
    c: Coincident(g1,g2)
    c: Coincident(g2,g3)
    c: Coincident(g3,g0)
    c: Vertical(g0)
    c: Vertical(g2)
    c: Horizontal(g1)
    c: Horizontal(g3)
    c: Coincident(g4,g5)
    c: Coincident(g5,g6)
    c: Coincident(g6,g7)
    c: Coincident(g7,g4)
    c: Vertical(g4)
    c: Vertical(g6)
    c: Horizontal(g5)
    c: Horizontal(g7)
    c: DistanceY(g-5,g4) = 2
    c: DistanceX(g-5,g6) = 2
    c: DistanceY(g5,g-6) = 2
    c: DistanceX(g4,g-6) = 2
    c: DistanceY(g0,g-3) = 0.6
    c: DistanceX(g2,g-3) = 0.6
    c: DistanceY(g-4,g1) = 0.6
    c: DistanceX(g-4,g0) = 0.6
FEATURE [PartDesign::Pad] Pad092
  Direction = (0,0,-1)
  Length = 0.2
  Length2 = 10
  Profile = -> Sketch120
  ReferenceAxis = -> Sketch120 [N_Axis]
  Refine = true
  Suppressed = false
  Type = 0
FEATURE [Sketcher::SketchObject] Sketch121
  ArcFitTolerance = 1e-06
  AttachmentSupport = -> [Pad092]
  ExternalGeometry = -> [Pad092]
  FullyConstrained = true
  MakeInternals = false
  MapMode = 5
  Placement = pos=(0,0,-0.00178905) rot=(0,0,1;0rad)
  sketch-geometry (8):
    g0: LineSegment StartX=26 StartY=77.8 StartZ=0 EndX=26 EndY=65.8 EndZ=0
    g1: LineSegment StartX=26 StartY=65.8 StartZ=0 EndX=38 EndY=65.8 EndZ=0
    g2: LineSegment StartX=38 StartY=65.8 StartZ=0 EndX=38 EndY=77.8 EndZ=0
    g3: LineSegment StartX=38 StartY=77.8 StartZ=0 EndX=26 EndY=77.8 EndZ=0
    g4: LineSegment StartX=25.5 StartY=78.3 StartZ=0 EndX=25.5 EndY=65.3 EndZ=0
    g5: LineSegment StartX=25.5 StartY=65.3 StartZ=0 EndX=38.5 EndY=65.3 EndZ=0
    g6: LineSegment StartX=38.5 StartY=65.3 StartZ=0 EndX=38.5 EndY=78.3 EndZ=0
    g7: LineSegment StartX=38.5 StartY=78.3 StartZ=0 EndX=25.5 EndY=78.3 EndZ=0
  constraints (22):
    c: Coincident(g0,g1)
    c: Coincident(g1,g2)
    c: Coincident(g2,g3)
    c: Coincident(g3,g0)
    c: Vertical(g0)
    c: Vertical(g2)
    c: Horizontal(g1)
    c: Horizontal(g3)
    c: Coincident(g0,g-3)
    c: Coincident(g1,g-4)
    c: Coincident(g4,g5)
    c: Coincident(g5,g6)
    c: Coincident(g6,g7)
    c: Coincident(g7,g4)
    c: Vertical(g4)
    c: Vertical(g6)
    c: Horizontal(g5)
    c: Horizontal(g7)
    c: DistanceY(g0,g4) = 0.5
    c: DistanceX(g2,g6) = 0.5
    c: DistanceY(g5,g1) = 0.5
    c: DistanceX(g4,g0) = 0.5
FEATURE [PartDesign::Pad] Pad093
  BaseFeature = -> Pad092
  Direction = (0,0,1)
  Length = 5
  Length2 = 10
  Profile = -> Sketch121
  ReferenceAxis = -> Sketch121 [N_Axis]
  Refine = true
  Suppressed = false
  Type = 0
FEATURE [PartDesign::Body] Body066  label="Reset Button fat Border"
  AllowCompound = false
  Group = -> [Binder028,Sketch120,Pad092,Sketch121,Pad093]
  Origin = -> Origin340
  Tip = -> Pad093
FEATURE [PartDesign::FeatureBase] BaseFeature004
  BaseFeature = -> Cut
  Suppressed = false
FEATURE [PartDesign::Pad] Pad094
  BaseFeature = -> BaseFeature004
  Direction = (0,0,-1)
  Length = 1.4
  Length2 = 10
  Profile = -> BaseFeature004 [Face68]
  Refine = true
  Suppressed = false
  Type = 0
FEATURE [PartDesign::Pad] Pad095
  BaseFeature = -> Pad094
  Direction = (0,0,-1)
  Length = 1.4
  Length2 = 10
  Profile = -> Pad094 [Face18]
  Refine = true
  Suppressed = false
  Type = 0
FEATURE [Sketcher::SketchObject] Sketch122
  ArcFitTolerance = 1e-06
  AttachmentSupport = -> [Pad095]
  ExternalGeometry = -> [Pad095]
  FullyConstrained = true
  MakeInternals = false
  MapMode = 5
  Placement = pos=(0,0,-0.00178905) rot=(1,0,0;3.14159rad)
  sketch-geometry (12):
    g0: LineSegment StartX=25.9 StartY=-97.7 StartZ=0 EndX=25.9 EndY=-109.9 EndZ=0
    g1: LineSegment StartX=25.9 StartY=-109.9 StartZ=0 EndX=38.1 EndY=-109.9 EndZ=0
    g2: LineSegment StartX=38.1 StartY=-109.9 StartZ=0 EndX=38.1 EndY=-97.7 EndZ=0
    g3: LineSegment StartX=38.1 StartY=-97.7 StartZ=0 EndX=25.9 EndY=-97.7 EndZ=0
    g4: LineSegment StartX=25.4 StartY=-97.2 StartZ=0 EndX=25.4 EndY=-110.4 EndZ=0
    g5: LineSegment StartX=25.4 StartY=-110.4 StartZ=0 EndX=38.6 EndY=-110.4 EndZ=0
    g6: LineSegment StartX=38.6 StartY=-110.4 StartZ=0 EndX=38.6 EndY=-97.2 EndZ=0
    g7: LineSegment StartX=38.6 StartY=-97.2 StartZ=0 EndX=25.4 EndY=-97.2 EndZ=0
    g8: LineSegment [constr] StartX=25.9 StartY=-97.7 StartZ=0 EndX=25.4 EndY=-97.2 EndZ=0
    g9: LineSegment [constr] StartX=25.9 StartY=-109.9 StartZ=0 EndX=25.4 EndY=-110.4 EndZ=0
    g10: LineSegment [constr] StartX=38.1 StartY=-109.9 StartZ=0 EndX=38.6 EndY=-110.4 EndZ=0
    g11: LineSegment [constr] StartX=38.1 StartY=-97.7 StartZ=0 EndX=38.6 EndY=-97.2 EndZ=0
  constraints (30):
    c: Coincident(g0,g1)
    c: Coincident(g1,g2)
    c: Coincident(g2,g3)
    c: Coincident(g3,g0)
    c: Vertical(g0)
    c: Vertical(g2)
    c: Horizontal(g1)
    c: Horizontal(g3)
    c: Coincident(g4,g5)
    c: Coincident(g5,g6)
    c: Coincident(g6,g7)
    c: Coincident(g7,g4)
    c: Vertical(g4)
    c: Vertical(g6)
    c: Horizontal(g5)
    c: Horizontal(g7)
    c: Coincident(g8,g0)
    c: Coincident(g8,g4)
    c: Coincident(g9,g1)
    c: Coincident(g9,g5)
    c: Coincident(g10,g2)
    c: Coincident(g10,g6)
    c: Coincident(g11,g3)
    c: Coincident(g11,g7)
    c: Perpendicular(g8,g9)
    c: Perpendicular(g9,g10)
    c: Perpendicular(g10,g11)
    c: Distance(g4,g0) = 0.5
    c: Coincident(g0,g-3)
    c: Coincident(g1,g-4)
FEATURE [PartDesign::Pocket] Pocket034
  BaseFeature = -> Pad095
  Direction = (0,0,1)
  Length = 5.4
  Length2 = 5
  Profile = -> Sketch122
  ReferenceAxis = -> Sketch122 [N_Axis]
  Refine = true
  Suppressed = false
  Type = 0
FEATURE [PartDesign::Body] Body067  label="Shutdown Button revised"
  AllowCompound = false
  BaseFeature = -> Cut
  Group = -> [BaseFeature004,Pad094,Pad095,Sketch122,Pocket034]
  Origin = -> Origin341
  Tip = -> Pocket034
FEATURE [PartDesign::SubShapeBinder] Binder029
  BindCopyOnChange = 0
  BindMode = 0
  ClaimChildren = false
  Context = -> Body068 [Binder029.]
  Fuse = false
  MakeFace = true
  OffsetFill = false
  OffsetIntersection = false
  OffsetJoinType = 0
  OffsetOpenResult = false
  PartialLoad = false
  Refine = true
  Relative = true
  Support = -> [Body067]
  _Version = 2
FEATURE [Sketcher::SketchObject] Sketch123
  ArcFitTolerance = 1e-06
  AttachmentSupport = -> [Binder029]
  ExternalGeometry = -> [Binder029]
  FullyConstrained = true
  MakeInternals = false
  MapMode = 5
  Placement = pos=(0,0,-0.00178905) rot=(1,0,0;3.14159rad)
  sketch-geometry (12):
    g0: LineSegment StartX=26 StartY=-97.8 StartZ=0 EndX=26 EndY=-109.8 EndZ=0
    g1: LineSegment StartX=26 StartY=-109.8 StartZ=0 EndX=38 EndY=-109.8 EndZ=0
    g2: LineSegment StartX=38 StartY=-109.8 StartZ=0 EndX=38 EndY=-97.8 EndZ=0
    g3: LineSegment StartX=38 StartY=-97.8 StartZ=0 EndX=26 EndY=-97.8 EndZ=0
    g4: LineSegment StartX=22.5 StartY=-94.3 StartZ=0 EndX=22.5 EndY=-113.3 EndZ=0
    g5: LineSegment StartX=22.5 StartY=-113.3 StartZ=0 EndX=41.5 EndY=-113.3 EndZ=0
    g6: LineSegment StartX=41.5 StartY=-113.3 StartZ=0 EndX=41.5 EndY=-94.3 EndZ=0
    g7: LineSegment StartX=41.5 StartY=-94.3 StartZ=0 EndX=22.5 EndY=-94.3 EndZ=0
    g8: LineSegment [constr] StartX=26 StartY=-97.8 StartZ=0 EndX=22.5 EndY=-94.3 EndZ=0
    g9: LineSegment [constr] StartX=26 StartY=-109.8 StartZ=0 EndX=22.5 EndY=-113.3 EndZ=0
    g10: LineSegment [constr] StartX=38 StartY=-109.8 StartZ=0 EndX=41.5 EndY=-113.3 EndZ=0
    g11: LineSegment [constr] StartX=38 StartY=-97.8 StartZ=0 EndX=41.5 EndY=-94.3 EndZ=0
  constraints (32):
    c: Coincident(g0,g1)
    c: Coincident(g1,g2)
    c: Coincident(g2,g3)
    c: Coincident(g3,g0)
    c: Vertical(g0)
    c: Vertical(g2)
    c: Horizontal(g1)
    c: Horizontal(g3)
    c: Coincident(g4,g5)
    c: Coincident(g5,g6)
    c: Coincident(g6,g7)
    c: Coincident(g7,g4)
    c: Vertical(g4)
    c: Vertical(g6)
    c: Horizontal(g5)
    c: Horizontal(g7)
    c: Coincident(g8,g0)
    c: Coincident(g8,g4)
    c: Coincident(g9,g1)
    c: Coincident(g9,g5)
    c: Coincident(g10,g2)
    c: Coincident(g10,g6)
    c: Coincident(g11,g3)
    c: Coincident(g11,g7)
    c: Perpendicular(g8,g9)
    c: Perpendicular(g9,g10)
    c: Perpendicular(g10,g11)
    c: PointOnObject(g-3,g8)
    c: PointOnObject(g-3,g11)
    c: PointOnObject(g-4,g10)
    c: DistanceY(g0,g-3) = 0.6
    c: DistanceY(g-5,g4) = 2
FEATURE [PartDesign::Pad] Pad096
  Direction = (0,0,-1)
  Length = 0.2
  Length2 = 10
  Profile = -> Sketch123
  ReferenceAxis = -> Sketch123 [N_Axis]
  Refine = true
  Suppressed = false
  Type = 0
FEATURE [Sketcher::SketchObject] Sketch124
  ArcFitTolerance = 1e-06
  AttachmentSupport = -> [Pad096]
  ExternalGeometry = -> [Pad096]
  FullyConstrained = true
  MakeInternals = false
  MapMode = 5
  Placement = pos=(0,0,-0.00178905) rot=(0,0,1;0rad)
  sketch-geometry (12):
    g0: LineSegment StartX=26 StartY=109.8 StartZ=0 EndX=26 EndY=97.8 EndZ=0
    g1: LineSegment StartX=26 StartY=97.8 StartZ=0 EndX=38 EndY=97.8 EndZ=0
    g2: LineSegment StartX=38 StartY=97.8 StartZ=0 EndX=38 EndY=109.8 EndZ=0
    g3: LineSegment StartX=38 StartY=109.8 StartZ=0 EndX=26 EndY=109.8 EndZ=0
    g4: LineSegment StartX=25.5 StartY=110.3 StartZ=0 EndX=25.5 EndY=97.3 EndZ=0
    g5: LineSegment StartX=25.5 StartY=97.3 StartZ=0 EndX=38.5 EndY=97.3 EndZ=0
    g6: LineSegment StartX=38.5 StartY=97.3 StartZ=0 EndX=38.5 EndY=110.3 EndZ=0
    g7: LineSegment StartX=38.5 StartY=110.3 StartZ=0 EndX=25.5 EndY=110.3 EndZ=0
    g8: LineSegment [constr] StartX=26 StartY=109.8 StartZ=0 EndX=25.5 EndY=110.3 EndZ=0
    g9: LineSegment [constr] StartX=26 StartY=97.8 StartZ=0 EndX=25.5 EndY=97.3 EndZ=0
    g10: LineSegment [constr] StartX=38 StartY=97.8 StartZ=0 EndX=38.5 EndY=97.3 EndZ=0
    g11: LineSegment [constr] StartX=38 StartY=109.8 StartZ=0 EndX=38.5 EndY=110.3 EndZ=0
  constraints (30):
    c: Coincident(g0,g1)
    c: Coincident(g1,g2)
    c: Coincident(g2,g3)
    c: Coincident(g3,g0)
    c: Vertical(g0)
    c: Vertical(g2)
    c: Horizontal(g1)
    c: Horizontal(g3)
    c: Coincident(g4,g5)
    c: Coincident(g5,g6)
    c: Coincident(g6,g7)
    c: Coincident(g7,g4)
    c: Vertical(g4)
    c: Vertical(g6)
    c: Horizontal(g5)
    c: Horizontal(g7)
    c: Coincident(g8,g0)
    c: Coincident(g8,g4)
    c: Coincident(g9,g1)
    c: Coincident(g9,g5)
    c: Coincident(g10,g2)
    c: Coincident(g10,g6)
    c: Coincident(g11,g3)
    c: Coincident(g11,g7)
    c: Perpendicular(g8,g9)
    c: Perpendicular(g9,g10)
    c: Perpendicular(g10,g11)
    c: Distance(g4,g0) = 0.5
    c: Coincident(g0,g-3)
    c: Coincident(g1,g-4)
FEATURE [PartDesign::Pad] Pad097
  BaseFeature = -> Pad096
  Direction = (0,0,1)
  Length = 5
  Length2 = 10
  Profile = -> Sketch124
  ReferenceAxis = -> Sketch124 [N_Axis]
  Refine = true
  Suppressed = false
  Type = 0
FEATURE [PartDesign::Body] Body068  label="Shutdown Button Border"
  AllowCompound = false
  Group = -> [Binder029,Sketch123,Pad096,Sketch124,Pad097]
  Origin = -> Origin342
  Tip = -> Pad097
FEATURE [PartDesign::Pad] Pad098
  BaseFeature = -> Pocket024
  Direction = (1e-16,4e-16,-1)
  Length = 1.4
  Length2 = 10
  Profile = -> Pocket024 [Face215,Face202,Face199]
  Refine = true
  Suppressed = false
  Type = 0
FEATURE [Sketcher::SketchObject] Sketch125
  ArcFitTolerance = 1e-06
  AttachmentSupport = -> [Pad098]
  ExternalGeometry = -> [Pad098]
  FullyConstrained = true
  MakeInternals = false
  MapMode = 5
  Placement = pos=(-3e-16,-1.4e-15,3.2) rot=(0,0,1;0rad)
  sketch-geometry (6):
    g0: GeomPoint X=63.9 Y=63.55 Z=0
    g1: LineSegment StartX=61.5 StartY=63.55 StartZ=0 EndX=66.3 EndY=63.55 EndZ=0
    g2: LineSegment StartX=66.3 StartY=63.55 StartZ=0 EndX=66.3 EndY=65.25 EndZ=0
    g3: LineSegment StartX=66.3 StartY=65.25 StartZ=0 EndX=61.5 EndY=65.25 EndZ=0
    g4: LineSegment StartX=61.5 StartY=65.25 StartZ=0 EndX=61.5 EndY=63.55 EndZ=0
    g5: GeomPoint X=63.9 Y=63.55 Z=0
  constraints (13):
    c: Symmetric(g-3,g-3,g0)
    c: Coincident(g1,g2)
    c: Coincident(g2,g3)
    c: Coincident(g3,g4)
    c: Coincident(g4,g1)
    c: Horizontal(g1)
    c: Horizontal(g3)
    c: Vertical(g2)
    c: Vertical(g4)
    c: DistanceX(g3,g3) = 4.8
    c: DistanceY(g4,g4) = 1.7
    c: Symmetric(g1,g1,g5)
    c: Coincident(g5,g0)
FEATURE [Sketcher::SketchObject] Sketch126
  ArcFitTolerance = 1e-06
  FullyConstrained = true
  MakeInternals = false
  MapMode = 5
  Placement = pos=(29,0,0) rot=(0.57735,-0.57735,-0.57735;2.0944rad)
  sketch-geometry (4):
    g0: LineSegment StartX=-48.9 StartY=-6.48e-14 StartZ=0 EndX=-49.9 EndY=-6.48e-14 EndZ=0
    g1: LineSegment StartX=-49.9 StartY=-6.48e-14 StartZ=0 EndX=-49.9 EndY=-6 EndZ=0
    g2: LineSegment StartX=-49.9 StartY=-6 StartZ=0 EndX=-48.9 EndY=-7 EndZ=0
    g3: LineSegment StartX=-48.9 StartY=-7 StartZ=0 EndX=-48.9 EndY=-6.48e-14 EndZ=0
  constraints (12):
    c: Coincident(g0,g1)
    c: Coincident(g1,g2)
    c: Coincident(g2,g3)
    c: Coincident(g3,g0)
    c: Horizontal(g0)
    c: Vertical(g1)
    c: Vertical(g3)
    c: Distance(g1,g3) = 1
    c: Distance(g0,g2) = 7
    c: PointOnObject(g0,g-3)
    c: PointOnObject(g-4,g3)
    c: Angle(g3,g2) = 0.785398
FEATURE [PartDesign::Pocket] Pocket035
  BaseFeature = -> Pad098
  Direction = (1,1e-16,-1e-16)
  Length = 7
  Length2 = 5
  Profile = -> Sketch126
  ReferenceAxis = -> Sketch126 [N_Axis]
  Refine = true
  Suppressed = false
  Type = 0
FEATURE [PartDesign::Pad] Pad099
  BaseFeature = -> Pocket035
  Direction = (0,0,1)
  Length = 3.2
  Length2 = 10
  Profile = -> Sketch125
  ReferenceAxis = -> Sketch125 [N_Axis]
  Refine = true
  Reversed = true
  Suppressed = false
  Type = 0
FEATURE [Part::Feature] Part__Feature266  label="JST_S4B_PH_K"
  shape: bbox 9.9 x 7.6 x 8.25 mm, 174 faces (baked)
FEATURE [App::Part] JST_PH_S4B_PH_K_1x04_P2_00mm_Horizontal  label="JST_PH_S4B-PH-K_1x04_P2.00mm_Horizontal"
  Group = -> [Part__Feature266]
  Origin = -> Origin343
  Placement = pos=(78.1,3.15,-0.05) rot=(1,0,0;3.14159rad)
FEATURE [Part::Feature] Part__Feature267  label="JST_S2B_PH_K"
  shape: bbox 5.9 x 7.6 x 8.25 mm, 110 faces (baked)
FEATURE [App::Part] JST_PH_S2B_PH_K_1x02_P2_00mm_Horizontal  label="JST_PH_S2B-PH-K_1x02_P2.00mm_Horizontal"
  Group = -> [Part__Feature267]
  Origin = -> Origin344
  Placement = pos=(49.95,3.5,-0.05) rot=(1,0,0;3.14159rad)
FEATURE [Part::Feature] Part__Feature268  label="JST_S2B_PH_K001"
  shape: bbox 5.9 x 7.6 x 8.25 mm, 110 faces (baked)
FEATURE [App::Part] JST_PH_S2B_PH_K_1x02_P2_00mm_Horizontal001  label="JST_PH_S2B-PH-K_1x02_P2.00mm_Horizontal001"
  Group = -> [Part__Feature268]
  Origin = -> Origin345
  Placement = pos=(56.9,3.5,-0.05) rot=(1,0,0;3.14159rad)
FEATURE [Part::Feature] Part__Feature269  label="JST_S2B_PH_K002"
  shape: bbox 5.9 x 7.6 x 8.25 mm, 110 faces (baked)
FEATURE [App::Part] JST_PH_S2B_PH_K_1x02_P2_00mm_Horizontal002  label="JST_PH_S2B-PH-K_1x02_P2.00mm_Horizontal002"
  Group = -> [Part__Feature269]
  Origin = -> Origin346
  Placement = pos=(63.85,3.5,-0.05) rot=(1,0,0;3.14159rad)
FEATURE [Part::Feature] Part__Feature270  label="KeyswitchCarrierMk3_PCB"
  shape: bbox 97.15 x 30.02 x 1.6 mm, 40 faces (baked)
FEATURE [App::Part] KeyswitchCarrierMk3_1  label="KeyswitchCarrierMk3 1"
  Group = -> [JST_PH_S4B_PH_K_1x04_P2_00mm_Horizontal,JST_PH_S2B_PH_K_1x02_P2_00mm_Horizontal,JST_PH_S2B_PH_K_1x02_P2_00mm_Horizontal001,JST_PH_S2B_PH_K_1x02_P2_00mm_Horizontal002,Part__Feature270]
  Origin = -> Origin347
  Placement = pos=(15.2,114.3,-14.9) rot=(0,0,1;-1.5708rad)
  expr: .Placement.Base.z = -13.5 mm - 1.4 mm
FEATURE [Mesh::Feature] Component
  Placement = pos=(-4,26,0) rot=(0,-1,0;1.5708rad)
FEATURE [Mesh::Feature] Component001
  Placement = pos=(0,0,0) rot=(0,-1,0;1.5708rad)
FEATURE [Mesh::Feature] Component002
  Placement = pos=(-4,26,0) rot=(0,-1,0;1.5708rad)
FEATURE [Mesh::Feature] Component003
  Placement = pos=(0,0,0) rot=(0,-1,0;1.5708rad)
FEATURE [Part::Feature] Component004
  shape: bbox 8.3 x 11.95 x 4.4 mm, 2629 faces, 0 solids (baked)
FEATURE [Part::Feature] Component004_solid  label="Component004 (Solid)"
  shape: bbox 8.3 x 11.95 x 4.4 mm, 2629 faces (baked)
FEATURE [PartDesign::FeatureBase] BaseFeature005
  BaseFeature = -> Component004_solid
  Suppressed = false
FEATURE [PartDesign::Body] Body069
  AllowCompound = false
  BaseFeature = -> Component004_solid
  Group = -> [BaseFeature005]
  Origin = -> Origin350
  Tip = -> BaseFeature005
FEATURE [App::Part] Part012  label="stabilizer"
  Group = -> [Component,Component001,Component004,Body069,Component004_solid]
  Origin = -> Origin348
  Placement = pos=(40,20,-31) rot=(1,0,0;1.5708rad)
FEATURE [Part::Feature] Component005
  shape: bbox 8.3 x 11.95 x 4.4 mm, 2629 faces, 0 solids (baked)
FEATURE [Part::Feature] Component005_solid  label="Component005 (Solid)"
  shape: bbox 8.3 x 11.95 x 4.4 mm, 2629 faces (baked)
FEATURE [PartDesign::FeatureBase] BaseFeature006
  BaseFeature = -> Component005_solid
  Suppressed = false
FEATURE [PartDesign::Body] Body070
  AllowCompound = false
  BaseFeature = -> Component005_solid
  Group = -> [BaseFeature006]
  Origin = -> Origin351
  Tip = -> BaseFeature006
FEATURE [App::Part] Part013  label="stabilizer001"
  Group = -> [Component002,Component003,Component005,Component005_solid,Body070]
  Origin = -> Origin349
  Placement = pos=(40,43.7,-31) rot=(1,0,0;1.5708rad)
FEATURE [PartDesign::SubShapeBinder] Binder030
  BindCopyOnChange = 0
  BindMode = 0
  ClaimChildren = false
  Context = -> Body063 [Binder030.]
  Fuse = false
  MakeFace = true
  OffsetFill = false
  OffsetIntersection = false
  OffsetJoinType = 0
  OffsetOpenResult = false
  PartialLoad = false
  Refine = true
  Relative = true
  Support = -> [Part012[Body069.],Part013[Body070.]]
  _Version = 2
FEATURE [Sketcher::SketchObject] Sketch127
  ArcFitTolerance = 1e-06
  AttachmentSupport = -> [Pocket032]
  ExternalGeometry = -> [Pocket032,Binder030]
  FullyConstrained = true
  MakeInternals = false
  MapMode = 5
  Placement = pos=(0,0,5.39821) rot=(1,0,0;3.14159rad)
  sketch-geometry (75):
    g0: LineSegment StartX=29.625 StartY=-20.625 StartZ=0 EndX=29.625 EndY=-19.375 EndZ=0
    g1: LineSegment StartX=29.625 StartY=-19.375 StartZ=0 EndX=31.3 EndY=-19.375 EndZ=0
    g2: LineSegment [constr] StartX=31.3 StartY=-19.375 StartZ=0 EndX=31.3 EndY=-17.8 EndZ=0
    g3: LineSegment [constr] StartX=31.3 StartY=-17.8 StartZ=0 EndX=32.45 EndY=-17.8 EndZ=0
    g4: LineSegment [constr] StartX=32.45 StartY=-17.8 StartZ=0 EndX=32.45 EndY=-19.375 EndZ=0
    g5: LineSegment StartX=32.45 StartY=-19.375 StartZ=0 EndX=34.125 EndY=-19.375 EndZ=0
    g6: LineSegment StartX=34.125 StartY=-19.375 StartZ=0 EndX=34.125 EndY=-20.625 EndZ=0
    g7: LineSegment StartX=34.125 StartY=-20.625 StartZ=0 EndX=32.45 EndY=-20.625 EndZ=0
    g8: LineSegment StartX=32.45 StartY=-20.625 StartZ=0 EndX=32.45 EndY=-22.2 EndZ=0
    g9: LineSegment StartX=32.45 StartY=-22.2 StartZ=0 EndX=31.3 EndY=-22.2 EndZ=0
    g10: LineSegment StartX=31.3 StartY=-22.2 StartZ=0 EndX=31.3 EndY=-20.625 EndZ=0
    g11: LineSegment StartX=31.3 StartY=-20.625 StartZ=0 EndX=29.625 EndY=-20.625 EndZ=0
    g12: LineSegment [constr] StartX=29.875 StartY=-20.5 StartZ=0 EndX=33.875 EndY=-19.5 EndZ=0
    g13: LineSegment [constr] StartX=33.875 StartY=-20.5 StartZ=0 EndX=29.875 EndY=-19.5 EndZ=0
    g14: LineSegment [constr] StartX=31.325 StartY=-22 StartZ=0 EndX=32.425 EndY=-18 EndZ=0
    g15: LineSegment [constr] StartX=32.425 StartY=-22 StartZ=0 EndX=31.325 EndY=-18 EndZ=0
    g16: GeomPoint [constr] X=31.875 Y=-20 Z=0
    g17: LineSegment [constr] StartX=31.3 StartY=-22.2 StartZ=0 EndX=32.45 EndY=-17.8 EndZ=0
    g18: LineSegment [constr] StartX=31.3 StartY=-17.8 StartZ=0 EndX=32.45 EndY=-22.2 EndZ=0
    g19: LineSegment [constr] StartX=29.625 StartY=-20.625 StartZ=0 EndX=34.125 EndY=-19.375 EndZ=0
    g20: LineSegment [constr] StartX=29.625 StartY=-19.375 StartZ=0 EndX=34.125 EndY=-20.625 EndZ=0
    g21: GeomPoint [constr] X=31.875 Y=-20 Z=0
    g22: LineSegment StartX=29.045 StartY=-20.975 StartZ=0 EndX=29.045 EndY=-19.025 EndZ=0
    g23: LineSegment [constr] StartX=29.045 StartY=-19.025 StartZ=0 EndX=31 EndY=-17.12 EndZ=0
    g24: LineSegment [constr] StartX=31 StartY=-17.12 StartZ=0 EndX=32.75 EndY=-17.12 EndZ=0
    g25: LineSegment [constr] StartX=32.75 StartY=-17.12 StartZ=0 EndX=34.705 EndY=-19.025 EndZ=0
    g26: LineSegment StartX=34.705 StartY=-19.025 StartZ=0 EndX=34.705 EndY=-20.975 EndZ=0
    g27: LineSegment StartX=34.705 StartY=-20.975 StartZ=0 EndX=32.75 EndY=-22.88 EndZ=0
    g28: LineSegment StartX=32.75 StartY=-22.88 StartZ=0 EndX=31 EndY=-22.88 EndZ=0
    g29: LineSegment StartX=31 StartY=-22.88 StartZ=0 EndX=29.045 EndY=-20.975 EndZ=0
    g30: LineSegment [constr] StartX=29.625 StartY=-20 StartZ=0 EndX=29.045 EndY=-20 EndZ=0
    g31: LineSegment [constr] StartX=31.875 StartY=-17.8 StartZ=0 EndX=31.875 EndY=-17.12 EndZ=0
    g32: LineSegment [constr] StartX=31.875 StartY=-22.2 StartZ=0 EndX=31.875 EndY=-22.88 EndZ=0
    g33: LineSegment [constr] StartX=34.125 StartY=-20 StartZ=0 EndX=34.705 EndY=-20 EndZ=0
    g34: LineSegment StartX=29.625 StartY=-44.375 StartZ=0 EndX=29.625 EndY=-43.025 EndZ=0
    g35: LineSegment StartX=29.625 StartY=-43.025 StartZ=0 EndX=31.3 EndY=-43.025 EndZ=0
    g36: LineSegment StartX=31.3 StartY=-43.025 StartZ=0 EndX=31.3 EndY=-41.45 EndZ=0
    g37: LineSegment StartX=31.3 StartY=-41.45 StartZ=0 EndX=32.45 EndY=-41.45 EndZ=0
    g38: LineSegment StartX=32.45 StartY=-41.45 StartZ=0 EndX=32.45 EndY=-43.025 EndZ=0
    g39: LineSegment StartX=32.45 StartY=-43.025 StartZ=0 EndX=34.125 EndY=-43.025 EndZ=0
    g40: LineSegment StartX=34.125 StartY=-43.025 StartZ=0 EndX=34.125 EndY=-44.375 EndZ=0
    g41: LineSegment StartX=34.125 StartY=-44.375 StartZ=0 EndX=32.45 EndY=-44.375 EndZ=0
    g42: LineSegment [constr] StartX=32.45 StartY=-44.375 StartZ=0 EndX=32.45 EndY=-45.95 EndZ=0
    g43: LineSegment [constr] StartX=32.45 StartY=-45.95 StartZ=0 EndX=31.3 EndY=-45.95 EndZ=0
    g44: LineSegment [constr] StartX=31.3 StartY=-45.95 StartZ=0 EndX=31.3 EndY=-44.375 EndZ=0
    g45: LineSegment StartX=31.3 StartY=-44.375 StartZ=0 EndX=29.625 EndY=-44.375 EndZ=0
    g46: LineSegment [constr] StartX=31.3 StartY=-45.95 StartZ=0 EndX=32.45 EndY=-41.45 EndZ=0
    g47: LineSegment [constr] StartX=31.3 StartY=-41.45 StartZ=0 EndX=32.45 EndY=-45.95 EndZ=0
    g48: LineSegment [constr] StartX=31.325 StartY=-45.7 StartZ=0 EndX=32.425 EndY=-41.7 EndZ=0
    g49: LineSegment [constr] StartX=31.325 StartY=-41.7 StartZ=0 EndX=32.425 EndY=-45.7 EndZ=0
    g50: GeomPoint [constr] X=31.875 Y=-43.7 Z=0
    g51: LineSegment StartX=29.045 StartY=-44.675 StartZ=0 EndX=29.045 EndY=-42.725 EndZ=0
    g52: LineSegment StartX=29.045 StartY=-42.725 StartZ=0 EndX=31 EndY=-40.77 EndZ=0
    g53: LineSegment StartX=31 StartY=-40.77 StartZ=0 EndX=32.75 EndY=-40.77 EndZ=0
    g54: LineSegment StartX=32.75 StartY=-40.77 StartZ=0 EndX=34.705 EndY=-42.725 EndZ=0
    g55: LineSegment StartX=34.705 StartY=-42.725 StartZ=0 EndX=34.705 EndY=-44.675 EndZ=0
    g56: LineSegment [constr] StartX=34.705 StartY=-44.675 StartZ=0 EndX=32.75 EndY=-46.63 EndZ=0
    g57: LineSegment [constr] StartX=32.75 StartY=-46.63 StartZ=0 EndX=31 EndY=-46.63 EndZ=0
    g58: LineSegment [constr] StartX=31 StartY=-46.63 StartZ=0 EndX=29.045 EndY=-44.675 EndZ=0
    g59: LineSegment [constr] StartX=29.625 StartY=-43.7 StartZ=0 EndX=29.045 EndY=-43.7 EndZ=0
    g60: LineSegment [constr] StartX=31.875 StartY=-41.45 StartZ=0 EndX=31.875 EndY=-40.77 EndZ=0
    g61: LineSegment [constr] StartX=34.125 StartY=-43.7 StartZ=0 EndX=34.705 EndY=-43.7 EndZ=0
    g62: LineSegment [constr] StartX=31.875 StartY=-45.95 StartZ=0 EndX=31.875 EndY=-46.63 EndZ=0
    g63: LineSegment StartX=31.3 StartY=-44.375 StartZ=0 EndX=31.3 EndY=-45.55 EndZ=0
    g64: LineSegment StartX=31.3 StartY=-45.55 StartZ=0 EndX=29.92 EndY=-45.55 EndZ=0
    g65: LineSegment StartX=29.92 StartY=-45.55 StartZ=0 EndX=29.045 EndY=-44.675 EndZ=0
    g66: LineSegment StartX=32.45 StartY=-44.375 StartZ=0 EndX=32.45 EndY=-45.55 EndZ=0
    g67: LineSegment StartX=32.45 StartY=-45.55 StartZ=0 EndX=33.83 EndY=-45.55 EndZ=0
    g68: LineSegment StartX=33.83 StartY=-45.55 StartZ=0 EndX=34.705 EndY=-44.675 EndZ=0
    g69: LineSegment StartX=31.3 StartY=-19.375 StartZ=0 EndX=31.3 EndY=-18.2 EndZ=0
    g70: LineSegment StartX=31.3 StartY=-18.2 StartZ=0 EndX=29.8917 EndY=-18.2 EndZ=0
    g71: LineSegment StartX=29.8917 StartY=-18.2 StartZ=0 EndX=29.045 EndY=-19.025 EndZ=0
    g72: LineSegment StartX=32.45 StartY=-19.375 StartZ=0 EndX=32.45 EndY=-18.2 EndZ=0
    g73: LineSegment StartX=32.45 StartY=-18.2 StartZ=0 EndX=33.8583 EndY=-18.2 EndZ=0
    g74: LineSegment StartX=33.8583 StartY=-18.2 StartZ=0 EndX=34.705 EndY=-19.025 EndZ=0
  constraints (211):
    c: DistanceY(g-4,g-4) = 1.35
    c: DistanceX(g-7,g-7) = 1.15
    c: DistanceX(g-3,g-3) = 1.675
    c: Distance(g-6,g-6) = 1.575
    c: Vertical(g0)
    c: Coincident(g0,g1)
    c: Horizontal(g1)
    c: Coincident(g1,g2)
    c: Vertical(g2)
    c: Coincident(g2,g3)
    c: Horizontal(g3)
    c: Coincident(g3,g4)
    c: Vertical(g4)
    c: Coincident(g4,g5)
    c: Horizontal(g5)
    c: Coincident(g5,g6)
    c: Vertical(g6)
    c: Coincident(g6,g7)
    c: Horizontal(g7)
    c: Coincident(g7,g8)
    c: Vertical(g8)
    c: Coincident(g8,g9)
    c: Horizontal(g9)
    c: Coincident(g9,g10)
    c: Vertical(g10)
    c: Coincident(g10,g11)
    c: Coincident(g11,g0)
    c: Horizontal(g11)
    c: Equal(g-3,g1)
    c: Equal(g-6,g2)
    c: Equal(g2,g4)
    c: Equal(g5,g1)
    c: Equal(g7,g5)
    c: Equal(g8,g4)
    c: Coincident(g12,g-14)
    c: Coincident(g12,g-12)
    c: Coincident(g13,g-12)
    c: Coincident(g13,g-14)
    c: Coincident(g14,g-15)
    c: Coincident(g14,g-13)
    c: Coincident(g15,g-15)
    c: Coincident(g15,g-13)
    c: PointOnObject(g16,g12)
    c: PointOnObject(g16,g13)
    c: Coincident(g17,g9)
    c: Coincident(g17,g3)
    c: Coincident(g18,g2)
    c: Coincident(g18,g8)
    c: Coincident(g19,g0)
    c: Coincident(g19,g5)
    c: Coincident(g20,g0)
    c: Coincident(g20,g6)
    c: PointOnObject(g21,g19)
    c: PointOnObject(g21,g20)
    c: Coincident(g21,g16)
    c: DistanceY(g-23,g-23) = 1.95
    c: Distance(g-22,g-22) = 2.76479
    c: DistanceX(g-21,g-21) = 1.75
    c: DistanceY(g-19,g-19) = 1.95
    c: DistanceX(g-17,g-17) = 1.75
    c: Distance(g-16,g-16) = 2.76479
    c: Distance(g-18,g-18) = 2.76479
    c: Distance(g-20,g-20) = 2.76479
    c: DistanceX(g-23,g-4) = 0.58
    c: Vertical(g22)
    c: Coincident(g22,g23)
    c: Coincident(g23,g24)
    c: Horizontal(g24)
    c: Coincident(g24,g25)
    c: Coincident(g25,g26)
    c: Vertical(g26)
    c: Coincident(g26,g27)
    c: Coincident(g27,g28)
    c: Horizontal(g28)
    c: Coincident(g28,g29)
    c: Coincident(g29,g22)
    c: Equal(g-23,g22)
    c: DistanceX(g22,g0) = 0.58
    c: Symmetric(g0,g0,g30)
    c: Symmetric(g22,g22,g30)
    c: Horizontal(g30)
    c: Equal(g24,g-21)
    c: DistanceY(g-7,g-22) = 0.68
    c: DistanceY(g2,g23) = 0.68
    c: Symmetric(g3,g3,g31)
    c: Symmetric(g24,g24,g31)
    c: Vertical(g31)
    c: Equal(g26,g22)
    c: Symmetric(g9,g9,g32)
    c: Symmetric(g28,g28,g32)
    c: Vertical(g32)
    c: DistanceY(g28,g9) = 0.68
    c: DistanceX(g6,g26) = 0.58
    c: Symmetric(g6,g6,g33)
    c: Symmetric(g26,g26,g33)
    c: Horizontal(g33)
    c: Equal(g28,g24)
    c: Vertical(g34)
    c: Coincident(g34,g35)
    c: Horizontal(g35)
    c: Coincident(g35,g36)
    c: Vertical(g36)
    c: Coincident(g36,g37)
    c: Horizontal(g37)
    c: Coincident(g37,g38)
    c: Vertical(g38)
    c: Coincident(g38,g39)
    c: Horizontal(g39)
    c: Coincident(g39,g40)
    c: Vertical(g40)
    c: Coincident(g40,g41)
    c: Horizontal(g41)
    c: Coincident(g41,g42)
    c: Vertical(g42)
    c: Coincident(g42,g43)
    c: Horizontal(g43)
    c: Coincident(g43,g44)
    c: Vertical(g44)
    c: Coincident(g44,g45)
    c: Coincident(g45,g34)
    c: Horizontal(g45)
    c: Equal(g35,g-3)
    c: Equal(g36,g-6)
    c: Equal(g36,g38)
    c: Equal(g39,g35)
    c: Equal(g41,g39)
    c: Equal(g42,g38)
    c: Equal(g45,g35)
    c: Coincident(g46,g43)
    c: Coincident(g46,g37)
    c: Coincident(g47,g36)
    c: Coincident(g47,g42)
    c: Coincident(g48,g-8)
    c: Coincident(g48,g-10)
    c: Coincident(g49,g-10)
    c: Coincident(g49,g-8)
    c: PointOnObject(g50,g46)
    c: PointOnObject(g50,g47)
    c: PointOnObject(g50,g48)
    c: PointOnObject(g50,g49)
    c: Equal(g3,g-7)
    c: Equal(g3,g9)
    c: Equal(g34,g-4)
    c: Equal(g40,g34)
    c: Equal(g37,g-7)
    c: Vertical(g51)
    c: Coincident(g51,g52)
    c: Coincident(g52,g53)
    c: Horizontal(g53)
    c: Coincident(g53,g54)
    c: Coincident(g54,g55)
    c: Vertical(g55)
    c: Coincident(g55,g56)
    c: Coincident(g56,g57)
    c: Coincident(g57,g58)
    c: Coincident(g58,g51)
    c: Equal(g51,g-23)
    c: DistanceX(g51,g34) = 0.58
    c: Symmetric(g34,g34,g59)
    c: Symmetric(g51,g51,g59)
    c: Horizontal(g59)
    c: Equal(g53,g-21)
    c: DistanceY(g36,g52) = 0.68
    c: Symmetric(g37,g37,g60)
    c: Symmetric(g53,g53,g60)
    c: Vertical(g60)
    c: Equal(g55,g51)
    c: DistanceX(g40,g55) = 0.58
    c: Symmetric(g40,g40,g61)
    c: Symmetric(g55,g55,g61)
    c: Horizontal(g61)
    c: Horizontal(g57)
    c: DistanceY(g57,g43) = 0.68
    c: Symmetric(g43,g43,g62)
    c: Symmetric(g57,g57,g62)
    c: Vertical(g62)
    c: Equal(g57,g53)
    c: Coincident(g63,g44)
    c: PointOnObject(g63,g44)
    c: Coincident(g64,g63)
    c: PointOnObject(g64,g58)
    c: Horizontal(g64)
    c: Coincident(g65,g64)
    c: Coincident(g65,g51)
    c: DistanceY(g43,g63) = 0.4
    c: Coincident(g66,g41)
    c: PointOnObject(g66,g42)
    c: Coincident(g67,g66)
    c: PointOnObject(g67,g56)
    c: Horizontal(g67)
    c: Coincident(g68,g67)
    c: Coincident(g68,g55)
    c: Equal(g66,g63)
    c: Coincident(g69,g1)
    c: PointOnObject(g69,g2)
    c: Coincident(g70,g69)
    c: PointOnObject(g70,g23)
    c: Horizontal(g70)
    c: Coincident(g71,g70)
    c: Coincident(g71,g22)
    c: Coincident(g72,g4)
    c: PointOnObject(g72,g4)
    c: Coincident(g73,g72)
    c: PointOnObject(g73,g25)
    c: Horizontal(g73)
    c: Coincident(g74,g73)
    c: Coincident(g74,g25)
    c: Equal(g72,g69)
    c: DistanceY(g69,g2) = 0.4
    c: DistanceY(g6,g6) = 1.25
    c: PointOnObject(g10,g7)
FEATURE [PartDesign::Pad] Pad100
  BaseFeature = -> Pocket032
  Direction = (0,0,-1)
  Length = 7.21
  Length2 = 10
  Profile = -> Sketch127
  ReferenceAxis = -> Sketch127 [N_Axis]
  Refine = true
  Suppressed = false
  Type = 0
FEATURE [PartDesign::Body] Body063  label="Quit Button fat revised"
  AllowCompound = false
  BaseFeature = -> Cut004
  Group = -> [BaseFeature002,Pad086,Pad087,Sketch116,Pocket032,Binder030,Sketch127,Pad100]
  Origin = -> Origin337
  Tip = -> Pad100
FEATURE [PartDesign::FeatureBase] Clone004
  BaseFeature = -> Body001
  Suppressed = false
FEATURE [PartDesign::Pocket] Pocket036
  BaseFeature = -> Clone004
  Direction = (0,0,-1)
  Length = 19.2
  Length2 = 5
  Profile = -> Clone004 [Face66,Face62,Face58,Face54,Face90,Face86,Face82,Face78]
  Refine = true
  Suppressed = false
  Type = 0
FEATURE [Sketcher::SketchObject] Sketch128
  ArcFitTolerance = 1e-06
  AttachmentSupport = -> [Pocket001]
  ExternalGeometry = -> [Pocket001]
  FullyConstrained = true
  MakeInternals = false
  MapMode = 5
  Placement = pos=(0,135.8,0) rot=(0,0.707107,0.707107;3.14159rad)
  sketch-geometry (7):
    g0: LineSegment StartX=-127.8 StartY=-4.9e-15 StartZ=0 EndX=-131 EndY=-4.9e-15 EndZ=0
    g1: LineSegment StartX=-127.8 StartY=-3.2 StartZ=0 EndX=-127.8 EndY=-4.9e-15 EndZ=0
    g2: LineSegment [constr] StartX=-131 StartY=-4.9e-15 StartZ=0 EndX=-131 EndY=-3.2 EndZ=0
    g3: LineSegment StartX=-131 StartY=-3.2 StartZ=0 EndX=-127.8 EndY=-3.2 EndZ=0
    g4: LineSegment StartX=-131 StartY=-4.9e-15 StartZ=0 EndX=-143.8 EndY=-7.68 EndZ=0
    g5: LineSegment StartX=-143.8 StartY=-7.68 StartZ=0 EndX=-143.8 EndY=-10.88 EndZ=0
    g6: LineSegment StartX=-143.8 StartY=-10.88 StartZ=0 EndX=-131 EndY=-3.2 EndZ=0
  constraints (19):
    c: Coincident(g1,g0)
    c: Horizontal(g0)
    c: Vertical(g1)
    c: Distance(g0,g1) = 3.2
    c: Coincident(g0,g-3)
    c: Coincident(g2,g0)
    c: Vertical(g2)
    c: Coincident(g3,g2)
    c: Coincident(g3,g1)
    c: Horizontal(g3)
    c: DistanceY(g2,g2) = 3.2
    c: Coincident(g0,g4)
    c: Coincident(g4,g5)
    c: Vertical(g5)
    c: Coincident(g5,g6)
    c: Coincident(g6,g2)
    c: Parallel(g6,g4)
    c: PointOnObject(g-3,g5)
    c: Parallel(g-3,g4)
FEATURE [Sketcher::SketchObject] Sketch129
  ArcFitTolerance = 1e-06
  AttachmentSupport = -> [Pocket002]
  ExternalGeometry = -> [Pocket002]
  FullyConstrained = true
  MakeInternals = false
  MapMode = 5
  Placement = pos=(0,104,0) rot=(0,0.707107,0.707107;3.14159rad)
  sketch-geometry (8):
    g0: LineSegment StartX=-127.8 StartY=-9.8e-15 StartZ=0 EndX=-131 EndY=-9.8e-15 EndZ=0
    g1: LineSegment [constr] StartX=-131 StartY=-9.8e-15 StartZ=0 EndX=-131 EndY=-3.2 EndZ=0
    g2: LineSegment StartX=-131 StartY=-3.2 StartZ=0 EndX=-127.8 EndY=-3.2 EndZ=0
    g3: LineSegment StartX=-127.8 StartY=-3.2 StartZ=0 EndX=-127.8 EndY=-9.8e-15 EndZ=0
    g4: LineSegment StartX=-131 StartY=-9.8e-15 StartZ=0 EndX=-143.8 EndY=-7.68 EndZ=0
    g5: LineSegment StartX=-143.8 StartY=-7.68 StartZ=0 EndX=-143.8 EndY=-10.88 EndZ=0
    g6: LineSegment StartX=-143.8 StartY=-10.88 StartZ=0 EndX=-131 EndY=-3.2 EndZ=0
    g7: LineSegment [constr] StartX=-131 StartY=-3.2 StartZ=0 EndX=-131 EndY=-9.8e-15 EndZ=0
  constraints (21):
    c: Coincident(g0,g1)
    c: Coincident(g1,g2)
    c: Coincident(g2,g3)
    c: Coincident(g3,g0)
    c: Horizontal(g0)
    c: Horizontal(g2)
    c: Vertical(g1)
    c: Vertical(g3)
    c: Distance(g1,g3) = 3.2
    c: Coincident(g0,g-3)
    c: Coincident(g4,g5)
    c: Coincident(g6,g7)
    c: Coincident(g7,g4)
    c: Vertical(g5)
    c: Coincident(g4,g0)
    c: Coincident(g6,g1)
    c: Parallel(g6,g4)
    c: DistanceY(g1,g1) = 3.2
    c: Parallel(g-3,g4)
    c: Coincident(g5,g6)
    c: PointOnObject(g-3,g5)
FEATURE [Sketcher::SketchObject] Sketch130
  ArcFitTolerance = 1e-06
  AttachmentSupport = -> [Pocket003]
  ExternalGeometry = -> [Pocket003]
  FullyConstrained = true
  MakeInternals = false
  MapMode = 5
  Placement = pos=(0,72,0) rot=(0,0.707107,0.707107;3.14159rad)
  expr: Constraints[10] = 1.6 * 2 mm
  sketch-geometry (8):
    g0: LineSegment StartX=-127.8 StartY=-2.2e-15 StartZ=0 EndX=-131 EndY=-2.2e-15 EndZ=0
    g1: LineSegment StartX=-131 StartY=-2.2e-15 StartZ=0 EndX=-131 EndY=-3.2 EndZ=0
    g2: LineSegment StartX=-131 StartY=-3.2 StartZ=0 EndX=-127.8 EndY=-3.2 EndZ=0
    g3: LineSegment StartX=-127.8 StartY=-3.2 StartZ=0 EndX=-127.8 EndY=-2.2e-15 EndZ=0
    g4: LineSegment StartX=-131 StartY=-2.2e-15 StartZ=0 EndX=-143.8 EndY=-7.68 EndZ=0
    g5: LineSegment StartX=-143.8 StartY=-7.68 StartZ=0 EndX=-143.8 EndY=-10.88 EndZ=0
    g6: LineSegment StartX=-143.8 StartY=-10.88 StartZ=0 EndX=-131 EndY=-3.2 EndZ=0
    g7: LineSegment StartX=-131 StartY=-3.2 StartZ=0 EndX=-131 EndY=-2.2e-15 EndZ=0
  constraints (21):
    c: Coincident(g0,g1)
    c: Coincident(g1,g2)
    c: Coincident(g2,g3)
    c: Coincident(g3,g0)
    c: Horizontal(g0)
    c: Horizontal(g2)
    c: Vertical(g1)
    c: Vertical(g3)
    c: Distance(g1,g3) = 3.2
    c: Coincident(g0,g-3)
    c: DistanceY(g1,g1) = 3.2
    c: Coincident(g4,g5)
    c: Coincident(g5,g6)
    c: Coincident(g6,g7)
    c: Coincident(g7,g4)
    c: Vertical(g5)
    c: Coincident(g4,g0)
    c: Coincident(g6,g1)
    c: Parallel(g4,g6)
    c: Parallel(g6,g-3)
    c: PointOnObject(g-3,g5)
FEATURE [Sketcher::SketchObject] Sketch131
  ArcFitTolerance = 1e-06
  AttachmentSupport = -> [Pocket004]
  ExternalGeometry = -> [Pocket004]
  FullyConstrained = true
  MakeInternals = false
  MapMode = 5
  Placement = pos=(0,40,0) rot=(0,0.707107,0.707107;3.14159rad)
  sketch-geometry (7):
    g0: LineSegment StartX=-127.8 StartY=-8e-15 StartZ=0 EndX=-131 EndY=-8e-15 EndZ=0
    g1: LineSegment [constr] StartX=-131 StartY=-8e-15 StartZ=0 EndX=-131 EndY=-3.2 EndZ=0
    g2: LineSegment StartX=-131 StartY=-3.2 StartZ=0 EndX=-127.8 EndY=-3.2 EndZ=0
    g3: LineSegment StartX=-127.8 StartY=-3.2 StartZ=0 EndX=-127.8 EndY=-8e-15 EndZ=0
    g4: LineSegment StartX=-131 StartY=-8e-15 StartZ=0 EndX=-143.8 EndY=-7.68 EndZ=0
    g5: LineSegment StartX=-143.8 StartY=-7.68 StartZ=0 EndX=-143.8 EndY=-10.88 EndZ=0
    g6: LineSegment StartX=-143.8 StartY=-10.88 StartZ=0 EndX=-131 EndY=-3.2 EndZ=0
  constraints (19):
    c: Coincident(g0,g1)
    c: Coincident(g1,g2)
    c: Coincident(g2,g3)
    c: Coincident(g3,g0)
    c: Horizontal(g0)
    c: Horizontal(g2)
    c: Vertical(g1)
    c: Vertical(g3)
    c: Distance(g1,g3) = 3.2
    c: Coincident(g0,g-3)
    c: DistanceY(g1,g1) = 3.2
    c: Coincident(g0,g4)
    c: Coincident(g4,g5)
    c: Vertical(g5)
    c: Coincident(g5,g6)
    c: Coincident(g6,g1)
    c: Parallel(g6,g4)
    c: Parallel(g-3,g4)
    c: PointOnObject(g-3,g5)
FEATURE [Sketcher::SketchObject] Sketch132
  ArcFitTolerance = 1e-06
  AttachmentSupport = -> [Pocket027]
  ExternalGeometry = -> [Pocket027]
  FullyConstrained = true
  MakeInternals = false
  MapMode = 5
  Placement = pos=(0,8,0) rot=(0,0.707107,0.707107;3.14159rad)
  sketch-geometry (7):
    g0: LineSegment StartX=-127.8 StartY=-2.4e-15 StartZ=0 EndX=-131 EndY=-2.4e-15 EndZ=0
    g1: LineSegment [constr] StartX=-131 StartY=-2.4e-15 StartZ=0 EndX=-131 EndY=-3.2 EndZ=0
    g2: LineSegment StartX=-131 StartY=-3.2 StartZ=0 EndX=-127.8 EndY=-3.2 EndZ=0
    g3: LineSegment StartX=-127.8 StartY=-3.2 StartZ=0 EndX=-127.8 EndY=-2.2e-15 EndZ=0
    g4: LineSegment StartX=-131 StartY=-2.4e-15 StartZ=0 EndX=-143.8 EndY=-7.68 EndZ=0
    g5: LineSegment StartX=-143.8 StartY=-7.68 StartZ=0 EndX=-143.8 EndY=-10.88 EndZ=0
    g6: LineSegment StartX=-143.8 StartY=-10.88 StartZ=0 EndX=-131 EndY=-3.2 EndZ=0
  constraints (19):
    c: Coincident(g0,g1)
    c: Coincident(g1,g2)
    c: Coincident(g2,g3)
    c: Coincident(g3,g0)
    c: Horizontal(g0)
    c: Horizontal(g2)
    c: Vertical(g1)
    c: Vertical(g3)
    c: Distance(g1,g3) = 3.2
    c: Coincident(g0,g-3)
    c: DistanceY(g1,g1) = 3.2
    c: Coincident(g0,g4)
    c: Coincident(g4,g5)
    c: Vertical(g5)
    c: Coincident(g5,g6)
    c: Coincident(g6,g1)
    c: Parallel(g4,g6)
    c: Parallel(g4,g-3)
    c: PointOnObject(g-3,g5)
FEATURE [Sketcher::SketchObject] Sketch133
  ArcFitTolerance = 1e-06
  FullyConstrained = true
  MakeInternals = false
  MapMode = 5
  Placement = pos=(120.8,0,0) rot=(0.57735,-0.57735,-0.57735;2.0944rad)
  sketch-geometry (7):
    g0: LineSegment StartX=0 StartY=0 StartZ=0 EndX=0 EndY=-3.2 EndZ=0
    g1: LineSegment StartX=0 StartY=-3.2 StartZ=0 EndX=3.2 EndY=-3.2 EndZ=0
    g2: LineSegment [constr] StartX=3.2 StartY=-3.2 StartZ=0 EndX=3.2 EndY=0 EndZ=0
    g3: LineSegment StartX=3.2 StartY=0 StartZ=0 EndX=0 EndY=0 EndZ=0
    g4: LineSegment StartX=3.2 StartY=0 StartZ=0 EndX=16 EndY=-7.68 EndZ=0
    g5: LineSegment StartX=16 StartY=-7.68 StartZ=0 EndX=16 EndY=-10.88 EndZ=0
    g6: LineSegment StartX=16 StartY=-10.88 StartZ=0 EndX=3.2 EndY=-3.2 EndZ=0
  constraints (19):
    c: Coincident(g0,g1)
    c: Coincident(g1,g2)
    c: Coincident(g2,g3)
    c: Coincident(g3,g0)
    c: Vertical(g0)
    c: Vertical(g2)
    c: Horizontal(g1)
    c: Horizontal(g3)
    c: Distance(g0,g2) = 3.2
    c: Coincident(g0,g-1)
    c: DistanceY(g2,g2) = 3.2
    c: Coincident(g4,g2)
    c: Coincident(g5,g4)
    c: Vertical(g5)
    c: Coincident(g6,g5)
    c: Coincident(g6,g1)
    c: Parallel(g6,g4)
    c: Parallel(g-3,g4)
    c: PointOnObject(g-3,g5)
FEATURE [Sketcher::SketchObject] Sketch134
  ArcFitTolerance = 1e-06
  AttachmentSupport = -> [Pocket031]
  ExternalGeometry = -> [Pocket031]
  FullyConstrained = true
  MakeInternals = false
  MapMode = 5
  Placement = pos=(103,0,0) rot=(0.57735,0.57735,0.57735;2.0944rad)
  sketch-geometry (7):
    g0: LineSegment StartX=0 StartY=0 StartZ=0 EndX=-3.2 EndY=0 EndZ=0
    g1: LineSegment [constr] StartX=-3.2 StartY=0 StartZ=0 EndX=-3.2 EndY=-3.2 EndZ=0
    g2: LineSegment StartX=-3.2 StartY=-3.2 StartZ=0 EndX=0 EndY=-3.2 EndZ=0
    g3: LineSegment StartX=0 StartY=-3.2 StartZ=0 EndX=0 EndY=0 EndZ=0
    g4: LineSegment StartX=-3.2 StartY=0 StartZ=0 EndX=-16 EndY=-7.68 EndZ=0
    g5: LineSegment StartX=-16 StartY=-7.68 StartZ=0 EndX=-16 EndY=-10.88 EndZ=0
    g6: LineSegment StartX=-16 StartY=-10.88 StartZ=0 EndX=-3.2 EndY=-3.2 EndZ=0
  constraints (19):
    c: Coincident(g0,g1)
    c: Coincident(g1,g2)
    c: Coincident(g2,g3)
    c: Coincident(g3,g0)
    c: Horizontal(g0)
    c: Horizontal(g2)
    c: Vertical(g1)
    c: Vertical(g3)
    c: Distance(g1,g3) = 3.2
    c: Coincident(g0,g-1)
    c: DistanceY(g1,g1) = 3.2
    c: Coincident(g0,g4)
    c: Coincident(g4,g5)
    c: Vertical(g5)
    c: Coincident(g5,g6)
    c: Coincident(g6,g1)
    c: Parallel(g4,g6)
    c: Parallel(g-3,g4)
    c: PointOnObject(g-3,g5)
FEATURE [Sketcher::SketchObject] Sketch135
  ArcFitTolerance = 1e-06
  AttachmentSupport = -> [Pocket030]
  ExternalGeometry = -> [Pocket030]
  FullyConstrained = true
  MakeInternals = false
  MapMode = 5
  Placement = pos=(71,0,0) rot=(0.57735,0.57735,0.57735;2.0944rad)
  sketch-geometry (7):
    g0: LineSegment StartX=0 StartY=0 StartZ=0 EndX=-3.2 EndY=0 EndZ=0
    g1: LineSegment [constr] StartX=-3.2 StartY=0 StartZ=0 EndX=-3.2 EndY=-3.2 EndZ=0
    g2: LineSegment StartX=-3.2 StartY=-3.2 StartZ=0 EndX=0 EndY=-3.2 EndZ=0
    g3: LineSegment StartX=0 StartY=-3.2 StartZ=0 EndX=0 EndY=0 EndZ=0
    g4: LineSegment StartX=-3.2 StartY=0 StartZ=0 EndX=-16 EndY=-7.68 EndZ=0
    g5: LineSegment StartX=-16 StartY=-7.68 StartZ=0 EndX=-16 EndY=-10.88 EndZ=0
    g6: LineSegment StartX=-16 StartY=-10.88 StartZ=0 EndX=-3.2 EndY=-3.2 EndZ=0
  constraints (19):
    c: Coincident(g0,g1)
    c: Coincident(g1,g2)
    c: Coincident(g2,g3)
    c: Coincident(g3,g0)
    c: Horizontal(g0)
    c: Horizontal(g2)
    c: Vertical(g1)
    c: Vertical(g3)
    c: Distance(g1,g3) = 3.2
    c: Coincident(g0,g-1)
    c: DistanceY(g1,g1) = 3.2
    c: Coincident(g0,g4)
    c: Coincident(g4,g5)
    c: Vertical(g5)
    c: Coincident(g5,g6)
    c: Coincident(g6,g1)
    c: Parallel(g4,g6)
    c: Parallel(g-3,g4)
    c: PointOnObject(g-3,g5)
FEATURE [Sketcher::SketchObject] Sketch136
  ArcFitTolerance = 1e-06
  AttachmentSupport = -> [Pocket029]
  ExternalGeometry = -> [Pocket029]
  FullyConstrained = true
  MakeInternals = false
  MapMode = 5
  Placement = pos=(39,0,0) rot=(0.57735,0.57735,0.57735;2.0944rad)
  sketch-geometry (7):
    g0: LineSegment StartX=0 StartY=0 StartZ=0 EndX=-3.2 EndY=0 EndZ=0
    g1: LineSegment [constr] StartX=-3.2 StartY=0 StartZ=0 EndX=-3.2 EndY=-3.2 EndZ=0
    g2: LineSegment StartX=-3.2 StartY=-3.2 StartZ=0 EndX=0 EndY=-3.2 EndZ=0
    g3: LineSegment StartX=0 StartY=-3.2 StartZ=0 EndX=0 EndY=0 EndZ=0
    g4: LineSegment StartX=-3.2 StartY=0 StartZ=0 EndX=-16 EndY=-7.68 EndZ=0
    g5: LineSegment StartX=-16 StartY=-7.68 StartZ=0 EndX=-16 EndY=-10.88 EndZ=0
    g6: LineSegment StartX=-16 StartY=-10.88 StartZ=0 EndX=-3.2 EndY=-3.2 EndZ=0
  constraints (19):
    c: Coincident(g0,g1)
    c: Coincident(g1,g2)
    c: Coincident(g2,g3)
    c: Coincident(g3,g0)
    c: Horizontal(g0)
    c: Horizontal(g2)
    c: Vertical(g1)
    c: Vertical(g3)
    c: Distance(g1,g3) = 3.2
    c: Coincident(g0,g-1)
    c: DistanceY(g1,g1) = 3.2
    c: Coincident(g0,g4)
    c: Coincident(g4,g5)
    c: Vertical(g5)
    c: Coincident(g5,g6)
    c: Coincident(g6,g1)
    c: Parallel(g4,g6)
    c: Parallel(g-3,g4)
    c: PointOnObject(g-3,g5)
FEATURE [Sketcher::SketchObject] Sketch137
  ArcFitTolerance = 1e-06
  AttachmentSupport = -> [Pocket028]
  ExternalGeometry = -> [Pocket028]
  FullyConstrained = true
  MakeInternals = false
  MapMode = 5
  Placement = pos=(7,0,0) rot=(0.57735,0.57735,0.57735;2.0944rad)
  sketch-geometry (7):
    g0: LineSegment StartX=0 StartY=0 StartZ=0 EndX=-3.2 EndY=0 EndZ=0
    g1: LineSegment [constr] StartX=-3.2 StartY=0 StartZ=0 EndX=-3.2 EndY=-3.2 EndZ=0
    g2: LineSegment StartX=-3.2 StartY=-3.2 StartZ=0 EndX=0 EndY=-3.2 EndZ=0
    g3: LineSegment StartX=0 StartY=-3.2 StartZ=0 EndX=0 EndY=0 EndZ=0
    g4: LineSegment StartX=-3.2 StartY=0 StartZ=0 EndX=-16 EndY=-7.68 EndZ=0
    g5: LineSegment StartX=-16 StartY=-7.68 StartZ=0 EndX=-16 EndY=-10.88 EndZ=0
    g6: LineSegment StartX=-16 StartY=-10.88 StartZ=0 EndX=-3.2 EndY=-3.2 EndZ=0
  constraints (19):
    c: Coincident(g0,g1)
    c: Coincident(g1,g2)
    c: Coincident(g2,g3)
    c: Coincident(g3,g0)
    c: Horizontal(g0)
    c: Horizontal(g2)
    c: Vertical(g1)
    c: Vertical(g3)
    c: Coincident(g0,g-1)
    c: DistanceX(g0,g0) = 3.2
    c: DistanceY(g1,g1) = 3.2
    c: Coincident(g0,g4)
    c: Coincident(g4,g5)
    c: Vertical(g5)
    c: Coincident(g5,g6)
    c: Coincident(g6,g1)
    c: Parallel(g6,g4)
    c: Parallel(g-3,g4)
    c: PointOnObject(g-3,g5)
FEATURE [Sketcher::SketchObject] Sketch138
  ArcFitTolerance = 1e-06
  AttachmentSupport = -> [Pocket010]
  ExternalGeometry = -> [Pocket010]
  FullyConstrained = true
  MakeInternals = false
  MapMode = 5
  Placement = pos=(0,24,0) rot=(1,0,0;1.5708rad)
  sketch-geometry (7):
    g0: LineSegment StartX=0 StartY=0 StartZ=0 EndX=-3.2 EndY=0 EndZ=0
    g1: LineSegment [constr] StartX=-3.2 StartY=0 StartZ=0 EndX=-3.2 EndY=-3.2 EndZ=0
    g2: LineSegment StartX=-3.2 StartY=-3.2 StartZ=0 EndX=0 EndY=-3.2 EndZ=0
    g3: LineSegment StartX=0 StartY=-3.2 StartZ=0 EndX=0 EndY=0 EndZ=0
    g4: LineSegment StartX=-3.2 StartY=0 StartZ=0 EndX=-16 EndY=-7.68 EndZ=0
    g5: LineSegment StartX=-16 StartY=-7.68 StartZ=0 EndX=-16 EndY=-10.88 EndZ=0
    g6: LineSegment StartX=-16 StartY=-10.88 StartZ=0 EndX=-3.2 EndY=-3.2 EndZ=0
  constraints (19):
    c: Coincident(g0,g1)
    c: Coincident(g1,g2)
    c: Coincident(g2,g3)
    c: Coincident(g3,g0)
    c: Horizontal(g0)
    c: Horizontal(g2)
    c: Vertical(g1)
    c: Vertical(g3)
    c: Distance(g1,g3) = 3.2
    c: Coincident(g0,g-1)
    c: DistanceY(g1,g1) = 3.2
    c: Coincident(g0,g4)
    c: Coincident(g4,g5)
    c: Vertical(g5)
    c: Coincident(g5,g6)
    c: Coincident(g6,g1)
    c: Parallel(g6,g4)
    c: Parallel(g-3,g4)
    c: PointOnObject(g-3,g5)
FEATURE [PartDesign::Pocket] Pocket047
  BaseFeature = -> Pocket010
  Direction = (0,1,-2e-16)
  Length = 16
  Length2 = 5
  Profile = -> Sketch138
  ReferenceAxis = -> Sketch138 [N_Axis]
  Refine = true
  Suppressed = false
  Type = 0
FEATURE [Sketcher::SketchObject] Sketch139
  ArcFitTolerance = 1e-06
  AttachmentSupport = -> [Pocket009]
  ExternalGeometry = -> [Pocket009]
  FullyConstrained = true
  MakeInternals = false
  MapMode = 5
  Placement = pos=(0,56,0) rot=(1,0,0;1.5708rad)
  sketch-geometry (7):
    g0: LineSegment StartX=0 StartY=0 StartZ=0 EndX=-3.2 EndY=0 EndZ=0
    g1: LineSegment [constr] StartX=-3.2 StartY=0 StartZ=0 EndX=-3.2 EndY=-3.2 EndZ=0
    g2: LineSegment StartX=-3.2 StartY=-3.2 StartZ=0 EndX=0 EndY=-3.2 EndZ=0
    g3: LineSegment StartX=0 StartY=-3.2 StartZ=0 EndX=0 EndY=0 EndZ=0
    g4: LineSegment StartX=-3.2 StartY=0 StartZ=0 EndX=-16 EndY=-7.68 EndZ=0
    g5: LineSegment StartX=-16 StartY=-7.68 StartZ=0 EndX=-16 EndY=-10.88 EndZ=0
    g6: LineSegment StartX=-16 StartY=-10.88 StartZ=0 EndX=-3.2 EndY=-3.2 EndZ=0
  constraints (19):
    c: Coincident(g0,g1)
    c: Coincident(g1,g2)
    c: Coincident(g2,g3)
    c: Coincident(g3,g0)
    c: Horizontal(g0)
    c: Horizontal(g2)
    c: Vertical(g1)
    c: Vertical(g3)
    c: Distance(g1,g3) = 3.2
    c: Coincident(g0,g-1)
    c: DistanceY(g1,g1) = 3.2
    c: Coincident(g0,g4)
    c: Coincident(g4,g5)
    c: Vertical(g5)
    c: Coincident(g5,g6)
    c: Coincident(g6,g1)
    c: Parallel(g4,g6)
    c: Parallel(g-3,g4)
    c: PointOnObject(g-3,g5)
FEATURE [Sketcher::SketchObject] Sketch140
  ArcFitTolerance = 1e-06
  AttachmentSupport = -> [Pocket008]
  ExternalGeometry = -> [Pocket008]
  FullyConstrained = true
  MakeInternals = false
  MapMode = 5
  Placement = pos=(0,88,0) rot=(1,0,0;1.5708rad)
  sketch-geometry (7):
    g0: LineSegment StartX=0 StartY=0 StartZ=0 EndX=-3.2 EndY=0 EndZ=0
    g1: LineSegment [constr] StartX=-3.2 StartY=0 StartZ=0 EndX=-3.2 EndY=-3.2 EndZ=0
    g2: LineSegment StartX=-3.2 StartY=-3.2 StartZ=0 EndX=0 EndY=-3.2 EndZ=0
    g3: LineSegment StartX=0 StartY=-3.2 StartZ=0 EndX=0 EndY=0 EndZ=0
    g4: LineSegment StartX=-3.2 StartY=0 StartZ=0 EndX=-16 EndY=-7.68 EndZ=0
    g5: LineSegment StartX=-16 StartY=-7.68 StartZ=0 EndX=-16 EndY=-10.88 EndZ=0
    g6: LineSegment StartX=-16 StartY=-10.88 StartZ=0 EndX=-3.2 EndY=-3.2 EndZ=0
  constraints (19):
    c: Coincident(g0,g1)
    c: Coincident(g1,g2)
    c: Coincident(g2,g3)
    c: Coincident(g3,g0)
    c: Horizontal(g0)
    c: Horizontal(g2)
    c: Vertical(g1)
    c: Vertical(g3)
    c: Distance(g1,g3) = 3.2
    c: Coincident(g0,g-1)
    c: DistanceY(g1,g1) = 3.2
    c: Coincident(g0,g4)
    c: Coincident(g4,g5)
    c: Vertical(g5)
    c: Coincident(g5,g6)
    c: Coincident(g6,g1)
    c: Parallel(g6,g4)
    c: Parallel(g4,g-3)
    c: PointOnObject(g-3,g5)
FEATURE [Sketcher::SketchObject] Sketch141
  ArcFitTolerance = 1e-06
  AttachmentSupport = -> [Pocket007]
  ExternalGeometry = -> [Pocket007]
  FullyConstrained = true
  MakeInternals = false
  MapMode = 5
  Placement = pos=(0,120,0) rot=(1,0,0;1.5708rad)
  sketch-geometry (7):
    g0: LineSegment StartX=0 StartY=0 StartZ=0 EndX=-3.2 EndY=0 EndZ=0
    g1: LineSegment [constr] StartX=-3.2 StartY=0 StartZ=0 EndX=-3.2 EndY=-3.2 EndZ=0
    g2: LineSegment StartX=-3.2 StartY=-3.2 StartZ=0 EndX=0 EndY=-3.2 EndZ=0
    g3: LineSegment StartX=0 StartY=-3.2 StartZ=0 EndX=0 EndY=0 EndZ=0
    g4: LineSegment StartX=-3.2 StartY=0 StartZ=0 EndX=-16 EndY=-7.68 EndZ=0
    g5: LineSegment StartX=-16 StartY=-7.68 StartZ=0 EndX=-16 EndY=-10.88 EndZ=0
    g6: LineSegment StartX=-16 StartY=-10.88 StartZ=0 EndX=-3.2 EndY=-3.2 EndZ=0
  constraints (19):
    c: Coincident(g0,g1)
    c: Coincident(g1,g2)
    c: Coincident(g2,g3)
    c: Coincident(g3,g0)
    c: Horizontal(g0)
    c: Horizontal(g2)
    c: Vertical(g1)
    c: Vertical(g3)
    c: Distance(g1,g3) = 3.2
    c: Coincident(g0,g-1)
    c: DistanceY(g1,g1) = 3.2
    c: Coincident(g0,g4)
    c: Coincident(g4,g5)
    c: Vertical(g5)
    c: Coincident(g5,g6)
    c: Coincident(g6,g1)
    c: Parallel(g4,g6)
    c: Parallel(g4,g-3)
    c: PointOnObject(g-3,g5)
FEATURE [Sketcher::SketchObject] Sketch142
  ArcFitTolerance = 1e-06
  AttachmentSupport = -> [Pad099]
  ExternalGeometry = -> [Pad099]
  FullyConstrained = true
  MakeInternals = false
  MapMode = 5
  Placement = pos=(0,2.2e-15,3.2) rot=(0,0,1;0rad)
  sketch-geometry (10):
    g0: LineSegment StartX=5.68e-14 StartY=135.8 StartZ=0 EndX=5.68e-14 EndY=-5.68e-14 EndZ=0
    g1: LineSegment StartX=5.68e-14 StartY=-6.97e-14 StartZ=0 EndX=127.8 EndY=-6.97e-14 EndZ=0
    g2: LineSegment StartX=127.8 StartY=-6.97e-14 StartZ=0 EndX=127.8 EndY=135.8 EndZ=0
    g3: LineSegment StartX=-3.2 StartY=135.8 StartZ=0 EndX=-3.2 EndY=-3.2 EndZ=0
    g4: LineSegment StartX=-3.2 StartY=-3.2 StartZ=0 EndX=131 EndY=-3.2 EndZ=0
    g5: LineSegment StartX=131 StartY=-3.2 StartZ=0 EndX=131 EndY=135.8 EndZ=0
    g6: LineSegment [constr] StartX=5.68e-14 StartY=-6.97e-14 StartZ=0 EndX=-3.2 EndY=-3.2 EndZ=0
    g7: LineSegment [constr] StartX=127.8 StartY=-6.97e-14 StartZ=0 EndX=131 EndY=-3.2 EndZ=0
    g8: LineSegment StartX=-3.2 StartY=135.8 StartZ=0 EndX=5.68e-14 EndY=135.8 EndZ=0
    g9: LineSegment StartX=131 StartY=135.8 StartZ=0 EndX=127.8 EndY=135.8 EndZ=0
  constraints (25):
    c: Coincident(g0,g1)
    c: Coincident(g1,g2)
    c: Vertical(g0)
    c: Horizontal(g1)
    c: Coincident(g3,g4)
    c: Coincident(g4,g5)
    c: Vertical(g3)
    c: Vertical(g5)
    c: Horizontal(g4)
    c: Coincident(g6,g1)
    c: Coincident(g6,g4)
    c: Coincident(g7,g2)
    c: Coincident(g7,g5)
    c: Perpendicular(g6,g7)
    c: Distance(g3,g0) = 3.2
    c: Coincident(g0,g-3)
    c: Coincident(g1,g-4)
    c: Coincident(g8,g3)
    c: Coincident(g8,g0)
    c: Coincident(g9,g5)
    c: Coincident(g9,g2)
    c: Horizontal(g9)
    c: Coincident(g2,g-3)
    c: Horizontal(g8)
    c: DistanceX(g2,g5) = 3.2
FEATURE [PartDesign::Pad] Pad101
  BaseFeature = -> Pad099
  Direction = (0,0,1)
  Length = 3.2
  Length2 = 10
  Profile = -> Sketch142
  ReferenceAxis = -> Sketch142 [N_Axis]
  Refine = true
  Reversed = true
  Suppressed = false
  Type = 0
FEATURE [PartDesign::Body] Body062  label="cover embossed"
  AllowCompound = false
  BaseFeature = -> Cut013
  Group = -> [BaseFeature001,Sketch106,Pocket024,Pad098,Sketch125,Sketch126,Pocket035,Pad099,Sketch142,Pad101]
  Origin = -> Origin336
  Tip = -> Pad101
FEATURE [PartDesign::SubShapeBinder] Binder031
  BindCopyOnChange = 0
  BindMode = 0
  ClaimChildren = false
  Context = -> Part001 [Body071.Binder031.]
  Fuse = false
  MakeFace = true
  OffsetFill = false
  OffsetIntersection = false
  OffsetJoinType = 0
  OffsetOpenResult = false
  PartialLoad = false
  Refine = true
  Relative = true
  Support = -> [Body003,Body004,Body005,Body006,Body007,Body008,Body009,Body010,Body011,Body012,Body013,Body014,Body002]
  _Version = 2
FEATURE [Sketcher::SketchObject] Sketch167
  ArcFitTolerance = 1e-06
  FullyConstrained = true
  MakeInternals = false
  MapMode = 5
  Placement = pos=(1.4e-15,8,0) rot=(0,0.707107,0.707107;3.14159rad)
  sketch-geometry (7):
    g0: LineSegment StartX=0 StartY=0 StartZ=0 EndX=0 EndY=-3.2 EndZ=0
    g1: LineSegment StartX=0 StartY=-3.2 StartZ=0 EndX=3.2 EndY=-3.2 EndZ=0
    g2: LineSegment [constr] StartX=3.2 StartY=-3.2 StartZ=0 EndX=3.2 EndY=0 EndZ=0
    g3: LineSegment StartX=3.2 StartY=0 StartZ=0 EndX=0 EndY=0 EndZ=0
    g4: LineSegment StartX=3.2 StartY=0 StartZ=0 EndX=16 EndY=-7.68 EndZ=0
    g5: LineSegment StartX=16 StartY=-7.68 StartZ=0 EndX=16 EndY=-10.88 EndZ=0
    g6: LineSegment StartX=16 StartY=-10.88 StartZ=0 EndX=3.2 EndY=-3.2 EndZ=0
  constraints (19):
    c: Coincident(g0,g1)
    c: Coincident(g1,g2)
    c: Coincident(g2,g3)
    c: Coincident(g3,g0)
    c: Vertical(g0)
    c: Vertical(g2)
    c: Horizontal(g1)
    c: Horizontal(g3)
    c: Distance(g0,g2) = 3.2
    c: Distance(g1,g3) = 3.2
    c: Coincident(g0,g-1)
    c: Coincident(g2,g4)
    c: Coincident(g4,g5)
    c: Vertical(g5)
    c: Coincident(g5,g6)
    c: Coincident(g6,g1)
    c: Parallel(g4,g6)
    c: Parallel(g4,g-3)
    c: PointOnObject(g-3,g5)
FEATURE [PartDesign::Pad] Pad128
  BaseFeature = -> Pocket001
  Direction = (0,1,-2e-16)
  Length = 15.8
  Length2 = 10
  Profile = -> Sketch128
  ReferenceAxis = -> Sketch128 [N_Axis]
  Refine = true
  Reversed = true
  Suppressed = false
  Type = 0
FEATURE [PartDesign::Body] Body002  label="Pillar 1"
  AllowCompound = false
  Group = -> [Binder001,Sketch006,Pad005,Sketch007,Pocket001,Sketch128,Pad128]
  Origin = -> Origin002
  Tip = -> Pad128
FEATURE [PartDesign::Pad] Pad129
  BaseFeature = -> Pocket002
  Direction = (0,1,-2e-16)
  Length = 16
  Length2 = 10
  Profile = -> Sketch129
  ReferenceAxis = -> Sketch129 [N_Axis]
  Refine = true
  Reversed = true
  Suppressed = false
  Type = 0
FEATURE [PartDesign::Body] Body003  label="Pillar 2"
  AllowCompound = false
  Group = -> [Binder002,Sketch008,Pad006,Sketch009,Pocket002,Sketch129,Pad129]
  Origin = -> Origin003
  Tip = -> Pad129
FEATURE [PartDesign::Pad] Pad130
  BaseFeature = -> Pocket003
  Direction = (0,1,-2e-16)
  Length = 16
  Length2 = 10
  Profile = -> Sketch130
  ReferenceAxis = -> Sketch130 [N_Axis]
  Refine = true
  Reversed = true
  Suppressed = false
  Type = 0
FEATURE [PartDesign::Body] Body004  label="Pillar 3"
  AllowCompound = false
  Group = -> [Binder003,Sketch010,Pad007,Sketch011,Pocket003,Sketch130,Pad130]
  Origin = -> Origin004
  Tip = -> Pad130
FEATURE [PartDesign::Pad] Pad131
  BaseFeature = -> Pocket004
  Direction = (0,1,-2e-16)
  Length = 16
  Length2 = 10
  Profile = -> Sketch131
  ReferenceAxis = -> Sketch131 [N_Axis]
  Refine = true
  Reversed = true
  Suppressed = false
  Type = 0
FEATURE [PartDesign::Body] Body005  label="Pillar 4"
  AllowCompound = false
  Group = -> [Binder004,Sketch012,Pad008,Sketch013,Pocket004,Sketch131,Pad131]
  Origin = -> Origin005
  Tip = -> Pad131
FEATURE [PartDesign::Pad] Pad132
  BaseFeature = -> Pocket027
  Direction = (0,1,-2e-16)
  Length = 24
  Length2 = 10
  Profile = -> Sketch132
  ReferenceAxis = -> Sketch132 [N_Axis]
  Refine = true
  Reversed = true
  Suppressed = false
  Type = 0
FEATURE [PartDesign::Pad] Pad133
  BaseFeature = -> Pad132
  Direction = (-1,0,0)
  Length = 23
  Length2 = 10
  Profile = -> Sketch133
  ReferenceAxis = -> Sketch133 [N_Axis]
  Refine = true
  Reversed = true
  Suppressed = false
  Type = 0
FEATURE [Sketcher::SketchObject] Sketch168
  ArcFitTolerance = 1e-06
  AttachmentSupport = -> [Pad133]
  ExternalGeometry = -> [Pad133]
  FullyConstrained = true
  MakeInternals = false
  MapMode = 5
  Placement = pos=(0,8,0) rot=(0,0.707107,0.707107;3.14159rad)
  sketch-geometry (3):
    g0: LineSegment StartX=-131 StartY=0 StartZ=0 EndX=-143.8 EndY=-7.68 EndZ=0
    g1: LineSegment StartX=-143.8 StartY=-7.68 StartZ=0 EndX=-143.8 EndY=0 EndZ=0
    g2: LineSegment StartX=-143.8 StartY=0 StartZ=0 EndX=-131 EndY=0 EndZ=0
  constraints (7):
    c: Coincident(g-3,g0)
    c: Coincident(g0,g-3)
    c: Coincident(g0,g1)
    c: PointOnObject(g1,g-1)
    c: Vertical(g1)
    c: Coincident(g1,g2)
    c: Coincident(g2,g0)
FEATURE [PartDesign::Pocket] Pocket054
  BaseFeature = -> Pad133
  Direction = (0,-1,2e-16)
  Length = 30
  Length2 = 5
  Profile = -> Sketch168
  ReferenceAxis = -> Sketch168 [N_Axis]
  Refine = true
  Suppressed = false
  Type = 0
FEATURE [Sketcher::SketchObject] Sketch169
  ArcFitTolerance = 1e-06
  AttachmentSupport = -> [Pocket054]
  ExternalGeometry = -> [Pocket054]
  FullyConstrained = true
  MakeInternals = false
  MapMode = 5
  Placement = pos=(120.8,0,0) rot=(0.57735,-0.57735,-0.57735;2.0944rad)
  sketch-geometry (3):
    g0: LineSegment StartX=3.2 StartY=0 StartZ=0 EndX=16 EndY=-7.68 EndZ=0
    g1: LineSegment StartX=16 StartY=-7.68 StartZ=0 EndX=16 EndY=0 EndZ=0
    g2: LineSegment StartX=16 StartY=0 StartZ=0 EndX=3.2 EndY=0 EndZ=0
  constraints (7):
    c: Coincident(g-3,g0)
    c: Coincident(g0,g-3)
    c: Coincident(g0,g1)
    c: PointOnObject(g1,g-1)
    c: Vertical(g1)
    c: Coincident(g1,g2)
    c: Coincident(g2,g0)
FEATURE [PartDesign::Pocket] Pocket055
  BaseFeature = -> Pocket054
  Direction = (1,0,0)
  Length = 26
  Length2 = 5
  Profile = -> Sketch169
  ReferenceAxis = -> Sketch169 [N_Axis]
  Refine = true
  Suppressed = false
  Type = 0
FEATURE [PartDesign::Body] Body006  label="Pillar 5"
  AllowCompound = false
  Group = -> [Binder005,Sketch014,Pad009,Sketch015,Pocket005,Sketch016,Pocket006,Sketch111,Pocket027,Sketch132,Sketch133,Pad132,Pad133,Sketch168,Pocket054,Sketch169,Pocket055]
  Origin = -> Origin006
  Tip = -> Pocket055
FEATURE [PartDesign::Pad] Pad134
  BaseFeature = -> Pocket031
  Direction = (1,0,0)
  Length = 14
  Length2 = 10
  Profile = -> Sketch134
  ReferenceAxis = -> Sketch134 [N_Axis]
  Refine = true
  Reversed = true
  Suppressed = false
  Type = 0
FEATURE [PartDesign::Body] Body014  label="Pillar 13"
  AllowCompound = false
  Group = -> [Binder013,Sketch032,Pad017,Sketch033,Pocket015,Sketch115,Pocket031,Sketch134,Pad134]
  Origin = -> Origin014
  Tip = -> Pad134
FEATURE [PartDesign::Pad] Pad135
  BaseFeature = -> Pocket030
  Direction = (1,0,0)
  Length = 14
  Length2 = 10
  Profile = -> Sketch135
  ReferenceAxis = -> Sketch135 [N_Axis]
  Refine = true
  Reversed = true
  Suppressed = false
  Type = 0
FEATURE [PartDesign::Body] Body013  label="Pillar 12"
  AllowCompound = false
  Group = -> [Binder012,Sketch030,Pad016,Sketch031,Pocket014,Sketch114,Pocket030,Sketch135,Pad135]
  Origin = -> Origin013
  Tip = -> Pad135
FEATURE [PartDesign::Pad] Pad136
  BaseFeature = -> Pocket029
  Direction = (1,0,0)
  Length = 14
  Length2 = 10
  Profile = -> Sketch136
  ReferenceAxis = -> Sketch136 [N_Axis]
  Refine = true
  Reversed = true
  Suppressed = false
  Type = 0
FEATURE [PartDesign::Body] Body012  label="Pillar 11"
  AllowCompound = false
  Group = -> [Binder011,Sketch028,Pad015,Sketch029,Pocket013,Sketch113,Pocket029,Sketch136,Pad136]
  Origin = -> Origin012
  Tip = -> Pad136
FEATURE [PartDesign::Pad] Pad137
  BaseFeature = -> Pocket007
  Direction = (0,-1,2e-16)
  Length = 15.8
  Length2 = 10
  Profile = -> Sketch141
  ReferenceAxis = -> Sketch141 [N_Axis]
  Refine = true
  Reversed = true
  Suppressed = false
  Type = 0
FEATURE [PartDesign::Body] Body007  label="Pillar 6"
  AllowCompound = false
  Group = -> [Binder006,Sketch017,Pad010,Sketch018,Pocket007,Sketch141,Pad137]
  Origin = -> Origin007
  Tip = -> Pad137
FEATURE [PartDesign::Pad] Pad138
  BaseFeature = -> Pocket008
  Direction = (0,-1,2e-16)
  Length = 16
  Length2 = 10
  Profile = -> Sketch140
  ReferenceAxis = -> Sketch140 [N_Axis]
  Refine = true
  Reversed = true
  Suppressed = false
  Type = 0
FEATURE [PartDesign::Body] Body008  label="Pillar 7"
  AllowCompound = false
  Group = -> [Binder007,Sketch019,Pad011,Sketch020,Pocket008,Sketch140,Pad138]
  Origin = -> Origin008
  Tip = -> Pad138
FEATURE [PartDesign::Pad] Pad139
  BaseFeature = -> Pocket009
  Direction = (0,-1,2e-16)
  Length = 16
  Length2 = 10
  Profile = -> Sketch139
  ReferenceAxis = -> Sketch139 [N_Axis]
  Refine = true
  Reversed = true
  Suppressed = false
  Type = 0
FEATURE [PartDesign::Body] Body009  label="Pillar 8"
  AllowCompound = false
  Group = -> [Binder008,Sketch021,Pad012,Sketch022,Pocket009,Sketch139,Pad139]
  Origin = -> Origin009
  Tip = -> Pad139
FEATURE [PartDesign::Pad] Pad140
  BaseFeature = -> Pocket047
  Direction = (0,-1,2e-16)
  Length = 16
  Length2 = 10
  Profile = -> Sketch138
  ReferenceAxis = -> Sketch138 [N_Axis]
  Refine = true
  Reversed = true
  Suppressed = false
  Type = 0
FEATURE [PartDesign::Body] Body010  label="Pillar 9"
  AllowCompound = false
  Group = -> [Binder009,Sketch023,Pad013,Sketch024,Pocket010,Sketch138,Pocket047,Pad140]
  Origin = -> Origin010
  Tip = -> Pad140
FEATURE [PartDesign::Pad] Pad141
  BaseFeature = -> Pocket028
  Direction = (1,0,0)
  Length = 23
  Length2 = 10
  Profile = -> Sketch137
  ReferenceAxis = -> Sketch137 [N_Axis]
  Refine = true
  Reversed = true
  Suppressed = false
  Type = 0
FEATURE [PartDesign::Pad] Pad142
  BaseFeature = -> Pad141
  Direction = (0,1,-2e-16)
  Length = 24
  Length2 = 10
  Profile = -> Sketch167
  ReferenceAxis = -> Sketch167 [N_Axis]
  Refine = true
  Reversed = true
  Suppressed = false
  Type = 0
FEATURE [Sketcher::SketchObject] Sketch170
  ArcFitTolerance = 1e-06
  AttachmentSupport = -> [Pad142]
  ExternalGeometry = -> [Pad142]
  FullyConstrained = true
  MakeInternals = false
  MapMode = 5
  Placement = pos=(0,8,0) rot=(0,0.707107,0.707107;3.14159rad)
  sketch-geometry (3):
    g0: LineSegment StartX=3.2 StartY=0 StartZ=0 EndX=16 EndY=-7.68 EndZ=0
    g1: LineSegment StartX=16 StartY=-7.68 StartZ=0 EndX=16 EndY=0 EndZ=0
    g2: LineSegment StartX=16 StartY=0 StartZ=0 EndX=3.2 EndY=0 EndZ=0
  constraints (7):
    c: Coincident(g-3,g0)
    c: Coincident(g0,g-3)
    c: Coincident(g0,g1)
    c: PointOnObject(g1,g-1)
    c: Vertical(g1)
    c: Coincident(g1,g2)
    c: Coincident(g2,g0)
FEATURE [PartDesign::Pocket] Pocket056
  BaseFeature = -> Pad142
  Direction = (0,-1,2e-16)
  Length = 24
  Length2 = 5
  Profile = -> Sketch170
  ReferenceAxis = -> Sketch170 [N_Axis]
  Refine = true
  Suppressed = false
  Type = 0
FEATURE [Sketcher::SketchObject] Sketch171
  ArcFitTolerance = 1e-06
  AttachmentSupport = -> [Pocket056]
  ExternalGeometry = -> [Pocket056]
  FullyConstrained = true
  MakeInternals = false
  MapMode = 5
  Placement = pos=(7,0,0) rot=(0.57735,0.57735,0.57735;2.0944rad)
  sketch-geometry (3):
    g0: LineSegment StartX=-3.2 StartY=0 StartZ=0 EndX=-16 EndY=-7.68 EndZ=0
    g1: LineSegment StartX=-16 StartY=-7.68 StartZ=0 EndX=-16 EndY=0 EndZ=0
    g2: LineSegment StartX=-16 StartY=0 StartZ=0 EndX=-3.2 EndY=0 EndZ=0
  constraints (7):
    c: Coincident(g-3,g0)
    c: Coincident(g0,g-3)
    c: Coincident(g0,g1)
    c: PointOnObject(g1,g-1)
    c: Vertical(g1)
    c: Coincident(g1,g2)
    c: Coincident(g2,g0)
FEATURE [PartDesign::Pocket] Pocket057
  BaseFeature = -> Pocket056
  Direction = (-1,0,0)
  Length = 23
  Length2 = 5
  Profile = -> Sketch171
  ReferenceAxis = -> Sketch171 [N_Axis]
  Refine = true
  Suppressed = false
  Type = 0
FEATURE [PartDesign::Body] Body011  label="Pillar 10"
  AllowCompound = false
  Group = -> [Binder010,Sketch025,Pad014,Sketch026,Pocket011,Sketch027,Pocket012,Sketch112,Pocket028,Sketch137,Sketch167,Pad141,Pad142,Sketch170,Pocket056,Sketch171,Pocket057]
  Origin = -> Origin011
  Tip = -> Pocket057
FEATURE [TechDraw::DrawProjGroupItem] View001
  CoarseView = false
  Direction = (0,0,1)
  Focus = 100
  HardHidden = false
  IsoCount = 0
  IsoHidden = false
  IsoVisible = false
  LockPosition = false
  Perspective = false
  Rotation = 0
  RotationVector = (1,0,0)
  ScaleType = 0
  ScrubCount = 1
  SeamHidden = false
  SeamVisible = true
  SmoothHidden = false
  SmoothVisible = true
  Source = -> [Body,Body001,Body002,Body003,Body004,Body005,Body006,Body007,Body008,Body009,Body010,Body011,Body012,Body013,Body014]
  Type = 0
  X = 110.905
  XDirection = (1,0,0)
  Y = 115.011
FEATURE [TechDraw::DrawViewDimension] Dimension006
  AngleOverride = false
  Arbitrary = false
  ArbitraryTolerances = false
  BoxCorners = (2) [(-79.9,-75.9,0),(79.9,75.9,0)]
  EqualTolerance = true
  ExtensionAngle = 0
  FormatSpec = %.2f
  FormatSpecOverTolerance = %+.2f
  FormatSpecUnderTolerance = %+.2f
  Inverted = false
  LineAngle = 0
  LockPosition = false
  MeasureType = 1
  OverTolerance = 0
  References2D = -> [View001]
  Rotation = 0
  ScaleType = 0
  TheoreticalExact = false
  Type = 1
  UnderTolerance = 0
  X = -41.1698
  Y = 86.4342
FEATURE [TechDraw::DrawViewDimension] Dimension007
  AngleOverride = false
  Arbitrary = false
  ArbitraryTolerances = false
  BoxCorners = (2) [(-79.9,-75.9,0),(79.9,75.9,0)]
  EqualTolerance = true
  ExtensionAngle = 0
  FormatSpec = %.2f
  FormatSpecOverTolerance = %+.2f
  FormatSpecUnderTolerance = %+.2f
  Inverted = false
  LineAngle = 0
  LockPosition = false
  MeasureType = 1
  OverTolerance = 0
  References2D = -> [View001]
  Rotation = 0
  ScaleType = 0
  TheoreticalExact = false
  Type = 1
  UnderTolerance = 0
  X = 50.9277
  Y = 86.4342
FEATURE [TechDraw::DrawViewDimension] Dimension008
  AngleOverride = false
  Arbitrary = false
  ArbitraryTolerances = false
  BoxCorners = (2) [(-79.9,-75.9,0),(79.9,75.9,0)]
  EqualTolerance = true
  ExtensionAngle = 0
  FormatSpec = %.2f
  FormatSpecOverTolerance = %+.2f
  FormatSpecUnderTolerance = %+.2f
  Inverted = false
  LineAngle = 0
  LockPosition = false
  MeasureType = 1
  OverTolerance = 0
  References2D = -> [View001]
  Rotation = 0
  ScaleType = 0
  TheoreticalExact = false
  Type = 2
  UnderTolerance = 0
  X = -98.1943
  Y = 59.9617
FEATURE [TechDraw::DrawViewDimension] Dimension009
  AngleOverride = false
  Arbitrary = false
  ArbitraryTolerances = false
  BoxCorners = (2) [(-79.9,-75.9,0),(79.9,75.9,0)]
  EqualTolerance = true
  ExtensionAngle = 0
  FormatSpec = %.2f
  FormatSpecOverTolerance = %+.2f
  FormatSpecUnderTolerance = %+.2f
  Inverted = false
  LineAngle = 0
  LockPosition = false
  MeasureType = 1
  OverTolerance = 0
  References2D = -> [View001]
  Rotation = 0
  ScaleType = 0
  TheoreticalExact = false
  Type = 2
  UnderTolerance = 0
  X = -98.1943
  Y = -36.05
FEATURE [TechDraw::DrawViewDimension] Dimension010
  AngleOverride = false
  Arbitrary = false
  ArbitraryTolerances = false
  BoxCorners = (2) [(-79.9,-75.9,0),(79.9,75.9,0)]
  EqualTolerance = true
  ExtensionAngle = 0
  FormatSpec = %.2f
  FormatSpecOverTolerance = %+.2f
  FormatSpecUnderTolerance = %+.2f
  Inverted = false
  LineAngle = 0
  LockPosition = false
  MeasureType = 1
  OverTolerance = 0
  References2D = -> [View001]
  Rotation = 0
  ScaleType = 0
  TheoreticalExact = false
  Type = 1
  UnderTolerance = 0
  X = -6.0851
  Y = -100.653
FEATURE [TechDraw::DrawViewDimension] Dimension011
  AngleOverride = false
  Arbitrary = false
  ArbitraryTolerances = false
  BoxCorners = (2) [(-79.9,-75.9,0),(79.9,75.9,0)]
  EqualTolerance = true
  ExtensionAngle = 0
  FormatSpec = %.2f
  FormatSpecOverTolerance = %+.2f
  FormatSpecUnderTolerance = %+.2f
  Inverted = false
  LineAngle = 0
  LockPosition = false
  MeasureType = 1
  OverTolerance = 0
  References2D = -> [View001]
  Rotation = 0
  ScaleType = 0
  TheoreticalExact = false
  Type = 2
  UnderTolerance = 0
  X = 108.608
  Y = 25.7032
FEATURE [TechDraw::DrawPage] Page001  label="TOP"
  KeepUpdated = true
  NextBalloonIndex = 1
  ProjectionType = 0
  Template = -> Template001
  Views = -> [View001,Dimension006,Dimension007,Dimension008,Dimension009,Dimension010,Dimension011]
FEATURE [TechDraw::DrawProjGroupItem] View
  CoarseView = false
  Direction = (0,-1,0)
  Focus = 100
  HardHidden = false
  IsoCount = 0
  IsoHidden = false
  IsoVisible = false
  LockPosition = false
  Perspective = false
  Rotation = 0
  RotationVector = (1,0,0)
  ScaleType = 0
  ScrubCount = 1
  SeamHidden = false
  SeamVisible = true
  SmoothHidden = false
  SmoothVisible = true
  Source = -> [Body001,Body002,Body003,Body004,Body005,Body006,Body007,Body008,Body009,Body010,Body011,Body012,Body013,Body014]
  Type = 0
  X = 98.9035
  XDirection = (1,0,0)
  Y = 183.904
FEATURE [TechDraw::DrawViewSection] SectionView  label="Section  - "
  BaseView = -> View
  CoarseView = false
  CutSurfaceDisplay = 2
  Direction = (1e-16,0,1)
  FileGeomPattern = /Applications/FreeCAD.app/Contents/Resources/share/Mod/TechDraw/PAT/FCPAT.pat
  FileHatchPattern = /Applications/FreeCAD.app/Contents/Resources/share/Mod/TechDraw/Patterns/simple.svg
  Focus = 100
  FuseBeforeCut = false
  HardHidden = false
  HatchOffset = (0,0,0)
  HatchRotation = 0
  HatchScale = 1
  IsoCount = 0
  IsoHidden = false
  IsoVisible = false
  LockPosition = false
  NameGeomPattern = Diamond
  Perspective = false
  Rotation = 0
  ScaleType = 0
  ScrubCount = 1
  SeamHidden = false
  SeamVisible = true
  SectionDirection = 4
  SectionLineStretch = 1
  SectionNormal = (1e-16,0,1)
  SectionOrigin = (63.9,59.9,-21.6)
  SmoothHidden = false
  SmoothVisible = true
  Source = -> [Body001,Body002,Body003,Body004,Body005,Body006,Body007,Body008,Body009,Body010,Body011,Body012,Body013,Body014]
  TrimAfterCut = false
  UsePreviousCut = false
  X = 111.077
  XDirection = (1,0,-1e-16)
  Y = 87.6412
FEATURE [TechDraw::DrawPage] Page  label="Querschnitt Case"
  KeepUpdated = true
  NextBalloonIndex = 1
  ProjectionType = 0
  Template = -> Template
  Views = -> [View,SectionView]
FEATURE [Sketcher::SketchObject] Sketch172
  ArcFitTolerance = 1e-06
  AttachmentSupport = -> [Pocket036]
  ExternalGeometry = -> [Pocket036]
  FullyConstrained = true
  MakeInternals = false
  MapMode = 5
  Placement = pos=(127.8,0,0) rot=(0.57735,0.57735,0.57735;2.0944rad)
  sketch-geometry (37):
    g0: LineSegment StartX=135.8 StartY=-28.8 StartZ=0 EndX=135.8 EndY=-27.2 EndZ=0
    g1: LineSegment StartX=135.8 StartY=-27.2 StartZ=0 EndX=0 EndY=-27.2 EndZ=0
    g2: LineSegment StartX=0 StartY=-27.2 StartZ=0 EndX=0 EndY=-28.8 EndZ=0
    g3: LineSegment StartX=0 StartY=-28.8 StartZ=0 EndX=135.8 EndY=-28.8 EndZ=0
    g4: LineSegment StartX=135.8 StartY=-25.6 StartZ=0 EndX=135.8 EndY=-24 EndZ=0
    g5: LineSegment StartX=135.8 StartY=-24 StartZ=0 EndX=0 EndY=-24 EndZ=0
    g6: LineSegment StartX=0 StartY=-24 StartZ=0 EndX=0 EndY=-25.6 EndZ=0
    g7: LineSegment StartX=0 StartY=-25.6 StartZ=0 EndX=135.8 EndY=-25.6 EndZ=0
    g8: LineSegment StartX=135.8 StartY=-22.4 StartZ=0 EndX=135.8 EndY=-20.8 EndZ=0
    g9: LineSegment StartX=135.8 StartY=-20.8 StartZ=0 EndX=0 EndY=-20.8 EndZ=0
    g10: LineSegment StartX=0 StartY=-20.8 StartZ=0 EndX=0 EndY=-22.4 EndZ=0
    g11: LineSegment StartX=0 StartY=-22.4 StartZ=0 EndX=135.8 EndY=-22.4 EndZ=0
    g12: LineSegment StartX=135.8 StartY=-19.2 StartZ=0 EndX=135.8 EndY=-17.6 EndZ=0
    g13: LineSegment StartX=135.8 StartY=-17.6 StartZ=0 EndX=0 EndY=-17.6 EndZ=0
    g14: LineSegment StartX=0 StartY=-17.6 StartZ=0 EndX=0 EndY=-19.2 EndZ=0
    g15: LineSegment StartX=0 StartY=-19.2 StartZ=0 EndX=135.8 EndY=-19.2 EndZ=0
    g16: LineSegment StartX=135.8 StartY=-16 StartZ=0 EndX=135.8 EndY=-14.4 EndZ=0
    g17: LineSegment StartX=135.8 StartY=-14.4 StartZ=0 EndX=-3.2 EndY=-14.4 EndZ=0
    g18: LineSegment StartX=-3.2 StartY=-14.4 StartZ=0 EndX=-3.2 EndY=-16 EndZ=0
    g19: LineSegment StartX=-3.2 StartY=-16 StartZ=0 EndX=135.8 EndY=-16 EndZ=0
    g20: LineSegment [constr] StartX=-3.2 StartY=-14.4 StartZ=0 EndX=-3.2 EndY=0 EndZ=0
    g21: LineSegment StartX=135.8 StartY=-12.8 StartZ=0 EndX=135.8 EndY=-11.2 EndZ=0
    g22: LineSegment StartX=135.8 StartY=-11.2 StartZ=0 EndX=-3.2 EndY=-11.2 EndZ=0
    g23: LineSegment StartX=-3.2 StartY=-11.2 StartZ=0 EndX=-3.2 EndY=-12.8 EndZ=0
    g24: LineSegment StartX=-3.2 StartY=-12.8 StartZ=0 EndX=135.8 EndY=-12.8 EndZ=0
    g25: LineSegment StartX=135.8 StartY=-9.6 StartZ=0 EndX=135.8 EndY=-8 EndZ=0
    g26: LineSegment StartX=135.8 StartY=-8 StartZ=0 EndX=-3.2 EndY=-8 EndZ=0
    g27: LineSegment StartX=-3.2 StartY=-8 StartZ=0 EndX=-3.2 EndY=-9.6 EndZ=0
    g28: LineSegment StartX=-3.2 StartY=-9.6 StartZ=0 EndX=135.8 EndY=-9.6 EndZ=0
    g29: LineSegment StartX=135.8 StartY=-6.4 StartZ=0 EndX=135.8 EndY=-4.8 EndZ=0
    g30: LineSegment StartX=135.8 StartY=-4.8 StartZ=0 EndX=-3.2 EndY=-4.8 EndZ=0
    g31: LineSegment StartX=-3.2 StartY=-4.8 StartZ=0 EndX=-3.2 EndY=-6.4 EndZ=0
    g32: LineSegment StartX=-3.2 StartY=-6.4 StartZ=0 EndX=135.8 EndY=-6.4 EndZ=0
    g33: LineSegment StartX=135.8 StartY=-3.2 StartZ=0 EndX=135.8 EndY=-1.6 EndZ=0
    g34: LineSegment StartX=135.8 StartY=-1.6 StartZ=0 EndX=-3.2 EndY=-1.6 EndZ=0
    g35: LineSegment StartX=-3.2 StartY=-1.6 StartZ=0 EndX=-3.2 EndY=-3.2 EndZ=0
    g36: LineSegment StartX=-3.2 StartY=-3.2 StartZ=0 EndX=135.8 EndY=-3.2 EndZ=0
  constraints (110):
    c: Coincident(g0,g1)
    c: Coincident(g1,g2)
    c: Coincident(g2,g3)
    c: Coincident(g3,g0)
    c: Vertical(g0)
    c: Vertical(g2)
    c: Horizontal(g1)
    c: Horizontal(g3)
    c: Distance(g1,g3) = 1.6
    c: Coincident(g0,g-3)
    c: PointOnObject(g1,g-4)
    c: Coincident(g4,g5)
    c: Coincident(g5,g6)
    c: Coincident(g6,g7)
    c: Coincident(g7,g4)
    c: Vertical(g4)
    c: Vertical(g6)
    c: Horizontal(g5)
    c: Horizontal(g7)
    c: Distance(g5,g7) = 1.6
    c: PointOnObject(g4,g-3)
    c: PointOnObject(g5,g-4)
    c: DistanceY(g0,g4) = 1.6
    c: Coincident(g8,g9)
    c: Coincident(g9,g10)
    c: Coincident(g10,g11)
    c: Coincident(g11,g8)
    c: Vertical(g8)
    c: Vertical(g10)
    c: Horizontal(g9)
    c: Horizontal(g11)
    c: Distance(g9,g11) = 1.6
    c: PointOnObject(g8,g-3)
    c: PointOnObject(g9,g-4)
    c: Coincident(g12,g13)
    c: Coincident(g13,g14)
    c: Coincident(g14,g15)
    c: Coincident(g15,g12)
    c: Vertical(g12)
    c: Vertical(g14)
    c: Horizontal(g13)
    c: Horizontal(g15)
    c: Distance(g13,g15) = 1.6
    c: PointOnObject(g12,g-3)
    c: PointOnObject(g13,g-4)
    c: Coincident(g16,g17)
    c: Coincident(g17,g18)
    c: Coincident(g18,g19)
    c: Coincident(g19,g16)
    c: Vertical(g16)
    c: Vertical(g18)
    c: Horizontal(g17)
    c: Horizontal(g19)
    c: Distance(g17,g19) = 1.6
    c: PointOnObject(g16,g-3)
    c: DistanceY(g4,g8) = 1.6
    c: DistanceY(g8,g12) = 1.6
    c: DistanceY(g12,g16) = 1.6
    c: DistanceX(g18,g13) = 3.2
    c: Coincident(g20,g17)
    c: PointOnObject(g20,g-1)
    c: Vertical(g20)
    c: Coincident(g21,g22)
    c: Coincident(g22,g23)
    c: Coincident(g23,g24)
    c: Coincident(g24,g21)
    c: Vertical(g21)
    c: Vertical(g23)
    c: Horizontal(g22)
    c: Horizontal(g24)
    c: Distance(g22,g24) = 1.6
    c: PointOnObject(g21,g-3)
    c: PointOnObject(g22,g20)
    c: Coincident(g25,g26)
    c: Coincident(g26,g27)
    c: Coincident(g27,g28)
    c: Coincident(g28,g25)
    c: Vertical(g25)
    c: Vertical(g27)
    c: Horizontal(g26)
    c: Horizontal(g28)
    c: Distance(g26,g28) = 1.6
    c: PointOnObject(g25,g-3)
    c: PointOnObject(g26,g20)
    c: DistanceY(g16,g21) = 1.6
    c: DistanceY(g21,g25) = 1.6
    c: Coincident(g29,g30)
    c: Coincident(g30,g31)
    c: Coincident(g31,g32)
    c: Coincident(g32,g29)
    c: Vertical(g29)
    c: Vertical(g31)
    c: Horizontal(g30)
    c: Horizontal(g32)
    c: Distance(g30,g32) = 1.6
    c: PointOnObject(g29,g-3)
    c: PointOnObject(g30,g20)
    c: Coincident(g33,g34)
    c: Coincident(g34,g35)
    c: Coincident(g35,g36)
    c: Coincident(g36,g33)
    c: Vertical(g33)
    c: Vertical(g35)
    c: Horizontal(g34)
    c: Horizontal(g36)
    c: Distance(g34,g36) = 1.6
    c: PointOnObject(g33,g-3)
    c: PointOnObject(g34,g20)
    c: DistanceY(g25,g29) = 1.6
    c: DistanceY(g29,g33) = 1.6
FEATURE [PartDesign::Pad] Pad143
  BaseFeature = -> Pocket036
  Direction = (1,0,0)
  Length = 3.2
  Length2 = 10
  Profile = -> Sketch172
  ReferenceAxis = -> Sketch172 [N_Axis]
  Refine = true
  Suppressed = false
  Type = 0
FEATURE [PartDesign::Pad] Pad144
  BaseFeature = -> Pad143
  Direction = (-1,0,0)
  Length = 131
  Length2 = 10
  Profile = -> Pad143 [Face63,Face83,Face88,Face93,Face98]
  Refine = true
  Suppressed = false
  Type = 0
FEATURE [PartDesign::Pad] Pad145
  BaseFeature = -> Pad144
  Direction = (0,1,0)
  Length = 135.8
  Length2 = 10
  Profile = -> Pad144 [Face54,Face56,Face58,Face60,Face62]
  Refine = true
  Suppressed = false
  Type = 0
FEATURE [Sketcher::SketchObject] Sketch173
  ArcFitTolerance = 1e-06
  AttachmentSupport = -> [Pad145]
  ExternalGeometry = -> [Pad145]
  FullyConstrained = true
  MakeInternals = false
  MapMode = 5
  Placement = pos=(-8e-16,0,0) rot=(0.57735,-0.57735,-0.57735;2.0944rad)
  sketch-geometry (16):
    g0: LineSegment StartX=-135.8 StartY=-28.8 StartZ=0 EndX=0 EndY=-28.8 EndZ=0
    g1: LineSegment StartX=0 StartY=-28.8 StartZ=0 EndX=0 EndY=-27.2 EndZ=0
    g2: LineSegment StartX=0 StartY=-27.2 StartZ=0 EndX=-135.8 EndY=-27.2 EndZ=0
    g3: LineSegment StartX=-135.8 StartY=-27.2 StartZ=0 EndX=-135.8 EndY=-28.8 EndZ=0
    g4: LineSegment StartX=-135.8 StartY=-25.6 StartZ=0 EndX=0 EndY=-25.6 EndZ=0
    g5: LineSegment StartX=0 StartY=-25.6 StartZ=0 EndX=0 EndY=-24 EndZ=0
    g6: LineSegment StartX=0 StartY=-24 StartZ=0 EndX=-135.8 EndY=-24 EndZ=0
    g7: LineSegment StartX=-135.8 StartY=-24 StartZ=0 EndX=-135.8 EndY=-25.6 EndZ=0
    g8: LineSegment StartX=-135.8 StartY=-22.4 StartZ=0 EndX=0 EndY=-22.4 EndZ=0
    g9: LineSegment StartX=0 StartY=-22.4 StartZ=0 EndX=0 EndY=-20.8 EndZ=0
    g10: LineSegment StartX=0 StartY=-20.8 StartZ=0 EndX=-135.8 EndY=-20.8 EndZ=0
    g11: LineSegment StartX=-135.8 StartY=-20.8 StartZ=0 EndX=-135.8 EndY=-22.4 EndZ=0
    g12: LineSegment StartX=-135.8 StartY=-19.2 StartZ=0 EndX=0 EndY=-19.2 EndZ=0
    g13: LineSegment StartX=0 StartY=-19.2 StartZ=0 EndX=0 EndY=-17.6 EndZ=0
    g14: LineSegment StartX=0 StartY=-17.6 StartZ=0 EndX=-135.8 EndY=-17.6 EndZ=0
    g15: LineSegment StartX=-135.8 StartY=-17.6 StartZ=0 EndX=-135.8 EndY=-19.2 EndZ=0
  constraints (47):
    c: Coincident(g0,g1)
    c: Coincident(g1,g2)
    c: Coincident(g2,g3)
    c: Coincident(g3,g0)
    c: Horizontal(g0)
    c: Horizontal(g2)
    c: Vertical(g1)
    c: Vertical(g3)
    c: Distance(g0,g2) = 1.6
    c: Coincident(g0,g-3)
    c: PointOnObject(g1,g-4)
    c: Coincident(g4,g5)
    c: Coincident(g5,g6)
    c: Coincident(g6,g7)
    c: Coincident(g7,g4)
    c: Horizontal(g4)
    c: Horizontal(g6)
    c: Vertical(g5)
    c: Vertical(g7)
    c: Distance(g4,g6) = 1.6
    c: PointOnObject(g4,g-3)
    c: PointOnObject(g5,g-4)
    c: Coincident(g8,g9)
    c: Coincident(g9,g10)
    c: Coincident(g10,g11)
    c: Coincident(g11,g8)
    c: Horizontal(g8)
    c: Horizontal(g10)
    c: Vertical(g9)
    c: Vertical(g11)
    c: Distance(g8,g10) = 1.6
    c: PointOnObject(g8,g-3)
    c: PointOnObject(g9,g-4)
    c: DistanceY(g2,g4) = 1.6
    c: DistanceY(g6,g8) = 1.6
    c: Coincident(g12,g13)
    c: Coincident(g13,g14)
    c: Coincident(g14,g15)
    c: Coincident(g15,g12)
    c: Horizontal(g12)
    c: Horizontal(g14)
    c: Vertical(g13)
    c: Vertical(g15)
    c: Distance(g12,g14) = 1.6
    c: PointOnObject(g12,g-3)
    c: PointOnObject(g13,g-4)
    c: DistanceY(g10,g12) = 1.6
FEATURE [PartDesign::Pad] Pad146
  BaseFeature = -> Pad145
  Direction = (-1,0,0)
  Length = 3.2
  Length2 = 10
  Profile = -> Sketch173
  ReferenceAxis = -> Sketch173 [N_Axis]
  Refine = true
  Suppressed = false
  Type = 0
FEATURE [Sketcher::SketchObject] Sketch174
  ArcFitTolerance = 1e-06
  AttachmentSupport = -> [Pad146]
  ExternalGeometry = -> [Pad146]
  FullyConstrained = true
  MakeInternals = false
  MapMode = 5
  Placement = pos=(0,135.8,-1.372e-13) rot=(0,0.707107,0.707107;3.14159rad)
  sketch-geometry (48):
    g0: LineSegment StartX=-131 StartY=-3.2 StartZ=0 EndX=-127.8 EndY=-3.2 EndZ=0
    g1: LineSegment StartX=-127.8 StartY=-3.2 StartZ=0 EndX=-127.8 EndY=-5.04752 EndZ=0
    g2: LineSegment StartX=-127.8 StartY=-5.04752 StartZ=0 EndX=-131 EndY=-3.2 EndZ=0
    g3: LineSegment StartX=-131 StartY=-6.4 StartZ=0 EndX=-127.8 EndY=-6.4 EndZ=0
    g4: LineSegment StartX=-127.8 StartY=-6.4 StartZ=0 EndX=-127.8 EndY=-8.24752 EndZ=0
    g5: LineSegment StartX=-127.8 StartY=-8.24752 StartZ=0 EndX=-131 EndY=-6.4 EndZ=0
    g6: LineSegment StartX=-131 StartY=-9.6 StartZ=0 EndX=-127.8 EndY=-9.6 EndZ=0
    g7: LineSegment StartX=-127.8 StartY=-9.6 StartZ=0 EndX=-127.8 EndY=-11.4475 EndZ=0
    g8: LineSegment StartX=-127.8 StartY=-11.4475 StartZ=0 EndX=-131 EndY=-9.6 EndZ=0
    g9: LineSegment StartX=-131 StartY=-12.8 StartZ=0 EndX=-127.8 EndY=-12.8 EndZ=0
    g10: LineSegment StartX=-127.8 StartY=-12.8 StartZ=0 EndX=-127.8 EndY=-14.6475 EndZ=0
    g11: LineSegment StartX=-127.8 StartY=-14.6475 StartZ=0 EndX=-131 EndY=-12.8 EndZ=0
    g12: LineSegment StartX=-131 StartY=-16 StartZ=0 EndX=-127.8 EndY=-16 EndZ=0
    g13: LineSegment StartX=-127.8 StartY=-16 StartZ=0 EndX=-127.8 EndY=-17.8475 EndZ=0
    g14: LineSegment StartX=-127.8 StartY=-17.8475 StartZ=0 EndX=-131 EndY=-16 EndZ=0
    g15: LineSegment StartX=-131 StartY=-19.2 StartZ=0 EndX=-127.8 EndY=-19.2 EndZ=0
    g16: LineSegment StartX=-127.8 StartY=-19.2 StartZ=0 EndX=-127.8 EndY=-21.0475 EndZ=0
    g17: LineSegment StartX=-127.8 StartY=-21.0475 StartZ=0 EndX=-131 EndY=-19.2 EndZ=0
    g18: LineSegment StartX=-131 StartY=-22.4 StartZ=0 EndX=-127.8 EndY=-22.4 EndZ=0
    g19: LineSegment StartX=-127.8 StartY=-22.4 StartZ=0 EndX=-127.8 EndY=-24.2475 EndZ=0
    g20: LineSegment StartX=-127.8 StartY=-24.2475 StartZ=0 EndX=-131 EndY=-22.4 EndZ=0
    g21: LineSegment StartX=-131 StartY=-25.6 StartZ=0 EndX=-127.8 EndY=-25.6 EndZ=0
    g22: LineSegment StartX=-127.8 StartY=-25.6 StartZ=0 EndX=-127.8 EndY=-27.4475 EndZ=0
    g23: LineSegment StartX=-127.8 StartY=-27.4475 StartZ=0 EndX=-131 EndY=-25.6 EndZ=0
    g24: LineSegment StartX=3.2 StartY=-3.2 StartZ=0 EndX=0 EndY=-3.2 EndZ=0
    g25: LineSegment StartX=0 StartY=-3.2 StartZ=0 EndX=0 EndY=-5.04752 EndZ=0
    g26: LineSegment StartX=0 StartY=-5.04752 StartZ=0 EndX=3.2 EndY=-3.2 EndZ=0
    g27: LineSegment StartX=3.2 StartY=-6.4 StartZ=0 EndX=0 EndY=-6.4 EndZ=0
    g28: LineSegment StartX=0 StartY=-6.4 StartZ=0 EndX=0 EndY=-8.24752 EndZ=0
    g29: LineSegment StartX=0 StartY=-8.24752 StartZ=0 EndX=3.2 EndY=-6.4 EndZ=0
    g30: LineSegment StartX=3.2 StartY=-9.6 StartZ=0 EndX=0 EndY=-9.6 EndZ=0
    g31: LineSegment StartX=0 StartY=-9.6 StartZ=0 EndX=0 EndY=-11.4475 EndZ=0
    g32: LineSegment StartX=0 StartY=-11.4475 StartZ=0 EndX=3.2 EndY=-9.6 EndZ=0
    g33: LineSegment StartX=3.2 StartY=-12.8 StartZ=0 EndX=0 EndY=-12.8 EndZ=0
    g34: LineSegment StartX=0 StartY=-12.8 StartZ=0 EndX=0 EndY=-14.6475 EndZ=0
    g35: LineSegment StartX=0 StartY=-14.6475 StartZ=0 EndX=3.2 EndY=-12.8 EndZ=0
    g36: LineSegment StartX=3.2 StartY=-16 StartZ=0 EndX=0 EndY=-16 EndZ=0
    g37: LineSegment StartX=0 StartY=-16 StartZ=0 EndX=0 EndY=-17.8475 EndZ=0
    g38: LineSegment StartX=0 StartY=-17.8475 StartZ=0 EndX=3.2 EndY=-16 EndZ=0
    g39: LineSegment StartX=3.2 StartY=-19.2 StartZ=0 EndX=9e-16 EndY=-19.2 EndZ=0
    g40: LineSegment StartX=9e-16 StartY=-19.2 StartZ=0 EndX=0 EndY=-21.0475 EndZ=0
    g41: LineSegment StartX=0 StartY=-21.0475 StartZ=0 EndX=3.2 EndY=-19.2 EndZ=0
    g42: LineSegment StartX=3.2 StartY=-22.4 StartZ=0 EndX=9e-16 EndY=-22.4 EndZ=0
    g43: LineSegment StartX=9e-16 StartY=-22.4 StartZ=0 EndX=0 EndY=-24.2475 EndZ=0
    g44: LineSegment StartX=0 StartY=-24.2475 StartZ=0 EndX=3.2 EndY=-22.4 EndZ=0
    g45: LineSegment StartX=3.2 StartY=-25.6 StartZ=0 EndX=9e-16 EndY=-25.6 EndZ=0
    g46: LineSegment StartX=9e-16 StartY=-25.6 StartZ=0 EndX=0 EndY=-27.4475 EndZ=0
    g47: LineSegment StartX=0 StartY=-27.4475 StartZ=0 EndX=3.2 EndY=-25.6 EndZ=0
  constraints (112):
    c: Coincident(g-3,g0)
    c: Coincident(g0,g-3)
    c: Coincident(g0,g1)
    c: Vertical(g1)
    c: Coincident(g1,g2)
    c: Coincident(g2,g0)
    c: Coincident(g-4,g3)
    c: Coincident(g3,g-4)
    c: Coincident(g3,g4)
    c: Vertical(g4)
    c: Coincident(g4,g5)
    c: Coincident(g5,g3)
    c: Coincident(g-5,g6)
    c: Coincident(g6,g-5)
    c: Coincident(g6,g7)
    c: Vertical(g7)
    c: Coincident(g7,g8)
    c: Coincident(g8,g6)
    c: Coincident(g-6,g9)
    c: Coincident(g9,g-6)
    c: Coincident(g9,g10)
    c: Vertical(g10)
    c: Coincident(g10,g11)
    c: Coincident(g11,g9)
    c: Coincident(g-7,g12)
    c: Coincident(g12,g-7)
    c: Coincident(g12,g13)
    c: Vertical(g13)
    c: Coincident(g13,g14)
    c: Coincident(g14,g12)
    c: Coincident(g-8,g15)
    c: Coincident(g15,g-8)
    c: Coincident(g15,g16)
    c: Vertical(g16)
    c: Coincident(g16,g17)
    c: Coincident(g17,g15)
    c: Coincident(g-9,g18)
    c: Coincident(g18,g-9)
    c: Coincident(g18,g19)
    c: Vertical(g19)
    c: Coincident(g19,g20)
    c: Coincident(g20,g18)
    c: Coincident(g-10,g21)
    c: Coincident(g21,g-10)
    c: Coincident(g21,g22)
    c: Vertical(g22)
    c: Coincident(g22,g23)
    c: Coincident(g23,g21)
    c: Coincident(g-11,g24)
    c: Coincident(g24,g-11)
    c: Coincident(g24,g25)
    c: PointOnObject(g25,g-2)
    c: Coincident(g25,g26)
    c: Coincident(g26,g24)
    c: Coincident(g-12,g27)
    c: Coincident(g27,g-12)
    c: Coincident(g27,g28)
    c: PointOnObject(g28,g-2)
    c: Coincident(g28,g29)
    c: Coincident(g29,g27)
    c: Coincident(g-13,g30)
    c: Coincident(g30,g-13)
    c: Coincident(g30,g31)
    c: PointOnObject(g31,g-2)
    c: Coincident(g31,g32)
    c: Coincident(g32,g30)
    c: Coincident(g-14,g33)
    c: Coincident(g33,g-14)
    c: Coincident(g33,g34)
    c: PointOnObject(g34,g-2)
    c: Coincident(g34,g35)
    c: Coincident(g35,g33)
    c: Coincident(g-15,g36)
    c: Coincident(g36,g-15)
    c: Coincident(g36,g37)
    c: PointOnObject(g37,g-2)
    c: Coincident(g37,g38)
    c: Coincident(g38,g36)
    c: Coincident(g-16,g39)
    c: Coincident(g39,g-16)
    c: Coincident(g39,g40)
    c: PointOnObject(g40,g-2)
    c: Coincident(g40,g41)
    c: Coincident(g41,g39)
    c: Coincident(g-17,g42)
    c: Coincident(g42,g-17)
    c: Coincident(g42,g43)
    c: PointOnObject(g43,g-2)
    c: Coincident(g43,g44)
    c: Coincident(g44,g42)
    c: Coincident(g-18,g45)
    c: Coincident(g45,g-18)
    c: Coincident(g45,g46)
    c: PointOnObject(g46,g-2)
    c: Coincident(g46,g47)
    c: Coincident(g47,g45)
    c: Angle(g47,g46) = 1.0472
    c: Angle(g44,g43) = 1.0472
    c: Angle(g41,g40) = 1.0472
    c: Angle(g38,g37) = 1.0472
    c: Angle(g35,g34) = 1.0472
    c: Angle(g32,g31) = 1.0472
    c: Angle(g29,g28) = 1.0472
    c: Angle(g26,g25) = 1.0472
    c: Angle(g22,g23) = 1.0472
    c: Angle(g19,g20) = 1.0472
    c: Angle(g16,g17) = 1.0472
    c: Angle(g13,g14) = 1.0472
    c: Angle(g10,g11) = 1.0472
    c: Angle(g7,g8) = 1.0472
    c: Angle(g4,g5) = 1.0472
    c: Angle(g1,g2) = 1.0472
FEATURE [PartDesign::Pad] Pad147
  BaseFeature = -> Pad146
  Direction = (0,1,-1.1e-15)
  Length = 135.8
  Length2 = 10
  Profile = -> Sketch174
  ReferenceAxis = -> Sketch174 [N_Axis]
  Refine = true
  Reversed = true
  Suppressed = false
  Type = 0
FEATURE [Sketcher::SketchObject] Sketch175
  ArcFitTolerance = 1e-06
  AttachmentSupport = -> [Pad147]
  ExternalGeometry = -> [Pad147]
  FullyConstrained = true
  MakeInternals = false
  MapMode = 5
  Placement = pos=(131,0,0) rot=(0.57735,0.57735,0.57735;2.0944rad)
  sketch-geometry (15):
    g0: LineSegment StartX=-3.2 StartY=-3.2 StartZ=0 EndX=-2.309e-13 EndY=-3.2 EndZ=0
    g1: LineSegment StartX=-2.309e-13 StartY=-3.2 StartZ=0 EndX=0 EndY=-5.04752 EndZ=0
    g2: LineSegment StartX=0 StartY=-5.04752 StartZ=0 EndX=-3.2 EndY=-3.2 EndZ=0
    g3: LineSegment StartX=-3.2 StartY=-6.4 StartZ=0 EndX=-2.345e-13 EndY=-6.4 EndZ=0
    g4: LineSegment StartX=-2.345e-13 StartY=-6.4 StartZ=0 EndX=0 EndY=-8.24752 EndZ=0
    g5: LineSegment StartX=0 StartY=-8.24752 StartZ=0 EndX=-3.2 EndY=-6.4 EndZ=0
    g6: LineSegment StartX=-3.2 StartY=-9.6 StartZ=0 EndX=-2.38e-13 EndY=-9.6 EndZ=0
    g7: LineSegment StartX=-2.38e-13 StartY=-9.6 StartZ=0 EndX=0 EndY=-11.4475 EndZ=0
    g8: LineSegment StartX=0 StartY=-11.4475 StartZ=0 EndX=-3.2 EndY=-9.6 EndZ=0
    g9: LineSegment StartX=-3.2 StartY=-12.8 StartZ=0 EndX=-2.416e-13 EndY=-12.8 EndZ=0
    g10: LineSegment StartX=-2.416e-13 StartY=-12.8 StartZ=0 EndX=0 EndY=-14.6475 EndZ=0
    g11: LineSegment StartX=0 StartY=-14.6475 StartZ=0 EndX=-3.2 EndY=-12.8 EndZ=0
    g12: LineSegment StartX=-3.2 StartY=-16 StartZ=0 EndX=-2.451e-13 EndY=-16 EndZ=0
    g13: LineSegment StartX=-2.451e-13 StartY=-16 StartZ=0 EndX=0 EndY=-17.8475 EndZ=0
    g14: LineSegment StartX=0 StartY=-17.8475 StartZ=0 EndX=-3.2 EndY=-16 EndZ=0
  constraints (35):
    c: Coincident(g-3,g0)
    c: Coincident(g0,g-3)
    c: Coincident(g0,g1)
    c: PointOnObject(g1,g-2)
    c: Coincident(g1,g2)
    c: Coincident(g2,g0)
    c: Coincident(g-4,g3)
    c: Coincident(g3,g-4)
    c: Coincident(g3,g4)
    c: PointOnObject(g4,g-2)
    c: Coincident(g4,g5)
    c: Coincident(g5,g3)
    c: Coincident(g-5,g6)
    c: Coincident(g6,g-5)
    c: Coincident(g6,g7)
    c: PointOnObject(g7,g-2)
    c: Coincident(g7,g8)
    c: Coincident(g8,g6)
    c: Coincident(g-6,g9)
    c: Coincident(g9,g-6)
    c: Coincident(g9,g10)
    c: PointOnObject(g10,g-2)
    c: Coincident(g10,g11)
    c: Coincident(g11,g9)
    c: Coincident(g-7,g12)
    c: Coincident(g12,g-7)
    c: Coincident(g12,g13)
    c: PointOnObject(g13,g-2)
    c: Coincident(g13,g14)
    c: Coincident(g14,g12)
    c: Angle(g13,g14) = 1.0472
    c: Angle(g10,g11) = 1.0472
    c: Angle(g7,g8) = 1.0472
    c: Angle(g4,g5) = 1.0472
    c: Angle(g1,g2) = 1.0472
FEATURE [PartDesign::Pad] Pad148
  BaseFeature = -> Pad147
  Direction = (1,0,0)
  Length = 134.2
  Length2 = 10
  Profile = -> Sketch175
  ReferenceAxis = -> Sketch175 [N_Axis]
  Refine = true
  Reversed = true
  Suppressed = false
  Type = 0
FEATURE [Sketcher::SketchObject] Sketch176
  ArcFitTolerance = 1e-06
  AttachmentSupport = -> [Pad148]
  ExternalGeometry = -> [Binder031,Pad148]
  FullyConstrained = true
  MakeInternals = false
  MapMode = 5
  Placement = pos=(131,0,0) rot=(0.57735,0.57735,0.57735;2.0944rad)
  sketch-geometry (20):
    g0: LineSegment StartX=120 StartY=0 StartZ=0 EndX=120 EndY=-28.8 EndZ=0
    g1: LineSegment StartX=120 StartY=-28.8 StartZ=0 EndX=135.8 EndY=-28.8 EndZ=0
    g2: LineSegment StartX=135.8 StartY=-28.8 StartZ=0 EndX=135.8 EndY=0 EndZ=0
    g3: LineSegment StartX=135.8 StartY=0 StartZ=0 EndX=120 EndY=0 EndZ=0
    g4: LineSegment StartX=88 StartY=2e-16 StartZ=0 EndX=88 EndY=-28.8 EndZ=0
    g5: LineSegment StartX=88 StartY=-28.8 StartZ=0 EndX=104 EndY=-28.8 EndZ=0
    g6: LineSegment StartX=104 StartY=-28.8 StartZ=0 EndX=104 EndY=0 EndZ=0
    g7: LineSegment StartX=104 StartY=2e-16 StartZ=0 EndX=88 EndY=2e-16 EndZ=0
    g8: LineSegment StartX=56 StartY=4e-16 StartZ=0 EndX=56 EndY=-28.8 EndZ=0
    g9: LineSegment StartX=56 StartY=-28.8 StartZ=0 EndX=72 EndY=-28.8 EndZ=0
    g10: LineSegment StartX=72 StartY=-28.8 StartZ=0 EndX=72 EndY=0 EndZ=0
    g11: LineSegment StartX=72 StartY=4e-16 StartZ=0 EndX=56 EndY=4e-16 EndZ=0
    g12: LineSegment StartX=24 StartY=2e-16 StartZ=0 EndX=24 EndY=-28.8 EndZ=0
    g13: LineSegment StartX=24 StartY=-28.8 StartZ=0 EndX=40 EndY=-28.8 EndZ=0
    g14: LineSegment StartX=40 StartY=-28.8 StartZ=0 EndX=40 EndY=0 EndZ=0
    g15: LineSegment StartX=40 StartY=2e-16 StartZ=0 EndX=24 EndY=2e-16 EndZ=0
    g16: LineSegment StartX=-16 StartY=0 StartZ=0 EndX=-16 EndY=-28.8 EndZ=0
    g17: LineSegment StartX=-16 StartY=-28.8 StartZ=0 EndX=8 EndY=-28.8 EndZ=0
    g18: LineSegment StartX=8 StartY=-28.8 StartZ=0 EndX=8 EndY=0 EndZ=0
    g19: LineSegment StartX=8 StartY=0 StartZ=0 EndX=-16 EndY=0 EndZ=0
  constraints (60):
    c: Coincident(g0,g1)
    c: Coincident(g1,g2)
    c: Coincident(g2,g3)
    c: Coincident(g3,g0)
    c: Vertical(g0)
    c: Vertical(g2)
    c: Horizontal(g1)
    c: Horizontal(g3)
    c: PointOnObject(g2,g-13)
    c: PointOnObject(g0,g-3)
    c: Coincident(g4,g5)
    c: Coincident(g5,g6)
    c: Coincident(g6,g7)
    c: Coincident(g7,g4)
    c: Vertical(g4)
    c: Vertical(g6)
    c: Horizontal(g5)
    c: Horizontal(g7)
    c: PointOnObject(g6,g3)
    c: PointOnObject(g6,g-4)
    c: PointOnObject(g5,g1)
    c: PointOnObject(g4,g-6)
    c: Coincident(g8,g9)
    c: Coincident(g9,g10)
    c: Coincident(g10,g11)
    c: Coincident(g11,g8)
    c: Vertical(g8)
    c: Vertical(g10)
    c: Horizontal(g9)
    c: Horizontal(g11)
    c: PointOnObject(g9,g-7)
    c: PointOnObject(g9,g5)
    c: PointOnObject(g10,g7)
    c: PointOnObject(g8,g-8)
    c: Coincident(g12,g13)
    c: Coincident(g13,g14)
    c: Coincident(g14,g15)
    c: Coincident(g15,g12)
    c: Vertical(g12)
    c: Vertical(g14)
    c: Horizontal(g13)
    c: Horizontal(g15)
    c: PointOnObject(g13,g-9)
    c: PointOnObject(g14,g11)
    c: PointOnObject(g13,g9)
    c: PointOnObject(g12,g-10)
    c: Coincident(g16,g17)
    c: Coincident(g17,g18)
    c: Coincident(g18,g19)
    c: Coincident(g19,g16)
    c: Vertical(g16)
    c: Vertical(g18)
    c: Horizontal(g17)
    c: Horizontal(g19)
    c: PointOnObject(g17,g-11)
    c: PointOnObject(g18,g15)
    c: PointOnObject(g17,g13)
    c: PointOnObject(g16,g-12)
    c: PointOnObject(g17,g-14)
    c: PointOnObject(g18,g-1)
FEATURE [PartDesign::Pocket] Pocket058
  BaseFeature = -> Pad148
  Direction = (-1,0,0)
  Length = 3.2
  Length2 = 5
  Profile = -> Sketch176
  ReferenceAxis = -> Sketch176 [N_Axis]
  Refine = true
  Suppressed = false
  Type = 0
FEATURE [Sketcher::SketchObject] Sketch177
  ArcFitTolerance = 1e-06
  AttachmentSupport = -> [Pocket058]
  ExternalGeometry = -> [Binder031,Pocket058]
  FullyConstrained = true
  MakeInternals = false
  MapMode = 5
  Placement = pos=(0,-3.2,0) rot=(1,0,0;1.5708rad)
  sketch-geometry (20):
    g0: LineSegment StartX=-16 StartY=-1.6 StartZ=0 EndX=-16 EndY=-17.8475 EndZ=0
    g1: LineSegment StartX=-16 StartY=-17.8475 StartZ=0 EndX=7 EndY=-17.8475 EndZ=0
    g2: LineSegment StartX=7 StartY=-17.8475 StartZ=0 EndX=7 EndY=-1.6 EndZ=0
    g3: LineSegment StartX=7 StartY=-1.6 StartZ=0 EndX=-16 EndY=-1.6 EndZ=0
    g4: LineSegment StartX=25 StartY=-1.6 StartZ=0 EndX=25 EndY=-17.8475 EndZ=0
    g5: LineSegment StartX=25 StartY=-17.8475 StartZ=0 EndX=39 EndY=-17.8475 EndZ=0
    g6: LineSegment StartX=39 StartY=-17.8475 StartZ=0 EndX=39 EndY=-1.6 EndZ=0
    g7: LineSegment StartX=39 StartY=-1.6 StartZ=0 EndX=25 EndY=-1.6 EndZ=0
    g8: LineSegment StartX=57 StartY=-1.6 StartZ=0 EndX=57 EndY=-17.8475 EndZ=0
    g9: LineSegment StartX=57 StartY=-17.8475 StartZ=0 EndX=71 EndY=-17.8475 EndZ=0
    g10: LineSegment StartX=71 StartY=-17.8475 StartZ=0 EndX=71 EndY=-1.6 EndZ=0
    g11: LineSegment StartX=71 StartY=-1.6 StartZ=0 EndX=57 EndY=-1.6 EndZ=0
    g12: LineSegment StartX=89 StartY=-1.6 StartZ=0 EndX=89 EndY=-17.8475 EndZ=0
    g13: LineSegment StartX=89 StartY=-17.8475 StartZ=0 EndX=103 EndY=-17.8475 EndZ=0
    g14: LineSegment StartX=103 StartY=-17.8475 StartZ=0 EndX=103 EndY=-1.6 EndZ=0
    g15: LineSegment StartX=103 StartY=-1.6 StartZ=0 EndX=89 EndY=-1.6 EndZ=0
    g16: LineSegment StartX=120.8 StartY=-1.6 StartZ=0 EndX=120.8 EndY=-17.8475 EndZ=0
    g17: LineSegment StartX=120.8 StartY=-17.8475 StartZ=0 EndX=143.8 EndY=-17.8475 EndZ=0
    g18: LineSegment StartX=143.8 StartY=-17.8475 StartZ=0 EndX=143.8 EndY=-1.6 EndZ=0
    g19: LineSegment StartX=143.8 StartY=-1.6 StartZ=0 EndX=120.8 EndY=-1.6 EndZ=0
  constraints (60):
    c: Coincident(g0,g1)
    c: Coincident(g1,g2)
    c: Coincident(g2,g3)
    c: Coincident(g3,g0)
    c: Vertical(g0)
    c: Vertical(g2)
    c: Horizontal(g1)
    c: Horizontal(g3)
    c: PointOnObject(g0,g-7)
    c: PointOnObject(g1,g-8)
    c: PointOnObject(g2,g-10)
    c: PointOnObject(g2,g-9)
    c: Coincident(g4,g5)
    c: Coincident(g5,g6)
    c: Coincident(g6,g7)
    c: Coincident(g7,g4)
    c: Vertical(g4)
    c: Vertical(g6)
    c: Horizontal(g5)
    c: Horizontal(g7)
    c: PointOnObject(g5,g-8)
    c: PointOnObject(g6,g-11)
    c: PointOnObject(g4,g-9)
    c: PointOnObject(g4,g-6)
    c: Coincident(g8,g9)
    c: Coincident(g9,g10)
    c: Coincident(g10,g11)
    c: Coincident(g11,g8)
    c: Vertical(g8)
    c: Vertical(g10)
    c: Horizontal(g9)
    c: Horizontal(g11)
    c: PointOnObject(g9,g-8)
    c: PointOnObject(g10,g-12)
    c: PointOnObject(g8,g-9)
    c: PointOnObject(g8,g-5)
    c: Coincident(g12,g13)
    c: Coincident(g13,g14)
    c: Coincident(g14,g15)
    c: Coincident(g15,g12)
    c: Vertical(g12)
    c: Vertical(g14)
    c: Horizontal(g13)
    c: Horizontal(g15)
    c: PointOnObject(g13,g-8)
    c: PointOnObject(g14,g-13)
    c: PointOnObject(g12,g-9)
    c: PointOnObject(g12,g-4)
    c: Coincident(g16,g17)
    c: Coincident(g17,g18)
    c: Coincident(g18,g19)
    c: Coincident(g19,g16)
    c: Vertical(g16)
    c: Vertical(g18)
    c: Horizontal(g17)
    c: Horizontal(g19)
    c: PointOnObject(g17,g-8)
    c: PointOnObject(g18,g-14)
    c: PointOnObject(g16,g-9)
    c: PointOnObject(g16,g-3)
FEATURE [PartDesign::Pocket] Pocket059
  BaseFeature = -> Pocket058
  Direction = (0,1,-2e-16)
  Length = 3.2
  Length2 = 5
  Profile = -> Sketch177
  ReferenceAxis = -> Sketch177 [N_Axis]
  Refine = true
  Suppressed = false
  Type = 0
FEATURE [Sketcher::SketchObject] Sketch178
  ArcFitTolerance = 1e-06
  AttachmentSupport = -> [Pocket059]
  ExternalGeometry = -> [Pocket059,Binder031]
  FullyConstrained = true
  MakeInternals = false
  MapMode = 5
  Placement = pos=(-3.2,0,4.6e-15) rot=(0.57735,-0.57735,-0.57735;2.0944rad)
  sketch-geometry (20):
    g0: LineSegment StartX=-135.8 StartY=-1.6 StartZ=0 EndX=-135.8 EndY=-28.8 EndZ=0
    g1: LineSegment StartX=-135.8 StartY=-28.8 StartZ=0 EndX=-120 EndY=-28.8 EndZ=0
    g2: LineSegment StartX=-120 StartY=-28.8 StartZ=0 EndX=-120 EndY=-1.6 EndZ=0
    g3: LineSegment StartX=-120 StartY=-1.6 StartZ=0 EndX=-135.8 EndY=-1.6 EndZ=0
    g4: LineSegment StartX=-104 StartY=-1.6 StartZ=0 EndX=-104 EndY=-28.8 EndZ=0
    g5: LineSegment StartX=-104 StartY=-28.8 StartZ=0 EndX=-88 EndY=-28.8 EndZ=0
    g6: LineSegment StartX=-88 StartY=-28.8 StartZ=0 EndX=-88 EndY=-1.6 EndZ=0
    g7: LineSegment StartX=-88 StartY=-1.6 StartZ=0 EndX=-104 EndY=-1.6 EndZ=0
    g8: LineSegment StartX=-72 StartY=-1.6 StartZ=0 EndX=-72 EndY=-28.8 EndZ=0
    g9: LineSegment StartX=-72 StartY=-28.8 StartZ=0 EndX=-56 EndY=-28.8 EndZ=0
    g10: LineSegment StartX=-56 StartY=-28.8 StartZ=0 EndX=-56 EndY=-1.6 EndZ=0
    g11: LineSegment StartX=-56 StartY=-1.6 StartZ=0 EndX=-72 EndY=-1.6 EndZ=0
    g12: LineSegment StartX=-40 StartY=-1.6 StartZ=0 EndX=-40 EndY=-28.8 EndZ=0
    g13: LineSegment StartX=-40 StartY=-28.8 StartZ=0 EndX=-24 EndY=-28.8 EndZ=0
    g14: LineSegment StartX=-24 StartY=-28.8 StartZ=0 EndX=-24 EndY=-1.6 EndZ=0
    g15: LineSegment StartX=-24 StartY=-1.6 StartZ=0 EndX=-40 EndY=-1.6 EndZ=0
    g16: LineSegment StartX=-8 StartY=-1.6 StartZ=0 EndX=-8 EndY=-28.8 EndZ=0
    g17: LineSegment StartX=-8 StartY=-28.8 StartZ=0 EndX=16 EndY=-28.8 EndZ=0
    g18: LineSegment StartX=16 StartY=-28.8 StartZ=0 EndX=16 EndY=-1.6 EndZ=0
    g19: LineSegment StartX=16 StartY=-1.6 StartZ=0 EndX=-8 EndY=-1.6 EndZ=0
  constraints (60):
    c: Coincident(g0,g1)
    c: Coincident(g1,g2)
    c: Coincident(g2,g3)
    c: Coincident(g3,g0)
    c: Vertical(g0)
    c: Vertical(g2)
    c: Horizontal(g1)
    c: Horizontal(g3)
    c: PointOnObject(g1,g-4)
    c: PointOnObject(g2,g-5)
    c: PointOnObject(g0,g-3)
    c: PointOnObject(g0,g-14)
    c: Coincident(g4,g5)
    c: Coincident(g5,g6)
    c: Coincident(g6,g7)
    c: Coincident(g7,g4)
    c: Vertical(g4)
    c: Vertical(g6)
    c: Horizontal(g5)
    c: Horizontal(g7)
    c: PointOnObject(g5,g-4)
    c: PointOnObject(g6,g-6)
    c: PointOnObject(g4,g-3)
    c: PointOnObject(g4,g-13)
    c: Coincident(g8,g9)
    c: Coincident(g9,g10)
    c: Coincident(g10,g11)
    c: Coincident(g11,g8)
    c: Vertical(g8)
    c: Vertical(g10)
    c: Horizontal(g9)
    c: Horizontal(g11)
    c: PointOnObject(g9,g-4)
    c: PointOnObject(g10,g-7)
    c: PointOnObject(g8,g-3)
    c: PointOnObject(g8,g-12)
    c: Coincident(g12,g13)
    c: Coincident(g13,g14)
    c: Coincident(g14,g15)
    c: Coincident(g15,g12)
    c: Vertical(g12)
    c: Vertical(g14)
    c: Horizontal(g13)
    c: Horizontal(g15)
    c: PointOnObject(g13,g-4)
    c: PointOnObject(g14,g-8)
    c: PointOnObject(g12,g-3)
    c: PointOnObject(g12,g-11)
    c: Coincident(g16,g17)
    c: Coincident(g17,g18)
    c: Coincident(g18,g19)
    c: Coincident(g19,g16)
    c: Vertical(g16)
    c: Vertical(g18)
    c: Horizontal(g17)
    c: Horizontal(g19)
    c: PointOnObject(g17,g-4)
    c: PointOnObject(g18,g-9)
    c: PointOnObject(g16,g-3)
    c: PointOnObject(g16,g-10)
FEATURE [PartDesign::Pocket] Pocket060
  BaseFeature = -> Pocket059
  Direction = (1,0,-1.3e-15)
  Length = 3.2
  Length2 = 5
  Profile = -> Sketch178
  ReferenceAxis = -> Sketch178 [N_Axis]
  Refine = true
  Suppressed = false
  Type = 0
FEATURE [PartDesign::Body] Body071  label="Base Revised"
  AllowCompound = false
  Group = -> [Clone004,Pocket036,Binder031,Sketch172,Pad143,Pad144,Pad145,Sketch173,Pad146,Sketch174,Pad147,Sketch175,Pad148,Sketch176,Pocket058,Sketch177,Pocket059,Sketch178,Pocket060]
  Origin = -> Origin352
  Tip = -> Pocket060
FEATURE [App::Part] Part001  label="Case"
  Group = -> [Body001,Body071,Body002,Body003,Body004,Body005,Body006,Body007,Body008,Body009,Body010,Body011,Body012,Body013,Body014]
  Origin = -> Origin288
FEATURE [TechDraw::DrawProjGroupItem] View004
  CoarseView = false
  Direction = (-0.122657,-0.869252,0.478912)
  Focus = 100
  HardHidden = false
  IsoCount = 0
  IsoHidden = false
  IsoVisible = false
  LockPosition = false
  Perspective = false
  Rotation = 0
  RotationVector = (1,0,0)
  ScaleType = 0
  ScrubCount = 1
  SeamHidden = false
  SeamVisible = true
  SmoothHidden = false
  SmoothVisible = true
  Source = -> [Body,Part001,Part,Body016,Body017,Body018]
  Type = 0
  X = 148.5
  XDirection = (0.969196,-0.208762,-0.130688)
  Y = 105
FEATURE [TechDraw::DrawPage] Page004  label="Colouring Export"
  KeepUpdated = true
  NextBalloonIndex = 1
  ProjectionType = 0
  Template = -> Template004
  Views = -> [View004]
